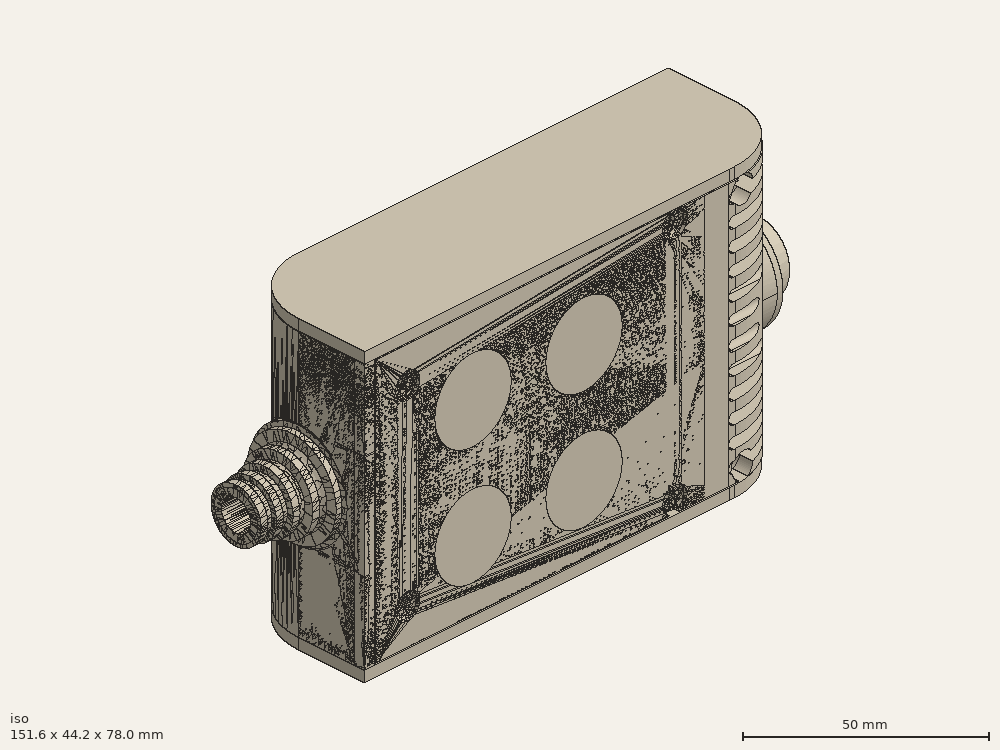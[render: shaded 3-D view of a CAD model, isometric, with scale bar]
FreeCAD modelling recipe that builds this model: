
FCSTD DOCUMENT  (FreeCAD 0.19R0.19.2)
Label: enclosure_194FCStd
License: All rights reserved
LicenseURL: http://en.wikipedia.org/wiki/All_rights_reserved
objects: Part::Revolution×152, Part::MultiFuse×146, Part::Feature×146, Sketcher::SketchObject×84, Part::Cut×70, Part::Cylinder×70, Part::Extrusion×67, Part::Fillet×58, Part::Box×36, App::MeasureDistance×4, PartDesign::Body×2, Image::ImagePlane×1
note: 831 computed .brp shape members not serialized (recipe doc carries the construction recipe); baked Part::Feature solids carry a one-line shape summary decoded from their .brp

FEATURE [Sketcher::SketchObject] Sketch  label="topSketch"
  FullyConstrained = true
  sketch-geometry (20):
    g0: LineSegment StartX=5.21097e-06 StartY=3 StartZ=0 EndX=5.21097e-06 EndY=19 EndZ=0
    g1: ArcOfCircle CenterX=19 CenterY=19 CenterZ=0 NormalX=0 NormalY=0 NormalZ=1 AngleXU=0 Radius=19 StartAngle=1.5708 EndAngle=3.14159
    g2: ArcOfCircle CenterX=19 CenterY=19 CenterZ=0 NormalX=0 NormalY=0 NormalZ=1 AngleXU=0 Radius=16 StartAngle=1.5708 EndAngle=3.14159
    g3: LineSegment StartX=114 StartY=35 StartZ=0 EndX=19 EndY=35 EndZ=0
    g4: LineSegment StartX=5.21097e-06 StartY=3 StartZ=0 EndX=5.21097e-06 EndY=0 EndZ=0
    g5: LineSegment StartX=3 StartY=0 StartZ=0 EndX=5.21097e-06 EndY=0 EndZ=0
    g6: LineSegment StartX=3 StartY=19 StartZ=0 EndX=3 EndY=0 EndZ=0
    g7: LineSegment StartX=19 StartY=38 StartZ=0 EndX=124 EndY=38 EndZ=0
    g8: Circle CenterX=119 CenterY=35 CenterZ=0 NormalX=0 NormalY=0 NormalZ=1 AngleXU=0 Radius=1
    g9: Circle CenterX=121 CenterY=35 CenterZ=0 NormalX=0 NormalY=0 NormalZ=1 AngleXU=0 Radius=1
    g10: Circle CenterX=121 CenterY=33 CenterZ=0 NormalX=0 NormalY=0 NormalZ=1 AngleXU=0 Radius=1
    g11: BSplineCurve PolesCount=3 KnotsCount=2 Degree=2 IsPeriodic=0
    g12: GeomPoint X=119 Y=35 Z=0
    g13: GeomPoint X=121 Y=33 Z=0
    g14: LineSegment StartX=119 StartY=35 StartZ=0 EndX=114 EndY=35 EndZ=0
    g15: ArcOfCircle CenterX=105 CenterY=19 CenterZ=0 NormalX=0 NormalY=0 NormalZ=1 AngleXU=0 Radius=19 StartAngle=5.7297 EndAngle=6.28319
    g16: ArcOfCircle CenterX=105 CenterY=19 CenterZ=0 NormalX=0 NormalY=0 NormalZ=1 AngleXU=0 Radius=16 StartAngle=5.60905 EndAngle=6.28319
    g17: LineSegment StartX=121 StartY=33 StartZ=0 EndX=121 EndY=19 EndZ=0
    g18: LineSegment StartX=124 StartY=38 StartZ=0 EndX=124 EndY=19 EndZ=0
    g19: LineSegment StartX=117.5 StartY=9.01251 StartZ=0 EndX=121.163 EndY=9.0125 EndZ=0
  constraints (46):
    c: Vertical(g0)
    c: Block(g0)
    c: Coincident(g1,g0)
    c: Block(g1)
    c: Coincident(g2,g1)
    c: Block(g2)
    c: Coincident(g3,g2)
    c: Horizontal(g3)
    c: Tangent(g3,g2)
    c: Coincident(g4,g0)
    c: Distance(g4) = 3
    c: Vertical(g4)
    c: Coincident(g5,g4)
    c: Horizontal(g5)
    c: Coincident(g6,g2)
    c: Coincident(g6,g5)
    c: Vertical(g6)
    c: Horizontal(g7)
    c: Distance(g7) = 105
    c: Coincident(g7,g1)
    c: Block(g3)
    c: Weight(g8) = 1
    c: Equal(g8,g9)
    c: Equal(g8,g10)
    c: InternalAlignment(g8,g11)
    c: InternalAlignment(g9,g11)
    c: InternalAlignment(g10,g11)
    c: InternalAlignment(g12,g11)
    c: InternalAlignment(g13,g11)
    c: Block(g11)
    c: Coincident(g14,g11)
    c: Coincident(g14,g3)
    c: Horizontal(g14)
    c: Block(g15)
    c: Coincident(g16,g15)
    c: Block(g16)
    c: Coincident(g17,g11)
    c: Coincident(g17,g16)
    c: Vertical(g17)
    c: Distance(g17) = 14
    c: Coincident(g18,g7)
    c: Coincident(g18,g15)
    c: Vertical(g18)
    c: Distance(g18) = 19
    c: Coincident(g19,g16)
    c: Coincident(g19,g15)
FEATURE [Sketcher::SketchObject] Sketch001  label="bottomSketch"
  FullyConstrained = true
  sketch-geometry (32):
    g0: LineSegment StartX=3.3 StartY=-6.03275e-07 StartZ=0 EndX=98 EndY=-6.03275e-07 EndZ=0
    g1: ArcOfCircle CenterX=98 CenterY=19 CenterZ=0 NormalX=0 NormalY=0 NormalZ=1 AngleXU=0 Radius=19 StartAngle=4.71239 EndAngle=5.71103
    g2: LineSegment StartX=6.3 StartY=8 StartZ=0 EndX=3.3 EndY=8 EndZ=0
    g3: LineSegment StartX=3.3 StartY=8 StartZ=0 EndX=3.3 EndY=-6.03275e-07 EndZ=0
    g4: ArcOfCircle CenterX=8.3 CenterY=5 CenterZ=0 NormalX=0 NormalY=0 NormalZ=1 AngleXU=0 Radius=2 StartAngle=3.14159 EndAngle=4.71239
    g5: LineSegment StartX=6.3 StartY=8 StartZ=0 EndX=6.3 EndY=5 EndZ=0
    g6: ArcOfCircle CenterX=98 CenterY=19 CenterZ=0 NormalX=0 NormalY=0 NormalZ=1 AngleXU=0 Radius=12.7 StartAngle=4.71239 EndAngle=6.28319
    g7: LineSegment StartX=94.7 StartY=3 StartZ=0 EndX=8.3 EndY=3 EndZ=0
    g8-g12: Circle x5 (B-spline internal-alignment scaffolding for g13; pole/knot coordinates omitted)
    g13: BSplineCurve PolesCount=5 KnotsCount=3 Degree=3 IsPeriodic=0
    g14: GeomPoint X=98 Y=6.3 Z=0
    g15: GeomPoint X=96.3938 Y=4.71946 Z=0
    g16: GeomPoint X=94.7 Y=3 Z=0
    g17-g23: Circle x7 (B-spline internal-alignment scaffolding for g24; pole/knot coordinates omitted)
    g24: BSplineCurve PolesCount=7 KnotsCount=5 Degree=3 IsPeriodic=0
    g25-g29: GeomPoint x5 (B-spline internal-alignment scaffolding for g24; pole/knot coordinates omitted)
    g30: ArcOfCircle CenterX=98 CenterY=19 CenterZ=0 NormalX=0 NormalY=0 NormalZ=1 AngleXU=0 Radius=15.7 StartAngle=5.81226 EndAngle=6.28319
    g31: LineSegment StartX=110.7 StartY=19 StartZ=0 EndX=113.7 EndY=19 EndZ=0
  constraints (41):
    c: Horizontal(g0)
    c: Coincident(g1,g0)
    c: Block(g1)
    c: Horizontal(g2)
    c: Distance(g2) = 3
    c: Coincident(g3,g2)
    c: Vertical(g3)
    c: Coincident(g3,g0)
    c: Block(g4)
    c: Block(g2)
    c: Coincident(g5,g2)
    c: Coincident(g5,g4)
    c: Vertical(g5)
    c: Coincident(g6,g1)
    c: Block(g6)
    c: Coincident(g7,g4)
    c: Horizontal(g7)
    c: Block(g0)
    c: Block(g7)
    c: Block(g3)
    c: Coincident(g13,g6)
    c: Weight(g8) = 1
    c: Equal(g8, g9-g12) x4
    c: Coincident(g13,g7)
    c: InternalAlignment(g8-g12 -> g13) x5
    c: InternalAlignment(g14,g13)
    c: InternalAlignment(g15,g13)
    c: InternalAlignment(g16,g13)
    c: Block(g13)
    c: Weight(g17) = 1
    c: Equal(g17, g18-g23) x6
    c: Coincident(g24,g1)
    c: InternalAlignment(g17-g23 -> g24) x7
    c: InternalAlignment(g25-g29 -> g24) x5
    c: Block(g24)
    c: Coincident(g30,g24)
    c: Coincident(g31,g6)
    c: Coincident(g31,g30)
    c: Horizontal(g31)
    c: Block(g31)
    c: Block(g30)
FEATURE [Part::Extrusion] Extrude  label="top"
  Base = -> Sketch
  Dir = (0,0,1)
  DirMode = 2
  FaceMakerClass = Part::FaceMakerBullseye
  LengthFwd = 72
  LengthRev = 0
  Solid = true
  Symmetric = false
FEATURE [Part::Extrusion] Extrude001  label="bottom"
  Base = -> Sketch001
  Dir = (0,0,1)
  DirMode = 2
  FaceMakerClass = Part::FaceMakerBullseye
  LengthFwd = 71.4
  LengthRev = 0
  Placement = pos=(0,0,0.3) rot=(0,0,1;0rad)
  Solid = true
  Symmetric = false
FEATURE [Sketcher::SketchObject] Sketch002  label="topSketch001"
  FullyConstrained = true
  sketch-geometry (8):
    g0: ArcOfCircle CenterX=19 CenterY=19.0975 CenterZ=0 NormalX=0 NormalY=0 NormalZ=1 AngleXU=0 Radius=18.9025 StartAngle=1.5708 EndAngle=3.14674
    g1: LineSegment StartX=0.0977805 StartY=19.0003 StartZ=0 EndX=0.0977805 EndY=0.000251602 EndZ=0
    g2: LineSegment StartX=19 StartY=38 StartZ=0 EndX=124 EndY=38 EndZ=0
    g3: LineSegment StartX=0.0977805 StartY=0.000251602 StartZ=0 EndX=105.098 EndY=0.000251602 EndZ=0
    g4: LineSegment StartX=124 StartY=38 StartZ=0 EndX=125.616 EndY=38 EndZ=0
    g5: LineSegment StartX=105.098 StartY=0.000251602 StartZ=0 EndX=106.713 EndY=0.000251602 EndZ=0
    g6: ArcOfCircle CenterX=106.616 CenterY=19 CenterZ=0 NormalX=0 NormalY=0 NormalZ=1 AngleXU=0 Radius=19 StartAngle=4.71754 EndAngle=6.28319
    g7: LineSegment StartX=125.616 StartY=38 StartZ=0 EndX=125.616 EndY=19 EndZ=0
  constraints (21):
    c: Block(g0)
    c: Coincident(g1,g0)
    c: Vertical(g1)
    c: Horizontal(g2)
    c: Distance(g2) = 105
    c: Coincident(g2,g0)
    c: Distance(g1) = 19
    c: Coincident(g3,g1)
    c: Horizontal(g3)
    c: Distance(g3) = 105
    c: Coincident(g4,g2)
    c: Horizontal(g4)
    c: Distance(g4) = 1.61553
    c: Horizontal(g5)
    c: Equal(g4,g5) = 1.61553
    c: Coincident(g5,g3)
    c: Block(g6)
    c: Coincident(g6,g5)
    c: Coincident(g7,g4)
    c: Coincident(g7,g6)
    c: Vertical(g7)
FEATURE [Part::Extrusion] Extrude002  label="sideA"
  Base = -> Sketch002
  Dir = (0,0,1)
  DirMode = 2
  FaceMakerClass = Part::FaceMakerBullseye
  LengthFwd = 3
  LengthRev = 0
  Placement = pos=(0,0,-3) rot=(0,0,1;0rad)
  Solid = true
  Symmetric = false
FEATURE [Sketcher::SketchObject] Sketch003  label="topSketch002"
  FullyConstrained = true
  sketch-geometry (6):
    g0: LineSegment StartX=19 StartY=38 StartZ=0 EndX=117 EndY=38 EndZ=0
    g1: ArcOfCircle CenterX=19 CenterY=19 CenterZ=0 NormalX=0 NormalY=0 NormalZ=1 AngleXU=0 Radius=19 StartAngle=1.5708 EndAngle=3.14159
    g2: LineSegment StartX=117 StartY=38 StartZ=0 EndX=117 EndY=19 EndZ=0
    g3: LineSegment StartX=98 StartY=1.0161e-12 StartZ=0 EndX=5.22862e-06 EndY=1.0161e-12 EndZ=0
    g4: LineSegment StartX=5.22862e-06 StartY=19 StartZ=0 EndX=5.22862e-06 EndY=1.0161e-12 EndZ=0
    g5: ArcOfCircle CenterX=98 CenterY=19 CenterZ=0 NormalX=0 NormalY=0 NormalZ=1 AngleXU=0 Radius=19 StartAngle=4.71239 EndAngle=6.28319
  constraints (16):
    c: Horizontal(g0)
    c: Distance(g0) = 98
    c: Coincident(g1,g0)
    c: Block(g1)
    c: Coincident(g2,g0)
    c: Vertical(g2)
    c: Distance(g2) = 19
    c: Horizontal(g3)
    c: Coincident(g4,g1)
    c: Vertical(g4)
    c: Coincident(g3,g4)
    c: Block(g3)
    c: Coincident(g5,g2)
    c: Coincident(g5,g3)
    c: Block(g0)
    c: Block(g5)
FEATURE [Sketcher::SketchObject] Sketch004
  FullyConstrained = true
  MapMode = 3
  Placement = pos=(0,0,0) rot=(1,0,0;1.5708rad)
  Support = -> [Extrude]
  sketch-geometry (8):
    g0: Circle CenterX=80.351 CenterY=-67.6202 CenterZ=0 NormalX=0 NormalY=0 NormalZ=1 AngleXU=0 Radius=2
    g1: Circle CenterX=80.351 CenterY=-67.6202 CenterZ=0 NormalX=0 NormalY=0 NormalZ=1 AngleXU=0 Radius=3
    g2: Circle CenterX=80.351 CenterY=-4.92017 CenterZ=0 NormalX=0 NormalY=0 NormalZ=1 AngleXU=0 Radius=2
    g3: Circle CenterX=80.351 CenterY=-4.92017 CenterZ=0 NormalX=0 NormalY=0 NormalZ=1 AngleXU=0 Radius=3
    g4: Circle CenterX=23.851 CenterY=-4.92017 CenterZ=0 NormalX=0 NormalY=0 NormalZ=1 AngleXU=0 Radius=2
    g5: Circle CenterX=23.851 CenterY=-4.92017 CenterZ=0 NormalX=0 NormalY=0 NormalZ=1 AngleXU=0 Radius=3
    g6: Circle CenterX=23.851 CenterY=-67.6202 CenterZ=0 NormalX=0 NormalY=0 NormalZ=1 AngleXU=0 Radius=2
    g7: Circle CenterX=23.851 CenterY=-67.6202 CenterZ=0 NormalX=0 NormalY=0 NormalZ=1 AngleXU=0 Radius=3
  constraints (8):
    c: Block(g3)
    c: Block(g2)
    c: Block(g1)
    c: Block(g0)
    c: Block(g6)
    c: Block(g7)
    c: Block(g4)
    c: Block(g5)
FEATURE [Part::Extrusion] Extrude004
  Base = -> Sketch004
  Dir = (0,-1,2e-16)
  DirMode = 2
  FaceMakerClass = Part::FaceMakerBullseye
  LengthFwd = 6
  LengthRev = 0
  Placement = pos=(0,9,0) rot=(0,0,1;0rad)
  Solid = true
  Symmetric = false
FEATURE [Sketcher::SketchObject] Sketch005
  FullyConstrained = true
  MapMode = 3
  Placement = pos=(0,0,0) rot=(1,0,0;1.5708rad)
  Support = -> [Extrude]
  sketch-geometry (8):
    g0: Circle CenterX=80.351 CenterY=-67.6202 CenterZ=0 NormalX=0 NormalY=0 NormalZ=1 AngleXU=0 Radius=3
    g1: Circle CenterX=80.351 CenterY=-4.92017 CenterZ=0 NormalX=0 NormalY=0 NormalZ=1 AngleXU=0 Radius=3
    g2: Circle CenterX=23.851 CenterY=-4.92017 CenterZ=0 NormalX=0 NormalY=0 NormalZ=1 AngleXU=0 Radius=3
    g3: Circle CenterX=23.851 CenterY=-67.6202 CenterZ=0 NormalX=0 NormalY=0 NormalZ=1 AngleXU=0 Radius=3
    g4: Circle CenterX=23.851 CenterY=-67.6202 CenterZ=0 NormalX=0 NormalY=0 NormalZ=1 AngleXU=0 Radius=5
    g5: Circle CenterX=80.351 CenterY=-67.6202 CenterZ=0 NormalX=0 NormalY=0 NormalZ=1 AngleXU=0 Radius=5
    g6: Circle CenterX=23.851 CenterY=-4.92017 CenterZ=0 NormalX=0 NormalY=0 NormalZ=1 AngleXU=0 Radius=5
    g7: Circle CenterX=80.351 CenterY=-4.92017 CenterZ=0 NormalX=0 NormalY=0 NormalZ=1 AngleXU=0 Radius=5
  constraints (8):
    c: Block(g1)
    c: Block(g0)
    c: Block(g3)
    c: Block(g2)
    c: Block(g5)
    c: Block(g4)
    c: Block(g6)
    c: Block(g7)
FEATURE [Part::Extrusion] Extrude005
  Base = -> Sketch005
  Dir = (0,-1,2e-16)
  DirMode = 2
  FaceMakerClass = Part::FaceMakerBullseye
  LengthFwd = 2
  LengthRev = 0
  Solid = true
  Symmetric = false
FEATURE [Sketcher::SketchObject] Sketch006
  FullyConstrained = true
  MapMode = 3
  Placement = pos=(0,0,0) rot=(1,0,0;1.5708rad)
  sketch-geometry (8):
    g0: Circle CenterX=80.351 CenterY=-67.6202 CenterZ=0 NormalX=0 NormalY=0 NormalZ=1 AngleXU=0 Radius=3
    g1: Circle CenterX=80.351 CenterY=-4.92017 CenterZ=0 NormalX=0 NormalY=0 NormalZ=1 AngleXU=0 Radius=3
    g2: Circle CenterX=23.851 CenterY=-4.92017 CenterZ=0 NormalX=0 NormalY=0 NormalZ=1 AngleXU=0 Radius=3
    g3: Circle CenterX=23.851 CenterY=-67.6202 CenterZ=0 NormalX=0 NormalY=0 NormalZ=1 AngleXU=0 Radius=3
    g4: Circle CenterX=23.851 CenterY=-67.6202 CenterZ=0 NormalX=0 NormalY=0 NormalZ=1 AngleXU=0 Radius=5
    g5: Circle CenterX=80.351 CenterY=-67.6202 CenterZ=0 NormalX=0 NormalY=0 NormalZ=1 AngleXU=0 Radius=5
    g6: Circle CenterX=23.851 CenterY=-4.92017 CenterZ=0 NormalX=0 NormalY=0 NormalZ=1 AngleXU=0 Radius=5
    g7: Circle CenterX=80.351 CenterY=-4.92017 CenterZ=0 NormalX=0 NormalY=0 NormalZ=1 AngleXU=0 Radius=5
  constraints (8):
    c: Block(g1)
    c: Block(g0)
    c: Block(g3)
    c: Block(g2)
    c: Block(g5)
    c: Block(g4)
    c: Block(g6)
    c: Block(g7)
FEATURE [Part::Extrusion] Extrude007
  Base = -> Sketch006
  Dir = (0,-1,2e-16)
  DirMode = 2
  FaceMakerClass = Part::FaceMakerBullseye
  LengthFwd = 2
  LengthRev = 0
  Solid = true
  Symmetric = false
FEATURE [Part::Fillet] Fillet
  Base = -> Extrude007
  Edges = 4 edges r=1.99: [Edge6,Edge12,Edge18,Edge24]
FEATURE [Part::Cut] Cut
  Base = -> Extrude005
  Placement = pos=(0,5,0) rot=(0,0,1;0rad)
  Tool = -> Fillet
FEATURE [Part::MultiFuse] Fusion  label="pCBScrews"
  Placement = pos=(-2.5,0,72.3) rot=(0,0,1;0rad)
  Shapes = -> [Extrude004,Cut]
FEATURE [App::MeasureDistance] Distance  label="Distance: 0.69 mm"
  Distance = 0.685967
  P1 = (24.0138,2.9647,0.3)
  P2 = (23.8901,3,-0.373787)
FEATURE [App::MeasureDistance] Distance001  label="Distance: 0.53 mm"
  Distance = 0.533607
  P1 = (80.2939,3,72.2334)
  P2 = (80.281,2.99661,71.7)
FEATURE [Part::Fillet] Fillet001
  Base = -> Extrude001
  Edges = 1 edges r=2.4: [Edge17]
FEATURE [Part::Fillet] Fillet002  label="bottom001"
  Base = -> Fillet001
  Edges = 1 edges r=2.4: [Edge36]
FEATURE [Part::Fillet] Fillet003  label="top001"
  Base = -> Extrude
  Edges = 1 edges r=2: [Edge1]
FEATURE [Sketcher::SketchObject] Sketch007
  FullyConstrained = true
  sketch-geometry (16):
    g0: LineSegment StartX=4 StartY=0 StartZ=0 EndX=4 EndY=2.4 EndZ=0
    g1: LineSegment StartX=4 StartY=2.4 StartZ=0 EndX=7 EndY=2.4 EndZ=0
    g2: LineSegment StartX=4 StartY=0 StartZ=0 EndX=5.7 EndY=0 EndZ=0
    g3: LineSegment StartX=5.7 StartY=0 StartZ=0 EndX=5.7 EndY=-5.6 EndZ=0
    g4-g8: Circle x5 (B-spline internal-alignment scaffolding for g9; pole/knot coordinates omitted)
    g9: BSplineCurve PolesCount=5 KnotsCount=3 Degree=3 IsPeriodic=0
    g10: GeomPoint X=7 Y=2.4 Z=0
    g11: GeomPoint X=10.4582 Y=-1.55472 Z=0
    g12: GeomPoint X=14 Y=-5.6 Z=0
    g13: LineSegment StartX=14 StartY=-5.6 StartZ=0 EndX=14 EndY=-14.1 EndZ=0
    g14: LineSegment StartX=14 StartY=-14.1 StartZ=0 EndX=6.5 EndY=-14.1 EndZ=0
    g15: LineSegment StartX=5.7 StartY=-5.6 StartZ=0 EndX=6.5 EndY=-14.1 EndZ=0
  constraints (28):
    c: Distance(g0) = 2.4
    c: Vertical(g0)
    c: Block(g0)
    c: Coincident(g1,g0)
    c: Horizontal(g1)
    c: Distance(g1) = 3
    c: Coincident(g2,g0)
    c: Horizontal(g2)
    c: Distance(g2) = 1.7
    c: Coincident(g3,g2)
    c: Vertical(g3)
    c: Distance(g3) = 5.6
    c: Coincident(g9,g1)
    c: Weight(g4) = 1
    c: Equal(g4, g5-g8) x4
    c: InternalAlignment(g4-g8 -> g9) x5
    c: InternalAlignment(g10,g9)
    c: InternalAlignment(g11,g9)
    c: InternalAlignment(g12,g9)
    c: Block(g9)
    c: Coincident(g13,g9)
    c: Vertical(g13)
    c: Distance(g13) = 8.5
    c: Coincident(g14,g13)
    c: Horizontal(g14)
    c: Distance(g14) = 7.5
    c: Coincident(g15,g3)
    c: Coincident(g15,g14)
FEATURE [Part::Feature] Face
  shape: bbox 10 x 16.5 x 2e-07 mm, 1 faces, 0 solids (baked)
FEATURE [Part::Revolution] Revolve  label="plugHousing"
  Angle = 360
  Axis = (0,1,0)
  Base = (0,0,0)
  FaceMakerClass = Part::FaceMakerBullseye
  Placement = pos=(0,0,36.15) rot=(0,0,1;0rad)
  Solid = false
  Source = -> Face
  Symmetric = false
FEATURE [Part::Feature] Face001
  shape: bbox 10 x 16.5 x 2e-07 mm, 1 faces, 0 solids (baked)
FEATURE [Part::Revolution] Revolve001  label="plugHousing001"
  Angle = 360
  Axis = (0,1,0)
  Base = (0,0,0)
  FaceMakerClass = Part::FaceMakerBullseye
  Placement = pos=(0,0,36.15) rot=(0,0,1;0rad)
  Solid = false
  Source = -> Face001
  Symmetric = false
FEATURE [Part::MultiFuse] Fusion001  label="plugHousing002"
  Placement = pos=(0,0,0) rot=(0,0,1;1.5708rad)
  Shapes = -> [Revolve001,Revolve]
FEATURE [Part::Feature] Face002
  shape: bbox 10 x 16.5 x 2e-07 mm, 1 faces, 0 solids (baked)
FEATURE [Part::Revolution] Revolve003  label="plugHousing005"
  Angle = 360
  Axis = (0,1,0)
  Base = (0,0,0)
  FaceMakerClass = Part::FaceMakerBullseye
  Placement = pos=(0,0,36.15) rot=(0,0,1;0rad)
  Solid = false
  Source = -> Face002
  Symmetric = false
FEATURE [Part::Feature] Face003
  shape: bbox 10 x 16.5 x 2e-07 mm, 1 faces, 0 solids (baked)
FEATURE [Part::Revolution] Revolve002  label="plugHousing003"
  Angle = 360
  Axis = (0,1,0)
  Base = (0,0,0)
  FaceMakerClass = Part::FaceMakerBullseye
  Placement = pos=(0,0,36.15) rot=(0,0,1;0rad)
  Solid = false
  Source = -> Face003
  Symmetric = false
FEATURE [Part::MultiFuse] Fusion002  label="plugHousing004"
  Placement = pos=(0,0,0) rot=(0,0,1;1.5708rad)
  Shapes = -> [Revolve002,Revolve003]
FEATURE [Part::MultiFuse] Fusion003  label="plugHousing006"
  Placement = pos=(0,19,0) rot=(0,0,1;3.14159rad)
  Shapes = -> [Fusion002,Fusion001]
FEATURE [Part::Feature] Face004
  shape: bbox 10 x 16.5 x 2e-07 mm, 1 faces, 0 solids (baked)
FEATURE [Part::Revolution] Revolve006  label="plugHousing010"
  Angle = 360
  Axis = (0,1,0)
  Base = (0,0,0)
  FaceMakerClass = Part::FaceMakerBullseye
  Placement = pos=(0,0,36.15) rot=(0,0,1;0rad)
  Solid = false
  Source = -> Face004
  Symmetric = false
FEATURE [Part::Feature] Face005
  shape: bbox 10 x 16.5 x 2e-07 mm, 1 faces, 0 solids (baked)
FEATURE [Part::Revolution] Revolve007  label="plugHousing011"
  Angle = 360
  Axis = (0,1,0)
  Base = (0,0,0)
  FaceMakerClass = Part::FaceMakerBullseye
  Placement = pos=(0,0,36.15) rot=(0,0,1;0rad)
  Solid = false
  Source = -> Face005
  Symmetric = false
FEATURE [Part::Feature] Face006
  shape: bbox 10 x 16.5 x 2e-07 mm, 1 faces, 0 solids (baked)
FEATURE [Part::Revolution] Revolve004  label="plugHousing007"
  Angle = 360
  Axis = (0,1,0)
  Base = (0,0,0)
  FaceMakerClass = Part::FaceMakerBullseye
  Placement = pos=(0,0,36.15) rot=(0,0,1;0rad)
  Solid = false
  Source = -> Face006
  Symmetric = false
FEATURE [Part::MultiFuse] Fusion004  label="plugHousing009"
  Placement = pos=(0,0,0) rot=(0,0,1;1.5708rad)
  Shapes = -> [Revolve004,Revolve007]
FEATURE [Part::Feature] Face007
  shape: bbox 10 x 16.5 x 2e-07 mm, 1 faces, 0 solids (baked)
FEATURE [Part::Revolution] Revolve005  label="plugHousing008"
  Angle = 360
  Axis = (0,1,0)
  Base = (0,0,0)
  FaceMakerClass = Part::FaceMakerBullseye
  Placement = pos=(0,0,36.15) rot=(0,0,1;0rad)
  Solid = false
  Source = -> Face007
  Symmetric = false
FEATURE [Part::MultiFuse] Fusion005  label="plugHousing012"
  Placement = pos=(0,0,0) rot=(0,0,1;1.5708rad)
  Shapes = -> [Revolve006,Revolve005]
FEATURE [Part::MultiFuse] Fusion006  label="plugHousing013"
  Placement = pos=(0,19,0) rot=(0,0,1;3.14159rad)
  Shapes = -> [Fusion005,Fusion004]
FEATURE [Part::MultiFuse] Fusion007  label="plugHousing014"
  Placement = pos=(122.621,0,-0.15) rot=(0,0,1;0rad)
  Shapes = -> [Fusion003,Fusion006]
FEATURE [Part::Cylinder] Cylinder002
  Angle = 360
  AttacherType = Attacher::AttachEngine3D
  Height = 20
  Placement = pos=(0,0,36.15) rot=(0,0,1;0rad)
  Radius = 4
FEATURE [Part::Cylinder] Cylinder003
  Angle = 360
  AttacherType = Attacher::AttachEngine3D
  Height = 10
  Placement = pos=(0,0,36.15) rot=(0,0,1;0rad)
  Radius = 4
FEATURE [Part::MultiFuse] Fusion009  label="removeToCreateHoleForPlugHousing"
  Placement = pos=(70,19,36.15) rot=(0,1,0;1.5708rad)
  Shapes = -> [Cylinder002,Cylinder003]
FEATURE [Part::Cylinder] Cylinder004
  Angle = 360
  AttacherType = Attacher::AttachEngine3D
  Height = 20
  Placement = pos=(0,0,36.15) rot=(0,0,1;0rad)
  Radius = 4
FEATURE [Part::Cylinder] Cylinder005
  Angle = 360
  AttacherType = Attacher::AttachEngine3D
  Height = 10
  Placement = pos=(0,0,36.15) rot=(0,0,1;0rad)
  Radius = 4
FEATURE [Part::MultiFuse] Fusion010  label="removeToCreateHoleForPlugHousing001"
  Placement = pos=(70,19,36.15) rot=(0,1,0;1.5708rad)
  Shapes = -> [Cylinder004,Cylinder005]
FEATURE [Part::Cut] Cut001
  Base = -> Fillet003
  Tool = -> Fusion010
FEATURE [Part::Cut] Cut002  label="Bottom"
  Base = -> Fillet002
  Tool = -> Fusion009
FEATURE [Part::Feature] Face008
  shape: bbox 10 x 16.5 x 2e-07 mm, 1 faces, 0 solids (baked)
FEATURE [Part::Revolution] Revolve011  label="plugHousing021"
  Angle = 360
  Axis = (0,1,0)
  Base = (0,0,0)
  FaceMakerClass = Part::FaceMakerBullseye
  Placement = pos=(0,0,36.15) rot=(0,0,1;0rad)
  Solid = false
  Source = -> Face008
  Symmetric = false
FEATURE [Part::Feature] Face009
  shape: bbox 10 x 16.5 x 2e-07 mm, 1 faces, 0 solids (baked)
FEATURE [Part::Revolution] Revolve012  label="plugHousing022"
  Angle = 360
  Axis = (0,1,0)
  Base = (0,0,0)
  FaceMakerClass = Part::FaceMakerBullseye
  Placement = pos=(0,0,36.15) rot=(0,0,1;0rad)
  Solid = false
  Source = -> Face009
  Symmetric = false
FEATURE [Part::Feature] Face010 .. Face013  x4 (patterned run collapsed; names and placements below)
  shape: bbox 10 x 16.5 x 2e-07 mm, 1 faces, 0 solids (baked)
FEATURE [Part::Revolution] Revolve015  label="plugHousing027"
  Angle = 360
  Axis = (0,1,0)
  Base = (0,0,0)
  FaceMakerClass = Part::FaceMakerBullseye
  Placement = pos=(0,0,36.15) rot=(0,0,1;0rad)
  Solid = false
  Source = -> Face013
  Symmetric = false
FEATURE [Part::Feature] Face014
  shape: bbox 10 x 16.5 x 2e-07 mm, 1 faces, 0 solids (baked)
FEATURE [Part::Feature] Face015
  shape: bbox 10 x 16.5 x 2e-07 mm, 1 faces, 0 solids (baked)
FEATURE [Part::Feature] Face016
  shape: bbox 10 x 16.5 x 2e-07 mm, 1 faces, 0 solids (baked)
FEATURE [Part::Revolution] Revolve019  label="plugHousing033"
  Angle = 360
  Axis = (0,1,0)
  Base = (0,0,0)
  FaceMakerClass = Part::FaceMakerBullseye
  Placement = pos=(0,0,36.15) rot=(0,0,1;0rad)
  Solid = false
  Source = -> Face016
  Symmetric = false
FEATURE [Part::Feature] Face017
  shape: bbox 10 x 16.5 x 2e-07 mm, 1 faces, 0 solids (baked)
FEATURE [Part::Revolution] Revolve020  label="plugHousing034"
  Angle = 360
  Axis = (0,1,0)
  Base = (0,0,0)
  FaceMakerClass = Part::FaceMakerBullseye
  Placement = pos=(0,0,36.15) rot=(0,0,1;0rad)
  Solid = false
  Source = -> Face017
  Symmetric = false
FEATURE [Part::Feature] Face018
  shape: bbox 10 x 16.5 x 2e-07 mm, 1 faces, 0 solids (baked)
FEATURE [Part::Revolution] Revolve016  label="plugHousing030"
  Angle = 360
  Axis = (0,1,0)
  Base = (0,0,0)
  FaceMakerClass = Part::FaceMakerBullseye
  Placement = pos=(0,0,36.15) rot=(0,0,1;0rad)
  Solid = false
  Source = -> Face018
  Symmetric = false
FEATURE [Part::MultiFuse] Fusion020  label="plugHousing038"
  Placement = pos=(0,0,0) rot=(0,0,1;1.5708rad)
  Shapes = -> [Revolve016,Revolve020]
FEATURE [Part::Feature] Face019
  shape: bbox 10 x 16.5 x 2e-07 mm, 1 faces, 0 solids (baked)
FEATURE [Part::Feature] Face020
  shape: bbox 10 x 16.5 x 2e-07 mm, 1 faces, 0 solids (baked)
FEATURE [Part::Revolution] Revolve017  label="plugHousing031"
  Angle = 360
  Axis = (0,1,0)
  Base = (0,0,0)
  FaceMakerClass = Part::FaceMakerBullseye
  Placement = pos=(0,0,36.15) rot=(0,0,1;0rad)
  Solid = false
  Source = -> Face020
  Symmetric = false
FEATURE [Part::MultiFuse] Fusion021  label="plugHousing039"
  Placement = pos=(0,0,0) rot=(0,0,1;1.5708rad)
  Shapes = -> [Revolve019,Revolve017]
FEATURE [Part::MultiFuse] Fusion023  label="plugHousing041"
  Placement = pos=(0,19,0) rot=(0,0,1;3.14159rad)
  Shapes = -> [Fusion021,Fusion020]
FEATURE [Part::Revolution] Revolve022  label="plugHousing043"
  Angle = 360
  Axis = (0,1,0)
  Base = (0,0,0)
  FaceMakerClass = Part::FaceMakerBullseye
  Placement = pos=(0,0,36.15) rot=(0,0,1;0rad)
  Solid = false
  Source = -> Face019
  Symmetric = false
FEATURE [Part::Feature] Face021
  shape: bbox 10 x 16.5 x 2e-07 mm, 1 faces, 0 solids (baked)
FEATURE [Part::Revolution] Revolve023  label="plugHousing044"
  Angle = 360
  Axis = (0,1,0)
  Base = (0,0,0)
  FaceMakerClass = Part::FaceMakerBullseye
  Placement = pos=(0,0,36.15) rot=(0,0,1;0rad)
  Solid = false
  Source = -> Face021
  Symmetric = false
FEATURE [Part::Feature] Face022
  shape: bbox 10 x 16.5 x 2e-07 mm, 1 faces, 0 solids (baked)
FEATURE [Part::Revolution] Revolve018  label="plugHousing032"
  Angle = 360
  Axis = (0,1,0)
  Base = (0,0,0)
  FaceMakerClass = Part::FaceMakerBullseye
  Placement = pos=(0,0,36.15) rot=(0,0,1;0rad)
  Solid = false
  Source = -> Face022
  Symmetric = false
FEATURE [Part::MultiFuse] Fusion022  label="plugHousing040"
  Placement = pos=(0,0,0) rot=(0,0,1;1.5708rad)
  Shapes = -> [Revolve018,Revolve023]
FEATURE [Part::Feature] Face023
  shape: bbox 10 x 16.5 x 2e-07 mm, 1 faces, 0 solids (baked)
FEATURE [Part::Revolution] Revolve021  label="plugHousing035"
  Angle = 360
  Axis = (0,1,0)
  Base = (0,0,0)
  FaceMakerClass = Part::FaceMakerBullseye
  Placement = pos=(0,0,36.15) rot=(0,0,1;0rad)
  Solid = false
  Source = -> Face023
  Symmetric = false
FEATURE [Part::MultiFuse] Fusion018  label="plugHousing036"
  Placement = pos=(0,0,0) rot=(0,0,1;1.5708rad)
  Shapes = -> [Revolve022,Revolve021]
FEATURE [Part::MultiFuse] Fusion019  label="plugHousing037"
  Placement = pos=(0,19,0) rot=(0,0,1;3.14159rad)
  Shapes = -> [Fusion018,Fusion022]
FEATURE [Part::MultiFuse] Fusion024  label="plugHousing042"
  Placement = pos=(122.621,0,-0.15) rot=(0,0,1;0rad)
  Shapes = -> [Fusion023,Fusion019]
FEATURE [Part::Cylinder] Cylinder006
  Angle = 360
  AttacherType = Attacher::AttachEngine3D
  Height = 20
  Placement = pos=(0,0,36.15) rot=(0,0,1;0rad)
  Radius = 14.3
FEATURE [Part::Cylinder] Cylinder007
  Angle = 360
  AttacherType = Attacher::AttachEngine3D
  Height = 10
  Placement = pos=(0,0,36.15) rot=(0,0,1;0rad)
  Radius = 4
FEATURE [Part::MultiFuse] Fusion026  label="removeToCreteHoleForPlugHousing"
  Placement = pos=(70,19,36) rot=(0,1,0;1.5708rad)
  Shapes = -> [Cylinder006,Cylinder007]
FEATURE [Part::Box] Box001  label="Cube001"
  AttacherType = Attacher::AttachEngine3D
  Height = 28
  Length = 3
  Placement = pos=(110.7,19,22) rot=(0,0,1;0rad)
  Width = 15.7
FEATURE [Part::Cut] Cut003  label="top002"
  Base = -> Cut001
  Tool = -> Fusion007
FEATURE [Part::Revolution] Revolve008  label="plugHousing015"
  Angle = 360
  Axis = (0,1,0)
  Base = (0,0,0)
  FaceMakerClass = Part::FaceMakerBullseye
  Placement = pos=(0,0,36.15) rot=(0,0,1;0rad)
  Solid = false
  Source = -> Face010
  Symmetric = false
FEATURE [Part::MultiFuse] Fusion013  label="plugHousing020"
  Placement = pos=(0,0,0) rot=(0,0,1;1.5708rad)
  Shapes = -> [Revolve008,Revolve012]
FEATURE [Part::Cut] Cut004  label="top003"
  Base = -> Cut003
  Placement = pos=(1,0,0) rot=(0,0,1;0rad)
  Tool = -> Fusion026
FEATURE [Part::Cylinder] Cylinder008
  Angle = 360
  AttacherType = Attacher::AttachEngine3D
  Height = 20
  Placement = pos=(0,0,36.15) rot=(0,0,1;0rad)
  Radius = 10.3
FEATURE [Part::Cylinder] Cylinder009
  Angle = 360
  AttacherType = Attacher::AttachEngine3D
  Height = 10
  Placement = pos=(0,0,36.15) rot=(0,0,1;0rad)
  Radius = 4
FEATURE [Part::MultiFuse] Fusion027  label="removeToCreteHoleForPlugHousing001"
  Placement = pos=(70,19,36) rot=(0,1,0;1.5708rad)
  Shapes = -> [Cylinder008,Cylinder009]
FEATURE [Part::Cut] Cut005  label="plugHousingTab"
  Base = -> Box001
  Tool = -> Fusion027
FEATURE [Part::MultiFuse] Fusion028  label="plugHousing045"
  Shapes = -> [Fusion024,Cut005]
FEATURE [Part::Box] Box002  label="Cube002"
  AttacherType = Attacher::AttachEngine3D
  Height = 28.8
  Length = 3
  Placement = pos=(107.3,28,21.6) rot=(0,0,1;0rad)
  Width = 7
FEATURE [Part::Box] Box003  label="Cube003"
  AttacherType = Attacher::AttachEngine3D
  Height = 3
  Length = 6.4
  Placement = pos=(107.3,28,18.6) rot=(0,0,1;0rad)
  Width = 7
FEATURE [Part::Box] Box004  label="Cube004"
  AttacherType = Attacher::AttachEngine3D
  Height = 3
  Length = 6.4
  Placement = pos=(107.3,28,50.4) rot=(0,0,1;0rad)
  Width = 7
FEATURE [Part::MultiFuse] Fusion029  label="plugHousingBracketHolder"
  Shapes = -> [Box004,Box002,Box003]
FEATURE [Part::Cylinder] Cylinder010
  Angle = 360
  AttacherType = Attacher::AttachEngine3D
  Height = 20
  Placement = pos=(0,0,36.15) rot=(0,0,1;0rad)
  Radius = 14.3
FEATURE [Part::Cylinder] Cylinder011
  Angle = 360
  AttacherType = Attacher::AttachEngine3D
  Height = 10
  Placement = pos=(0,0,36.15) rot=(0,0,1;0rad)
  Radius = 4
FEATURE [Part::MultiFuse] Fusion030  label="removeToCreteHoleForPlugHousing002"
  Placement = pos=(70,19,36) rot=(0,1,0;1.5708rad)
  Shapes = -> [Cylinder010,Cylinder011]
FEATURE [Part::Cut] Cut006  label="plugHousingBracketHolder001"
  Base = -> Fusion029
  Tool = -> Fusion030
FEATURE [Part::Cylinder] Cylinder012
  Angle = 360
  AttacherType = Attacher::AttachEngine3D
  Height = 20
  Placement = pos=(0,0,36.15) rot=(0,0,1;0rad)
  Radius = 7
FEATURE [Part::Cylinder] Cylinder013
  Angle = 360
  AttacherType = Attacher::AttachEngine3D
  Height = 10
  Placement = pos=(0,0,36.15) rot=(0,0,1;0rad)
  Radius = 4
FEATURE [Part::MultiFuse] Fusion032  label="removeToCreteHoleForPlugHousing003"
  Placement = pos=(70,19,36) rot=(0,1,0;1.5708rad)
  Shapes = -> [Cylinder012,Cylinder013]
FEATURE [Part::Cut] Cut007  label="bottom002"
  Base = -> Cut002
  Tool = -> Fusion032
FEATURE [Sketcher::SketchObject] Sketch008
  FullyConstrained = true
  sketch-geometry (54):
    g0: LineSegment StartX=-4.2 StartY=0 StartZ=0 EndX=-6.2 EndY=0 EndZ=0
    g1: LineSegment StartX=-14 StartY=-18 StartZ=0 EndX=-14 EndY=-26.5 EndZ=0
    g2: LineSegment StartX=-4.2 StartY=0 StartZ=0 EndX=-4.2 EndY=-13.4877 EndZ=0
    g3: Circle CenterX=-4.2 CenterY=-13.4877 CenterZ=0 NormalX=0 NormalY=0 NormalZ=1 AngleXU=0 Radius=1
    g4: Circle CenterX=-4.2 CenterY=-26.5 CenterZ=0 NormalX=0 NormalY=0 NormalZ=1 AngleXU=0 Radius=1
    g5: Circle CenterX=-8.2 CenterY=-26.5 CenterZ=0 NormalX=0 NormalY=0 NormalZ=1 AngleXU=0 Radius=1
    g6: BSplineCurve PolesCount=3 KnotsCount=2 Degree=2 IsPeriodic=0
    g7: GeomPoint X=-4.2 Y=-13.4877 Z=0
    g8: GeomPoint X=-8.2 Y=-26.5 Z=0
    g9: LineSegment StartX=-14 StartY=-26.5 StartZ=0 EndX=-8.2 EndY=-26.5 EndZ=0
    g10: LineSegment StartX=-10.15 StartY=-12 StartZ=0 EndX=-10.15 EndY=-14 EndZ=0
    g11: LineSegment StartX=-12.8401 StartY=-16 StartZ=0 EndX=-10.1571 EndY=-16 EndZ=0
    g12: LineSegment StartX=-10.15 StartY=-14 StartZ=0 EndX=-8.70761 EndY=-14 EndZ=0
    g13: LineSegment StartX=-12.8401 StartY=-16 StartZ=0 EndX=-12.8401 EndY=-17.6958 EndZ=0
    g14: LineSegment StartX=-10.15 StartY=-12 StartZ=0 EndX=-7.79258 EndY=-12 EndZ=0
    g15: Circle CenterX=-6.2215 CenterY=-2 CenterZ=0 NormalX=0 NormalY=0 NormalZ=1 AngleXU=0 Radius=1
    g16: Circle CenterX=-6.22762 CenterY=-2.58724 CenterZ=0 NormalX=0 NormalY=0 NormalZ=1 AngleXU=0 Radius=1
    g17: Circle CenterX=-6.32538 CenterY=-4 CenterZ=0 NormalX=0 NormalY=0 NormalZ=1 AngleXU=0 Radius=1
    g18: BSplineCurve PolesCount=3 KnotsCount=2 Degree=2 IsPeriodic=0
    g19: GeomPoint X=-6.2215 Y=-2 Z=0
    g20: GeomPoint X=-6.32538 Y=-4 Z=0
    g21: Circle CenterX=-6.48644 CenterY=-5.99526 CenterZ=0 NormalX=0 NormalY=0 NormalZ=1 AngleXU=0 Radius=1
    g22: Circle CenterX=-6.58486 CenterY=-6.99526 CenterZ=0 NormalX=0 NormalY=0 NormalZ=1 AngleXU=0 Radius=1
    g23: Circle CenterX=-6.77343 CenterY=-8 CenterZ=0 NormalX=0 NormalY=0 NormalZ=1 AngleXU=0 Radius=1
    g24: BSplineCurve PolesCount=3 KnotsCount=2 Degree=2 IsPeriodic=0
    g25: GeomPoint X=-6.48644 Y=-5.99526 Z=0
    g26: GeomPoint X=-6.77343 Y=-8 Z=0
    g27: Circle CenterX=-7.19003 CenterY=-10 CenterZ=0 NormalX=0 NormalY=0 NormalZ=1 AngleXU=0 Radius=1
    g28: Circle CenterX=-7.44407 CenterY=-11.0915 CenterZ=0 NormalX=0 NormalY=0 NormalZ=1 AngleXU=0 Radius=1
    g29: Circle CenterX=-7.79258 CenterY=-12 CenterZ=0 NormalX=0 NormalY=0 NormalZ=1 AngleXU=0 Radius=1
    g30: BSplineCurve PolesCount=3 KnotsCount=2 Degree=2 IsPeriodic=0
    g31: GeomPoint X=-7.19003 Y=-10 Z=0
    g32: GeomPoint X=-7.79258 Y=-12 Z=0
    g33: Circle CenterX=-8.70761 CenterY=-14 CenterZ=0 NormalX=0 NormalY=0 NormalZ=1 AngleXU=0 Radius=1
    g34: Circle CenterX=-9.33087 CenterY=-15.1837 CenterZ=0 NormalX=0 NormalY=0 NormalZ=1 AngleXU=0 Radius=1
    g35: Circle CenterX=-10.1571 CenterY=-16 CenterZ=0 NormalX=0 NormalY=0 NormalZ=1 AngleXU=0 Radius=1
    g36: BSplineCurve PolesCount=3 KnotsCount=2 Degree=2 IsPeriodic=0
    g37: GeomPoint X=-8.70761 Y=-14 Z=0
    g38: GeomPoint X=-10.1571 Y=-16 Z=0
    g39: Circle CenterX=-12.8401 CenterY=-17.6958 CenterZ=0 NormalX=0 NormalY=0 NormalZ=1 AngleXU=0 Radius=1
    g40: Circle CenterX=-13.3521 CenterY=-17.9027 CenterZ=0 NormalX=0 NormalY=0 NormalZ=1 AngleXU=0 Radius=1
    g41: Circle CenterX=-14 CenterY=-18 CenterZ=0 NormalX=0 NormalY=0 NormalZ=1 AngleXU=0 Radius=1
    g42: BSplineCurve PolesCount=3 KnotsCount=2 Degree=2 IsPeriodic=0
    g43: GeomPoint X=-12.8401 Y=-17.6958 Z=0
    g44: GeomPoint X=-14 Y=-18 Z=0
    g45: LineSegment StartX=-6.2 StartY=0 StartZ=0 EndX=-7.2 EndY=0 EndZ=0
    g46: LineSegment StartX=-7.2 StartY=0 StartZ=0 EndX=-7.2 EndY=-2 EndZ=0
    g47: LineSegment StartX=-7.2 StartY=-2 StartZ=0 EndX=-6.2215 EndY=-2 EndZ=0
    g48: LineSegment StartX=-6.32538 StartY=-4 StartZ=0 EndX=-7.65538 EndY=-4 EndZ=0
    g49: LineSegment StartX=-7.65538 StartY=-4 StartZ=0 EndX=-7.65538 EndY=-5.99526 EndZ=0
    g50: LineSegment StartX=-7.65538 StartY=-5.99526 StartZ=0 EndX=-6.48644 EndY=-5.99526 EndZ=0
    g51: LineSegment StartX=-6.77343 StartY=-8 StartZ=0 EndX=-8.43343 EndY=-8 EndZ=0
    g52: LineSegment StartX=-8.43343 StartY=-8 StartZ=0 EndX=-8.43343 EndY=-10 EndZ=0
    g53: LineSegment StartX=-8.43343 StartY=-10 StartZ=0 EndX=-7.19003 EndY=-10 EndZ=0
  constraints (112):
    c: Horizontal(g0)
    c: Distance(g0) = 2
    c: Block(g0)
    c: Vertical(g1)
    c: Coincident(g2,g0)
    c: Vertical(g2)
    c: Block(g2)
    c: Coincident(g6,g2)
    c: Weight(g3) = 1
    c: Equal(g3,g4)
    c: Equal(g3,g5)
    c: InternalAlignment(g3,g6)
    c: InternalAlignment(g4,g6)
    c: InternalAlignment(g5,g6)
    c: InternalAlignment(g7,g6)
    c: InternalAlignment(g8,g6)
    c: Block(g6)
    c: Coincident(g9,g1)
    c: Coincident(g9,g6)
    c: Horizontal(g9)
    c: Vertical(g10)
    c: Block(g10)
    c: Horizontal(g11)
    c: Block(g11)
    c: Coincident(g12,g10)
    c: Horizontal(g12)
    c: Block(g12)
    c: Coincident(g13,g11)
    c: Vertical(g13)
    c: Block(g13)
    c: Coincident(g14,g10)
    c: Horizontal(g14)
    c: Block(g14)
    c: Block(g9)
    c: Block(g1)
    c: Weight(g15) = 1
    c: Equal(g15,g16)
    c: Equal(g15,g17)
    c: InternalAlignment(g15,g18)
    c: InternalAlignment(g16,g18)
    c: InternalAlignment(g17,g18)
    c: InternalAlignment(g19,g18)
    c: InternalAlignment(g20,g18)
    c: Weight(g21) = 1
    c: Equal(g21,g22)
    c: Equal(g21,g23)
    c: InternalAlignment(g21,g24)
    c: InternalAlignment(g22,g24)
    c: InternalAlignment(g23,g24)
    c: InternalAlignment(g25,g24)
    c: InternalAlignment(g26,g24)
    c: Weight(g27) = 1
    c: Equal(g27,g28)
    c: Equal(g27,g29)
    c: Coincident(g30,g14)
    c: InternalAlignment(g27,g30)
    c: InternalAlignment(g28,g30)
    c: InternalAlignment(g29,g30)
    c: InternalAlignment(g31,g30)
    c: InternalAlignment(g32,g30)
    c: Coincident(g36,g12)
    c: Weight(g33) = 1
    c: Equal(g33,g34)
    c: Equal(g33,g35)
    c: Coincident(g36,g11)
    c: InternalAlignment(g33,g36)
    c: InternalAlignment(g34,g36)
    c: InternalAlignment(g35,g36)
    c: InternalAlignment(g37,g36)
    c: InternalAlignment(g38,g36)
    c: Coincident(g42,g13)
    c: Weight(g39) = 1
    c: Equal(g39,g40)
    c: Equal(g39,g41)
    c: Coincident(g42,g1)
    c: InternalAlignment(g39,g42)
    c: InternalAlignment(g40,g42)
    c: InternalAlignment(g41,g42)
    c: InternalAlignment(g43,g42)
    c: InternalAlignment(g44,g42)
    c: Block(g18)
    c: Block(g24)
    c: Block(g30)
    c: Block(g36)
    c: Block(g42)
    c: Horizontal(g45)
    c: Coincident(g45,g0)
    c: Vertical(g46)
    c: Coincident(g46,g45)
    c: Coincident(g47,g46)
    c: Coincident(g47,g18)
    c: Horizontal(g47)
    c: Block(g46)
    c: Coincident(g48,g18)
    c: Horizontal(g48)
    c: Distance(g48) = 1.33
    c: Vertical(g49)
    c: Coincident(g49,g48)
    c: Coincident(g50,g49)
    c: Coincident(g50,g24)
    c: Horizontal(g50)
    c: Tangent(g50,g22)
    c: Horizontal(g51)
    c: Coincident(g51,g24)
    c: Block(g51)
    c: Vertical(g52)
    c: Block(g52)
    c: Coincident(g52,g51)
    c: Coincident(g53,g52)
    c: Coincident(g53,g30)
    c: Horizontal(g53)
    c: Distance(g1) = 8.5
FEATURE [Part::Feature] Face024
  shape: bbox 9.8 x 26.5 x 2e-07 mm, 1 faces, 0 solids (baked)
FEATURE [Part::Revolution] Revolve024
  Angle = 360
  Axis = (0,1,0)
  Base = (0,0,0)
  FaceMakerClass = Part::FaceMakerBullseye
  Placement = pos=(0,0,0) rot=(0,0,1;1.5708rad)
  Solid = false
  Source = -> Face024
  Symmetric = false
FEATURE [Part::Feature] Face025
  shape: bbox 9.8 x 26.5 x 2e-07 mm, 1 faces, 0 solids (baked)
FEATURE [Part::Revolution] Revolve025
  Angle = 360
  Axis = (0,1,0)
  Base = (0,0,0)
  FaceMakerClass = Part::FaceMakerBullseye
  Placement = pos=(0,0,0) rot=(0,0,1;1.5708rad)
  Solid = false
  Source = -> Face025
  Symmetric = false
FEATURE [Part::MultiFuse] Fusion033
  Placement = pos=(-18,19,36) rot=(0,0,1;0rad)
  Shapes = -> [Revolve025,Revolve024]
FEATURE [Part::Cylinder] Cylinder014
  Angle = 360
  AttacherType = Attacher::AttachEngine3D
  Height = 20
  Placement = pos=(0,0,36.15) rot=(0,0,1;0rad)
  Radius = 14.3
FEATURE [Part::Cylinder] Cylinder015
  Angle = 360
  AttacherType = Attacher::AttachEngine3D
  Height = 10
  Placement = pos=(0,0,36.15) rot=(0,0,1;0rad)
  Radius = 4
FEATURE [Part::MultiFuse] Fusion034  label="removeToCreteHoleForPlugHousing004"
  Placement = pos=(-42,19,36) rot=(0,1,0;1.5708rad)
  Shapes = -> [Cylinder014,Cylinder015]
FEATURE [Part::Cut] Cut008  label="top004"
  Base = -> Cut004
  Placement = pos=(-1,0,0) rot=(0,0,1;0rad)
  Tool = -> Fusion034
FEATURE [Part::Box] Box005  label="Cube005"
  AttacherType = Attacher::AttachEngine3D
  Height = 28
  Length = 3
  Placement = pos=(110.7,19,22) rot=(0,0,1;0rad)
  Width = 15.7
FEATURE [Part::Cylinder] Cylinder016
  Angle = 360
  AttacherType = Attacher::AttachEngine3D
  Height = 10
  Placement = pos=(0,0,36.15) rot=(0,0,1;0rad)
  Radius = 4
FEATURE [Part::Cylinder] Cylinder017
  Angle = 360
  AttacherType = Attacher::AttachEngine3D
  Height = 20
  Placement = pos=(0,0,36.15) rot=(0,0,1;0rad)
  Radius = 10.3
FEATURE [Part::MultiFuse] Fusion035  label="removeToCreteHoleForPlugHousing005"
  Placement = pos=(70,19,36) rot=(0,1,0;1.5708rad)
  Shapes = -> [Cylinder017,Cylinder016]
FEATURE [Part::Cut] Cut009  label="plugHousingTab001"
  Base = -> Box005
  Placement = pos=(-107.4,-14,0) rot=(0,0,1;0rad)
  Tool = -> Fusion035
FEATURE [Part::Box] Box006  label="Cube006"
  AttacherType = Attacher::AttachEngine3D
  Height = 28
  Length = 3
  Placement = pos=(110.7,19,22) rot=(0,0,1;0rad)
  Width = 15.7
FEATURE [Part::Cylinder] Cylinder018
  Angle = 360
  AttacherType = Attacher::AttachEngine3D
  Height = 10
  Placement = pos=(0,0,36.15) rot=(0,0,1;0rad)
  Radius = 4
FEATURE [Part::Cylinder] Cylinder019
  Angle = 360
  AttacherType = Attacher::AttachEngine3D
  Height = 20
  Placement = pos=(0,0,36.15) rot=(0,0,1;0rad)
  Radius = 10.3
FEATURE [Part::MultiFuse] Fusion036  label="removeToCreteHoleForPlugHousing006"
  Placement = pos=(70,19,36) rot=(0,1,0;1.5708rad)
  Shapes = -> [Cylinder019,Cylinder018]
FEATURE [Part::Cut] Cut010  label="plugHousingTab002"
  Base = -> Box006
  Placement = pos=(-107.4,-14,0) rot=(0,0,1;0rad)
  Tool = -> Fusion036
FEATURE [Part::MultiFuse] Fusion037
  Placement = pos=(9.6,23,0) rot=(0,0,1;3.14159rad)
  Shapes = -> [Cut009,Cut010]
FEATURE [Part::Box] Box  label="Cube"
  AttacherType = Attacher::AttachEngine3D
  Height = 10
  Length = 3
  Placement = pos=(3.3,4,12) rot=(0,0,1;0rad)
  Width = 10
FEATURE [Part::Fillet] Fillet004
  Base = -> Fusion028
  Edges = 1 edges r=2: [Edge25]
FEATURE [Part::Fillet] Fillet005  label="plugHousing046"
  Base = -> Fillet004
  Edges = 1 edges r=2: [Edge8]
FEATURE [Part::Fillet] Fillet006
  Base = -> Box
  Edges = 1 edges r=2: [Edge11]
FEATURE [Part::Box] Box007  label="Cube007"
  AttacherType = Attacher::AttachEngine3D
  Height = 10
  Length = 3
  Placement = pos=(3.3,4,50) rot=(0,0,1;0rad)
  Width = 10
FEATURE [Part::Fillet] Fillet007
  Base = -> Box007
  Edges = 1 edges r=2: [Edge12]
FEATURE [Part::Box] Box008  label="Cube008"
  AttacherType = Attacher::AttachEngine3D
  Height = 28
  Length = 4
  Placement = pos=(5,0,22) rot=(0,0,1;0rad)
  Width = 10
FEATURE [Part::Fillet] Fillet008
  Base = -> Box008
  Edges = 1 edges r=1: [Edge7]
FEATURE [Part::Fillet] Fillet009
  Base = -> Fillet008
  Edges = 1 edges r=2: [Edge5]
FEATURE [Part::Fillet] Fillet010
  Base = -> Fillet009
  Edges = 1 edges r=2: [Edge2]
FEATURE [Sketcher::SketchObject] Sketch009  label="topSketch003"
  FullyConstrained = true
  sketch-geometry (4):
    g0: LineSegment StartX=16.8446 StartY=31.512 StartZ=0 EndX=16.3251 EndY=34.4666 EndZ=0
    g1: ArcOfCircle CenterX=19 CenterY=19.2524 CenterZ=0 NormalX=0 NormalY=0 NormalZ=1 AngleXU=0 Radius=15.4476 StartAngle=1.74483 EndAngle=2.72717
    g2: ArcOfCircle CenterX=19 CenterY=19.2524 CenterZ=0 NormalX=0 NormalY=0 NormalZ=1 AngleXU=0 Radius=12.4476 StartAngle=1.74483 EndAngle=2.73189
    g3: LineSegment StartX=4.86004 StartY=25.4725 StartZ=0 EndX=7.58253 EndY=24.2107 EndZ=0
  constraints (7):
    c: Block(g0)
    c: Coincident(g1,g0)
    c: Coincident(g2,g0)
    c: Coincident(g3,g1)
    c: Coincident(g3,g2)
    c: Block(g1)
    c: Block(g2)
FEATURE [Part::Extrusion] Extrude008
  Base = -> Sketch009
  Dir = (0,0,1)
  DirMode = 2
  FaceMakerClass = Part::FaceMakerBullseye
  LengthFwd = 10
  LengthRev = 0
  Placement = pos=(0,0,31) rot=(0,0,1;0rad)
  Solid = true
  Symmetric = false
FEATURE [Part::Cylinder] Cylinder020
  Angle = 360
  AttacherType = Attacher::AttachEngine3D
  Height = 20
  Placement = pos=(0,0,36.15) rot=(0,0,1;0rad)
  Radius = 8.2
FEATURE [Part::Cylinder] Cylinder021
  Angle = 360
  AttacherType = Attacher::AttachEngine3D
  Height = 10
  Placement = pos=(0,0,36.15) rot=(0,0,1;0rad)
  Radius = 4
FEATURE [Part::MultiFuse] Fusion038  label="removeToCreteHoleForPlugHousing007"
  Placement = pos=(-42,19,36) rot=(0,1,0;1.5708rad)
  Shapes = -> [Cylinder020,Cylinder021]
FEATURE [Part::Cut] Cut011
  Base = -> Extrude008
  Tool = -> Fusion038
FEATURE [Part::Fillet] Fillet011
  Base = -> Cut011
  Edges = 1 edges r=2: [Edge1]
FEATURE [Part::Fillet] Fillet012
  Base = -> Fillet011
  Edges = 1 edges r=2.5: [Edge1]
FEATURE [Part::Fillet] Fillet013
  Base = -> Fillet012
  Edges = 1 edges r=2.5: [Edge2]
FEATURE [Part::Box] Box010  label="Cube010"
  AttacherType = Attacher::AttachEngine3D
  Height = 16
  Length = 8
  Placement = pos=(12.7,31.52,28) rot=(0,0,1;0rad)
  Width = 4
FEATURE [Sketcher::SketchObject] Sketch010  label="topSketch004"
  FullyConstrained = true
  sketch-geometry (4):
    g0: LineSegment StartX=16.8446 StartY=31.512 StartZ=0 EndX=16.3251 EndY=34.4666 EndZ=0
    g1: ArcOfCircle CenterX=19 CenterY=19.2524 CenterZ=0 NormalX=0 NormalY=0 NormalZ=1 AngleXU=0 Radius=15.4476 StartAngle=1.74483 EndAngle=2.72717
    g2: ArcOfCircle CenterX=19 CenterY=19.2524 CenterZ=0 NormalX=0 NormalY=0 NormalZ=1 AngleXU=0 Radius=12.4476 StartAngle=1.74483 EndAngle=2.73189
    g3: LineSegment StartX=4.86004 StartY=25.4725 StartZ=0 EndX=7.58253 EndY=24.2107 EndZ=0
  constraints (7):
    c: Block(g0)
    c: Coincident(g1,g0)
    c: Coincident(g2,g0)
    c: Coincident(g3,g1)
    c: Coincident(g3,g2)
    c: Block(g1)
    c: Block(g2)
FEATURE [Part::Cylinder] Cylinder022
  Angle = 360
  AttacherType = Attacher::AttachEngine3D
  Height = 10
  Placement = pos=(0,0,36.15) rot=(0,0,1;0rad)
  Radius = 4
FEATURE [Sketcher::SketchObject] Sketch011  label="topSketch005"
  FullyConstrained = true
  sketch-geometry (4):
    g0: LineSegment StartX=16.8446 StartY=31.512 StartZ=0 EndX=16.3251 EndY=34.4666 EndZ=0
    g1: ArcOfCircle CenterX=19 CenterY=19.2524 CenterZ=0 NormalX=0 NormalY=0 NormalZ=1 AngleXU=0 Radius=15.4476 StartAngle=1.74483 EndAngle=2.72717
    g2: ArcOfCircle CenterX=19 CenterY=19.2524 CenterZ=0 NormalX=0 NormalY=0 NormalZ=1 AngleXU=0 Radius=12.4476 StartAngle=1.74483 EndAngle=2.73189
    g3: LineSegment StartX=4.86004 StartY=25.4725 StartZ=0 EndX=7.58253 EndY=24.2107 EndZ=0
  constraints (7):
    c: Block(g0)
    c: Coincident(g1,g0)
    c: Coincident(g2,g0)
    c: Coincident(g3,g1)
    c: Coincident(g3,g2)
    c: Block(g1)
    c: Block(g2)
FEATURE [Part::Extrusion] Extrude010
  Base = -> Sketch011
  Dir = (0,0,1)
  DirMode = 2
  FaceMakerClass = Part::FaceMakerBullseye
  LengthFwd = 10.6
  LengthRev = 0
  Placement = pos=(0,0,31) rot=(0,0,1;0rad)
  Solid = true
  Symmetric = false
FEATURE [Part::Cylinder] Cylinder023
  Angle = 360
  AttacherType = Attacher::AttachEngine3D
  Height = 20
  Placement = pos=(0,0,36.15) rot=(0,0,1;0rad)
  Radius = 8.2
FEATURE [Part::MultiFuse] Fusion039  label="removeToCreteHoleForPlugHousing008"
  Placement = pos=(-42,19,36) rot=(0,1,0;1.5708rad)
  Shapes = -> [Cylinder023,Cylinder022]
FEATURE [Part::Cut] Cut012
  Base = -> Extrude010
  Placement = pos=(0,0,-0.3) rot=(0,0,1;0rad)
  Tool = -> Fusion039
FEATURE [Part::Cut] Cut013
  Base = -> Box010
  Tool = -> Cut012
FEATURE [Part::Fillet] Fillet014
  Base = -> Cut013
  Edges = 1 edges r=0.7: [Edge13]
FEATURE [Part::Fillet] Fillet015
  Base = -> Fillet014
  Edges = 1 edges r=0.7: [Edge13]
FEATURE [Part::Fillet] Fillet016
  Base = -> Fillet015
  Edges = 1 edges r=0.7: [Edge16]
FEATURE [Part::Fillet] Fillet017
  Base = -> Fillet016
  Edges = 1 edges r=0.7: [Edge11]
FEATURE [Part::Fillet] Fillet018
  Base = -> Fillet017
  Edges = 1 edges r=0.7: [Edge10]
FEATURE [Part::Fillet] Fillet019
  Base = -> Fillet018
  Edges = 1 edges r=1.2: [Edge5]
FEATURE [Part::Fillet] Fillet020
  Base = -> Fillet019
  Edges = 1 edges r=1.2: [Edge12]
FEATURE [Part::Fillet] Fillet021
  Base = -> Fillet020
  Edges = 1 edges r=2: [Edge1]
  Placement = pos=(0.3,0,0) rot=(0,0,1;0rad)
FEATURE [Part::MultiFuse] Fusion040  label="top005"
  Shapes = -> [Cut008,Fillet021]
FEATURE [Part::MultiFuse] Fusion041  label="wireHolder"
  Shapes = -> [Fusion033,Fillet013]
FEATURE [Part::MultiFuse] Fusion042
  Shapes = -> [Fillet007,Fusion041]
FEATURE [Part::MultiFuse] Fusion043  label="wireHolder001"
  Shapes = -> [Fusion042,Fillet010]
FEATURE [Part::MultiFuse] Fusion044  label="wireHolder002"
  Shapes = -> [Fillet006,Fusion037,Fusion043]
FEATURE [Part::Feature] Face026
  shape: bbox 11 x 6 x 2e-07 mm, 1 faces, 0 solids (baked)
FEATURE [Part::Revolution] Revolve026
  Angle = 360
  Axis = (0,1,0)
  Base = (0,0,0)
  FaceMakerClass = Part::FaceMakerBullseye
  Placement = pos=(30.3,-1,19.7) rot=(0,0,1;0rad)
  Solid = false
  Source = -> Face026
  Symmetric = false
FEATURE [Sketcher::SketchObject] Sketch013  label="topSketch006"
  FullyConstrained = true
  sketch-geometry (13):
    g0: LineSegment StartX=117 StartY=19 StartZ=0 EndX=117 EndY=38 EndZ=0
    g1: ArcOfCircle CenterX=98 CenterY=19 CenterZ=0 NormalX=0 NormalY=0 NormalZ=1 AngleXU=0 Radius=19 StartAngle=5.7297 EndAngle=6.28319
    g2: LineSegment StartX=0 StartY=3 StartZ=0 EndX=0 EndY=19 EndZ=0
    g3: LineSegment StartX=19 StartY=38 StartZ=0 EndX=117 EndY=38 EndZ=0
    g4: ArcOfCircle CenterX=19 CenterY=19 CenterZ=0 NormalX=0 NormalY=0 NormalZ=1 AngleXU=0 Radius=19 StartAngle=1.5708 EndAngle=3.14159
    g5: ArcOfCircle CenterX=19 CenterY=19 CenterZ=0 NormalX=0 NormalY=0 NormalZ=1 AngleXU=0 Radius=16 StartAngle=1.5708 EndAngle=3.14159
    g6: ArcOfCircle CenterX=98 CenterY=19 CenterZ=0 NormalX=0 NormalY=0 NormalZ=1 AngleXU=0 Radius=16 StartAngle=5.60905 EndAngle=6.28319
    g7: LineSegment StartX=114 StartY=19 StartZ=0 EndX=114 EndY=35 EndZ=0
    g8: LineSegment StartX=110.5 StartY=9.01251 StartZ=0 EndX=114.163 EndY=9.01251 EndZ=0
    g9: LineSegment StartX=114 StartY=35 StartZ=0 EndX=19 EndY=35 EndZ=0
    g10: LineSegment StartX=0 StartY=3 StartZ=0 EndX=0 EndY=0 EndZ=0
    g11: LineSegment StartX=3 StartY=0 StartZ=0 EndX=0 EndY=0 EndZ=0
    g12: LineSegment StartX=3 StartY=19 StartZ=0 EndX=3 EndY=0 EndZ=0
  constraints (33):
    c: Vertical(g0)
    c: Distance(g0) = 19
    c: Block(g0)
    c: Coincident(g1,g0)
    c: Block(g1)
    c: Vertical(g2)
    c: Block(g2)
    c: Coincident(g3,g0)
    c: Horizontal(g3)
    c: Distance(g3) = 98
    c: Coincident(g4,g3)
    c: Coincident(g4,g2)
    c: Block(g4)
    c: Coincident(g5,g4)
    c: Coincident(g6,g1)
    c: Block(g6)
    c: Block(g5)
    c: Coincident(g7,g6)
    c: Vertical(g7)
    c: Coincident(g8,g6)
    c: Coincident(g8,g1)
    c: Coincident(g9,g7)
    c: Coincident(g9,g5)
    c: Horizontal(g9)
    c: Tangent(g9,g5)
    c: Coincident(g10,g2)
    c: Distance(g10) = 3
    c: Vertical(g10)
    c: Coincident(g11,g10)
    c: Horizontal(g11)
    c: Coincident(g12,g5)
    c: Coincident(g12,g11)
    c: Vertical(g12)
FEATURE [Part::Extrusion] Extrude011  label="top006"
  Base = -> Sketch013
  Dir = (0,0,1)
  DirMode = 2
  FaceMakerClass = Part::FaceMakerBullseye
  LengthFwd = 72
  LengthRev = 0
  Solid = true
  Symmetric = false
FEATURE [Sketcher::SketchObject] Sketch014
  FullyConstrained = true
  MapMode = 3
  Placement = pos=(0,0,0) rot=(1,0,0;1.5708rad)
  Support = -> [Extrude011]
  sketch-geometry (8):
    g0: Circle CenterX=80.351 CenterY=-67.6202 CenterZ=0 NormalX=0 NormalY=0 NormalZ=1 AngleXU=0 Radius=2
    g1: Circle CenterX=80.351 CenterY=-67.6202 CenterZ=0 NormalX=0 NormalY=0 NormalZ=1 AngleXU=0 Radius=3
    g2: Circle CenterX=80.351 CenterY=-4.92017 CenterZ=0 NormalX=0 NormalY=0 NormalZ=1 AngleXU=0 Radius=2
    g3: Circle CenterX=80.351 CenterY=-4.92017 CenterZ=0 NormalX=0 NormalY=0 NormalZ=1 AngleXU=0 Radius=3
    g4: Circle CenterX=23.851 CenterY=-4.92017 CenterZ=0 NormalX=0 NormalY=0 NormalZ=1 AngleXU=0 Radius=2
    g5: Circle CenterX=23.851 CenterY=-4.92017 CenterZ=0 NormalX=0 NormalY=0 NormalZ=1 AngleXU=0 Radius=3
    g6: Circle CenterX=23.851 CenterY=-67.6202 CenterZ=0 NormalX=0 NormalY=0 NormalZ=1 AngleXU=0 Radius=2
    g7: Circle CenterX=23.851 CenterY=-67.6202 CenterZ=0 NormalX=0 NormalY=0 NormalZ=1 AngleXU=0 Radius=3
  constraints (8):
    c: Block(g3)
    c: Block(g2)
    c: Block(g1)
    c: Block(g0)
    c: Block(g6)
    c: Block(g7)
    c: Block(g4)
    c: Block(g5)
FEATURE [Part::Feature] Face027
  shape: bbox 11 x 6 x 2e-07 mm, 1 faces, 0 solids (baked)
FEATURE [Part::Revolution] Revolve027
  Angle = 360
  Axis = (0,1,0)
  Base = (0,0,0)
  FaceMakerClass = Part::FaceMakerBullseye
  Placement = pos=(30.3,-1,51.7) rot=(0,0,1;0rad)
  Solid = false
  Source = -> Face027
  Symmetric = false
FEATURE [Part::Feature] Face028
  shape: bbox 11 x 6 x 2e-07 mm, 1 faces, 0 solids (baked)
FEATURE [Part::Revolution] Revolve028
  Angle = 360
  Axis = (0,1,0)
  Base = (0,0,0)
  FaceMakerClass = Part::FaceMakerBullseye
  Placement = pos=(62.3,-1,19.7) rot=(0,0,1;0rad)
  Solid = false
  Source = -> Face028
  Symmetric = false
FEATURE [Part::Feature] Face029
  shape: bbox 11 x 6 x 2e-07 mm, 1 faces, 0 solids (baked)
FEATURE [Part::Revolution] Revolve029
  Angle = 360
  Axis = (0,1,0)
  Base = (0,0,0)
  FaceMakerClass = Part::FaceMakerBullseye
  Placement = pos=(62.3,-1,51.7) rot=(0,0,1;0rad)
  Solid = false
  Source = -> Face029
  Symmetric = false
FEATURE [Part::Feature] Wire
  shape: bbox 11 x 5.2 x 2e-07 mm, 0 faces, 0 solids (baked)
FEATURE [Part::Revolution] Revolve030
  Angle = 360
  Axis = (0,1,0)
  Base = (0,0,0)
  FaceMakerClass = Part::FaceMakerBullseye
  Placement = pos=(30.3,38,19.7) rot=(0,0,1;0rad)
  Solid = true
  Source = -> Wire
  Symmetric = false
FEATURE [Part::Feature] Wire001
  shape: bbox 11 x 5.2 x 2e-07 mm, 0 faces, 0 solids (baked)
FEATURE [Part::Revolution] Revolve031
  Angle = 360
  Axis = (0,1,0)
  Base = (0,0,0)
  FaceMakerClass = Part::FaceMakerBullseye
  Placement = pos=(30.3,38,51.7) rot=(0,0,1;0rad)
  Solid = true
  Source = -> Wire001
  Symmetric = false
FEATURE [Part::Feature] Wire002
  shape: bbox 11 x 5.2 x 2e-07 mm, 0 faces, 0 solids (baked)
FEATURE [Part::Revolution] Revolve032
  Angle = 360
  Axis = (0,1,0)
  Base = (0,0,0)
  FaceMakerClass = Part::FaceMakerBullseye
  Placement = pos=(62.3,38,51.7) rot=(0,0,1;0rad)
  Solid = true
  Source = -> Wire002
  Symmetric = false
FEATURE [Part::Feature] Wire003
  shape: bbox 11 x 5.2 x 2e-07 mm, 0 faces, 0 solids (baked)
FEATURE [Part::Revolution] Revolve033
  Angle = 360
  Axis = (0,1,0)
  Base = (0,0,0)
  FaceMakerClass = Part::FaceMakerBullseye
  Placement = pos=(62.3,38,19.7) rot=(0,0,1;0rad)
  Solid = true
  Source = -> Wire003
  Symmetric = false
FEATURE [Part::MultiFuse] Fusion045  label="altRandScrewHousing"
  Shapes = -> [Revolve029,Revolve027,Revolve028,Revolve026]
FEATURE [Part::MultiFuse] Fusion046  label="fanScrewHousing"
  Shapes = -> [Revolve033,Revolve032,Revolve031,Revolve030]
FEATURE [Sketcher::SketchObject] Sketch015
  FullyConstrained = true
  sketch-geometry (17):
    g0: Circle CenterX=-3.5 CenterY=23.5 CenterZ=0 NormalX=0 NormalY=0 NormalZ=1 AngleXU=0 Radius=1
    g1: Circle CenterX=-1 CenterY=15.25 CenterZ=0 NormalX=0 NormalY=0 NormalZ=1 AngleXU=0 Radius=1
    g2: Circle CenterX=-3.5 CenterY=7 CenterZ=0 NormalX=0 NormalY=0 NormalZ=1 AngleXU=0 Radius=1
    g3: BSplineCurve PolesCount=3 KnotsCount=2 Degree=2 IsPeriodic=0
    g4: GeomPoint X=-3.5 Y=23.5 Z=0
    g5: GeomPoint X=-3.5 Y=7 Z=0
    g6: Circle CenterX=-4.8 CenterY=30.5 CenterZ=0 NormalX=0 NormalY=0 NormalZ=1 AngleXU=0 Radius=1
    g7: Circle CenterX=-3.5 CenterY=30.5 CenterZ=0 NormalX=0 NormalY=0 NormalZ=1 AngleXU=0 Radius=1
    g8: Circle CenterX=-3.5 CenterY=29.2 CenterZ=0 NormalX=0 NormalY=0 NormalZ=1 AngleXU=0 Radius=1
    g9: BSplineCurve PolesCount=3 KnotsCount=2 Degree=2 IsPeriodic=0
    g10: GeomPoint X=-4.8 Y=30.5 Z=0
    g11: GeomPoint X=-3.5 Y=29.2 Z=0
    g12: LineSegment StartX=-3.5 StartY=29.2 StartZ=0 EndX=-3.5 EndY=23.5 EndZ=0
    g13: LineSegment StartX=-4.8 StartY=30.5 StartZ=0 EndX=0 EndY=30.5 EndZ=0
    g14: LineSegment StartX=-3.5 StartY=0.3 StartZ=0 EndX=0 EndY=0.3 EndZ=0
    g15: LineSegment StartX=-3.5 StartY=0.3 StartZ=0 EndX=-3.5 EndY=7 EndZ=0
    g16: LineSegment StartX=0 StartY=0.3 StartZ=0 EndX=0 EndY=30.5 EndZ=0
  constraints (33):
    c: Weight(g0) = 1
    c: Equal(g0,g1)
    c: Equal(g0,g2)
    c: InternalAlignment(g0,g3)
    c: InternalAlignment(g1,g3)
    c: InternalAlignment(g2,g3)
    c: InternalAlignment(g4,g3)
    c: InternalAlignment(g5,g3)
    c: Block(g3)
    c: Weight(g6) = 1
    c: Equal(g6,g7)
    c: Equal(g6,g8)
    c: InternalAlignment(g6,g9)
    c: InternalAlignment(g7,g9)
    c: InternalAlignment(g8,g9)
    c: InternalAlignment(g10,g9)
    c: InternalAlignment(g11,g9)
    c: Block(g9)
    c: Coincident(g12,g9)
    c: Coincident(g12,g3)
    c: Vertical(g12)
    c: Coincident(g13,g9)
    c: Horizontal(g13)
    c: Distance(g13) = 4.8
    c: Horizontal(g14)
    c: Block(g14)
    c: Coincident(g15,g14)
    c: Coincident(g15,g3)
    c: Vertical(g15)
    c: Coincident(g16,g14)
    c: Coincident(g16,g13)
    c: Vertical(g16)
    c: Tangent(g16,g1)
FEATURE [Sketcher::SketchObject] Sketch016
  FullyConstrained = true
  sketch-geometry (16):
    g0: Circle CenterX=-3.5 CenterY=23.5 CenterZ=0 NormalX=0 NormalY=0 NormalZ=1 AngleXU=0 Radius=1
    g1: Circle CenterX=-1 CenterY=15.25 CenterZ=0 NormalX=0 NormalY=0 NormalZ=1 AngleXU=0 Radius=1
    g2: Circle CenterX=-3.5 CenterY=7 CenterZ=0 NormalX=0 NormalY=0 NormalZ=1 AngleXU=0 Radius=1
    g3: BSplineCurve PolesCount=3 KnotsCount=2 Degree=2 IsPeriodic=0
    g4: GeomPoint X=-3.5 Y=23.5 Z=0
    g5: GeomPoint X=-3.5 Y=7 Z=0
    g6: LineSegment StartX=-3.5 StartY=28.2 StartZ=0 EndX=-3.5 EndY=23.5 EndZ=0
    g7: LineSegment StartX=0 StartY=29.5 StartZ=0 EndX=0 EndY=30 EndZ=0
    g8: LineSegment StartX=-3.5 StartY=28.2 StartZ=0 EndX=-3.5 EndY=30 EndZ=0
    g9: LineSegment StartX=0 StartY=30 StartZ=0 EndX=0 EndY=30.5 EndZ=0
    g10: LineSegment StartX=0 StartY=30.5 StartZ=0 EndX=-3.5 EndY=30.5 EndZ=0
    g11: LineSegment StartX=-3.5 StartY=30.5 StartZ=0 EndX=-3.5 EndY=30 EndZ=0
    g12: LineSegment StartX=0 StartY=29.5 StartZ=0 EndX=0 EndY=5 EndZ=0
    g13: LineSegment StartX=-3.5 StartY=0.3 StartZ=0 EndX=-3.5 EndY=7 EndZ=0
    g14: LineSegment StartX=-3.5 StartY=0.3 StartZ=0 EndX=0 EndY=0.3 EndZ=0
    g15: LineSegment StartX=0 StartY=5 StartZ=0 EndX=0 EndY=0.3 EndZ=0
  constraints (39):
    c: Weight(g0) = 1
    c: Equal(g0,g1)
    c: Equal(g0,g2)
    c: InternalAlignment(g0,g3)
    c: InternalAlignment(g1,g3)
    c: InternalAlignment(g2,g3)
    c: InternalAlignment(g4,g3)
    c: InternalAlignment(g5,g3)
    c: Block(g3)
    c: Coincident(g6,g3)
    c: Vertical(g6)
    c: Vertical(g7)
    c: Distance(g7) = 0.5
    c: Coincident(g8,g6)
    c: Vertical(g8)
    c: Block(g6)
    c: Block(g7)
    c: Vertical(g9)
    c: Equal(g7,g9) = 0.5
    c: Block(g9)
    c: Coincident(g9,g7)
    c: Horizontal(g10)
    c: Coincident(g10,g9)
    c: Coincident(g11,g10)
    c: Coincident(g11,g8)
    c: Vertical(g11)
    c: Block(g11)
    c: Coincident(g12,g7)
    c: Vertical(g12)
    c: Coincident(g13,g3)
    c: Vertical(g13)
    c: Distance(g13) = 6.7
    c: Coincident(g14,g13)
    c: Horizontal(g14)
    c: Block(g14)
    c: Coincident(g15,g12)
    c: Coincident(g15,g14)
    c: Vertical(g15)
    c: Block(g15)
FEATURE [Sketcher::SketchObject] Sketch017
  FullyConstrained = true
  sketch-geometry (11):
    g0: LineSegment StartX=-3.5 StartY=1e-16 StartZ=0 EndX=-1.6 EndY=1e-16 EndZ=0
    g1: LineSegment StartX=-1.6 StartY=1e-16 StartZ=0 EndX=-1.6 EndY=1.5 EndZ=0
    g2: LineSegment StartX=-3.5 StartY=1.5 StartZ=0 EndX=-1.6 EndY=1.5 EndZ=0
    g3: LineSegment StartX=-3.5 StartY=1e-16 StartZ=0 EndX=-4.8 EndY=1e-16 EndZ=0
    g4: Circle CenterX=-3.5 CenterY=1.3 CenterZ=0 NormalX=0 NormalY=0 NormalZ=1 AngleXU=0 Radius=1
    g5: Circle CenterX=-3.5 CenterY=1e-16 CenterZ=0 NormalX=0 NormalY=0 NormalZ=1 AngleXU=0 Radius=1
    g6: Circle CenterX=-4.8 CenterY=1e-16 CenterZ=0 NormalX=0 NormalY=0 NormalZ=1 AngleXU=0 Radius=1
    g7: BSplineCurve PolesCount=3 KnotsCount=2 Degree=2 IsPeriodic=0
    g8: GeomPoint X=-3.5 Y=1.3 Z=0
    g9: GeomPoint X=-4.8 Y=1e-16 Z=0
    g10: LineSegment StartX=-3.5 StartY=1.3 StartZ=0 EndX=-3.5 EndY=1.5 EndZ=0
  constraints (24):
    c: Horizontal(g0)
    c: Distance(g0) = 1.9
    c: Block(g0)
    c: Coincident(g1,g0)
    c: Vertical(g1)
    c: Coincident(g2,g1)
    c: Horizontal(g2)
    c: Coincident(g3,g0)
    c: Horizontal(g3)
    c: Distance(g3) = 1.3
    c: Weight(g4) = 1
    c: Equal(g4,g5)
    c: Coincident(g5,g0)
    c: Equal(g4,g6)
    c: Coincident(g7,g3)
    c: InternalAlignment(g4,g7)
    c: InternalAlignment(g5,g7)
    c: InternalAlignment(g6,g7)
    c: InternalAlignment(g8,g7)
    c: InternalAlignment(g9,g7)
    c: Coincident(g10,g7)
    c: Coincident(g10,g2)
    c: Vertical(g10)
    c: Block(g10)
FEATURE [Part::Feature] Face035
  shape: bbox 3.2 x 1.5 x 2e-07 mm, 1 faces, 0 solids (baked)
FEATURE [Part::Revolution] Revolve039  label="backCaseScrewRetainer"
  Angle = 360
  Axis = (0,1,0)
  Base = (0,0,0)
  FaceMakerClass = Part::FaceMakerBullseye
  Placement = pos=(12.5,3,62) rot=(0,0,1;0rad)
  Solid = false
  Source = -> Face035
  Symmetric = false
FEATURE [Part::Feature] Face036
  shape: bbox 3.2 x 1.5 x 2e-07 mm, 1 faces, 0 solids (baked)
FEATURE [Part::Feature] Face039
  shape: bbox 4.8 x 30.2 x 2e-07 mm, 1 faces, 0 solids (baked)
FEATURE [Part::Revolution] Revolve043  label="frontCaseScrewPost002"
  Angle = 360
  Axis = (0,1,0)
  Base = (0,0,0)
  FaceMakerClass = Part::FaceMakerBullseye
  Placement = pos=(89.5,4.5,3.5) rot=(0,0,1;0rad)
  Solid = false
  Source = -> Face039
  Symmetric = false
FEATURE [Part::Feature] Face042
  shape: bbox 4.8 x 30.2 x 2e-07 mm, 1 faces, 0 solids (baked)
FEATURE [Part::Revolution] Revolve046  label="frontCaseScrewPost003"
  Angle = 360
  Axis = (0,1,0)
  Base = (0,0,0)
  FaceMakerClass = Part::FaceMakerBullseye
  Placement = pos=(89.5,4.5,68.5) rot=(0,0,1;0rad)
  Solid = false
  Source = -> Face042
  Symmetric = false
FEATURE [Part::Feature] Face043
  shape: bbox 3.2 x 1.5 x 2e-07 mm, 1 faces, 0 solids (baked)
FEATURE [Part::Revolution] Revolve047  label="frontCaseScrewRetainer002"
  Angle = 360
  Axis = (0,1,0)
  Base = (0,0,0)
  FaceMakerClass = Part::FaceMakerBullseye
  Placement = pos=(89.5,3,68.5) rot=(0,0,1;0rad)
  Solid = false
  Source = -> Face043
  Symmetric = false
FEATURE [Part::Feature] Face044
  shape: bbox 3.2 x 1.5 x 2e-07 mm, 1 faces, 0 solids (baked)
FEATURE [Part::Revolution] Revolve048  label="frontCaseScrewRetainer003"
  Angle = 360
  Axis = (0,1,0)
  Base = (0,0,0)
  FaceMakerClass = Part::FaceMakerBullseye
  Placement = pos=(89.5,3,3.5) rot=(0,0,1;0rad)
  Solid = false
  Source = -> Face044
  Symmetric = false
FEATURE [App::MeasureDistance] Distance002  label="Distance: 1.67 mm"
  Distance = 1.66921
  P1 = (99.2361,4.7524,71.7)
  P2 = (99.2347,6.42161,71.7)
FEATURE [Sketcher::SketchObject] Sketch018
  FullyConstrained = true
  sketch-geometry (7):
    g0: LineSegment StartX=0 StartY=0 StartZ=0 EndX=0 EndY=6 EndZ=0
    g1: Circle CenterX=0 CenterY=0 CenterZ=0 NormalX=0 NormalY=0 NormalZ=1 AngleXU=0 Radius=1
    g2: Circle CenterX=8 CenterY=6 CenterZ=0 NormalX=0 NormalY=0 NormalZ=1 AngleXU=0 Radius=1
    g3: BSplineCurve PolesCount=3 KnotsCount=2 Degree=2 IsPeriodic=0
    g4: GeomPoint X=0 Y=0 Z=0
    g5: GeomPoint X=8 Y=6 Z=0
    g6: LineSegment StartX=0 StartY=6 StartZ=0 EndX=8 EndY=6 EndZ=0
  constraints (14):
    c: Coincident(g0,g-1)
    c: Distance(g0) = 6
    c: Vertical(g0)
    c: Coincident(g3,g0)
    c: Weight(g1) = 1
    c: Equal(g1,g2)
    c: InternalAlignment(g1,g3)
    c: InternalAlignment(g2,g3)
    c: InternalAlignment(g4,g3)
    c: InternalAlignment(g5,g3)
    c: Block(g3)
    c: Coincident(g6,g0)
    c: Coincident(g6,g3)
    c: Horizontal(g6)
FEATURE [Part::Extrusion] Extrude012  label="caseScrewPillarBracket"
  Base = -> Sketch018
  Dir = (0,0,1)
  DirMode = 2
  FaceMakerClass = Part::FaceMakerBullseye
  LengthFwd = 2.4
  LengthRev = 0
  Placement = pos=(15.76,29,8.8) rot=(0,1,0;0rad)
  Solid = true
  Symmetric = false
FEATURE [Sketcher::SketchObject] Sketch019
  FullyConstrained = true
  sketch-geometry (7):
    g0: LineSegment StartX=0 StartY=0 StartZ=0 EndX=0 EndY=6 EndZ=0
    g1: Circle CenterX=0 CenterY=0 CenterZ=0 NormalX=0 NormalY=0 NormalZ=1 AngleXU=0 Radius=1
    g2: Circle CenterX=8 CenterY=6 CenterZ=0 NormalX=0 NormalY=0 NormalZ=1 AngleXU=0 Radius=1
    g3: BSplineCurve PolesCount=3 KnotsCount=2 Degree=2 IsPeriodic=0
    g4: GeomPoint X=0 Y=0 Z=0
    g5: GeomPoint X=8 Y=6 Z=0
    g6: LineSegment StartX=0 StartY=6 StartZ=0 EndX=8 EndY=6 EndZ=0
  constraints (14):
    c: Coincident(g0,g-1)
    c: Distance(g0) = 6
    c: Vertical(g0)
    c: Coincident(g3,g0)
    c: Weight(g1) = 1
    c: Equal(g1,g2)
    c: InternalAlignment(g1,g3)
    c: InternalAlignment(g2,g3)
    c: InternalAlignment(g4,g3)
    c: InternalAlignment(g5,g3)
    c: Block(g3)
    c: Coincident(g6,g0)
    c: Coincident(g6,g3)
    c: Horizontal(g6)
FEATURE [Part::Extrusion] Extrude013  label="caseScrewPillarBracket001"
  Base = -> Sketch019
  Dir = (0,0,1)
  DirMode = 2
  FaceMakerClass = Part::FaceMakerBullseye
  LengthFwd = 2.4
  LengthRev = 0
  Placement = pos=(15.76,29,60.8) rot=(0,0,1;0rad)
  Solid = true
  Symmetric = false
FEATURE [Sketcher::SketchObject] Sketch020
  FullyConstrained = true
  sketch-geometry (7):
    g0: LineSegment StartX=0 StartY=0 StartZ=0 EndX=0 EndY=6 EndZ=0
    g1: Circle CenterX=0 CenterY=0 CenterZ=0 NormalX=0 NormalY=0 NormalZ=1 AngleXU=0 Radius=1
    g2: Circle CenterX=8 CenterY=6 CenterZ=0 NormalX=0 NormalY=0 NormalZ=1 AngleXU=0 Radius=1
    g3: BSplineCurve PolesCount=3 KnotsCount=2 Degree=2 IsPeriodic=0
    g4: GeomPoint X=0 Y=0 Z=0
    g5: GeomPoint X=8 Y=6 Z=0
    g6: LineSegment StartX=0 StartY=6 StartZ=0 EndX=8 EndY=6 EndZ=0
  constraints (14):
    c: Coincident(g0,g-1)
    c: Distance(g0) = 6
    c: Vertical(g0)
    c: Coincident(g3,g0)
    c: Weight(g1) = 1
    c: Equal(g1,g2)
    c: InternalAlignment(g1,g3)
    c: InternalAlignment(g2,g3)
    c: InternalAlignment(g4,g3)
    c: InternalAlignment(g5,g3)
    c: Block(g3)
    c: Coincident(g6,g0)
    c: Coincident(g6,g3)
    c: Horizontal(g6)
FEATURE [Part::Extrusion] Extrude014  label="caseScrewPillarBracket002"
  Base = -> Sketch020
  Dir = (0,0,1)
  DirMode = 2
  FaceMakerClass = Part::FaceMakerBullseye
  LengthFwd = 2.4
  LengthRev = 0
  Placement = pos=(13.7,29,13.26) rot=(0,-1,0;1.5708rad)
  Solid = true
  Symmetric = false
FEATURE [Sketcher::SketchObject] Sketch021
  FullyConstrained = true
  sketch-geometry (7):
    g0: LineSegment StartX=0 StartY=0 StartZ=0 EndX=0 EndY=6 EndZ=0
    g1: Circle CenterX=0 CenterY=0 CenterZ=0 NormalX=0 NormalY=0 NormalZ=1 AngleXU=0 Radius=1
    g2: Circle CenterX=8 CenterY=6 CenterZ=0 NormalX=0 NormalY=0 NormalZ=1 AngleXU=0 Radius=1
    g3: BSplineCurve PolesCount=3 KnotsCount=2 Degree=2 IsPeriodic=0
    g4: GeomPoint X=0 Y=0 Z=0
    g5: GeomPoint X=8 Y=6 Z=0
    g6: LineSegment StartX=0 StartY=6 StartZ=0 EndX=8 EndY=6 EndZ=0
  constraints (14):
    c: Coincident(g0,g-1)
    c: Distance(g0) = 6
    c: Vertical(g0)
    c: Coincident(g3,g0)
    c: Weight(g1) = 1
    c: Equal(g1,g2)
    c: InternalAlignment(g1,g3)
    c: InternalAlignment(g2,g3)
    c: InternalAlignment(g4,g3)
    c: InternalAlignment(g5,g3)
    c: Block(g3)
    c: Coincident(g6,g0)
    c: Coincident(g6,g3)
    c: Horizontal(g6)
FEATURE [Part::Extrusion] Extrude015  label="caseScrewPillarBracket003"
  Base = -> Sketch021
  Dir = (0,0,1)
  DirMode = 2
  FaceMakerClass = Part::FaceMakerBullseye
  LengthFwd = 2.4
  LengthRev = 0
  Placement = pos=(11.3,29,58.74) rot=(0,1,0;1.5708rad)
  Solid = true
  Symmetric = false
FEATURE [Sketcher::SketchObject] Sketch022
  FullyConstrained = true
  sketch-geometry (7):
    g0: LineSegment StartX=0 StartY=0 StartZ=0 EndX=0 EndY=6 EndZ=0
    g1: Circle CenterX=0 CenterY=0 CenterZ=0 NormalX=0 NormalY=0 NormalZ=1 AngleXU=0 Radius=1
    g2: Circle CenterX=8 CenterY=6 CenterZ=0 NormalX=0 NormalY=0 NormalZ=1 AngleXU=0 Radius=1
    g3: BSplineCurve PolesCount=3 KnotsCount=2 Degree=2 IsPeriodic=0
    g4: GeomPoint X=0 Y=0 Z=0
    g5: GeomPoint X=8 Y=6 Z=0
    g6: LineSegment StartX=0 StartY=6 StartZ=0 EndX=8 EndY=6 EndZ=0
  constraints (14):
    c: Coincident(g0,g-1)
    c: Distance(g0) = 6
    c: Vertical(g0)
    c: Coincident(g3,g0)
    c: Weight(g1) = 1
    c: Equal(g1,g2)
    c: InternalAlignment(g1,g3)
    c: InternalAlignment(g2,g3)
    c: InternalAlignment(g4,g3)
    c: InternalAlignment(g5,g3)
    c: Block(g3)
    c: Coincident(g6,g0)
    c: Coincident(g6,g3)
    c: Horizontal(g6)
FEATURE [Part::Extrusion] Extrude016  label="caseScrewPillarBracket004"
  Base = -> Sketch022
  Dir = (0,0,1)
  DirMode = 2
  FaceMakerClass = Part::FaceMakerBullseye
  LengthFwd = 2.4
  LengthRev = 0
  Placement = pos=(88.3,29,65.23) rot=(0,1,0;1.5708rad)
  Solid = true
  Symmetric = false
FEATURE [Sketcher::SketchObject] Sketch023
  FullyConstrained = true
  sketch-geometry (7):
    g0: LineSegment StartX=0 StartY=0 StartZ=0 EndX=0 EndY=6 EndZ=0
    g1: Circle CenterX=0 CenterY=0 CenterZ=0 NormalX=0 NormalY=0 NormalZ=1 AngleXU=0 Radius=1
    g2: Circle CenterX=8 CenterY=6 CenterZ=0 NormalX=0 NormalY=0 NormalZ=1 AngleXU=0 Radius=1
    g3: BSplineCurve PolesCount=3 KnotsCount=2 Degree=2 IsPeriodic=0
    g4: GeomPoint X=0 Y=0 Z=0
    g5: GeomPoint X=8 Y=6 Z=0
    g6: LineSegment StartX=0 StartY=6 StartZ=0 EndX=8 EndY=6 EndZ=0
  constraints (14):
    c: Coincident(g0,g-1)
    c: Distance(g0) = 6
    c: Vertical(g0)
    c: Coincident(g3,g0)
    c: Weight(g1) = 1
    c: Equal(g1,g2)
    c: InternalAlignment(g1,g3)
    c: InternalAlignment(g2,g3)
    c: InternalAlignment(g4,g3)
    c: InternalAlignment(g5,g3)
    c: Block(g3)
    c: Coincident(g6,g0)
    c: Coincident(g6,g3)
    c: Horizontal(g6)
FEATURE [Part::Extrusion] Extrude017  label="caseScrewPillarBracket005"
  Base = -> Sketch023
  Dir = (0,0,1)
  DirMode = 2
  FaceMakerClass = Part::FaceMakerBullseye
  LengthFwd = 2.4
  LengthRev = 0
  Placement = pos=(90.7,29,6.77) rot=(0,-1,0;1.5708rad)
  Solid = true
  Symmetric = false
FEATURE [Sketcher::SketchObject] Sketch024
  FullyConstrained = true
  sketch-geometry (7):
    g0: LineSegment StartX=0 StartY=0 StartZ=0 EndX=0 EndY=6 EndZ=0
    g1: Circle CenterX=0 CenterY=0 CenterZ=0 NormalX=0 NormalY=0 NormalZ=1 AngleXU=0 Radius=1
    g2: Circle CenterX=8 CenterY=6 CenterZ=0 NormalX=0 NormalY=0 NormalZ=1 AngleXU=0 Radius=1
    g3: BSplineCurve PolesCount=3 KnotsCount=2 Degree=2 IsPeriodic=0
    g4: GeomPoint X=0 Y=0 Z=0
    g5: GeomPoint X=8 Y=6 Z=0
    g6: LineSegment StartX=0 StartY=6 StartZ=0 EndX=8 EndY=6 EndZ=0
  constraints (14):
    c: Coincident(g0,g-1)
    c: Distance(g0) = 6
    c: Vertical(g0)
    c: Coincident(g3,g0)
    c: Weight(g1) = 1
    c: Equal(g1,g2)
    c: InternalAlignment(g1,g3)
    c: InternalAlignment(g2,g3)
    c: InternalAlignment(g4,g3)
    c: InternalAlignment(g5,g3)
    c: Block(g3)
    c: Coincident(g6,g0)
    c: Coincident(g6,g3)
    c: Horizontal(g6)
FEATURE [Part::Extrusion] Extrude018  label="caseScrewPillarBracket006"
  Base = -> Sketch024
  Dir = (0,0,1)
  DirMode = 2
  FaceMakerClass = Part::FaceMakerBullseye
  LengthFwd = 2.4
  LengthRev = 0
  Placement = pos=(103.7,29,6.77) rot=(0,-1,0;1.5708rad)
  Solid = true
  Symmetric = false
FEATURE [Sketcher::SketchObject] Sketch025
  FullyConstrained = true
  sketch-geometry (7):
    g0: LineSegment StartX=0 StartY=0 StartZ=0 EndX=0 EndY=6 EndZ=0
    g1: Circle CenterX=0 CenterY=0 CenterZ=0 NormalX=0 NormalY=0 NormalZ=1 AngleXU=0 Radius=1
    g2: Circle CenterX=8 CenterY=6 CenterZ=0 NormalX=0 NormalY=0 NormalZ=1 AngleXU=0 Radius=1
    g3: BSplineCurve PolesCount=3 KnotsCount=2 Degree=2 IsPeriodic=0
    g4: GeomPoint X=0 Y=0 Z=0
    g5: GeomPoint X=8 Y=6 Z=0
    g6: LineSegment StartX=0 StartY=6 StartZ=0 EndX=8 EndY=6 EndZ=0
  constraints (14):
    c: Coincident(g0,g-1)
    c: Distance(g0) = 6
    c: Vertical(g0)
    c: Coincident(g3,g0)
    c: Weight(g1) = 1
    c: Equal(g1,g2)
    c: InternalAlignment(g1,g3)
    c: InternalAlignment(g2,g3)
    c: InternalAlignment(g4,g3)
    c: InternalAlignment(g5,g3)
    c: Block(g3)
    c: Coincident(g6,g0)
    c: Coincident(g6,g3)
    c: Horizontal(g6)
FEATURE [Part::Extrusion] Extrude019  label="caseScrewPillarBracket007"
  Base = -> Sketch025
  Dir = (0,0,1)
  DirMode = 2
  FaceMakerClass = Part::FaceMakerBullseye
  LengthFwd = 2.4
  LengthRev = 0
  Placement = pos=(101.3,29,65.23) rot=(0,1,0;1.5708rad)
  Solid = true
  Symmetric = false
FEATURE [Part::Box] Box011  label="frontCaseScrewPillarBracket"
  AttacherType = Attacher::AttachEngine3D
  Height = 2.4
  Length = 16
  Placement = pos=(87,28,2.3) rot=(0,0,1;0rad)
  Width = 7
FEATURE [Part::Box] Box012  label="frontCaseScrewPillarBracket001"
  AttacherType = Attacher::AttachEngine3D
  Height = 2.4
  Length = 16
  Placement = pos=(87,28,67.3) rot=(0,0,1;0rad)
  Width = 7
FEATURE [Sketcher::SketchObject] Sketch026
  FullyConstrained = true
  sketch-geometry (17):
    g0: Circle CenterX=-3.5 CenterY=23.5 CenterZ=0 NormalX=0 NormalY=0 NormalZ=1 AngleXU=0 Radius=1
    g1: Circle CenterX=-1 CenterY=15.25 CenterZ=0 NormalX=0 NormalY=0 NormalZ=1 AngleXU=0 Radius=1
    g2: Circle CenterX=-3.5 CenterY=7 CenterZ=0 NormalX=0 NormalY=0 NormalZ=1 AngleXU=0 Radius=1
    g3: BSplineCurve PolesCount=3 KnotsCount=2 Degree=2 IsPeriodic=0
    g4: GeomPoint X=-3.5 Y=23.5 Z=0
    g5: GeomPoint X=-3.5 Y=7 Z=0
    g6: Circle CenterX=-4.8 CenterY=30.5 CenterZ=0 NormalX=0 NormalY=0 NormalZ=1 AngleXU=0 Radius=1
    g7: Circle CenterX=-3.5 CenterY=30.5 CenterZ=0 NormalX=0 NormalY=0 NormalZ=1 AngleXU=0 Radius=1
    g8: Circle CenterX=-3.5 CenterY=29.2 CenterZ=0 NormalX=0 NormalY=0 NormalZ=1 AngleXU=0 Radius=1
    g9: BSplineCurve PolesCount=3 KnotsCount=2 Degree=2 IsPeriodic=0
    g10: GeomPoint X=-4.8 Y=30.5 Z=0
    g11: GeomPoint X=-3.5 Y=29.2 Z=0
    g12: LineSegment StartX=-3.5 StartY=29.2 StartZ=0 EndX=-3.5 EndY=23.5 EndZ=0
    g13: LineSegment StartX=-4.8 StartY=30.5 StartZ=0 EndX=0 EndY=30.5 EndZ=0
    g14: LineSegment StartX=-3.5 StartY=5 StartZ=0 EndX=-3.5 EndY=7 EndZ=0
    g15: LineSegment StartX=0 StartY=5 StartZ=0 EndX=0 EndY=30.5 EndZ=0
    g16: LineSegment StartX=-3.5 StartY=5 StartZ=0 EndX=0 EndY=5 EndZ=0
  constraints (33):
    c: Weight(g0) = 1
    c: Equal(g0,g1)
    c: Equal(g0,g2)
    c: InternalAlignment(g0,g3)
    c: InternalAlignment(g1,g3)
    c: InternalAlignment(g2,g3)
    c: InternalAlignment(g4,g3)
    c: InternalAlignment(g5,g3)
    c: Block(g3)
    c: Weight(g6) = 1
    c: Equal(g6,g7)
    c: Equal(g6,g8)
    c: InternalAlignment(g6,g9)
    c: InternalAlignment(g7,g9)
    c: InternalAlignment(g8,g9)
    c: InternalAlignment(g10,g9)
    c: InternalAlignment(g11,g9)
    c: Block(g9)
    c: Coincident(g12,g9)
    c: Coincident(g12,g3)
    c: Vertical(g12)
    c: Coincident(g13,g9)
    c: Horizontal(g13)
    c: Distance(g13) = 4.8
    c: Coincident(g14,g3)
    c: Vertical(g14)
    c: Coincident(g15,g13)
    c: Vertical(g15)
    c: Tangent(g15,g1)
    c: Distance(g14) = 2
    c: Coincident(g16,g14)
    c: Horizontal(g16)
    c: Coincident(g15,g16)
FEATURE [Part::Feature] Face050
  shape: bbox 4.8 x 25.5 x 2e-07 mm, 1 faces, 0 solids (baked)
FEATURE [Part::Revolution] Revolve054  label="moreFrontCaseScrewPost001"
  Angle = 360
  Axis = (0,1,0)
  Base = (0,0,0)
  FaceMakerClass = Part::FaceMakerBullseye
  Placement = pos=(102.5,4.5,3.5) rot=(0,0,1;0rad)
  Solid = false
  Source = -> Face050
  Symmetric = false
FEATURE [Part::Feature] Face051
  shape: bbox 4.8 x 25.5 x 2e-07 mm, 1 faces, 0 solids (baked)
FEATURE [Part::Revolution] Revolve055  label="moreFrontCaseScrewPost002"
  Angle = 360
  Axis = (0,1,0)
  Base = (0,0,0)
  FaceMakerClass = Part::FaceMakerBullseye
  Placement = pos=(102.5,4.5,68.5) rot=(0,0,1;0rad)
  Solid = false
  Source = -> Face051
  Symmetric = false
FEATURE [Sketcher::SketchObject] Sketch027
  FullyConstrained = true
  sketch-geometry (10):
    g0: LineSegment StartX=-1.6 StartY=4.7 StartZ=0 EndX=-1.6 EndY=1.7 EndZ=0
    g1: LineSegment StartX=-3.5 StartY=4.7 StartZ=0 EndX=-1.6 EndY=4.7 EndZ=0
    g2: LineSegment StartX=-1.6 StartY=1.7 StartZ=0 EndX=-1.6 EndY=1.5 EndZ=0
    g3: LineSegment StartX=-1.6 StartY=1.5 StartZ=0 EndX=-5.2 EndY=1.5 EndZ=0
    g4: Circle CenterX=-3.5 CenterY=4.7 CenterZ=0 NormalX=0 NormalY=0 NormalZ=1 AngleXU=0 Radius=1
    g5: Circle CenterX=-3.59627 CenterY=2.99743 CenterZ=0 NormalX=0 NormalY=0 NormalZ=1 AngleXU=0 Radius=1
    g6: Circle CenterX=-5.2 CenterY=1.5 CenterZ=0 NormalX=0 NormalY=0 NormalZ=1 AngleXU=0 Radius=1
    g7: BSplineCurve PolesCount=3 KnotsCount=2 Degree=2 IsPeriodic=0
    g8: GeomPoint X=-3.5 Y=4.7 Z=0
    g9: GeomPoint X=-5.2 Y=1.5 Z=0
  constraints (23):
    c: Vertical(g0)
    c: Distance(g0) = 3
    c: Coincident(g1,g0)
    c: Horizontal(g1)
    c: Block(g0)
    c: Block(g1)
    c: Coincident(g2,g0)
    c: Vertical(g2)
    c: Distance(g2) = 0.2
    c: Coincident(g3,g2)
    c: Horizontal(g3)
    c: Block(g3)
    c: Coincident(g7,g1)
    c: Weight(g4) = 1
    c: Equal(g4,g5)
    c: Equal(g4,g6)
    c: Coincident(g7,g3)
    c: InternalAlignment(g4,g7)
    c: InternalAlignment(g5,g7)
    c: InternalAlignment(g6,g7)
    c: InternalAlignment(g8,g7)
    c: InternalAlignment(g9,g7)
    c: Block(g7)
FEATURE [Sketcher::SketchObject] Sketch028
  FullyConstrained = true
  sketch-geometry (18):
    g0: LineSegment StartX=0 StartY=3e-16 StartZ=0 EndX=0 EndY=1.7 EndZ=0
    g1: LineSegment StartX=-3.5 StartY=0 StartZ=0 EndX=-3.5 EndY=0.9 EndZ=0
    g2: Circle CenterX=-2.7 CenterY=1.7 CenterZ=0 NormalX=0 NormalY=0 NormalZ=1 AngleXU=0 Radius=1
    g3: Circle CenterX=-3.5 CenterY=1.7 CenterZ=0 NormalX=0 NormalY=0 NormalZ=1 AngleXU=0 Radius=1
    g4: Circle CenterX=-3.5 CenterY=0.9 CenterZ=0 NormalX=0 NormalY=0 NormalZ=1 AngleXU=0 Radius=1
    g5: BSplineCurve PolesCount=3 KnotsCount=2 Degree=2 IsPeriodic=0
    g6: GeomPoint X=-2.7 Y=1.7 Z=0
    g7: GeomPoint X=-3.5 Y=0.9 Z=0
    g8: LineSegment StartX=-3.5 StartY=0 StartZ=0 EndX=-3.5 EndY=-7 EndZ=0
    g9: LineSegment StartX=0 StartY=3e-16 StartZ=0 EndX=0 EndY=-7 EndZ=0
    g10: LineSegment StartX=-3.5 StartY=-7 StartZ=0 EndX=0 EndY=-7 EndZ=0
    g11: LineSegment StartX=-2.7 StartY=1.7 StartZ=0 EndX=-1.6 EndY=1.7 EndZ=0
    g12: LineSegment StartX=0 StartY=1.7 StartZ=0 EndX=0 EndY=4.5 EndZ=0
    g13: LineSegment StartX=0 StartY=4.5 StartZ=0 EndX=0 EndY=10.8 EndZ=0
    g14: LineSegment StartX=0 StartY=10.8 StartZ=0 EndX=-2 EndY=10.8 EndZ=0
    g15: LineSegment StartX=-1.6 StartY=4.7 StartZ=0 EndX=-1.6 EndY=1.7 EndZ=0
    g16: LineSegment StartX=-1.6 StartY=4.7 StartZ=0 EndX=-2 EndY=4.7 EndZ=0
    g17: LineSegment StartX=-2 StartY=4.7 StartZ=0 EndX=-2 EndY=10.8 EndZ=0
  constraints (44):
    c: Vertical(g0)
    c: Vertical(g1)
    c: Distance(g1) = 0.9
    c: Block(g0)
    c: Distance(g0) = 1.7
    c: Weight(g2) = 1
    c: Equal(g2,g3)
    c: Equal(g2,g4)
    c: Coincident(g5,g1)
    c: InternalAlignment(g2,g5)
    c: InternalAlignment(g3,g5)
    c: InternalAlignment(g4,g5)
    c: InternalAlignment(g6,g5)
    c: InternalAlignment(g7,g5)
    c: Block(g5)
    c: Coincident(g8,g1)
    c: Vertical(g8)
    c: Distance(g8) = 7
    c: Vertical(g9)
    c: Equal(g8,g9) = 7
    c: Coincident(g9,g0)
    c: Coincident(g10,g8)
    c: Coincident(g10,g9)
    c: Horizontal(g10)
    c: Coincident(g11,g5)
    c: Horizontal(g11)
    c: Coincident(g12,g0)
    c: Vertical(g12)
    c: Distance(g12) = 2.8
    c: Coincident(g13,g12)
    c: Vertical(g13)
    c: Distance(g13) = 6.3
    c: Coincident(g14,g13)
    c: Horizontal(g14)
    c: Distance(g14) = 2
    c: Vertical(g15)
    c: Distance(g15) = 3
    c: Block(g11)
    c: Coincident(g15,g11)
    c: Coincident(g16,g15)
    c: Horizontal(g16)
    c: Coincident(g17,g16)
    c: Coincident(g17,g14)
    c: Vertical(g17)
FEATURE [Part::Revolution] Revolve040  label="backCaseScrewRetainer001"
  Angle = 360
  Axis = (0,1,0)
  Base = (0,0,0)
  FaceMakerClass = Part::FaceMakerBullseye
  Placement = pos=(12.5,3,10) rot=(0,0,1;0rad)
  Solid = false
  Source = -> Face036
  Symmetric = false
FEATURE [Part::Feature] Face055
  shape: bbox 3.5 x 30.2 x 2e-07 mm, 1 faces, 0 solids (baked)
FEATURE [Part::Revolution] Revolve059  label="backCaseScrewPost"
  Angle = 360
  Axis = (0,1,0)
  Base = (0,0,0)
  FaceMakerClass = Part::FaceMakerBullseye
  Placement = pos=(12.5,4.5,10) rot=(0,0,1;0rad)
  Solid = false
  Source = -> Face055
  Symmetric = false
FEATURE [Part::Feature] Face056
  shape: bbox 3.5 x 30.2 x 2e-07 mm, 1 faces, 0 solids (baked)
FEATURE [Part::Revolution] Revolve060  label="backCaseScrewPost001"
  Angle = 360
  Axis = (0,1,0)
  Base = (0,0,0)
  FaceMakerClass = Part::FaceMakerBullseye
  Placement = pos=(12.5,4.5,62) rot=(0,0,1;0rad)
  Solid = false
  Source = -> Face056
  Symmetric = false
FEATURE [Part::Feature] Face057
  shape: bbox 3.5 x 17.8 x 2e-07 mm, 1 faces, 0 solids (baked)
FEATURE [Part::Revolution] Revolve061  label="removeToCreateScrewAndThreadedInsertHole"
  Angle = 360
  Axis = (0,1,0)
  Base = (0,0,0)
  FaceMakerClass = Part::FaceMakerBullseye
  Placement = pos=(12.5,0,10) rot=(0,0,1;0rad)
  Solid = false
  Source = -> Face057
  Symmetric = false
FEATURE [Part::Feature] Face058
  shape: bbox 3.5 x 17.8 x 2e-07 mm, 1 faces, 0 solids (baked)
FEATURE [Part::Revolution] Revolve062  label="removeToCreateScrewAndThreadedInsertHole001"
  Angle = 360
  Axis = (0,1,0)
  Base = (0,0,0)
  FaceMakerClass = Part::FaceMakerBullseye
  Placement = pos=(12.5,0,62) rot=(0,0,1;0rad)
  Solid = false
  Source = -> Face058
  Symmetric = false
FEATURE [Part::Feature] Face059
  shape: bbox 3.5 x 17.8 x 2e-07 mm, 1 faces, 0 solids (baked)
FEATURE [Part::Revolution] Revolve063  label="removeToCreateScrewAndThreadedInsertHole002"
  Angle = 360
  Axis = (0,1,0)
  Base = (0,0,0)
  FaceMakerClass = Part::FaceMakerBullseye
  Placement = pos=(89.5,0,68.5) rot=(0,0,1;0rad)
  Solid = false
  Source = -> Face059
  Symmetric = false
FEATURE [Part::Feature] Face060
  shape: bbox 3.5 x 17.8 x 2e-07 mm, 1 faces, 0 solids (baked)
FEATURE [Part::Revolution] Revolve064  label="removeToCreateScrewAndThreadedInsertHole003"
  Angle = 360
  Axis = (0,1,0)
  Base = (0,0,0)
  FaceMakerClass = Part::FaceMakerBullseye
  Placement = pos=(89.5,0,3.5) rot=(0,0,1;0rad)
  Solid = false
  Source = -> Face060
  Symmetric = false
FEATURE [Part::Feature] Face061
  shape: bbox 3.5 x 17.8 x 2e-07 mm, 1 faces, 0 solids (baked)
FEATURE [Part::Revolution] Revolve065  label="removeToCreateScrewAndThreadedInsertHole004"
  Angle = 360
  Axis = (0,1,0)
  Base = (0,0,0)
  FaceMakerClass = Part::FaceMakerBullseye
  Placement = pos=(102.5,4.7,3.5) rot=(0,0,1;0rad)
  Solid = false
  Source = -> Face061
  Symmetric = false
FEATURE [Part::Feature] Face062
  shape: bbox 3.5 x 17.8 x 2e-07 mm, 1 faces, 0 solids (baked)
FEATURE [Part::Revolution] Revolve066  label="removeToCreateScrewAndThreadedInsertHole005"
  Angle = 360
  Axis = (0,1,0)
  Base = (0,0,0)
  FaceMakerClass = Part::FaceMakerBullseye
  Placement = pos=(102.5,4.7,68.5) rot=(0,0,1;0rad)
  Solid = false
  Source = -> Face062
  Symmetric = false
FEATURE [Part::MultiFuse] Fusion047  label="makeHoles"
  Shapes = -> [Revolve066,Revolve065,Revolve064,Revolve063,Revolve062,Revolve061]
FEATURE [Part::Feature] Face063
  shape: bbox 3.6 x 3.2 x 2e-07 mm, 1 faces, 0 solids (baked)
FEATURE [Part::Revolution] Revolve067  label="moreFrontCaseScrewRetainer002"
  Angle = 360
  Axis = (0,1,0)
  Base = (0,0,0)
  FaceMakerClass = Part::FaceMakerBullseye
  Placement = pos=(102.5,4.5,68.5) rot=(0,0,1;0rad)
  Solid = false
  Source = -> Face063
  Symmetric = false
FEATURE [Part::Feature] Face064
  shape: bbox 3.6 x 3.2 x 2e-07 mm, 1 faces, 0 solids (baked)
FEATURE [Part::Revolution] Revolve068  label="moreFrontCaseScrewRetainer003"
  Angle = 360
  Axis = (0,1,0)
  Base = (0,0,0)
  FaceMakerClass = Part::FaceMakerBullseye
  Placement = pos=(102.5,4.5,3.5) rot=(0,0,1;0rad)
  Solid = false
  Source = -> Face064
  Symmetric = false
FEATURE [Part::Feature] Face065
  shape: bbox 3.5 x 17.8 x 2e-07 mm, 1 faces, 0 solids (baked)
FEATURE [Part::Revolution] Revolve069  label="removeToCreateScrewAndThreadedInsertHole006"
  Angle = 360
  Axis = (0,1,0)
  Base = (0,0,0)
  FaceMakerClass = Part::FaceMakerBullseye
  Placement = pos=(12.5,0,10) rot=(0,0,1;0rad)
  Solid = false
  Source = -> Face065
  Symmetric = false
FEATURE [Part::Feature] Face066
  shape: bbox 3.5 x 17.8 x 2e-07 mm, 1 faces, 0 solids (baked)
FEATURE [Part::Revolution] Revolve070  label="removeToCreateScrewAndThreadedInsertHole007"
  Angle = 360
  Axis = (0,1,0)
  Base = (0,0,0)
  FaceMakerClass = Part::FaceMakerBullseye
  Placement = pos=(12.5,0,62) rot=(0,0,1;0rad)
  Solid = false
  Source = -> Face066
  Symmetric = false
FEATURE [Part::Feature] Face067
  shape: bbox 3.5 x 17.8 x 2e-07 mm, 1 faces, 0 solids (baked)
FEATURE [Part::Revolution] Revolve071  label="removeToCreateScrewAndThreadedInsertHole008"
  Angle = 360
  Axis = (0,1,0)
  Base = (0,0,0)
  FaceMakerClass = Part::FaceMakerBullseye
  Placement = pos=(89.5,0,68.5) rot=(0,0,1;0rad)
  Solid = false
  Source = -> Face067
  Symmetric = false
FEATURE [Part::Feature] Face068
  shape: bbox 3.5 x 17.8 x 2e-07 mm, 1 faces, 0 solids (baked)
FEATURE [Part::Revolution] Revolve072  label="removeToCreateScrewAndThreadedInsertHole009"
  Angle = 360
  Axis = (0,1,0)
  Base = (0,0,0)
  FaceMakerClass = Part::FaceMakerBullseye
  Placement = pos=(89.5,0,3.5) rot=(0,0,1;0rad)
  Solid = false
  Source = -> Face068
  Symmetric = false
FEATURE [Part::Feature] Face069
  shape: bbox 3.5 x 17.8 x 2e-07 mm, 1 faces, 0 solids (baked)
FEATURE [Part::Feature] Face070
  shape: bbox 3.5 x 17.8 x 2e-07 mm, 1 faces, 0 solids (baked)
FEATURE [Part::Revolution] Revolve073  label="removeToCreateScrewAndThreadedInsertHole010"
  Angle = 360
  Axis = (0,1,0)
  Base = (0,0,0)
  FaceMakerClass = Part::FaceMakerBullseye
  Placement = pos=(102.5,4.7,3.5) rot=(0,0,1;0rad)
  Solid = false
  Source = -> Face069
  Symmetric = false
FEATURE [Part::Revolution] Revolve074  label="removeToCreateScrewAndThreadedInsertHole011"
  Angle = 360
  Axis = (0,1,0)
  Base = (0,0,0)
  FaceMakerClass = Part::FaceMakerBullseye
  Placement = pos=(102.5,4.7,68.5) rot=(0,0,1;0rad)
  Solid = false
  Source = -> Face070
  Symmetric = false
FEATURE [Part::MultiFuse] Fusion048  label="makeHoles001"
  Shapes = -> [Revolve074,Revolve073,Revolve072,Revolve071,Revolve070,Revolve069]
FEATURE [Part::MultiFuse] Fusion049  label="caseScrewRetainers"
  Shapes = -> [Revolve067,Revolve068,Revolve048,Revolve047,Revolve039,Revolve040]
FEATURE [Part::Cut] Cut015  label="caseScrewRetainers001"
  Base = -> Fusion049
  Tool = -> Fusion048
FEATURE [Part::MultiFuse] Fusion050  label="casePillars"
  Shapes = -> [Revolve055,Revolve054,Revolve043,Revolve046,Revolve059,Revolve060]
FEATURE [Part::Feature] Face071 .. Face076  x6 (patterned run collapsed; names and placements below)
  shape: bbox 3.5 x 17.8 x 2e-07 mm, 1 faces, 0 solids (baked)
FEATURE [Part::Revolution] Revolve075  label="removeToCreateScrewAndThreadedInsertHole012"
  Angle = 360
  Axis = (0,1,0)
  Base = (0,0,0)
  FaceMakerClass = Part::FaceMakerBullseye
  Placement = pos=(12.5,0,10) rot=(0,0,1;0rad)
  Solid = false
  Source = -> Face071
  Symmetric = false
FEATURE [Part::Revolution] Revolve076  label="removeToCreateScrewAndThreadedInsertHole013"
  Angle = 360
  Axis = (0,1,0)
  Base = (0,0,0)
  FaceMakerClass = Part::FaceMakerBullseye
  Placement = pos=(12.5,0,62) rot=(0,0,1;0rad)
  Solid = false
  Source = -> Face072
  Symmetric = false
FEATURE [Part::Revolution] Revolve077  label="removeToCreateScrewAndThreadedInsertHole014"
  Angle = 360
  Axis = (0,1,0)
  Base = (0,0,0)
  FaceMakerClass = Part::FaceMakerBullseye
  Placement = pos=(89.5,0,68.5) rot=(0,0,1;0rad)
  Solid = false
  Source = -> Face073
  Symmetric = false
FEATURE [Part::Revolution] Revolve078  label="removeToCreateScrewAndThreadedInsertHole015"
  Angle = 360
  Axis = (0,1,0)
  Base = (0,0,0)
  FaceMakerClass = Part::FaceMakerBullseye
  Placement = pos=(89.5,0,3.5) rot=(0,0,1;0rad)
  Solid = false
  Source = -> Face074
  Symmetric = false
FEATURE [Part::Revolution] Revolve079  label="removeToCreateScrewAndThreadedInsertHole016"
  Angle = 360
  Axis = (0,1,0)
  Base = (0,0,0)
  FaceMakerClass = Part::FaceMakerBullseye
  Placement = pos=(102.5,4.7,3.5) rot=(0,0,1;0rad)
  Solid = false
  Source = -> Face075
  Symmetric = false
FEATURE [Part::Revolution] Revolve080  label="removeToCreateScrewAndThreadedInsertHole017"
  Angle = 360
  Axis = (0,1,0)
  Base = (0,0,0)
  FaceMakerClass = Part::FaceMakerBullseye
  Placement = pos=(102.5,4.7,68.5) rot=(0,0,1;0rad)
  Solid = false
  Source = -> Face076
  Symmetric = false
FEATURE [Part::MultiFuse] Fusion051  label="makeHoles002"
  Shapes = -> [Revolve080,Revolve079,Revolve078,Revolve077,Revolve076,Revolve075]
FEATURE [Part::Cut] Cut016  label="caesPillars"
  Base = -> Fusion050
  Tool = -> Fusion051
FEATURE [Part::Revolution] Revolve009  label="plugHousing016"
  Angle = 360
  Axis = (0,1,0)
  Base = (0,0,0)
  FaceMakerClass = Part::FaceMakerBullseye
  Placement = pos=(0,0,36.15) rot=(0,0,1;0rad)
  Solid = false
  Source = -> Face012
  Symmetric = false
FEATURE [Part::MultiFuse] Fusion014  label="plugHousing023"
  Placement = pos=(0,0,0) rot=(0,0,1;1.5708rad)
  Shapes = -> [Revolve011,Revolve009]
FEATURE [Part::Revolution] Revolve010  label="plugHousing017"
  Angle = 360
  Axis = (0,1,0)
  Base = (0,0,0)
  FaceMakerClass = Part::FaceMakerBullseye
  Placement = pos=(0,0,36.15) rot=(0,0,1;0rad)
  Solid = false
  Source = -> Face014
  Symmetric = false
FEATURE [Part::MultiFuse] Fusion015  label="plugHousing024"
  Placement = pos=(0,0,0) rot=(0,0,1;1.5708rad)
  Shapes = -> [Revolve010,Revolve015]
FEATURE [Part::Revolution] Revolve014  label="plugHousing026"
  Angle = 360
  Axis = (0,1,0)
  Base = (0,0,0)
  FaceMakerClass = Part::FaceMakerBullseye
  Placement = pos=(0,0,36.15) rot=(0,0,1;0rad)
  Solid = false
  Source = -> Face011
  Symmetric = false
FEATURE [Part::Revolution] Revolve013  label="plugHousing025"
  Angle = 360
  Axis = (0,1,0)
  Base = (0,0,0)
  FaceMakerClass = Part::FaceMakerBullseye
  Placement = pos=(0,0,36.15) rot=(0,0,1;0rad)
  Solid = false
  Source = -> Face015
  Symmetric = false
FEATURE [Part::MultiFuse] Fusion016  label="plugHousing028"
  Placement = pos=(0,19,0) rot=(0,0,1;3.14159rad)
  Shapes = -> [Fusion014,Fusion013]
FEATURE [Part::MultiFuse] Fusion011  label="plugHousing018"
  Placement = pos=(0,0,0) rot=(0,0,1;1.5708rad)
  Shapes = -> [Revolve014,Revolve013]
FEATURE [Part::MultiFuse] Fusion012  label="plugHousing019"
  Placement = pos=(0,19,0) rot=(0,0,1;3.14159rad)
  Shapes = -> [Fusion011,Fusion015]
FEATURE [Part::MultiFuse] Fusion017  label="plugHousing029"
  Placement = pos=(122.621,0,-0.15) rot=(0,0,1;0rad)
  Shapes = -> [Fusion016,Fusion012]
FEATURE [Part::MultiFuse] Fusion052  label="casePillarRetainers"
  Shapes = -> [Extrude012,Extrude013,Extrude014,Extrude015,Extrude016,Extrude017,Extrude018,Extrude019,Box011,Box012]
FEATURE [Part::Feature] Face077
  shape: bbox 3.5 x 17.8 x 2e-07 mm, 1 faces, 0 solids (baked)
FEATURE [Part::Revolution] Revolve081  label="removeToCreateScrewAndThreadedInsertHole018"
  Angle = 360
  Axis = (0,1,0)
  Base = (0,0,0)
  FaceMakerClass = Part::FaceMakerBullseye
  Placement = pos=(62.3,30.3,19.7) rot=(0,0,1;0rad)
  Solid = false
  Source = -> Face077
  Symmetric = false
FEATURE [Part::Feature] Face078
  shape: bbox 3.5 x 17.8 x 2e-07 mm, 1 faces, 0 solids (baked)
FEATURE [Part::Revolution] Revolve082  label="removeToCreateScrewAndThreadedInsertHole019"
  Angle = 360
  Axis = (0,1,0)
  Base = (0,0,0)
  FaceMakerClass = Part::FaceMakerBullseye
  Placement = pos=(62.3,30.3,51.7) rot=(0,0,1;0rad)
  Solid = false
  Source = -> Face078
  Symmetric = false
FEATURE [Part::Feature] Face079
  shape: bbox 3.5 x 17.8 x 2e-07 mm, 1 faces, 0 solids (baked)
FEATURE [Part::Revolution] Revolve083  label="removeToCreateScrewAndThreadedInsertHole020"
  Angle = 360
  Axis = (0,1,0)
  Base = (0,0,0)
  FaceMakerClass = Part::FaceMakerBullseye
  Placement = pos=(30.3,30.3,19.7) rot=(0,0,1;0rad)
  Solid = false
  Source = -> Face079
  Symmetric = false
FEATURE [Part::Feature] Face080
  shape: bbox 3.5 x 17.8 x 2e-07 mm, 1 faces, 0 solids (baked)
FEATURE [Part::Revolution] Revolve084  label="removeToCreateScrewAndThreadedInsertHole021"
  Angle = 360
  Axis = (0,1,0)
  Base = (0,0,0)
  FaceMakerClass = Part::FaceMakerBullseye
  Placement = pos=(30.3,30.3,51.7) rot=(0,0,1;0rad)
  Solid = false
  Source = -> Face080
  Symmetric = false
FEATURE [Part::MultiFuse] Fusion053  label="createThreadedInsertHolesForFan"
  Shapes = -> [Revolve081,Revolve082,Revolve083,Revolve084]
FEATURE [Part::Cut] Cut017  label="fanScrewHousing001"
  Base = -> Fusion046
  Tool = -> Fusion053
FEATURE [Part::Feature] Face081
  shape: bbox 3.5 x 17.8 x 2e-07 mm, 1 faces, 0 solids (baked)
FEATURE [Part::Revolution] Revolve085  label="removeToCreateScrewAndThreadedInsertHole022"
  Angle = 360
  Axis = (0,1,0)
  Base = (0,0,0)
  FaceMakerClass = Part::FaceMakerBullseye
  Placement = pos=(62.3,30.3,19.7) rot=(0,0,1;0rad)
  Solid = false
  Source = -> Face081
  Symmetric = false
FEATURE [Part::Feature] Face082
  shape: bbox 3.5 x 17.8 x 2e-07 mm, 1 faces, 0 solids (baked)
FEATURE [Part::Revolution] Revolve086  label="removeToCreateScrewAndThreadedInsertHole023"
  Angle = 360
  Axis = (0,1,0)
  Base = (0,0,0)
  FaceMakerClass = Part::FaceMakerBullseye
  Placement = pos=(62.3,30.3,51.7) rot=(0,0,1;0rad)
  Solid = false
  Source = -> Face082
  Symmetric = false
FEATURE [Part::Feature] Face083
  shape: bbox 3.5 x 17.8 x 2e-07 mm, 1 faces, 0 solids (baked)
FEATURE [Part::Revolution] Revolve087  label="removeToCreateScrewAndThreadedInsertHole024"
  Angle = 360
  Axis = (0,1,0)
  Base = (0,0,0)
  FaceMakerClass = Part::FaceMakerBullseye
  Placement = pos=(30.3,30.3,19.7) rot=(0,0,1;0rad)
  Solid = false
  Source = -> Face083
  Symmetric = false
FEATURE [Part::Feature] Face084
  shape: bbox 3.5 x 17.8 x 2e-07 mm, 1 faces, 0 solids (baked)
FEATURE [Part::Revolution] Revolve088  label="removeToCreateScrewAndThreadedInsertHole025"
  Angle = 360
  Axis = (0,1,0)
  Base = (0,0,0)
  FaceMakerClass = Part::FaceMakerBullseye
  Placement = pos=(30.3,30.3,51.7) rot=(0,0,1;0rad)
  Solid = false
  Source = -> Face084
  Symmetric = false
FEATURE [Part::MultiFuse] Fusion054  label="createThreadedInsertHolesForFan001"
  Shapes = -> [Revolve085,Revolve086,Revolve087,Revolve088]
FEATURE [Part::Cut] Cut018  label="top007"
  Base = -> Fusion040
  Tool = -> Fusion054
FEATURE [Sketcher::SketchObject] Sketch029
  FullyConstrained = false
  Placement = pos=(0,0,0) rot=(1,0,0;1.5708rad)
  sketch-geometry (24):
    g0: ArcOfCircle CenterX=-4 CenterY=-10.5 CenterZ=0 NormalX=0 NormalY=0 NormalZ=1 AngleXU=0 Radius=1.5 StartAngle=6e-16 EndAngle=3.14159
    g1: ArcOfCircle CenterX=-34.2 CenterY=-10.5 CenterZ=0 NormalX=0 NormalY=0 NormalZ=1 AngleXU=0 Radius=1.5 StartAngle=0 EndAngle=3.14159
    g2: ArcOfCircle CenterX=-34.2 CenterY=-27.7 CenterZ=0 NormalX=0 NormalY=0 NormalZ=1 AngleXU=0 Radius=1.5 StartAngle=3.14159 EndAngle=6.28319
    g3: ArcOfCircle CenterX=-4 CenterY=-27.7 CenterZ=0 NormalX=0 NormalY=0 NormalZ=1 AngleXU=0 Radius=1.5 StartAngle=3.1416 EndAngle=6.28319
    g4: ArcOfCircle CenterX=-10 CenterY=-4.3 CenterZ=0 NormalX=0 NormalY=0 NormalZ=1 AngleXU=0 Radius=1.5 StartAngle=2e-16 EndAngle=3.14159
    g5: ArcOfCircle CenterX=-16.1 CenterY=-1.8 CenterZ=0 NormalX=0 NormalY=0 NormalZ=1 AngleXU=0 Radius=1.5 StartAngle=5e-16 EndAngle=3.14159
    g6: ArcOfCircle CenterX=-22.1 CenterY=-1.8 CenterZ=0 NormalX=0 NormalY=0 NormalZ=1 AngleXU=0 Radius=1.5 StartAngle=5e-16 EndAngle=3.14159
    g7: ArcOfCircle CenterX=-28.2 CenterY=-4.3 CenterZ=0 NormalX=0 NormalY=0 NormalZ=1 AngleXU=0 Radius=1.5 StartAngle=2e-16 EndAngle=3.14159
    g8: ArcOfCircle CenterX=-10 CenterY=-33.9 CenterZ=0 NormalX=0 NormalY=0 NormalZ=1 AngleXU=0 Radius=1.5 StartAngle=3.14159 EndAngle=6.28319
    g9: ArcOfCircle CenterX=-16.1 CenterY=-36.4 CenterZ=0 NormalX=0 NormalY=0 NormalZ=1 AngleXU=0 Radius=1.5 StartAngle=3.14159 EndAngle=6.28319
    g10: ArcOfCircle CenterX=-22.1 CenterY=-36.4 CenterZ=0 NormalX=0 NormalY=0 NormalZ=1 AngleXU=0 Radius=1.5 StartAngle=3.14159 EndAngle=6.28319
    g11: ArcOfCircle CenterX=-28.2 CenterY=-33.9 CenterZ=0 NormalX=0 NormalY=0 NormalZ=1 AngleXU=0 Radius=1.5 StartAngle=3.14159 EndAngle=6.28319
    g12: LineSegment StartX=-35.7 StartY=-10.5 StartZ=0 EndX=-35.7 EndY=-27.7 EndZ=0
    g13: LineSegment StartX=-32.7 StartY=-10.5 StartZ=0 EndX=-32.7 EndY=-27.7 EndZ=0
    g14: LineSegment StartX=-29.7 StartY=-33.9 StartZ=0 EndX=-29.7 EndY=-4.3 EndZ=0
    g15: LineSegment StartX=-26.7 StartY=-33.9 StartZ=0 EndX=-26.7 EndY=-4.3 EndZ=0
    g16: LineSegment StartX=-2.5 StartY=-10.5 StartZ=0 EndX=-2.5 EndY=-27.7 EndZ=0
    g17: LineSegment StartX=-8.5 StartY=-4.3 StartZ=0 EndX=-8.5 EndY=-33.9 EndZ=0
    g18: LineSegment StartX=-5.5 StartY=-10.5 StartZ=0 EndX=-5.5 EndY=-27.7 EndZ=0
    g19: LineSegment StartX=-11.5 StartY=-4.3 StartZ=0 EndX=-11.5 EndY=-33.9 EndZ=0
    g20: LineSegment StartX=-14.6 StartY=-1.8 StartZ=0 EndX=-14.6 EndY=-36.4 EndZ=0
    g21: LineSegment StartX=-17.6 StartY=-1.8 StartZ=0 EndX=-17.6 EndY=-36.4 EndZ=0
    g22: LineSegment StartX=-20.6 StartY=-36.4 StartZ=0 EndX=-20.6 EndY=-1.8 EndZ=0
    g23: LineSegment StartX=-23.6 StartY=-1.8 StartZ=0 EndX=-23.6 EndY=-36.4 EndZ=0
  constraints (48):
    c: Block(g0)
    c: Block(g1)
    c: Block(g2)
    c: Block(g3)
    c: Block(g4)
    c: Block(g5)
    c: Block(g6)
    c: Block(g7)
    c: Block(g8)
    c: Block(g9)
    c: Block(g10)
    c: Block(g11)
    c: Coincident(g12,g1)
    c: Coincident(g12,g2)
    c: Vertical(g12)
    c: Coincident(g13,g1)
    c: Coincident(g13,g2)
    c: Vertical(g13)
    c: Coincident(g14,g11)
    c: Coincident(g14,g7)
    c: Vertical(g14)
    c: Coincident(g15,g11)
    c: Coincident(g15,g7)
    c: Vertical(g15)
    c: Coincident(g16,g0)
    c: Coincident(g16,g3)
    c: Vertical(g16)
    c: Coincident(g17,g4)
    c: Coincident(g17,g8)
    c: Vertical(g17)
    c: Coincident(g18,g0)
    c: Coincident(g18,g3)
    c: Vertical(g18)
    c: Coincident(g19,g4)
    c: Coincident(g19,g8)
    c: Vertical(g19)
    c: Coincident(g20,g5)
    c: Coincident(g20,g9)
    c: Vertical(g20)
    c: Coincident(g21,g5)
    c: Coincident(g21,g9)
    c: Vertical(g21)
    c: Coincident(g22,g10)
    c: Coincident(g22,g6)
    c: Vertical(g22)
    c: Coincident(g23,g6)
    c: Coincident(g23,g10)
    c: Vertical(g23)
FEATURE [Part::Extrusion] Extrude020  label="removeToCreateFanGrillHoles"
  Base = -> Sketch029
  Dir = (0,-1,6e-16)
  DirMode = 2
  FaceMakerClass = Part::FaceMakerBullseye
  LengthFwd = 10
  LengthRev = 0
  Placement = pos=(65.4,44,54.82) rot=(0,0,1;0rad)
  Solid = true
  Symmetric = false
FEATURE [Part::MultiFuse] Fusion055  label="top008"
  Shapes = -> [Cut017,Cut018]
FEATURE [Part::Cut] Cut019  label="top009"
  Base = -> Fusion055
  Tool = -> Extrude020
FEATURE [App::MeasureDistance] Distance003  label="Distance: 71.95 mm"
  Distance = 71.9513
  P1 = (117,38,72)
  P2 = (117,38,0.0487319)
FEATURE [Sketcher::SketchObject] Sketch030
  FullyConstrained = true
  Placement = pos=(117,19,0) rot=(0.57735,0.57735,0.57735;2.0944rad)
  sketch-geometry (48):
    g0: LineSegment StartX=-49.19 StartY=69.25 StartZ=0 EndX=-49.19 EndY=66.25 EndZ=0
    g1: LineSegment StartX=-49.19 StartY=63.5 StartZ=0 EndX=-49.19 EndY=60.5 EndZ=0
    g2: LineSegment StartX=-49.19 StartY=57.75 StartZ=0 EndX=-49.19 EndY=54.75 EndZ=0
    g3: LineSegment StartX=-49.19 StartY=52 StartZ=0 EndX=-49.19 EndY=49 EndZ=0
    g4: LineSegment StartX=-49.19 StartY=46.25 StartZ=0 EndX=-49.19 EndY=43.25 EndZ=0
    g5: LineSegment StartX=-49.19 StartY=40.5 StartZ=0 EndX=-49.19 EndY=37.5 EndZ=0
    g6: LineSegment StartX=-49.19 StartY=34.5 StartZ=0 EndX=-49.19 EndY=31.5 EndZ=0
    g7: LineSegment StartX=-49.19 StartY=28.75 StartZ=0 EndX=-49.19 EndY=25.75 EndZ=0
    g8: LineSegment StartX=-49.19 StartY=23 StartZ=0 EndX=-49.19 EndY=20 EndZ=0
    g9: LineSegment StartX=-49.19 StartY=17.25 StartZ=0 EndX=-49.19 EndY=14.25 EndZ=0
    g10: LineSegment StartX=-49.19 StartY=11.5 StartZ=0 EndX=-49.19 EndY=8.5 EndZ=0
    g11: LineSegment StartX=-49.19 StartY=5.75 StartZ=0 EndX=-49.19 EndY=2.75 EndZ=0
    g12: ArcOfCircle CenterX=-1.5 CenterY=67.75 CenterZ=0 NormalX=0 NormalY=0 NormalZ=1 AngleXU=0 Radius=1.5 StartAngle=4.71239 EndAngle=7.85398
    g13: ArcOfCircle CenterX=-1.5 CenterY=62 CenterZ=0 NormalX=0 NormalY=0 NormalZ=1 AngleXU=0 Radius=1.5 StartAngle=4.71239 EndAngle=7.85398
    g14: ArcOfCircle CenterX=-1.5 CenterY=56.25 CenterZ=0 NormalX=0 NormalY=0 NormalZ=1 AngleXU=0 Radius=1.5 StartAngle=4.71239 EndAngle=7.85398
    g15: ArcOfCircle CenterX=-11.49 CenterY=50.5 CenterZ=0 NormalX=0 NormalY=0 NormalZ=1 AngleXU=0 Radius=1.5 StartAngle=4.71239 EndAngle=7.85398
    g16: ArcOfCircle CenterX=-16.28 CenterY=44.75 CenterZ=0 NormalX=0 NormalY=0 NormalZ=1 AngleXU=0 Radius=1.5 StartAngle=4.71239 EndAngle=7.85398
    g17: ArcOfCircle CenterX=-18.2337 CenterY=39 CenterZ=0 NormalX=0 NormalY=0 NormalZ=1 AngleXU=0 Radius=1.5 StartAngle=4.71485 EndAngle=7.85398
    g18: ArcOfCircle CenterX=-16.2837 CenterY=27.25 CenterZ=0 NormalX=0 NormalY=0 NormalZ=1 AngleXU=0 Radius=1.5 StartAngle=4.71485 EndAngle=7.85398
    g19: ArcOfCircle CenterX=-18.2337 CenterY=33 CenterZ=0 NormalX=0 NormalY=0 NormalZ=1 AngleXU=0 Radius=1.5 StartAngle=4.71485 EndAngle=7.85398
    g20: ArcOfCircle CenterX=-11.49 CenterY=21.5 CenterZ=0 NormalX=0 NormalY=0 NormalZ=1 AngleXU=0 Radius=1.5 StartAngle=4.71239 EndAngle=7.85398
    g21: ArcOfCircle CenterX=-1.5 CenterY=4.25 CenterZ=0 NormalX=0 NormalY=0 NormalZ=1 AngleXU=0 Radius=1.5 StartAngle=4.71239 EndAngle=7.85398
    g22: ArcOfCircle CenterX=-1.5 CenterY=10 CenterZ=0 NormalX=0 NormalY=0 NormalZ=1 AngleXU=0 Radius=1.5 StartAngle=4.71239 EndAngle=7.85398
    g23: ArcOfCircle CenterX=-1.5 CenterY=15.75 CenterZ=0 NormalX=0 NormalY=0 NormalZ=1 AngleXU=0 Radius=1.5 StartAngle=4.71239 EndAngle=7.85398
    g24: LineSegment StartX=-49.19 StartY=69.25 StartZ=0 EndX=-1.5 EndY=69.25 EndZ=0
    g25: LineSegment StartX=-49.19 StartY=66.25 StartZ=0 EndX=-1.5 EndY=66.25 EndZ=0
    g26: LineSegment StartX=-49.19 StartY=63.5 StartZ=0 EndX=-1.5 EndY=63.5 EndZ=0
    g27: LineSegment StartX=-49.19 StartY=60.5 StartZ=0 EndX=-1.5 EndY=60.5 EndZ=0
    g28: LineSegment StartX=-49.19 StartY=57.75 StartZ=0 EndX=-1.5 EndY=57.75 EndZ=0
    g29: LineSegment StartX=-49.19 StartY=54.75 StartZ=0 EndX=-1.5 EndY=54.75 EndZ=0
    g30: LineSegment StartX=-49.19 StartY=52 StartZ=0 EndX=-11.49 EndY=52 EndZ=0
    g31: LineSegment StartX=-49.19 StartY=49 StartZ=0 EndX=-11.49 EndY=49 EndZ=0
    g32: LineSegment StartX=-49.19 StartY=46.25 StartZ=0 EndX=-16.28 EndY=46.25 EndZ=0
    g33: LineSegment StartX=-49.19 StartY=43.25 StartZ=0 EndX=-16.28 EndY=43.25 EndZ=0
    g34: LineSegment StartX=-49.19 StartY=40.5 StartZ=0 EndX=-18.2337 EndY=40.5 EndZ=0
    g35: LineSegment StartX=-49.19 StartY=37.5 StartZ=0 EndX=-18.23 EndY=37.5 EndZ=0
    g36: LineSegment StartX=-49.19 StartY=34.5 StartZ=0 EndX=-18.2337 EndY=34.5 EndZ=0
    g37: LineSegment StartX=-49.19 StartY=31.5 StartZ=0 EndX=-18.23 EndY=31.5 EndZ=0
    g38: LineSegment StartX=-49.19 StartY=28.75 StartZ=0 EndX=-16.2837 EndY=28.75 EndZ=0
    g39: LineSegment StartX=-49.19 StartY=25.75 StartZ=0 EndX=-16.28 EndY=25.75 EndZ=0
    g40: LineSegment StartX=-49.19 StartY=23 StartZ=0 EndX=-11.49 EndY=23 EndZ=0
    g41: LineSegment StartX=-49.19 StartY=20 StartZ=0 EndX=-11.49 EndY=20 EndZ=0
    g42: LineSegment StartX=-49.19 StartY=17.25 StartZ=0 EndX=-1.5 EndY=17.25 EndZ=0
    g43: LineSegment StartX=-49.19 StartY=14.25 StartZ=0 EndX=-1.5 EndY=14.25 EndZ=0
    g44: LineSegment StartX=-49.19 StartY=11.5 StartZ=0 EndX=-1.5 EndY=11.5 EndZ=0
    g45: LineSegment StartX=-49.19 StartY=8.5 StartZ=0 EndX=-1.5 EndY=8.5 EndZ=0
    g46: LineSegment StartX=-49.19 StartY=5.75 StartZ=0 EndX=-1.5 EndY=5.75 EndZ=0
    g47: LineSegment StartX=-49.19 StartY=2.75 StartZ=0 EndX=-1.5 EndY=2.75 EndZ=0
  constraints (120):
    c: Vertical(g0)
    c: Distance(g0) = 3
    c: Block(g0)
    c: Vertical(g1)
    c: Distance(g1) = 3
    c: Vertical(g2)
    c: Equal(g0,g2) = 3
    c: Block(g2)
    c: Vertical(g3)
    c: Equal(g1,g3) = 3
    c: Vertical(g4)
    c: Equal(g0,g4) = 3
    c: Block(g4)
    c: Vertical(g5)
    c: Equal(g1,g5) = 3
    c: Vertical(g6)
    c: Equal(g0,g6) = 3
    c: Block(g6)
    c: Vertical(g7)
    c: Equal(g1,g7) = 3
    c: Vertical(g8)
    c: Equal(g0,g8) = 3
    c: Block(g8)
    c: Vertical(g9)
    c: Equal(g1,g9) = 3
    c: Vertical(g10)
    c: Equal(g0,g10) = 3
    c: Block(g10)
    c: Vertical(g11)
    c: Equal(g1,g11) = 3
    c: Block(g12)
    c: Block(g13)
    c: Block(g14)
    c: Block(g15)
    c: Block(g16)
    c: Block(g17)
    c: Block(g18)
    c: Block(g19)
    c: Block(g20)
    c: Block(g21)
    c: Block(g22)
    c: Block(g23)
    c: Block(g11)
    c: Block(g9)
    c: Block(g7)
    c: Block(g5)
    c: Block(g3)
    c: Block(g1)
    c: Coincident(g24,g0)
    c: Coincident(g24,g12)
    c: Horizontal(g24)
    c: Coincident(g25,g0)
    c: Coincident(g25,g12)
    c: Horizontal(g25)
    c: Coincident(g26,g1)
    c: Coincident(g26,g13)
    c: Horizontal(g26)
    c: Coincident(g27,g1)
    c: Coincident(g27,g13)
    c: Horizontal(g27)
    c: Coincident(g28,g2)
    c: Coincident(g28,g14)
    c: Horizontal(g28)
    c: Coincident(g29,g2)
    c: Coincident(g29,g14)
    c: Horizontal(g29)
    c: Coincident(g30,g3)
    c: Coincident(g30,g15)
    c: Horizontal(g30)
    c: Coincident(g31,g3)
    c: Coincident(g31,g15)
    c: Horizontal(g31)
    c: Coincident(g32,g4)
    c: Coincident(g32,g16)
    c: Horizontal(g32)
    c: Coincident(g33,g4)
    c: Coincident(g33,g16)
    c: Horizontal(g33)
    c: Coincident(g34,g5)
    c: Coincident(g34,g17)
    c: Horizontal(g34)
    c: Coincident(g35,g5)
    c: Coincident(g35,g17)
    c: Horizontal(g35)
    c: Coincident(g36,g6)
    c: Coincident(g36,g19)
    c: Horizontal(g36)
    c: Coincident(g37,g6)
    c: Coincident(g37,g19)
    c: Horizontal(g37)
    c: Coincident(g38,g7)
    c: Coincident(g38,g18)
    c: Horizontal(g38)
    c: Coincident(g39,g7)
    c: Coincident(g39,g18)
    c: Horizontal(g39)
    c: Coincident(g40,g8)
    c: Coincident(g40,g20)
    c: Horizontal(g40)
    c: Coincident(g41,g8)
    c: Coincident(g41,g20)
    c: Horizontal(g41)
    c: Coincident(g42,g9)
    c: Coincident(g42,g23)
    c: Horizontal(g42)
    c: Coincident(g43,g9)
    c: Coincident(g43,g23)
    c: Horizontal(g43)
    c: Coincident(g44,g10)
    c: Coincident(g44,g22)
    c: Horizontal(g44)
    c: Coincident(g45,g10)
    c: Coincident(g45,g22)
    c: Horizontal(g45)
    c: Coincident(g46,g11)
    c: Coincident(g46,g21)
    c: Horizontal(g46)
    c: Coincident(g47,g11)
    c: Coincident(g47,g21)
    c: Horizontal(g47)
FEATURE [Sketcher::SketchObject] Sketch031
  FullyConstrained = true
  Placement = pos=(117,19,0) rot=(0.57735,0.57735,0.57735;2.0944rad)
  sketch-geometry (24):
    g0: ArcOfCircle CenterX=-49.19 CenterY=67.75 CenterZ=0 NormalX=0 NormalY=0 NormalZ=1 AngleXU=0 Radius=1.5 StartAngle=1.5708 EndAngle=4.71239
    g1: ArcOfCircle CenterX=-49.19 CenterY=62 CenterZ=0 NormalX=0 NormalY=0 NormalZ=1 AngleXU=0 Radius=1.5 StartAngle=1.5708 EndAngle=4.71239
    g2: ArcOfCircle CenterX=-49.19 CenterY=56.25 CenterZ=0 NormalX=0 NormalY=0 NormalZ=1 AngleXU=0 Radius=1.5 StartAngle=1.5708 EndAngle=4.71239
    g3: ArcOfCircle CenterX=-49.19 CenterY=50.5 CenterZ=0 NormalX=0 NormalY=0 NormalZ=1 AngleXU=0 Radius=1.5 StartAngle=1.5708 EndAngle=4.71239
    g4: ArcOfCircle CenterX=-49.19 CenterY=44.75 CenterZ=0 NormalX=0 NormalY=0 NormalZ=1 AngleXU=0 Radius=1.5 StartAngle=1.5708 EndAngle=4.71239
    g5: ArcOfCircle CenterX=-49.19 CenterY=39 CenterZ=0 NormalX=0 NormalY=0 NormalZ=1 AngleXU=0 Radius=1.5 StartAngle=1.5708 EndAngle=4.71239
    g6: ArcOfCircle CenterX=-49.19 CenterY=33 CenterZ=0 NormalX=0 NormalY=0 NormalZ=1 AngleXU=0 Radius=1.5 StartAngle=1.5708 EndAngle=4.71239
    g7: ArcOfCircle CenterX=-49.19 CenterY=27.25 CenterZ=0 NormalX=0 NormalY=0 NormalZ=1 AngleXU=0 Radius=1.5 StartAngle=1.5708 EndAngle=4.71239
    g8: ArcOfCircle CenterX=-49.19 CenterY=21.5 CenterZ=0 NormalX=0 NormalY=0 NormalZ=1 AngleXU=0 Radius=1.5 StartAngle=1.5708 EndAngle=4.71239
    g9: ArcOfCircle CenterX=-49.19 CenterY=15.75 CenterZ=0 NormalX=0 NormalY=0 NormalZ=1 AngleXU=0 Radius=1.5 StartAngle=1.5708 EndAngle=4.71239
    g10: ArcOfCircle CenterX=-49.19 CenterY=10 CenterZ=0 NormalX=0 NormalY=0 NormalZ=1 AngleXU=0 Radius=1.5 StartAngle=1.5708 EndAngle=4.71239
    g11: ArcOfCircle CenterX=-49.19 CenterY=4.25 CenterZ=0 NormalX=0 NormalY=0 NormalZ=1 AngleXU=0 Radius=1.5 StartAngle=1.5708 EndAngle=4.71239
    g12: LineSegment StartX=-49.19 StartY=69.25 StartZ=0 EndX=-49.19 EndY=66.25 EndZ=0
    g13: LineSegment StartX=-49.19 StartY=63.5 StartZ=0 EndX=-49.19 EndY=60.5 EndZ=0
    g14: LineSegment StartX=-49.19 StartY=57.75 StartZ=0 EndX=-49.19 EndY=54.75 EndZ=0
    g15: LineSegment StartX=-49.19 StartY=52 StartZ=0 EndX=-49.19 EndY=49 EndZ=0
    g16: LineSegment StartX=-49.19 StartY=46.25 StartZ=0 EndX=-49.19 EndY=43.25 EndZ=0
    g17: LineSegment StartX=-49.19 StartY=40.5 StartZ=0 EndX=-49.19 EndY=37.5 EndZ=0
    g18: LineSegment StartX=-49.19 StartY=34.5 StartZ=0 EndX=-49.19 EndY=31.5 EndZ=0
    g19: LineSegment StartX=-49.19 StartY=28.75 StartZ=0 EndX=-49.19 EndY=25.75 EndZ=0
    g20: LineSegment StartX=-49.19 StartY=23 StartZ=0 EndX=-49.19 EndY=20 EndZ=0
    g21: LineSegment StartX=-49.19 StartY=17.25 StartZ=0 EndX=-49.19 EndY=14.25 EndZ=0
    g22: LineSegment StartX=-49.19 StartY=11.5 StartZ=0 EndX=-49.19 EndY=8.5 EndZ=0
    g23: LineSegment StartX=-49.19 StartY=5.75 StartZ=0 EndX=-49.19 EndY=2.75 EndZ=0
  constraints (48):
    c: Block(g0)
    c: Block(g1)
    c: Block(g2)
    c: Block(g3)
    c: Block(g4)
    c: Block(g5)
    c: Block(g6)
    c: Block(g7)
    c: Block(g8)
    c: Block(g9)
    c: Block(g10)
    c: Block(g11)
    c: Coincident(g12,g0)
    c: Coincident(g12,g0)
    c: Vertical(g12)
    c: Vertical(g13)
    c: Coincident(g13,g1)
    c: Vertical(g14)
    c: Coincident(g14,g2)
    c: Vertical(g15)
    c: Coincident(g15,g3)
    c: Vertical(g16)
    c: Coincident(g16,g4)
    c: Vertical(g17)
    c: Coincident(g17,g5)
    c: Vertical(g18)
    c: Coincident(g18,g6)
    c: Vertical(g19)
    c: Coincident(g19,g7)
    c: Vertical(g20)
    c: Coincident(g20,g8)
    c: Vertical(g21)
    c: Coincident(g21,g9)
    c: Vertical(g22)
    c: Coincident(g22,g10)
    c: Vertical(g23)
    c: Coincident(g23,g11)
    c: Block(g23)
    c: Block(g22)
    c: Block(g21)
    c: Block(g20)
    c: Block(g13)
    c: Block(g14)
    c: Block(g15)
    c: Block(g16)
    c: Block(g17)
    c: Block(g18)
    c: Block(g19)
FEATURE [Part::Extrusion] Extrude022
  Base = -> Sketch030
  Dir = (1,-2e-16,2e-16)
  DirMode = 2
  FaceMakerClass = Part::FaceMakerBullseye
  LengthFwd = 19
  LengthRev = 0
  Placement = pos=(-19,0,0) rot=(0,0,1;0rad)
  Solid = true
  Symmetric = false
FEATURE [Part::Fillet] Fillet022
  Base = -> Extrude022
  Edges = 24 edges r=1.49: [Edge6,Edge11,Edge18,Edge23,Edge30,Edge35,Edge42,Edge47,Edge54,Edge59,Edge66,Edge71,Edge78,Edge83,Edge90,Edge95,Edge102,Edge107,Edge114,Edge119,Edge126,Edge131,Edge138,Edge143]
FEATURE [Part::Cut] Cut020  label="top010"
  Base = -> Cut019
  Tool = -> Fillet022
FEATURE [Sketcher::SketchObject] Sketch032
  FullyConstrained = true
  Placement = pos=(117,19,0) rot=(0.57735,0.57735,0.57735;2.0944rad)
  sketch-geometry (48):
    g0: LineSegment StartX=-49.19 StartY=69.25 StartZ=0 EndX=-49.19 EndY=66.25 EndZ=0
    g1: LineSegment StartX=-49.19 StartY=63.5 StartZ=0 EndX=-49.19 EndY=60.5 EndZ=0
    g2: LineSegment StartX=-49.19 StartY=57.75 StartZ=0 EndX=-49.19 EndY=54.75 EndZ=0
    g3: LineSegment StartX=-49.19 StartY=52 StartZ=0 EndX=-49.19 EndY=49 EndZ=0
    g4: LineSegment StartX=-49.19 StartY=46.25 StartZ=0 EndX=-49.19 EndY=43.25 EndZ=0
    g5: LineSegment StartX=-49.19 StartY=40.5 StartZ=0 EndX=-49.19 EndY=37.5 EndZ=0
    g6: LineSegment StartX=-49.19 StartY=34.5 StartZ=0 EndX=-49.19 EndY=31.5 EndZ=0
    g7: LineSegment StartX=-49.19 StartY=28.75 StartZ=0 EndX=-49.19 EndY=25.75 EndZ=0
    g8: LineSegment StartX=-49.19 StartY=23 StartZ=0 EndX=-49.19 EndY=20 EndZ=0
    g9: LineSegment StartX=-49.19 StartY=17.25 StartZ=0 EndX=-49.19 EndY=14.25 EndZ=0
    g10: LineSegment StartX=-49.19 StartY=11.5 StartZ=0 EndX=-49.19 EndY=8.5 EndZ=0
    g11: LineSegment StartX=-49.19 StartY=5.75 StartZ=0 EndX=-49.19 EndY=2.75 EndZ=0
    g12: ArcOfCircle CenterX=-1.5 CenterY=67.75 CenterZ=0 NormalX=0 NormalY=0 NormalZ=1 AngleXU=0 Radius=1.5 StartAngle=4.71239 EndAngle=7.85398
    g13: ArcOfCircle CenterX=-1.5 CenterY=62 CenterZ=0 NormalX=0 NormalY=0 NormalZ=1 AngleXU=0 Radius=1.5 StartAngle=4.71239 EndAngle=7.85398
    g14: ArcOfCircle CenterX=-1.5 CenterY=56.25 CenterZ=0 NormalX=0 NormalY=0 NormalZ=1 AngleXU=0 Radius=1.5 StartAngle=4.71239 EndAngle=7.85398
    g15: ArcOfCircle CenterX=-11.49 CenterY=50.5 CenterZ=0 NormalX=0 NormalY=0 NormalZ=1 AngleXU=0 Radius=1.5 StartAngle=4.71239 EndAngle=7.85398
    g16: ArcOfCircle CenterX=-16.28 CenterY=44.75 CenterZ=0 NormalX=0 NormalY=0 NormalZ=1 AngleXU=0 Radius=1.5 StartAngle=4.71239 EndAngle=7.85398
    g17: ArcOfCircle CenterX=-18.2337 CenterY=39 CenterZ=0 NormalX=0 NormalY=0 NormalZ=1 AngleXU=0 Radius=1.5 StartAngle=4.71485 EndAngle=7.85398
    g18: ArcOfCircle CenterX=-16.2837 CenterY=27.25 CenterZ=0 NormalX=0 NormalY=0 NormalZ=1 AngleXU=0 Radius=1.5 StartAngle=4.71485 EndAngle=7.85398
    g19: ArcOfCircle CenterX=-18.2337 CenterY=33 CenterZ=0 NormalX=0 NormalY=0 NormalZ=1 AngleXU=0 Radius=1.5 StartAngle=4.71485 EndAngle=7.85398
    g20: ArcOfCircle CenterX=-11.49 CenterY=21.5 CenterZ=0 NormalX=0 NormalY=0 NormalZ=1 AngleXU=0 Radius=1.5 StartAngle=4.71239 EndAngle=7.85398
    g21: ArcOfCircle CenterX=-1.5 CenterY=4.25 CenterZ=0 NormalX=0 NormalY=0 NormalZ=1 AngleXU=0 Radius=1.5 StartAngle=4.71239 EndAngle=7.85398
    g22: ArcOfCircle CenterX=-1.5 CenterY=10 CenterZ=0 NormalX=0 NormalY=0 NormalZ=1 AngleXU=0 Radius=1.5 StartAngle=4.71239 EndAngle=7.85398
    g23: ArcOfCircle CenterX=-1.5 CenterY=15.75 CenterZ=0 NormalX=0 NormalY=0 NormalZ=1 AngleXU=0 Radius=1.5 StartAngle=4.71239 EndAngle=7.85398
    g24: LineSegment StartX=-49.19 StartY=69.25 StartZ=0 EndX=-1.5 EndY=69.25 EndZ=0
    g25: LineSegment StartX=-49.19 StartY=66.25 StartZ=0 EndX=-1.5 EndY=66.25 EndZ=0
    g26: LineSegment StartX=-49.19 StartY=63.5 StartZ=0 EndX=-1.5 EndY=63.5 EndZ=0
    g27: LineSegment StartX=-49.19 StartY=60.5 StartZ=0 EndX=-1.5 EndY=60.5 EndZ=0
    g28: LineSegment StartX=-49.19 StartY=57.75 StartZ=0 EndX=-1.5 EndY=57.75 EndZ=0
    g29: LineSegment StartX=-49.19 StartY=54.75 StartZ=0 EndX=-1.5 EndY=54.75 EndZ=0
    g30: LineSegment StartX=-49.19 StartY=52 StartZ=0 EndX=-11.49 EndY=52 EndZ=0
    g31: LineSegment StartX=-49.19 StartY=49 StartZ=0 EndX=-11.49 EndY=49 EndZ=0
    g32: LineSegment StartX=-49.19 StartY=46.25 StartZ=0 EndX=-16.28 EndY=46.25 EndZ=0
    g33: LineSegment StartX=-49.19 StartY=43.25 StartZ=0 EndX=-16.28 EndY=43.25 EndZ=0
    g34: LineSegment StartX=-49.19 StartY=40.5 StartZ=0 EndX=-18.2337 EndY=40.5 EndZ=0
    g35: LineSegment StartX=-49.19 StartY=37.5 StartZ=0 EndX=-18.23 EndY=37.5 EndZ=0
    g36: LineSegment StartX=-49.19 StartY=34.5 StartZ=0 EndX=-18.2337 EndY=34.5 EndZ=0
    g37: LineSegment StartX=-49.19 StartY=31.5 StartZ=0 EndX=-18.23 EndY=31.5 EndZ=0
    g38: LineSegment StartX=-49.19 StartY=28.75 StartZ=0 EndX=-16.2837 EndY=28.75 EndZ=0
    g39: LineSegment StartX=-49.19 StartY=25.75 StartZ=0 EndX=-16.28 EndY=25.75 EndZ=0
    g40: LineSegment StartX=-49.19 StartY=23 StartZ=0 EndX=-11.49 EndY=23 EndZ=0
    g41: LineSegment StartX=-49.19 StartY=20 StartZ=0 EndX=-11.49 EndY=20 EndZ=0
    g42: LineSegment StartX=-49.19 StartY=17.25 StartZ=0 EndX=-1.5 EndY=17.25 EndZ=0
    g43: LineSegment StartX=-49.19 StartY=14.25 StartZ=0 EndX=-1.5 EndY=14.25 EndZ=0
    g44: LineSegment StartX=-49.19 StartY=11.5 StartZ=0 EndX=-1.5 EndY=11.5 EndZ=0
    g45: LineSegment StartX=-49.19 StartY=8.5 StartZ=0 EndX=-1.5 EndY=8.5 EndZ=0
    g46: LineSegment StartX=-49.19 StartY=5.75 StartZ=0 EndX=-1.5 EndY=5.75 EndZ=0
    g47: LineSegment StartX=-49.19 StartY=2.75 StartZ=0 EndX=-1.5 EndY=2.75 EndZ=0
  constraints (120):
    c: Vertical(g0)
    c: Distance(g0) = 3
    c: Block(g0)
    c: Vertical(g1)
    c: Distance(g1) = 3
    c: Vertical(g2)
    c: Equal(g0,g2) = 3
    c: Block(g2)
    c: Vertical(g3)
    c: Equal(g1,g3) = 3
    c: Vertical(g4)
    c: Equal(g0,g4) = 3
    c: Block(g4)
    c: Vertical(g5)
    c: Equal(g1,g5) = 3
    c: Vertical(g6)
    c: Equal(g0,g6) = 3
    c: Block(g6)
    c: Vertical(g7)
    c: Equal(g1,g7) = 3
    c: Vertical(g8)
    c: Equal(g0,g8) = 3
    c: Block(g8)
    c: Vertical(g9)
    c: Equal(g1,g9) = 3
    c: Vertical(g10)
    c: Equal(g0,g10) = 3
    c: Block(g10)
    c: Vertical(g11)
    c: Equal(g1,g11) = 3
    c: Block(g12)
    c: Block(g13)
    c: Block(g14)
    c: Block(g15)
    c: Block(g16)
    c: Block(g17)
    c: Block(g18)
    c: Block(g19)
    c: Block(g20)
    c: Block(g21)
    c: Block(g22)
    c: Block(g23)
    c: Block(g11)
    c: Block(g9)
    c: Block(g7)
    c: Block(g5)
    c: Block(g3)
    c: Block(g1)
    c: Coincident(g24,g0)
    c: Coincident(g24,g12)
    c: Horizontal(g24)
    c: Coincident(g25,g0)
    c: Coincident(g25,g12)
    c: Horizontal(g25)
    c: Coincident(g26,g1)
    c: Coincident(g26,g13)
    c: Horizontal(g26)
    c: Coincident(g27,g1)
    c: Coincident(g27,g13)
    c: Horizontal(g27)
    c: Coincident(g28,g2)
    c: Coincident(g28,g14)
    c: Horizontal(g28)
    c: Coincident(g29,g2)
    c: Coincident(g29,g14)
    c: Horizontal(g29)
    c: Coincident(g30,g3)
    c: Coincident(g30,g15)
    c: Horizontal(g30)
    c: Coincident(g31,g3)
    c: Coincident(g31,g15)
    c: Horizontal(g31)
    c: Coincident(g32,g4)
    c: Coincident(g32,g16)
    c: Horizontal(g32)
    c: Coincident(g33,g4)
    c: Coincident(g33,g16)
    c: Horizontal(g33)
    c: Coincident(g34,g5)
    c: Coincident(g34,g17)
    c: Horizontal(g34)
    c: Coincident(g35,g5)
    c: Coincident(g35,g17)
    c: Horizontal(g35)
    c: Coincident(g36,g6)
    c: Coincident(g36,g19)
    c: Horizontal(g36)
    c: Coincident(g37,g6)
    c: Coincident(g37,g19)
    c: Horizontal(g37)
    c: Coincident(g38,g7)
    c: Coincident(g38,g18)
    c: Horizontal(g38)
    c: Coincident(g39,g7)
    c: Coincident(g39,g18)
    c: Horizontal(g39)
    c: Coincident(g40,g8)
    c: Coincident(g40,g20)
    c: Horizontal(g40)
    c: Coincident(g41,g8)
    c: Coincident(g41,g20)
    c: Horizontal(g41)
    c: Coincident(g42,g9)
    c: Coincident(g42,g23)
    c: Horizontal(g42)
    c: Coincident(g43,g9)
    c: Coincident(g43,g23)
    c: Horizontal(g43)
    c: Coincident(g44,g10)
    c: Coincident(g44,g22)
    c: Horizontal(g44)
    c: Coincident(g45,g10)
    c: Coincident(g45,g22)
    c: Horizontal(g45)
    c: Coincident(g46,g11)
    c: Coincident(g46,g21)
    c: Horizontal(g46)
    c: Coincident(g47,g11)
    c: Coincident(g47,g21)
    c: Horizontal(g47)
FEATURE [Part::Extrusion] Extrude023
  Base = -> Sketch032
  Dir = (1,-2e-16,2e-16)
  DirMode = 2
  FaceMakerClass = Part::FaceMakerBullseye
  LengthFwd = 19
  LengthRev = 0
  Placement = pos=(-19,0,0) rot=(0,0,1;0rad)
  Solid = true
  Symmetric = false
FEATURE [Part::Fillet] Fillet023
  Base = -> Extrude023
  Edges = <same value as first occurrence — deduplicated (x6 in doc)>
  Placement = pos=(0,0.05,0) rot=(0,0,1;0rad)
FEATURE [Part::Cut] Cut014  label="bottom003"
  Base = -> Cut007
  Tool = -> Fusion047
FEATURE [Part::Cut] Cut021  label="bottom004"
  Base = -> Cut014
  Tool = -> Fillet023
FEATURE [Sketcher::SketchObject] Sketch033
  FullyConstrained = true
  Placement = pos=(117,19,0) rot=(0.57735,0.57735,0.57735;2.0944rad)
  sketch-geometry (8):
    g0: LineSegment StartX=-49.19 StartY=69.25 StartZ=0 EndX=-49.19 EndY=66.25 EndZ=0
    g1: LineSegment StartX=-49.19 StartY=5.75 StartZ=0 EndX=-49.19 EndY=2.75 EndZ=0
    g2: ArcOfCircle CenterX=-1.5 CenterY=67.75 CenterZ=0 NormalX=0 NormalY=0 NormalZ=1 AngleXU=0 Radius=1.5 StartAngle=4.71239 EndAngle=7.85398
    g3: ArcOfCircle CenterX=-1.5 CenterY=4.25 CenterZ=0 NormalX=0 NormalY=0 NormalZ=1 AngleXU=0 Radius=1.5 StartAngle=4.71239 EndAngle=7.85398
    g4: LineSegment StartX=-49.19 StartY=69.25 StartZ=0 EndX=-1.5 EndY=69.25 EndZ=0
    g5: LineSegment StartX=-49.19 StartY=66.25 StartZ=0 EndX=-1.5 EndY=66.25 EndZ=0
    g6: LineSegment StartX=-49.19 StartY=5.75 StartZ=0 EndX=-1.5 EndY=5.75 EndZ=0
    g7: LineSegment StartX=-49.19 StartY=2.75 StartZ=0 EndX=-1.5 EndY=2.75 EndZ=0
  constraints (19):
    c: Vertical(g0)
    c: Distance(g0) = 3
    c: Block(g0)
    c: Vertical(g1)
    c: Block(g2)
    c: Block(g3)
    c: Block(g1)
    c: Coincident(g4,g0)
    c: Coincident(g4,g2)
    c: Horizontal(g4)
    c: Coincident(g5,g0)
    c: Coincident(g5,g2)
    c: Horizontal(g5)
    c: Coincident(g6,g1)
    c: Coincident(g6,g3)
    c: Horizontal(g6)
    c: Coincident(g7,g1)
    c: Coincident(g7,g3)
    c: Horizontal(g7)
FEATURE [Sketcher::SketchObject] Sketch034
  FullyConstrained = true
  Placement = pos=(117,19,0) rot=(0.57735,0.57735,0.57735;2.0944rad)
  sketch-geometry (8):
    g0: LineSegment StartX=-49.19 StartY=63.5 StartZ=0 EndX=-49.19 EndY=60.5 EndZ=0
    g1: LineSegment StartX=-49.19 StartY=11.5 StartZ=0 EndX=-49.19 EndY=8.5 EndZ=0
    g2: ArcOfCircle CenterX=-1.5 CenterY=62 CenterZ=0 NormalX=0 NormalY=0 NormalZ=1 AngleXU=0 Radius=1.5 StartAngle=4.71239 EndAngle=7.85398
    g3: ArcOfCircle CenterX=-1.5 CenterY=10 CenterZ=0 NormalX=0 NormalY=0 NormalZ=1 AngleXU=0 Radius=1.5 StartAngle=4.71239 EndAngle=7.85398
    g4: LineSegment StartX=-49.19 StartY=63.5 StartZ=0 EndX=-1.5 EndY=63.5 EndZ=0
    g5: LineSegment StartX=-49.19 StartY=60.5 StartZ=0 EndX=-1.5 EndY=60.5 EndZ=0
    g6: LineSegment StartX=-49.19 StartY=11.5 StartZ=0 EndX=-1.5 EndY=11.5 EndZ=0
    g7: LineSegment StartX=-49.19 StartY=8.5 StartZ=0 EndX=-1.5 EndY=8.5 EndZ=0
  constraints (19):
    c: Vertical(g0)
    c: Distance(g0) = 3
    c: Vertical(g1)
    c: Block(g1)
    c: Block(g2)
    c: Block(g3)
    c: Block(g0)
    c: Coincident(g4,g0)
    c: Coincident(g4,g2)
    c: Horizontal(g4)
    c: Coincident(g5,g0)
    c: Coincident(g5,g2)
    c: Horizontal(g5)
    c: Coincident(g6,g1)
    c: Coincident(g6,g3)
    c: Horizontal(g6)
    c: Coincident(g7,g1)
    c: Coincident(g7,g3)
    c: Horizontal(g7)
FEATURE [Part::Extrusion] Extrude024
  Base = -> Sketch033
  Dir = (1,0,0)
  DirMode = 2
  FaceMakerClass = Part::FaceMakerBullseye
  LengthFwd = 10
  LengthRev = 0
  Solid = true
  Symmetric = false
FEATURE [Part::Extrusion] Extrude025
  Base = -> Sketch034
  Dir = (1,0,0)
  DirMode = 2
  FaceMakerClass = Part::FaceMakerBullseye
  LengthFwd = 10
  LengthRev = 0
  Solid = true
  Symmetric = false
FEATURE [Part::Fillet] Fillet024  label="removeFromtMoreFrontCaseScrewRetainers"
  Base = -> Extrude024
  Edges = 4 edges r=1.49: [Edge6,Edge11,Edge18,Edge23]
  Placement = pos=(-11,0,0) rot=(0,0,1;0rad)
FEATURE [Part::Fillet] Fillet025  label="removeFromtMoreFrontCaseScrewRetainers001"
  Base = -> Extrude025
  Edges = 4 edges r=1.49: [Edge6,Edge11,Edge18,Edge23]
  Placement = pos=(-19,0,0) rot=(0,0,1;0rad)
FEATURE [Part::Cut] Cut022
  Base = -> Cut015
  Tool = -> Fillet025
FEATURE [Part::Cut] Cut023  label="screwRetainers"
  Base = -> Cut022
  Tool = -> Fillet024
FEATURE [Part::MultiFuse] Fusion056  label="bottom005"
  Shapes = -> [Fusion044,Cut021]
FEATURE [Part::MultiFuse] Fusion057  label="casePillars001"
  Shapes = -> [Cut016,Fusion052]
FEATURE [Part::MultiFuse] Fusion058  label="bottom006"
  Shapes = -> [Fusion056,Cut023]
FEATURE [Part::MultiFuse] Fusion059  label="bottom007"
  Shapes = -> [Fusion058,Fillet005]
FEATURE [Part::MultiFuse] Fusion060  label="bottom008"
  Shapes = -> [Fusion059,Fusion]
FEATURE [Part::MultiFuse] Fusion061  label="top011"
  Shapes = -> [Cut006,Cut020]
FEATURE [Part::MultiFuse] Fusion062  label="top012"
  Shapes = -> [Fusion057,Fusion061]
FEATURE [Sketcher::SketchObject] Sketch035  label="topSketch007"
  FullyConstrained = true
  sketch-geometry (6):
    g0: LineSegment StartX=19 StartY=38 StartZ=0 EndX=117 EndY=38 EndZ=0
    g1: ArcOfCircle CenterX=19 CenterY=19 CenterZ=0 NormalX=0 NormalY=0 NormalZ=1 AngleXU=0 Radius=19 StartAngle=1.5708 EndAngle=3.14159
    g2: LineSegment StartX=117 StartY=38 StartZ=0 EndX=117 EndY=19 EndZ=0
    g3: LineSegment StartX=98 StartY=1.0161e-12 StartZ=0 EndX=5.22862e-06 EndY=1.0161e-12 EndZ=0
    g4: LineSegment StartX=5.22862e-06 StartY=19 StartZ=0 EndX=5.22862e-06 EndY=1.0161e-12 EndZ=0
    g5: ArcOfCircle CenterX=98 CenterY=19 CenterZ=0 NormalX=0 NormalY=0 NormalZ=1 AngleXU=0 Radius=19 StartAngle=4.71239 EndAngle=6.28319
  constraints (16):
    c: Horizontal(g0)
    c: Distance(g0) = 98
    c: Coincident(g1,g0)
    c: Block(g1)
    c: Coincident(g2,g0)
    c: Vertical(g2)
    c: Distance(g2) = 19
    c: Horizontal(g3)
    c: Coincident(g4,g1)
    c: Vertical(g4)
    c: Coincident(g3,g4)
    c: Block(g3)
    c: Coincident(g5,g2)
    c: Coincident(g5,g3)
    c: Block(g0)
    c: Block(g5)
FEATURE [Part::Extrusion] Extrude026  label="sideA001"
  Base = -> Sketch035
  Dir = (0,0,1)
  DirMode = 2
  FaceMakerClass = Part::FaceMakerBullseye
  LengthFwd = 3
  LengthRev = 0
  Placement = pos=(0,0,-2.7) rot=(0,0,1;0rad)
  Solid = true
  Symmetric = false
FEATURE [Sketcher::SketchObject] Sketch036  label="topSketch008"
  FullyConstrained = true
  sketch-geometry (6):
    g0: LineSegment StartX=19 StartY=38 StartZ=0 EndX=117 EndY=38 EndZ=0
    g1: ArcOfCircle CenterX=19 CenterY=19 CenterZ=0 NormalX=0 NormalY=0 NormalZ=1 AngleXU=0 Radius=19 StartAngle=1.5708 EndAngle=3.14159
    g2: LineSegment StartX=117 StartY=38 StartZ=0 EndX=117 EndY=19 EndZ=0
    g3: LineSegment StartX=98 StartY=1.0161e-12 StartZ=0 EndX=5.22862e-06 EndY=1.0161e-12 EndZ=0
    g4: LineSegment StartX=5.22862e-06 StartY=19 StartZ=0 EndX=5.22862e-06 EndY=1.0161e-12 EndZ=0
    g5: ArcOfCircle CenterX=98 CenterY=19 CenterZ=0 NormalX=0 NormalY=0 NormalZ=1 AngleXU=0 Radius=19 StartAngle=4.71239 EndAngle=6.28319
  constraints (16):
    c: Horizontal(g0)
    c: Distance(g0) = 98
    c: Coincident(g1,g0)
    c: Block(g1)
    c: Coincident(g2,g0)
    c: Vertical(g2)
    c: Distance(g2) = 19
    c: Horizontal(g3)
    c: Coincident(g4,g1)
    c: Vertical(g4)
    c: Coincident(g3,g4)
    c: Block(g3)
    c: Coincident(g5,g2)
    c: Coincident(g5,g3)
    c: Block(g0)
    c: Block(g5)
FEATURE [Part::Extrusion] Extrude027  label="sideB001"
  Base = -> Sketch036
  Dir = (0,0,1)
  DirMode = 2
  FaceMakerClass = Part::FaceMakerBullseye
  LengthFwd = 3
  LengthRev = 0
  Placement = pos=(0,0,71.7) rot=(0,0,1;0rad)
  Solid = true
  Symmetric = false
FEATURE [Part::MultiFuse] Fusion064  label="removeFromBottom"
  Shapes = -> [Extrude026,Extrude027]
FEATURE [Part::Cut] Cut024  label="bottom009"
  Base = -> Fusion060
  Tool = -> Fusion064
FEATURE [Sketcher::SketchObject] Sketch037  label="topSketch009"
  FullyConstrained = true
  sketch-geometry (8):
    g0: ArcOfCircle CenterX=19 CenterY=19.1201 CenterZ=0 NormalX=0 NormalY=0 NormalZ=1 AngleXU=0 Radius=18.8799 StartAngle=1.5708 EndAngle=3.14793
    g1: LineSegment StartX=0.120501 StartY=19.0004 StartZ=0 EndX=0.120501 EndY=0.000382114 EndZ=0
    g2: LineSegment StartX=19 StartY=38 StartZ=0 EndX=124 EndY=38 EndZ=0
    g3: LineSegment StartX=0.120501 StartY=0.000382114 StartZ=0 EndX=105.121 EndY=0.000382114 EndZ=0
    g4: LineSegment StartX=124 StartY=38 StartZ=0 EndX=125.616 EndY=38 EndZ=0
    g5: LineSegment StartX=105.121 StartY=0.000382114 StartZ=0 EndX=106.736 EndY=0.000382114 EndZ=0
    g6: ArcOfCircle CenterX=106.616 CenterY=19 CenterZ=0 NormalX=0 NormalY=0 NormalZ=1 AngleXU=0 Radius=19 StartAngle=4.71873 EndAngle=6.28319
    g7: LineSegment StartX=125.616 StartY=38 StartZ=0 EndX=125.616 EndY=19 EndZ=0
  constraints (21):
    c: Block(g0)
    c: Coincident(g1,g0)
    c: Vertical(g1)
    c: Horizontal(g2)
    c: Distance(g2) = 105
    c: Coincident(g2,g0)
    c: Distance(g1) = 19
    c: Coincident(g3,g1)
    c: Horizontal(g3)
    c: Distance(g3) = 105
    c: Coincident(g4,g2)
    c: Horizontal(g4)
    c: Distance(g4) = 1.61553
    c: Horizontal(g5)
    c: Equal(g4,g5) = 1.61553
    c: Coincident(g5,g3)
    c: Block(g6)
    c: Coincident(g6,g5)
    c: Coincident(g7,g4)
    c: Coincident(g7,g6)
    c: Vertical(g7)
FEATURE [Part::Extrusion] Extrude028  label="sideB"
  Base = -> Sketch037
  Dir = (0,0,1)
  DirMode = 2
  FaceMakerClass = Part::FaceMakerBullseye
  LengthFwd = 3
  LengthRev = 0
  Placement = pos=(0,0,72) rot=(0,0,1;0rad)
  Solid = true
  Symmetric = false
FEATURE [Sketcher::SketchObject] Sketch038  label="topSketch010"
  FullyConstrained = true
  sketch-geometry (22):
    g0: LineSegment StartX=5.21097e-06 StartY=3 StartZ=0 EndX=5.21097e-06 EndY=19 EndZ=0
    g1: ArcOfCircle CenterX=19 CenterY=19 CenterZ=0 NormalX=0 NormalY=0 NormalZ=1 AngleXU=0 Radius=19 StartAngle=1.5708 EndAngle=3.14159
    g2: ArcOfCircle CenterX=19 CenterY=19 CenterZ=0 NormalX=0 NormalY=0 NormalZ=1 AngleXU=0 Radius=16 StartAngle=1.5708 EndAngle=3.14159
    g3: LineSegment StartX=114 StartY=35 StartZ=0 EndX=19 EndY=35 EndZ=0
    g4: LineSegment StartX=5.21097e-06 StartY=3 StartZ=0 EndX=5.21097e-06 EndY=0 EndZ=0
    g5: LineSegment StartX=3 StartY=0 StartZ=0 EndX=5.21097e-06 EndY=0 EndZ=0
    g6: LineSegment StartX=3 StartY=19 StartZ=0 EndX=3 EndY=0 EndZ=0
    g7: LineSegment StartX=19 StartY=38 StartZ=0 EndX=124 EndY=38 EndZ=0
    g8: Circle CenterX=119 CenterY=35 CenterZ=0 NormalX=0 NormalY=0 NormalZ=1 AngleXU=0 Radius=1
    g9: Circle CenterX=121 CenterY=35 CenterZ=0 NormalX=0 NormalY=0 NormalZ=1 AngleXU=0 Radius=1
    g10: Circle CenterX=121 CenterY=33 CenterZ=0 NormalX=0 NormalY=0 NormalZ=1 AngleXU=0 Radius=1
    g11: BSplineCurve PolesCount=3 KnotsCount=2 Degree=2 IsPeriodic=0
    g12: GeomPoint X=119 Y=35 Z=0
    g13: GeomPoint X=121 Y=33 Z=0
    g14: LineSegment StartX=119 StartY=35 StartZ=0 EndX=114 EndY=35 EndZ=0
    g15: ArcOfCircle CenterX=105 CenterY=19 CenterZ=0 NormalX=0 NormalY=0 NormalZ=1 AngleXU=0 Radius=16 StartAngle=5.60905 EndAngle=6.28319
    g16: LineSegment StartX=121 StartY=33 StartZ=0 EndX=121 EndY=19 EndZ=0
    g17: LineSegment StartX=117.5 StartY=9.01251 StartZ=0 EndX=121.163 EndY=9.0125 EndZ=0
    g18: ArcOfCircle CenterX=105 CenterY=19 CenterZ=0 NormalX=0 NormalY=0 NormalZ=1 AngleXU=0 Radius=20.6155 StartAngle=5.7297 EndAngle=6.28319
    g19: LineSegment StartX=121.163 StartY=9.0125 StartZ=0 EndX=122.538 EndY=8.16329 EndZ=0
    g20: LineSegment StartX=124 StartY=38 StartZ=0 EndX=125.616 EndY=38 EndZ=0
    g21: LineSegment StartX=125.616 StartY=19 StartZ=0 EndX=125.616 EndY=38 EndZ=0
  constraints (49):
    c: Vertical(g0)
    c: Block(g0)
    c: Coincident(g1,g0)
    c: Block(g1)
    c: Coincident(g2,g1)
    c: Block(g2)
    c: Coincident(g3,g2)
    c: Horizontal(g3)
    c: Tangent(g3,g2)
    c: Coincident(g4,g0)
    c: Distance(g4) = 3
    c: Vertical(g4)
    c: Coincident(g5,g4)
    c: Horizontal(g5)
    c: Coincident(g6,g2)
    c: Coincident(g6,g5)
    c: Vertical(g6)
    c: Horizontal(g7)
    c: Distance(g7) = 105
    c: Coincident(g7,g1)
    c: Block(g3)
    c: Weight(g8) = 1
    c: Equal(g8,g9)
    c: Equal(g8,g10)
    c: InternalAlignment(g8,g11)
    c: InternalAlignment(g9,g11)
    c: InternalAlignment(g10,g11)
    c: InternalAlignment(g12,g11)
    c: InternalAlignment(g13,g11)
    c: Block(g11)
    c: Coincident(g14,g11)
    c: Coincident(g14,g3)
    c: Horizontal(g14)
    c: Block(g15)
    c: Coincident(g16,g11)
    c: Coincident(g16,g15)
    c: Vertical(g16)
    c: Distance(g16) = 14
    c: Coincident(g17,g15)
    c: Block(g18)
    c: Coincident(g19,g18)
    c: Coincident(g20,g7)
    c: Horizontal(g20)
    c: Vertical(g21)
    c: Coincident(g20,g21)
    c: Block(g20)
    c: Block(g21)
    c: Block(g19)
    c: Block(g17)
FEATURE [Part::Extrusion] Extrude029
  Base = -> Sketch038
  Dir = (0,0,1)
  DirMode = 2
  FaceMakerClass = Part::FaceMakerBullseye
  LengthFwd = 72
  LengthRev = 0
  Solid = true
  Symmetric = false
FEATURE [Part::Feature] Face085
  shape: bbox 4.8 x 25.5 x 2e-07 mm, 1 faces, 0 solids (baked)
FEATURE [Part::Revolution] Revolve089  label="moreFrontCaseScrewPost003"
  Angle = 360
  Axis = (0,1,0)
  Base = (0,0,0)
  FaceMakerClass = Part::FaceMakerBullseye
  Placement = pos=(109.5,4.5,3.5) rot=(0,0,1;0rad)
  Solid = false
  Source = -> Face085
  Symmetric = false
FEATURE [Part::Feature] Face086
  shape: bbox 4.8 x 25.5 x 2e-07 mm, 1 faces, 0 solids (baked)
FEATURE [Part::Revolution] Revolve090  label="moreFrontCaseScrewPost004"
  Angle = 360
  Axis = (0,1,0)
  Base = (0,0,0)
  FaceMakerClass = Part::FaceMakerBullseye
  Placement = pos=(109.5,4.5,68.5) rot=(0,0,1;0rad)
  Solid = false
  Source = -> Face086
  Symmetric = false
FEATURE [Part::Fillet] Fillet026  label="top013"
  Base = -> Extrude029
  Edges = 1 edges r=2: [Edge35]
FEATURE [Sketcher::SketchObject] Sketch039
  FullyConstrained = true
  sketch-geometry (7):
    g0: LineSegment StartX=0 StartY=0 StartZ=0 EndX=0 EndY=6 EndZ=0
    g1: Circle CenterX=0 CenterY=0 CenterZ=0 NormalX=0 NormalY=0 NormalZ=1 AngleXU=0 Radius=1
    g2: Circle CenterX=8 CenterY=6 CenterZ=0 NormalX=0 NormalY=0 NormalZ=1 AngleXU=0 Radius=1
    g3: BSplineCurve PolesCount=3 KnotsCount=2 Degree=2 IsPeriodic=0
    g4: GeomPoint X=0 Y=0 Z=0
    g5: GeomPoint X=8 Y=6 Z=0
    g6: LineSegment StartX=0 StartY=6 StartZ=0 EndX=8 EndY=6 EndZ=0
  constraints (14):
    c: Coincident(g0,g-1)
    c: Distance(g0) = 6
    c: Vertical(g0)
    c: Coincident(g3,g0)
    c: Weight(g1) = 1
    c: Equal(g1,g2)
    c: InternalAlignment(g1,g3)
    c: InternalAlignment(g2,g3)
    c: InternalAlignment(g4,g3)
    c: InternalAlignment(g5,g3)
    c: Block(g3)
    c: Coincident(g6,g0)
    c: Coincident(g6,g3)
    c: Horizontal(g6)
FEATURE [Sketcher::SketchObject] Sketch040
  FullyConstrained = true
  sketch-geometry (7):
    g0: LineSegment StartX=0 StartY=0 StartZ=0 EndX=0 EndY=6 EndZ=0
    g1: Circle CenterX=0 CenterY=0 CenterZ=0 NormalX=0 NormalY=0 NormalZ=1 AngleXU=0 Radius=1
    g2: Circle CenterX=8 CenterY=6 CenterZ=0 NormalX=0 NormalY=0 NormalZ=1 AngleXU=0 Radius=1
    g3: BSplineCurve PolesCount=3 KnotsCount=2 Degree=2 IsPeriodic=0
    g4: GeomPoint X=0 Y=0 Z=0
    g5: GeomPoint X=8 Y=6 Z=0
    g6: LineSegment StartX=0 StartY=6 StartZ=0 EndX=8 EndY=6 EndZ=0
  constraints (14):
    c: Coincident(g0,g-1)
    c: Distance(g0) = 6
    c: Vertical(g0)
    c: Coincident(g3,g0)
    c: Weight(g1) = 1
    c: Equal(g1,g2)
    c: InternalAlignment(g1,g3)
    c: InternalAlignment(g2,g3)
    c: InternalAlignment(g4,g3)
    c: InternalAlignment(g5,g3)
    c: Block(g3)
    c: Coincident(g6,g0)
    c: Coincident(g6,g3)
    c: Horizontal(g6)
FEATURE [Sketcher::SketchObject] Sketch041
  FullyConstrained = true
  sketch-geometry (7):
    g0: LineSegment StartX=0 StartY=0 StartZ=0 EndX=0 EndY=6 EndZ=0
    g1: Circle CenterX=0 CenterY=0 CenterZ=0 NormalX=0 NormalY=0 NormalZ=1 AngleXU=0 Radius=1
    g2: Circle CenterX=8 CenterY=6 CenterZ=0 NormalX=0 NormalY=0 NormalZ=1 AngleXU=0 Radius=1
    g3: BSplineCurve PolesCount=3 KnotsCount=2 Degree=2 IsPeriodic=0
    g4: GeomPoint X=0 Y=0 Z=0
    g5: GeomPoint X=8 Y=6 Z=0
    g6: LineSegment StartX=0 StartY=6 StartZ=0 EndX=8 EndY=6 EndZ=0
  constraints (14):
    c: Coincident(g0,g-1)
    c: Distance(g0) = 6
    c: Vertical(g0)
    c: Coincident(g3,g0)
    c: Weight(g1) = 1
    c: Equal(g1,g2)
    c: InternalAlignment(g1,g3)
    c: InternalAlignment(g2,g3)
    c: InternalAlignment(g4,g3)
    c: InternalAlignment(g5,g3)
    c: Block(g3)
    c: Coincident(g6,g0)
    c: Coincident(g6,g3)
    c: Horizontal(g6)
FEATURE [Sketcher::SketchObject] Sketch042
  FullyConstrained = true
  sketch-geometry (7):
    g0: LineSegment StartX=0 StartY=0 StartZ=0 EndX=0 EndY=6 EndZ=0
    g1: Circle CenterX=0 CenterY=0 CenterZ=0 NormalX=0 NormalY=0 NormalZ=1 AngleXU=0 Radius=1
    g2: Circle CenterX=8 CenterY=6 CenterZ=0 NormalX=0 NormalY=0 NormalZ=1 AngleXU=0 Radius=1
    g3: BSplineCurve PolesCount=3 KnotsCount=2 Degree=2 IsPeriodic=0
    g4: GeomPoint X=0 Y=0 Z=0
    g5: GeomPoint X=8 Y=6 Z=0
    g6: LineSegment StartX=0 StartY=6 StartZ=0 EndX=8 EndY=6 EndZ=0
  constraints (14):
    c: Coincident(g0,g-1)
    c: Distance(g0) = 6
    c: Vertical(g0)
    c: Coincident(g3,g0)
    c: Weight(g1) = 1
    c: Equal(g1,g2)
    c: InternalAlignment(g1,g3)
    c: InternalAlignment(g2,g3)
    c: InternalAlignment(g4,g3)
    c: InternalAlignment(g5,g3)
    c: Block(g3)
    c: Coincident(g6,g0)
    c: Coincident(g6,g3)
    c: Horizontal(g6)
FEATURE [Part::Extrusion] Extrude030  label="caseScrewPillarBracket008"
  Base = -> Sketch039
  Dir = (0,0,1)
  DirMode = 2
  FaceMakerClass = Part::FaceMakerBullseye
  LengthFwd = 2.4
  LengthRev = 0
  Placement = pos=(15.76,29,8.8) rot=(0,1,0;0rad)
  Solid = true
  Symmetric = false
FEATURE [Part::Extrusion] Extrude031  label="caseScrewPillarBracket009"
  Base = -> Sketch040
  Dir = (0,0,1)
  DirMode = 2
  FaceMakerClass = Part::FaceMakerBullseye
  LengthFwd = 2.4
  LengthRev = 0
  Placement = pos=(15.76,29,60.8) rot=(0,0,1;0rad)
  Solid = true
  Symmetric = false
FEATURE [Part::Extrusion] Extrude032  label="caseScrewPillarBracket010"
  Base = -> Sketch041
  Dir = (0,0,1)
  DirMode = 2
  FaceMakerClass = Part::FaceMakerBullseye
  LengthFwd = 2.4
  LengthRev = 0
  Placement = pos=(13.7,29,13.26) rot=(0,-1,0;1.5708rad)
  Solid = true
  Symmetric = false
FEATURE [Part::Extrusion] Extrude033  label="caseScrewPillarBracket011"
  Base = -> Sketch042
  Dir = (0,0,1)
  DirMode = 2
  FaceMakerClass = Part::FaceMakerBullseye
  LengthFwd = 2.4
  LengthRev = 0
  Placement = pos=(11.3,29,58.74) rot=(0,1,0;1.5708rad)
  Solid = true
  Symmetric = false
FEATURE [Sketcher::SketchObject] Sketch043
  FullyConstrained = true
  sketch-geometry (7):
    g0: LineSegment StartX=0 StartY=0 StartZ=0 EndX=0 EndY=6 EndZ=0
    g1: Circle CenterX=0 CenterY=0 CenterZ=0 NormalX=0 NormalY=0 NormalZ=1 AngleXU=0 Radius=1
    g2: Circle CenterX=8 CenterY=6 CenterZ=0 NormalX=0 NormalY=0 NormalZ=1 AngleXU=0 Radius=1
    g3: BSplineCurve PolesCount=3 KnotsCount=2 Degree=2 IsPeriodic=0
    g4: GeomPoint X=0 Y=0 Z=0
    g5: GeomPoint X=8 Y=6 Z=0
    g6: LineSegment StartX=0 StartY=6 StartZ=0 EndX=8 EndY=6 EndZ=0
  constraints (14):
    c: Coincident(g0,g-1)
    c: Distance(g0) = 6
    c: Vertical(g0)
    c: Coincident(g3,g0)
    c: Weight(g1) = 1
    c: Equal(g1,g2)
    c: InternalAlignment(g1,g3)
    c: InternalAlignment(g2,g3)
    c: InternalAlignment(g4,g3)
    c: InternalAlignment(g5,g3)
    c: Block(g3)
    c: Coincident(g6,g0)
    c: Coincident(g6,g3)
    c: Horizontal(g6)
FEATURE [Part::Extrusion] Extrude034  label="caseScrewPillarBracket012"
  Base = -> Sketch043
  Dir = (0,0,1)
  DirMode = 2
  FaceMakerClass = Part::FaceMakerBullseye
  LengthFwd = 2.4
  LengthRev = 0
  Placement = pos=(88.3,29,65.23) rot=(0,1,0;1.5708rad)
  Solid = true
  Symmetric = false
FEATURE [Sketcher::SketchObject] Sketch044
  FullyConstrained = true
  sketch-geometry (7):
    g0: LineSegment StartX=0 StartY=0 StartZ=0 EndX=0 EndY=6 EndZ=0
    g1: Circle CenterX=0 CenterY=0 CenterZ=0 NormalX=0 NormalY=0 NormalZ=1 AngleXU=0 Radius=1
    g2: Circle CenterX=8 CenterY=6 CenterZ=0 NormalX=0 NormalY=0 NormalZ=1 AngleXU=0 Radius=1
    g3: BSplineCurve PolesCount=3 KnotsCount=2 Degree=2 IsPeriodic=0
    g4: GeomPoint X=0 Y=0 Z=0
    g5: GeomPoint X=8 Y=6 Z=0
    g6: LineSegment StartX=0 StartY=6 StartZ=0 EndX=8 EndY=6 EndZ=0
  constraints (14):
    c: Coincident(g0,g-1)
    c: Distance(g0) = 6
    c: Vertical(g0)
    c: Coincident(g3,g0)
    c: Weight(g1) = 1
    c: Equal(g1,g2)
    c: InternalAlignment(g1,g3)
    c: InternalAlignment(g2,g3)
    c: InternalAlignment(g4,g3)
    c: InternalAlignment(g5,g3)
    c: Block(g3)
    c: Coincident(g6,g0)
    c: Coincident(g6,g3)
    c: Horizontal(g6)
FEATURE [Part::Extrusion] Extrude035  label="caseScrewPillarBracket013"
  Base = -> Sketch044
  Dir = (0,0,1)
  DirMode = 2
  FaceMakerClass = Part::FaceMakerBullseye
  LengthFwd = 2.4
  LengthRev = 0
  Placement = pos=(90.7,29,6.77) rot=(0,-1,0;1.5708rad)
  Solid = true
  Symmetric = false
FEATURE [Sketcher::SketchObject] Sketch045
  FullyConstrained = true
  sketch-geometry (7):
    g0: LineSegment StartX=0 StartY=0 StartZ=0 EndX=0 EndY=6 EndZ=0
    g1: Circle CenterX=0 CenterY=0 CenterZ=0 NormalX=0 NormalY=0 NormalZ=1 AngleXU=0 Radius=1
    g2: Circle CenterX=8 CenterY=6 CenterZ=0 NormalX=0 NormalY=0 NormalZ=1 AngleXU=0 Radius=1
    g3: BSplineCurve PolesCount=3 KnotsCount=2 Degree=2 IsPeriodic=0
    g4: GeomPoint X=0 Y=0 Z=0
    g5: GeomPoint X=8 Y=6 Z=0
    g6: LineSegment StartX=0 StartY=6 StartZ=0 EndX=8 EndY=6 EndZ=0
  constraints (14):
    c: Coincident(g0,g-1)
    c: Distance(g0) = 6
    c: Vertical(g0)
    c: Coincident(g3,g0)
    c: Weight(g1) = 1
    c: Equal(g1,g2)
    c: InternalAlignment(g1,g3)
    c: InternalAlignment(g2,g3)
    c: InternalAlignment(g4,g3)
    c: InternalAlignment(g5,g3)
    c: Block(g3)
    c: Coincident(g6,g0)
    c: Coincident(g6,g3)
    c: Horizontal(g6)
FEATURE [Sketcher::SketchObject] Sketch046
  FullyConstrained = true
  sketch-geometry (7):
    g0: LineSegment StartX=0 StartY=0 StartZ=0 EndX=0 EndY=6 EndZ=0
    g1: Circle CenterX=0 CenterY=0 CenterZ=0 NormalX=0 NormalY=0 NormalZ=1 AngleXU=0 Radius=1
    g2: Circle CenterX=8 CenterY=6 CenterZ=0 NormalX=0 NormalY=0 NormalZ=1 AngleXU=0 Radius=1
    g3: BSplineCurve PolesCount=3 KnotsCount=2 Degree=2 IsPeriodic=0
    g4: GeomPoint X=0 Y=0 Z=0
    g5: GeomPoint X=8 Y=6 Z=0
    g6: LineSegment StartX=0 StartY=6 StartZ=0 EndX=8 EndY=6 EndZ=0
  constraints (14):
    c: Coincident(g0,g-1)
    c: Distance(g0) = 6
    c: Vertical(g0)
    c: Coincident(g3,g0)
    c: Weight(g1) = 1
    c: Equal(g1,g2)
    c: InternalAlignment(g1,g3)
    c: InternalAlignment(g2,g3)
    c: InternalAlignment(g4,g3)
    c: InternalAlignment(g5,g3)
    c: Block(g3)
    c: Coincident(g6,g0)
    c: Coincident(g6,g3)
    c: Horizontal(g6)
FEATURE [Part::Extrusion] Extrude036  label="caseScrewPillarBracket014"
  Base = -> Sketch045
  Dir = (0,0,1)
  DirMode = 2
  FaceMakerClass = Part::FaceMakerBullseye
  LengthFwd = 2.4
  LengthRev = 0
  Placement = pos=(110.7,29,6.77) rot=(0,-1,0;1.5708rad)
  Solid = true
  Symmetric = false
FEATURE [Part::Extrusion] Extrude037  label="caseScrewPillarBracket015"
  Base = -> Sketch046
  Dir = (0,0,1)
  DirMode = 2
  FaceMakerClass = Part::FaceMakerBullseye
  LengthFwd = 2.4
  LengthRev = 0
  Placement = pos=(108.3,29,65.23) rot=(0,1,0;1.5708rad)
  Solid = true
  Symmetric = false
FEATURE [Part::Box] Box013  label="frontCaseScrewPillarBracket002"
  AttacherType = Attacher::AttachEngine3D
  Height = 2.4
  Length = 22
  Placement = pos=(87,28,2.3) rot=(0,0,1;0rad)
  Width = 7
FEATURE [Part::Box] Box014  label="frontCaseScrewPillarBracket003"
  AttacherType = Attacher::AttachEngine3D
  Height = 2.4
  Length = 22
  Placement = pos=(87,28,67.3) rot=(0,0,1;0rad)
  Width = 7
FEATURE [Part::Feature] Face087
  shape: bbox 4.8 x 30.2 x 2e-07 mm, 1 faces, 0 solids (baked)
FEATURE [Part::Revolution] Revolve091  label="frontCaseScrewPost004"
  Angle = 360
  Axis = (0,1,0)
  Base = (0,0,0)
  FaceMakerClass = Part::FaceMakerBullseye
  Placement = pos=(89.5,4.5,3.5) rot=(0,0,1;0rad)
  Solid = false
  Source = -> Face087
  Symmetric = false
FEATURE [Part::Feature] Face088
  shape: bbox 4.8 x 30.2 x 2e-07 mm, 1 faces, 0 solids (baked)
FEATURE [Part::Revolution] Revolve092  label="frontCaseScrewPost005"
  Angle = 360
  Axis = (0,1,0)
  Base = (0,0,0)
  FaceMakerClass = Part::FaceMakerBullseye
  Placement = pos=(89.5,4.5,68.5) rot=(0,0,1;0rad)
  Solid = false
  Source = -> Face088
  Symmetric = false
FEATURE [Part::Feature] Face089
  shape: bbox 3.5 x 30.2 x 2e-07 mm, 1 faces, 0 solids (baked)
FEATURE [Part::Revolution] Revolve093  label="backCaseScrewPost002"
  Angle = 360
  Axis = (0,1,0)
  Base = (0,0,0)
  FaceMakerClass = Part::FaceMakerBullseye
  Placement = pos=(12.5,4.5,10) rot=(0,0,1;0rad)
  Solid = false
  Source = -> Face089
  Symmetric = false
FEATURE [Part::Feature] Face090
  shape: bbox 3.5 x 30.2 x 2e-07 mm, 1 faces, 0 solids (baked)
FEATURE [Part::Revolution] Revolve094  label="backCaseScrewPost003"
  Angle = 360
  Axis = (0,1,0)
  Base = (0,0,0)
  FaceMakerClass = Part::FaceMakerBullseye
  Placement = pos=(12.5,4.5,62) rot=(0,0,1;0rad)
  Solid = false
  Source = -> Face090
  Symmetric = false
FEATURE [Part::Box] Box015  label="Cube011"
  AttacherType = Attacher::AttachEngine3D
  Height = 28.8
  Length = 3
  Placement = pos=(107.3,28,21.6) rot=(0,0,1;0rad)
  Width = 7
FEATURE [Part::Box] Box016  label="Cube012"
  AttacherType = Attacher::AttachEngine3D
  Height = 3
  Length = 7.4
  Placement = pos=(107.3,28,18.6) rot=(0,0,1;0rad)
  Width = 7
FEATURE [Part::Box] Box017  label="Cube013"
  AttacherType = Attacher::AttachEngine3D
  Height = 3
  Length = 7.4
  Placement = pos=(107.3,28,50.4) rot=(0,0,1;0rad)
  Width = 7
FEATURE [Part::Cylinder] Cylinder024
  Angle = 360
  AttacherType = Attacher::AttachEngine3D
  Height = 20
  Placement = pos=(0,0,36.15) rot=(0,0,1;0rad)
  Radius = 14.3
FEATURE [Part::Cylinder] Cylinder025
  Angle = 360
  AttacherType = Attacher::AttachEngine3D
  Height = 10
  Placement = pos=(0,0,36.15) rot=(0,0,1;0rad)
  Radius = 4
FEATURE [Part::MultiFuse] Fusion066  label="removeToCreteHoleForPlugHousing009"
  Placement = pos=(70,19,36) rot=(0,1,0;1.5708rad)
  Shapes = -> [Cylinder024,Cylinder025]
FEATURE [Part::MultiFuse] Fusion065  label="plugHousingBracketHolder002"
  Shapes = -> [Box017,Box015,Box016]
FEATURE [Part::Cut] Cut025  label="plugHousingBracketHolder003"
  Base = -> Fusion065
  Placement = pos=(7,0,0) rot=(0,0,1;0rad)
  Tool = -> Fusion066
FEATURE [Sketcher::SketchObject] Sketch047
  FullyConstrained = false
  Placement = pos=(0,0,0) rot=(1,0,0;1.5708rad)
  sketch-geometry (24):
    g0: ArcOfCircle CenterX=-4 CenterY=-10.5 CenterZ=0 NormalX=0 NormalY=0 NormalZ=1 AngleXU=0 Radius=1.5 StartAngle=6e-16 EndAngle=3.14159
    g1: ArcOfCircle CenterX=-34.2 CenterY=-10.5 CenterZ=0 NormalX=0 NormalY=0 NormalZ=1 AngleXU=0 Radius=1.5 StartAngle=0 EndAngle=3.14159
    g2: ArcOfCircle CenterX=-34.2 CenterY=-27.7 CenterZ=0 NormalX=0 NormalY=0 NormalZ=1 AngleXU=0 Radius=1.5 StartAngle=3.14159 EndAngle=6.28319
    g3: ArcOfCircle CenterX=-4 CenterY=-27.7 CenterZ=0 NormalX=0 NormalY=0 NormalZ=1 AngleXU=0 Radius=1.5 StartAngle=3.1416 EndAngle=6.28319
    g4: ArcOfCircle CenterX=-10 CenterY=-4.3 CenterZ=0 NormalX=0 NormalY=0 NormalZ=1 AngleXU=0 Radius=1.5 StartAngle=2e-16 EndAngle=3.14159
    g5: ArcOfCircle CenterX=-16.1 CenterY=-1.8 CenterZ=0 NormalX=0 NormalY=0 NormalZ=1 AngleXU=0 Radius=1.5 StartAngle=5e-16 EndAngle=3.14159
    g6: ArcOfCircle CenterX=-22.1 CenterY=-1.8 CenterZ=0 NormalX=0 NormalY=0 NormalZ=1 AngleXU=0 Radius=1.5 StartAngle=5e-16 EndAngle=3.14159
    g7: ArcOfCircle CenterX=-28.2 CenterY=-4.3 CenterZ=0 NormalX=0 NormalY=0 NormalZ=1 AngleXU=0 Radius=1.5 StartAngle=2e-16 EndAngle=3.14159
    g8: ArcOfCircle CenterX=-10 CenterY=-33.9 CenterZ=0 NormalX=0 NormalY=0 NormalZ=1 AngleXU=0 Radius=1.5 StartAngle=3.14159 EndAngle=6.28319
    g9: ArcOfCircle CenterX=-16.1 CenterY=-36.4 CenterZ=0 NormalX=0 NormalY=0 NormalZ=1 AngleXU=0 Radius=1.5 StartAngle=3.14159 EndAngle=6.28319
    g10: ArcOfCircle CenterX=-22.1 CenterY=-36.4 CenterZ=0 NormalX=0 NormalY=0 NormalZ=1 AngleXU=0 Radius=1.5 StartAngle=3.14159 EndAngle=6.28319
    g11: ArcOfCircle CenterX=-28.2 CenterY=-33.9 CenterZ=0 NormalX=0 NormalY=0 NormalZ=1 AngleXU=0 Radius=1.5 StartAngle=3.14159 EndAngle=6.28319
    g12: LineSegment StartX=-35.7 StartY=-10.5 StartZ=0 EndX=-35.7 EndY=-27.7 EndZ=0
    g13: LineSegment StartX=-32.7 StartY=-10.5 StartZ=0 EndX=-32.7 EndY=-27.7 EndZ=0
    g14: LineSegment StartX=-29.7 StartY=-33.9 StartZ=0 EndX=-29.7 EndY=-4.3 EndZ=0
    g15: LineSegment StartX=-26.7 StartY=-33.9 StartZ=0 EndX=-26.7 EndY=-4.3 EndZ=0
    g16: LineSegment StartX=-2.5 StartY=-10.5 StartZ=0 EndX=-2.5 EndY=-27.7 EndZ=0
    g17: LineSegment StartX=-8.5 StartY=-4.3 StartZ=0 EndX=-8.5 EndY=-33.9 EndZ=0
    g18: LineSegment StartX=-5.5 StartY=-10.5 StartZ=0 EndX=-5.5 EndY=-27.7 EndZ=0
    g19: LineSegment StartX=-11.5 StartY=-4.3 StartZ=0 EndX=-11.5 EndY=-33.9 EndZ=0
    g20: LineSegment StartX=-14.6 StartY=-1.8 StartZ=0 EndX=-14.6 EndY=-36.4 EndZ=0
    g21: LineSegment StartX=-17.6 StartY=-1.8 StartZ=0 EndX=-17.6 EndY=-36.4 EndZ=0
    g22: LineSegment StartX=-20.6 StartY=-36.4 StartZ=0 EndX=-20.6 EndY=-1.8 EndZ=0
    g23: LineSegment StartX=-23.6 StartY=-1.8 StartZ=0 EndX=-23.6 EndY=-36.4 EndZ=0
  constraints (48):
    c: Block(g0)
    c: Block(g1)
    c: Block(g2)
    c: Block(g3)
    c: Block(g4)
    c: Block(g5)
    c: Block(g6)
    c: Block(g7)
    c: Block(g8)
    c: Block(g9)
    c: Block(g10)
    c: Block(g11)
    c: Coincident(g12,g1)
    c: Coincident(g12,g2)
    c: Vertical(g12)
    c: Coincident(g13,g1)
    c: Coincident(g13,g2)
    c: Vertical(g13)
    c: Coincident(g14,g11)
    c: Coincident(g14,g7)
    c: Vertical(g14)
    c: Coincident(g15,g11)
    c: Coincident(g15,g7)
    c: Vertical(g15)
    c: Coincident(g16,g0)
    c: Coincident(g16,g3)
    c: Vertical(g16)
    c: Coincident(g17,g4)
    c: Coincident(g17,g8)
    c: Vertical(g17)
    c: Coincident(g18,g0)
    c: Coincident(g18,g3)
    c: Vertical(g18)
    c: Coincident(g19,g4)
    c: Coincident(g19,g8)
    c: Vertical(g19)
    c: Coincident(g20,g5)
    c: Coincident(g20,g9)
    c: Vertical(g20)
    c: Coincident(g21,g5)
    c: Coincident(g21,g9)
    c: Vertical(g21)
    c: Coincident(g22,g10)
    c: Coincident(g22,g6)
    c: Vertical(g22)
    c: Coincident(g23,g6)
    c: Coincident(g23,g10)
    c: Vertical(g23)
FEATURE [Part::Extrusion] Extrude038  label="removeToCreateFanGrillHoles001"
  Base = -> Sketch047
  Dir = (0,-1,6e-16)
  DirMode = 2
  FaceMakerClass = Part::FaceMakerBullseye
  LengthFwd = 10
  LengthRev = 0
  Placement = pos=(65.4,44,54.82) rot=(0,0,1;0rad)
  Solid = true
  Symmetric = false
FEATURE [Part::Feature] Wire004
  shape: bbox 11 x 5.2 x 2e-07 mm, 0 faces, 0 solids (baked)
FEATURE [Part::Revolution] Revolve095
  Angle = 360
  Axis = (0,1,0)
  Base = (0,0,0)
  FaceMakerClass = Part::FaceMakerBullseye
  Placement = pos=(30.3,38,19.7) rot=(0,0,1;0rad)
  Solid = true
  Source = -> Wire004
  Symmetric = false
FEATURE [Part::Feature] Wire005
  shape: bbox 11 x 5.2 x 2e-07 mm, 0 faces, 0 solids (baked)
FEATURE [Part::Revolution] Revolve096
  Angle = 360
  Axis = (0,1,0)
  Base = (0,0,0)
  FaceMakerClass = Part::FaceMakerBullseye
  Placement = pos=(30.3,38,51.7) rot=(0,0,1;0rad)
  Solid = true
  Source = -> Wire005
  Symmetric = false
FEATURE [Part::Feature] Wire006
  shape: bbox 11 x 5.2 x 2e-07 mm, 0 faces, 0 solids (baked)
FEATURE [Part::Revolution] Revolve097
  Angle = 360
  Axis = (0,1,0)
  Base = (0,0,0)
  FaceMakerClass = Part::FaceMakerBullseye
  Placement = pos=(62.3,38,51.7) rot=(0,0,1;0rad)
  Solid = true
  Source = -> Wire006
  Symmetric = false
FEATURE [Part::Feature] Wire007
  shape: bbox 11 x 5.2 x 2e-07 mm, 0 faces, 0 solids (baked)
FEATURE [Part::Revolution] Revolve098
  Angle = 360
  Axis = (0,1,0)
  Base = (0,0,0)
  FaceMakerClass = Part::FaceMakerBullseye
  Placement = pos=(62.3,38,19.7) rot=(0,0,1;0rad)
  Solid = true
  Source = -> Wire007
  Symmetric = false
FEATURE [Part::MultiFuse] Fusion067  label="fanScrewHousing002"
  Shapes = -> [Revolve098,Revolve097,Revolve096,Revolve095]
FEATURE [Part::Feature] Face091 .. Face094  x4 (patterned run collapsed; names and placements below)
  shape: bbox 3.5 x 17.8 x 2e-07 mm, 1 faces, 0 solids (baked)
FEATURE [Part::Revolution] Revolve099  label="removeToCreateScrewAndThreadedInsertHole026"
  Angle = 360
  Axis = (0,1,0)
  Base = (0,0,0)
  FaceMakerClass = Part::FaceMakerBullseye
  Placement = pos=(62.3,30.3,19.7) rot=(0,0,1;0rad)
  Solid = false
  Source = -> Face091
  Symmetric = false
FEATURE [Part::Revolution] Revolve100  label="removeToCreateScrewAndThreadedInsertHole027"
  Angle = 360
  Axis = (0,1,0)
  Base = (0,0,0)
  FaceMakerClass = Part::FaceMakerBullseye
  Placement = pos=(62.3,30.3,51.7) rot=(0,0,1;0rad)
  Solid = false
  Source = -> Face092
  Symmetric = false
FEATURE [Part::Revolution] Revolve101  label="removeToCreateScrewAndThreadedInsertHole028"
  Angle = 360
  Axis = (0,1,0)
  Base = (0,0,0)
  FaceMakerClass = Part::FaceMakerBullseye
  Placement = pos=(30.3,30.3,19.7) rot=(0,0,1;0rad)
  Solid = false
  Source = -> Face093
  Symmetric = false
FEATURE [Part::Revolution] Revolve102  label="removeToCreateScrewAndThreadedInsertHole029"
  Angle = 360
  Axis = (0,1,0)
  Base = (0,0,0)
  FaceMakerClass = Part::FaceMakerBullseye
  Placement = pos=(30.3,30.3,51.7) rot=(0,0,1;0rad)
  Solid = false
  Source = -> Face094
  Symmetric = false
FEATURE [Part::MultiFuse] Fusion068  label="createThreadedInsertHolesForFan002"
  Shapes = -> [Revolve099,Revolve100,Revolve101,Revolve102]
FEATURE [Part::Cut] Cut026  label="fanScrewHousing003"
  Base = -> Fusion067
  Tool = -> Fusion068
FEATURE [Sketcher::SketchObject] Sketch048
  FullyConstrained = false
  Placement = pos=(0,0,0) rot=(1,0,0;1.5708rad)
  sketch-geometry (24):
    g0: ArcOfCircle CenterX=-4 CenterY=-10.5 CenterZ=0 NormalX=0 NormalY=0 NormalZ=1 AngleXU=0 Radius=1.5 StartAngle=6e-16 EndAngle=3.14159
    g1: ArcOfCircle CenterX=-34.2 CenterY=-10.5 CenterZ=0 NormalX=0 NormalY=0 NormalZ=1 AngleXU=0 Radius=1.5 StartAngle=0 EndAngle=3.14159
    g2: ArcOfCircle CenterX=-34.2 CenterY=-27.7 CenterZ=0 NormalX=0 NormalY=0 NormalZ=1 AngleXU=0 Radius=1.5 StartAngle=3.14159 EndAngle=6.28319
    g3: ArcOfCircle CenterX=-4 CenterY=-27.7 CenterZ=0 NormalX=0 NormalY=0 NormalZ=1 AngleXU=0 Radius=1.5 StartAngle=3.1416 EndAngle=6.28319
    g4: ArcOfCircle CenterX=-10 CenterY=-4.3 CenterZ=0 NormalX=0 NormalY=0 NormalZ=1 AngleXU=0 Radius=1.5 StartAngle=2e-16 EndAngle=3.14159
    g5: ArcOfCircle CenterX=-16.1 CenterY=-1.8 CenterZ=0 NormalX=0 NormalY=0 NormalZ=1 AngleXU=0 Radius=1.5 StartAngle=5e-16 EndAngle=3.14159
    g6: ArcOfCircle CenterX=-22.1 CenterY=-1.8 CenterZ=0 NormalX=0 NormalY=0 NormalZ=1 AngleXU=0 Radius=1.5 StartAngle=5e-16 EndAngle=3.14159
    g7: ArcOfCircle CenterX=-28.2 CenterY=-4.3 CenterZ=0 NormalX=0 NormalY=0 NormalZ=1 AngleXU=0 Radius=1.5 StartAngle=2e-16 EndAngle=3.14159
    g8: ArcOfCircle CenterX=-10 CenterY=-33.9 CenterZ=0 NormalX=0 NormalY=0 NormalZ=1 AngleXU=0 Radius=1.5 StartAngle=3.14159 EndAngle=6.28319
    g9: ArcOfCircle CenterX=-16.1 CenterY=-36.4 CenterZ=0 NormalX=0 NormalY=0 NormalZ=1 AngleXU=0 Radius=1.5 StartAngle=3.14159 EndAngle=6.28319
    g10: ArcOfCircle CenterX=-22.1 CenterY=-36.4 CenterZ=0 NormalX=0 NormalY=0 NormalZ=1 AngleXU=0 Radius=1.5 StartAngle=3.14159 EndAngle=6.28319
    g11: ArcOfCircle CenterX=-28.2 CenterY=-33.9 CenterZ=0 NormalX=0 NormalY=0 NormalZ=1 AngleXU=0 Radius=1.5 StartAngle=3.14159 EndAngle=6.28319
    g12: LineSegment StartX=-35.7 StartY=-10.5 StartZ=0 EndX=-35.7 EndY=-27.7 EndZ=0
    g13: LineSegment StartX=-32.7 StartY=-10.5 StartZ=0 EndX=-32.7 EndY=-27.7 EndZ=0
    g14: LineSegment StartX=-29.7 StartY=-33.9 StartZ=0 EndX=-29.7 EndY=-4.3 EndZ=0
    g15: LineSegment StartX=-26.7 StartY=-33.9 StartZ=0 EndX=-26.7 EndY=-4.3 EndZ=0
    g16: LineSegment StartX=-2.5 StartY=-10.5 StartZ=0 EndX=-2.5 EndY=-27.7 EndZ=0
    g17: LineSegment StartX=-8.5 StartY=-4.3 StartZ=0 EndX=-8.5 EndY=-33.9 EndZ=0
    g18: LineSegment StartX=-5.5 StartY=-10.5 StartZ=0 EndX=-5.5 EndY=-27.7 EndZ=0
    g19: LineSegment StartX=-11.5 StartY=-4.3 StartZ=0 EndX=-11.5 EndY=-33.9 EndZ=0
    g20: LineSegment StartX=-14.6 StartY=-1.8 StartZ=0 EndX=-14.6 EndY=-36.4 EndZ=0
    g21: LineSegment StartX=-17.6 StartY=-1.8 StartZ=0 EndX=-17.6 EndY=-36.4 EndZ=0
    g22: LineSegment StartX=-20.6 StartY=-36.4 StartZ=0 EndX=-20.6 EndY=-1.8 EndZ=0
    g23: LineSegment StartX=-23.6 StartY=-1.8 StartZ=0 EndX=-23.6 EndY=-36.4 EndZ=0
  constraints (48):
    c: Block(g0)
    c: Block(g1)
    c: Block(g2)
    c: Block(g3)
    c: Block(g4)
    c: Block(g5)
    c: Block(g6)
    c: Block(g7)
    c: Block(g8)
    c: Block(g9)
    c: Block(g10)
    c: Block(g11)
    c: Coincident(g12,g1)
    c: Coincident(g12,g2)
    c: Vertical(g12)
    c: Coincident(g13,g1)
    c: Coincident(g13,g2)
    c: Vertical(g13)
    c: Coincident(g14,g11)
    c: Coincident(g14,g7)
    c: Vertical(g14)
    c: Coincident(g15,g11)
    c: Coincident(g15,g7)
    c: Vertical(g15)
    c: Coincident(g16,g0)
    c: Coincident(g16,g3)
    c: Vertical(g16)
    c: Coincident(g17,g4)
    c: Coincident(g17,g8)
    c: Vertical(g17)
    c: Coincident(g18,g0)
    c: Coincident(g18,g3)
    c: Vertical(g18)
    c: Coincident(g19,g4)
    c: Coincident(g19,g8)
    c: Vertical(g19)
    c: Coincident(g20,g5)
    c: Coincident(g20,g9)
    c: Vertical(g20)
    c: Coincident(g21,g5)
    c: Coincident(g21,g9)
    c: Vertical(g21)
    c: Coincident(g22,g10)
    c: Coincident(g22,g6)
    c: Vertical(g22)
    c: Coincident(g23,g6)
    c: Coincident(g23,g10)
    c: Vertical(g23)
FEATURE [Part::Extrusion] Extrude039  label="removeToCreateFanGrillHoles002"
  Base = -> Sketch048
  Dir = (0,-1,6e-16)
  DirMode = 2
  FaceMakerClass = Part::FaceMakerBullseye
  LengthFwd = 10
  LengthRev = 0
  Placement = pos=(65.4,44,54.82) rot=(0,0,1;0rad)
  Solid = true
  Symmetric = false
FEATURE [Part::Cut] Cut027  label="fanScrewHousing004"
  Base = -> Cut026
  Tool = -> Extrude038
FEATURE [Part::Cut] Cut028  label="top014"
  Base = -> Fillet026
  Tool = -> Extrude039
FEATURE [Part::Feature] Face095 .. Face098  x4 (patterned run collapsed; names and placements below)
  shape: bbox 3.5 x 17.8 x 2e-07 mm, 1 faces, 0 solids (baked)
FEATURE [Part::Revolution] Revolve103  label="removeToCreateScrewAndThreadedInsertHole030"
  Angle = 360
  Axis = (0,1,0)
  Base = (0,0,0)
  FaceMakerClass = Part::FaceMakerBullseye
  Placement = pos=(62.3,30.3,19.7) rot=(0,0,1;0rad)
  Solid = false
  Source = -> Face095
  Symmetric = false
FEATURE [Part::Revolution] Revolve104  label="removeToCreateScrewAndThreadedInsertHole031"
  Angle = 360
  Axis = (0,1,0)
  Base = (0,0,0)
  FaceMakerClass = Part::FaceMakerBullseye
  Placement = pos=(62.3,30.3,51.7) rot=(0,0,1;0rad)
  Solid = false
  Source = -> Face096
  Symmetric = false
FEATURE [Part::Revolution] Revolve105  label="removeToCreateScrewAndThreadedInsertHole032"
  Angle = 360
  Axis = (0,1,0)
  Base = (0,0,0)
  FaceMakerClass = Part::FaceMakerBullseye
  Placement = pos=(30.3,30.3,19.7) rot=(0,0,1;0rad)
  Solid = false
  Source = -> Face097
  Symmetric = false
FEATURE [Part::Revolution] Revolve106  label="removeToCreateScrewAndThreadedInsertHole033"
  Angle = 360
  Axis = (0,1,0)
  Base = (0,0,0)
  FaceMakerClass = Part::FaceMakerBullseye
  Placement = pos=(30.3,30.3,51.7) rot=(0,0,1;0rad)
  Solid = false
  Source = -> Face098
  Symmetric = false
FEATURE [Part::MultiFuse] Fusion069  label="createThreadedInsertHolesForFan003"
  Shapes = -> [Revolve103,Revolve104,Revolve105,Revolve106]
FEATURE [Part::Cut] Cut029  label="top015"
  Base = -> Cut028
  Tool = -> Fusion054
FEATURE [Part::Cut] Cut030  label="fanScrewHousing005"
  Base = -> Cut027
  Tool = -> Fusion069
FEATURE [Part::Cylinder] Cylinder026  label="removeToCreteHoleForPlugHousing010"
  Angle = 360
  AttacherType = Attacher::AttachEngine3D
  Height = 20
  Placement = pos=(-2,19,36) rot=(0,1,0;1.5708rad)
  Radius = 14.3
FEATURE [Part::Box] Box018  label="removeToCreteHoleForPlugHousing011"
  AttacherType = Attacher::AttachEngine3D
  Height = 28.6
  Length = 10
  Placement = pos=(-2,0,21.7) rot=(0,0,1;0rad)
  Width = 19
FEATURE [Part::Box] Box019  label="wireHolderBottomCaseBit"
  AttacherType = Attacher::AttachEngine3D
  Height = 28
  Length = 3
  Placement = pos=(0,0,22) rot=(0,0,1;0rad)
  Width = 21
FEATURE [Part::Cylinder] Cylinder027  label="removeToCreteHoleForPlugHousing012"
  Angle = 360
  AttacherType = Attacher::AttachEngine3D
  Height = 20
  Placement = pos=(-2,19,36) rot=(0,1,0;1.5708rad)
  Radius = 14.3
FEATURE [Part::Cut] Cut031  label="wireHolderBottomCaseBit001"
  Base = -> Box019
  Tool = -> Cylinder027
FEATURE [Part::MultiFuse] Fusion070  label="removeToCreteHoleForPlugHousing013"
  Shapes = -> [Box018,Cylinder026]
FEATURE [Part::Cut] Cut032  label="top016"
  Base = -> Cut029
  Tool = -> Fusion070
FEATURE [Part::Cylinder] Cylinder028
  Angle = 360
  AttacherType = Attacher::AttachEngine3D
  Height = 20
  Placement = pos=(0,0,36.15) rot=(0,0,1;0rad)
  Radius = 14.3
FEATURE [Part::Cylinder] Cylinder029
  Angle = 360
  AttacherType = Attacher::AttachEngine3D
  Height = 10
  Placement = pos=(0,0,36.15) rot=(0,0,1;0rad)
  Radius = 4
FEATURE [Part::MultiFuse] Fusion071  label="removeToCreteHoleForPlugHousing014"
  Placement = pos=(70,19,36) rot=(0,1,0;1.5708rad)
  Shapes = -> [Cylinder028,Cylinder029]
FEATURE [Sketcher::SketchObject] Sketch049  label="topSketch011"
  FullyConstrained = true
  sketch-geometry (4):
    g0: ArcOfCircle CenterX=105 CenterY=19 CenterZ=0 NormalX=0 NormalY=0 NormalZ=1 AngleXU=0 Radius=20.6155 StartAngle=5.54125 EndAngle=6.28319
    g1: ArcOfCircle CenterX=105 CenterY=19 CenterZ=0 NormalX=0 NormalY=0 NormalZ=1 AngleXU=0 Radius=13 StartAngle=5.54125 EndAngle=6.28319
    g2: LineSegment StartX=118 StartY=19 StartZ=0 EndX=125.616 EndY=19 EndZ=0
    g3: LineSegment StartX=114.583 StartY=10.2157 StartZ=0 EndX=120.197 EndY=5.06982 EndZ=0
  constraints (7):
    c: Block(g0)
    c: Block(g1)
    c: Coincident(g2,g1)
    c: Coincident(g2,g0)
    c: Horizontal(g2)
    c: Coincident(g3,g1)
    c: Coincident(g3,g0)
FEATURE [Part::Box] Box020  label="removeToCreteHoleForPlugHousing015"
  AttacherType = Attacher::AttachEngine3D
  Height = 28.6
  Length = 20
  Placement = pos=(106.15,0,21.7) rot=(0,0,1;0rad)
  Width = 19
FEATURE [Part::MultiFuse] Fusion072  label="removeToCreteHoleForPlugHousing016"
  Shapes = -> [Box020,Fusion071]
FEATURE [Part::Cut] Cut033  label="removeToCreteHoleForPlugHousing017"
  Base = -> Cut032
  Tool = -> Fusion072
FEATURE [Part::Cylinder] Cylinder030
  Angle = 360
  AttacherType = Attacher::AttachEngine3D
  Height = 20
  Placement = pos=(0,0,36.15) rot=(0,0,1;0rad)
  Radius = 14.3
FEATURE [Part::Cylinder] Cylinder031
  Angle = 360
  AttacherType = Attacher::AttachEngine3D
  Height = 10
  Placement = pos=(0,0,36.15) rot=(0,0,1;0rad)
  Radius = 4
FEATURE [Part::Box] Box021  label="removeToCreteHoleForPlugHousing019"
  AttacherType = Attacher::AttachEngine3D
  Height = 28.6
  Length = 20
  Placement = pos=(106.15,0,21.7) rot=(0,0,1;0rad)
  Width = 19
FEATURE [Part::MultiFuse] Fusion074  label="removeToCreteHoleForPlugHousing020"
  Placement = pos=(70,19,36) rot=(0,1,0;1.5708rad)
  Shapes = -> [Cylinder030,Cylinder031]
FEATURE [Part::MultiFuse] Fusion073  label="removeToCreteHoleForPlugHousing018"
  Placement = pos=(0,0,28.3) rot=(0,0,1;0rad)
  Shapes = -> [Box021,Fusion074]
FEATURE [Part::Cylinder] Cylinder032
  Angle = 360
  AttacherType = Attacher::AttachEngine3D
  Height = 20
  Placement = pos=(0,0,36.15) rot=(0,0,1;0rad)
  Radius = 14.3
FEATURE [Part::Cylinder] Cylinder033
  Angle = 360
  AttacherType = Attacher::AttachEngine3D
  Height = 10
  Placement = pos=(0,0,36.15) rot=(0,0,1;0rad)
  Radius = 4
FEATURE [Part::Box] Box022  label="removeToCreteHoleForPlugHousing021"
  AttacherType = Attacher::AttachEngine3D
  Height = 28.6
  Length = 20
  Placement = pos=(106.15,0,21.7) rot=(0,0,1;0rad)
  Width = 19
FEATURE [Part::MultiFuse] Fusion076  label="removeToCreteHoleForPlugHousing023"
  Placement = pos=(70,19,36) rot=(0,1,0;1.5708rad)
  Shapes = -> [Cylinder032,Cylinder033]
FEATURE [Part::MultiFuse] Fusion075  label="removeToCreteHoleForPlugHousing022"
  Placement = pos=(0,0,-28.3) rot=(0,0,1;0rad)
  Shapes = -> [Box022,Fusion076]
FEATURE [Part::MultiFuse] Fusion077  label="removeToCreatePlugHousingBottomBit"
  Shapes = -> [Fusion075,Fusion073]
FEATURE [Part::Cylinder] Cylinder034
  Angle = 360
  AttacherType = Attacher::AttachEngine3D
  Height = 20
  Placement = pos=(0,0,36.15) rot=(0,0,1;0rad)
  Radius = 14
FEATURE [Part::Cylinder] Cylinder035
  Angle = 360
  AttacherType = Attacher::AttachEngine3D
  Height = 10
  Placement = pos=(0,0,36.15) rot=(0,0,1;0rad)
  Radius = 4
FEATURE [Part::MultiFuse] Fusion078  label="removeToCreteHoleForPlugHousing024"
  Placement = pos=(70,19,36) rot=(0,1,0;1.5708rad)
  Shapes = -> [Cylinder034,Cylinder035]
FEATURE [Part::MultiFuse] Fusion079  label="removeToCreatePlugHousingBottomBit001"
  Shapes = -> [Fusion078,Fusion077]
FEATURE [Part::Extrusion] Extrude040  label="bottomPlugHousingBit"
  Base = -> Sketch049
  Dir = (0,0,1)
  DirMode = 2
  FaceMakerClass = Part::FaceMakerBullseye
  LengthFwd = 72
  LengthRev = 0
  Solid = true
  Symmetric = false
FEATURE [Part::Cut] Cut034  label="bottomPlugHousingBit001"
  Base = -> Extrude040
  Placement = pos=(-0.09,0,0) rot=(0,0,1;0rad)
  Tool = -> Fusion079
FEATURE [Part::Box] Box023  label="Cube014"
  AttacherType = Attacher::AttachEngine3D
  Height = 16
  Length = 8
  Placement = pos=(12.7,31.52,28) rot=(0,0,1;0rad)
  Width = 4
FEATURE [Part::Cylinder] Cylinder036
  Angle = 360
  AttacherType = Attacher::AttachEngine3D
  Height = 10
  Placement = pos=(0,0,36.15) rot=(0,0,1;0rad)
  Radius = 4
FEATURE [Part::Cylinder] Cylinder037
  Angle = 360
  AttacherType = Attacher::AttachEngine3D
  Height = 20
  Placement = pos=(0,0,36.15) rot=(0,0,1;0rad)
  Radius = 8.2
FEATURE [Part::MultiFuse] Fusion080  label="removeToCreteHoleForPlugHousing025"
  Placement = pos=(-42,19,36) rot=(0,1,0;1.5708rad)
  Shapes = -> [Cylinder037,Cylinder036]
FEATURE [Sketcher::SketchObject] Sketch050  label="topSketch012"
  FullyConstrained = true
  sketch-geometry (4):
    g0: LineSegment StartX=16.8446 StartY=31.512 StartZ=0 EndX=16.3251 EndY=34.4666 EndZ=0
    g1: ArcOfCircle CenterX=19 CenterY=19.2524 CenterZ=0 NormalX=0 NormalY=0 NormalZ=1 AngleXU=0 Radius=15.4476 StartAngle=1.74483 EndAngle=2.72717
    g2: ArcOfCircle CenterX=19 CenterY=19.2524 CenterZ=0 NormalX=0 NormalY=0 NormalZ=1 AngleXU=0 Radius=12.4476 StartAngle=1.74483 EndAngle=2.73189
    g3: LineSegment StartX=4.86004 StartY=25.4725 StartZ=0 EndX=7.58253 EndY=24.2107 EndZ=0
  constraints (7):
    c: Block(g0)
    c: Coincident(g1,g0)
    c: Coincident(g2,g0)
    c: Coincident(g3,g1)
    c: Coincident(g3,g2)
    c: Block(g1)
    c: Block(g2)
FEATURE [Part::Extrusion] Extrude041
  Base = -> Sketch050
  Dir = (0,0,1)
  DirMode = 2
  FaceMakerClass = Part::FaceMakerBullseye
  LengthFwd = 10.6
  LengthRev = 0
  Placement = pos=(0,0,31) rot=(0,0,1;0rad)
  Solid = true
  Symmetric = false
FEATURE [Part::Cut] Cut035
  Base = -> Extrude041
  Placement = pos=(0,0,-0.3) rot=(0,0,1;0rad)
  Tool = -> Fusion080
FEATURE [Part::Cut] Cut036
  Base = -> Box023
  Tool = -> Cut035
FEATURE [Part::Fillet] Fillet027
  Base = -> Cut036
  Edges = 1 edges r=0.7: [Edge13]
FEATURE [Part::Fillet] Fillet028
  Base = -> Fillet027
  Edges = 1 edges r=0.7: [Edge13]
FEATURE [Part::Fillet] Fillet029
  Base = -> Fillet028
  Edges = 1 edges r=0.7: [Edge16]
FEATURE [Part::Fillet] Fillet030
  Base = -> Fillet029
  Edges = 1 edges r=0.7: [Edge11]
FEATURE [Part::Fillet] Fillet031
  Base = -> Fillet030
  Edges = 1 edges r=0.7: [Edge10]
FEATURE [Part::Fillet] Fillet032
  Base = -> Fillet031
  Edges = 1 edges r=1.2: [Edge5]
FEATURE [Part::Fillet] Fillet033
  Base = -> Fillet032
  Edges = 1 edges r=1.2: [Edge12]
FEATURE [Part::Fillet] Fillet034  label="wireHousingRetainer"
  Base = -> Fillet033
  Edges = 1 edges r=2: [Edge1]
  Placement = pos=(0.3,0,0) rot=(0,0,1;0rad)
FEATURE [Part::Feature] Face099
  shape: bbox 3.5 x 17.8 x 2e-07 mm, 1 faces, 0 solids (baked)
FEATURE [Part::Revolution] Revolve107  label="removeToCreateScrewAndThreadedInsertHole034"
  Angle = 360
  Axis = (0,1,0)
  Base = (0,0,0)
  FaceMakerClass = Part::FaceMakerBullseye
  Placement = pos=(12.5,0,10) rot=(0,0,1;0rad)
  Solid = false
  Source = -> Face099
  Symmetric = false
FEATURE [Part::Feature] Face100
  shape: bbox 3.5 x 17.8 x 2e-07 mm, 1 faces, 0 solids (baked)
FEATURE [Part::Revolution] Revolve108  label="removeToCreateScrewAndThreadedInsertHole035"
  Angle = 360
  Axis = (0,1,0)
  Base = (0,0,0)
  FaceMakerClass = Part::FaceMakerBullseye
  Placement = pos=(12.5,0,62) rot=(0,0,1;0rad)
  Solid = false
  Source = -> Face100
  Symmetric = false
FEATURE [Part::Feature] Face101
  shape: bbox 3.5 x 17.8 x 2e-07 mm, 1 faces, 0 solids (baked)
FEATURE [Part::Revolution] Revolve109  label="removeToCreateScrewAndThreadedInsertHole036"
  Angle = 360
  Axis = (0,1,0)
  Base = (0,0,0)
  FaceMakerClass = Part::FaceMakerBullseye
  Placement = pos=(89.5,0,68.5) rot=(0,0,1;0rad)
  Solid = false
  Source = -> Face101
  Symmetric = false
FEATURE [Part::Feature] Face102
  shape: bbox 3.5 x 17.8 x 2e-07 mm, 1 faces, 0 solids (baked)
FEATURE [Part::Revolution] Revolve110  label="removeToCreateScrewAndThreadedInsertHole037"
  Angle = 360
  Axis = (0,1,0)
  Base = (0,0,0)
  FaceMakerClass = Part::FaceMakerBullseye
  Placement = pos=(89.5,0,3.5) rot=(0,0,1;0rad)
  Solid = false
  Source = -> Face102
  Symmetric = false
FEATURE [Part::Feature] Face103
  shape: bbox 3.5 x 17.8 x 2e-07 mm, 1 faces, 0 solids (baked)
FEATURE [Part::Revolution] Revolve111  label="removeToCreateScrewAndThreadedInsertHole038"
  Angle = 360
  Axis = (0,1,0)
  Base = (0,0,0)
  FaceMakerClass = Part::FaceMakerBullseye
  Placement = pos=(109.5,4.7,3.5) rot=(0,0,1;0rad)
  Solid = false
  Source = -> Face103
  Symmetric = false
FEATURE [Part::Feature] Face104
  shape: bbox 3.5 x 17.8 x 2e-07 mm, 1 faces, 0 solids (baked)
FEATURE [Part::Revolution] Revolve112  label="removeToCreateScrewAndThreadedInsertHole039"
  Angle = 360
  Axis = (0,1,0)
  Base = (0,0,0)
  FaceMakerClass = Part::FaceMakerBullseye
  Placement = pos=(109.5,4.7,68.5) rot=(0,0,1;0rad)
  Solid = false
  Source = -> Face104
  Symmetric = false
FEATURE [Part::MultiFuse] Fusion081  label="removeToCreateScrewAndThreadedInsertHole040"
  Shapes = -> [Revolve107,Revolve108,Revolve109,Revolve110,Revolve111,Revolve112]
FEATURE [Part::MultiFuse] Fusion082  label="casePillars002"
  Shapes = -> [Revolve094,Revolve092,Revolve090,Revolve089,Revolve091,Revolve093]
FEATURE [Part::Cut] Cut037  label="casePillars003"
  Base = -> Fusion082
  Tool = -> Fusion081
FEATURE [Sketcher::SketchObject] Sketch051
  FullyConstrained = true
  Placement = pos=(117,19,0) rot=(0.57735,0.57735,0.57735;2.0944rad)
  sketch-geometry (48):
    g0: LineSegment StartX=-49.19 StartY=69.25 StartZ=0 EndX=-49.19 EndY=66.25 EndZ=0
    g1: LineSegment StartX=-49.19 StartY=63.5 StartZ=0 EndX=-49.19 EndY=60.5 EndZ=0
    g2: LineSegment StartX=-49.19 StartY=57.75 StartZ=0 EndX=-49.19 EndY=54.75 EndZ=0
    g3: LineSegment StartX=-49.19 StartY=52 StartZ=0 EndX=-49.19 EndY=49 EndZ=0
    g4: LineSegment StartX=-49.19 StartY=46.25 StartZ=0 EndX=-49.19 EndY=43.25 EndZ=0
    g5: LineSegment StartX=-49.19 StartY=40.5 StartZ=0 EndX=-49.19 EndY=37.5 EndZ=0
    g6: LineSegment StartX=-49.19 StartY=34.5 StartZ=0 EndX=-49.19 EndY=31.5 EndZ=0
    g7: LineSegment StartX=-49.19 StartY=28.75 StartZ=0 EndX=-49.19 EndY=25.75 EndZ=0
    g8: LineSegment StartX=-49.19 StartY=23 StartZ=0 EndX=-49.19 EndY=20 EndZ=0
    g9: LineSegment StartX=-49.19 StartY=17.25 StartZ=0 EndX=-49.19 EndY=14.25 EndZ=0
    g10: LineSegment StartX=-49.19 StartY=11.5 StartZ=0 EndX=-49.19 EndY=8.5 EndZ=0
    g11: LineSegment StartX=-49.19 StartY=5.75 StartZ=0 EndX=-49.19 EndY=2.75 EndZ=0
    g12: ArcOfCircle CenterX=-1.5 CenterY=67.75 CenterZ=0 NormalX=0 NormalY=0 NormalZ=1 AngleXU=0 Radius=1.5 StartAngle=4.71239 EndAngle=7.85398
    g13: ArcOfCircle CenterX=-1.5 CenterY=62 CenterZ=0 NormalX=0 NormalY=0 NormalZ=1 AngleXU=0 Radius=1.5 StartAngle=4.71239 EndAngle=7.85398
    g14: ArcOfCircle CenterX=-1.5 CenterY=56.25 CenterZ=0 NormalX=0 NormalY=0 NormalZ=1 AngleXU=0 Radius=1.5 StartAngle=4.71239 EndAngle=7.85398
    g15: ArcOfCircle CenterX=-11.49 CenterY=50.5 CenterZ=0 NormalX=0 NormalY=0 NormalZ=1 AngleXU=0 Radius=1.5 StartAngle=4.71239 EndAngle=7.85398
    g16: ArcOfCircle CenterX=-16.28 CenterY=44.75 CenterZ=0 NormalX=0 NormalY=0 NormalZ=1 AngleXU=0 Radius=1.5 StartAngle=4.71239 EndAngle=7.85398
    g17: ArcOfCircle CenterX=-18.2337 CenterY=39 CenterZ=0 NormalX=0 NormalY=0 NormalZ=1 AngleXU=0 Radius=1.5 StartAngle=4.71485 EndAngle=7.85398
    g18: ArcOfCircle CenterX=-16.2837 CenterY=27.25 CenterZ=0 NormalX=0 NormalY=0 NormalZ=1 AngleXU=0 Radius=1.5 StartAngle=4.71485 EndAngle=7.85398
    g19: ArcOfCircle CenterX=-18.2337 CenterY=33 CenterZ=0 NormalX=0 NormalY=0 NormalZ=1 AngleXU=0 Radius=1.5 StartAngle=4.71485 EndAngle=7.85398
    g20: ArcOfCircle CenterX=-11.49 CenterY=21.5 CenterZ=0 NormalX=0 NormalY=0 NormalZ=1 AngleXU=0 Radius=1.5 StartAngle=4.71239 EndAngle=7.85398
    g21: ArcOfCircle CenterX=-1.5 CenterY=4.25 CenterZ=0 NormalX=0 NormalY=0 NormalZ=1 AngleXU=0 Radius=1.5 StartAngle=4.71239 EndAngle=7.85398
    g22: ArcOfCircle CenterX=-1.5 CenterY=10 CenterZ=0 NormalX=0 NormalY=0 NormalZ=1 AngleXU=0 Radius=1.5 StartAngle=4.71239 EndAngle=7.85398
    g23: ArcOfCircle CenterX=-1.5 CenterY=15.75 CenterZ=0 NormalX=0 NormalY=0 NormalZ=1 AngleXU=0 Radius=1.5 StartAngle=4.71239 EndAngle=7.85398
    g24: LineSegment StartX=-49.19 StartY=69.25 StartZ=0 EndX=-1.5 EndY=69.25 EndZ=0
    g25: LineSegment StartX=-49.19 StartY=66.25 StartZ=0 EndX=-1.5 EndY=66.25 EndZ=0
    g26: LineSegment StartX=-49.19 StartY=63.5 StartZ=0 EndX=-1.5 EndY=63.5 EndZ=0
    g27: LineSegment StartX=-49.19 StartY=60.5 StartZ=0 EndX=-1.5 EndY=60.5 EndZ=0
    g28: LineSegment StartX=-49.19 StartY=57.75 StartZ=0 EndX=-1.5 EndY=57.75 EndZ=0
    g29: LineSegment StartX=-49.19 StartY=54.75 StartZ=0 EndX=-1.5 EndY=54.75 EndZ=0
    g30: LineSegment StartX=-49.19 StartY=52 StartZ=0 EndX=-11.49 EndY=52 EndZ=0
    g31: LineSegment StartX=-49.19 StartY=49 StartZ=0 EndX=-11.49 EndY=49 EndZ=0
    g32: LineSegment StartX=-49.19 StartY=46.25 StartZ=0 EndX=-16.28 EndY=46.25 EndZ=0
    g33: LineSegment StartX=-49.19 StartY=43.25 StartZ=0 EndX=-16.28 EndY=43.25 EndZ=0
    g34: LineSegment StartX=-49.19 StartY=40.5 StartZ=0 EndX=-18.2337 EndY=40.5 EndZ=0
    g35: LineSegment StartX=-49.19 StartY=37.5 StartZ=0 EndX=-18.23 EndY=37.5 EndZ=0
    g36: LineSegment StartX=-49.19 StartY=34.5 StartZ=0 EndX=-18.2337 EndY=34.5 EndZ=0
    g37: LineSegment StartX=-49.19 StartY=31.5 StartZ=0 EndX=-18.23 EndY=31.5 EndZ=0
    g38: LineSegment StartX=-49.19 StartY=28.75 StartZ=0 EndX=-16.2837 EndY=28.75 EndZ=0
    g39: LineSegment StartX=-49.19 StartY=25.75 StartZ=0 EndX=-16.28 EndY=25.75 EndZ=0
    g40: LineSegment StartX=-49.19 StartY=23 StartZ=0 EndX=-11.49 EndY=23 EndZ=0
    g41: LineSegment StartX=-49.19 StartY=20 StartZ=0 EndX=-11.49 EndY=20 EndZ=0
    g42: LineSegment StartX=-49.19 StartY=17.25 StartZ=0 EndX=-1.5 EndY=17.25 EndZ=0
    g43: LineSegment StartX=-49.19 StartY=14.25 StartZ=0 EndX=-1.5 EndY=14.25 EndZ=0
    g44: LineSegment StartX=-49.19 StartY=11.5 StartZ=0 EndX=-1.5 EndY=11.5 EndZ=0
    g45: LineSegment StartX=-49.19 StartY=8.5 StartZ=0 EndX=-1.5 EndY=8.5 EndZ=0
    g46: LineSegment StartX=-49.19 StartY=5.75 StartZ=0 EndX=-1.5 EndY=5.75 EndZ=0
    g47: LineSegment StartX=-49.19 StartY=2.75 StartZ=0 EndX=-1.5 EndY=2.75 EndZ=0
  constraints (120):
    c: Vertical(g0)
    c: Distance(g0) = 3
    c: Block(g0)
    c: Vertical(g1)
    c: Distance(g1) = 3
    c: Vertical(g2)
    c: Equal(g0,g2) = 3
    c: Block(g2)
    c: Vertical(g3)
    c: Equal(g1,g3) = 3
    c: Vertical(g4)
    c: Equal(g0,g4) = 3
    c: Block(g4)
    c: Vertical(g5)
    c: Equal(g1,g5) = 3
    c: Vertical(g6)
    c: Equal(g0,g6) = 3
    c: Block(g6)
    c: Vertical(g7)
    c: Equal(g1,g7) = 3
    c: Vertical(g8)
    c: Equal(g0,g8) = 3
    c: Block(g8)
    c: Vertical(g9)
    c: Equal(g1,g9) = 3
    c: Vertical(g10)
    c: Equal(g0,g10) = 3
    c: Block(g10)
    c: Vertical(g11)
    c: Equal(g1,g11) = 3
    c: Block(g12)
    c: Block(g13)
    c: Block(g14)
    c: Block(g15)
    c: Block(g16)
    c: Block(g17)
    c: Block(g18)
    c: Block(g19)
    c: Block(g20)
    c: Block(g21)
    c: Block(g22)
    c: Block(g23)
    c: Block(g11)
    c: Block(g9)
    c: Block(g7)
    c: Block(g5)
    c: Block(g3)
    c: Block(g1)
    c: Coincident(g24,g0)
    c: Coincident(g24,g12)
    c: Horizontal(g24)
    c: Coincident(g25,g0)
    c: Coincident(g25,g12)
    c: Horizontal(g25)
    c: Coincident(g26,g1)
    c: Coincident(g26,g13)
    c: Horizontal(g26)
    c: Coincident(g27,g1)
    c: Coincident(g27,g13)
    c: Horizontal(g27)
    c: Coincident(g28,g2)
    c: Coincident(g28,g14)
    c: Horizontal(g28)
    c: Coincident(g29,g2)
    c: Coincident(g29,g14)
    c: Horizontal(g29)
    c: Coincident(g30,g3)
    c: Coincident(g30,g15)
    c: Horizontal(g30)
    c: Coincident(g31,g3)
    c: Coincident(g31,g15)
    c: Horizontal(g31)
    c: Coincident(g32,g4)
    c: Coincident(g32,g16)
    c: Horizontal(g32)
    c: Coincident(g33,g4)
    c: Coincident(g33,g16)
    c: Horizontal(g33)
    c: Coincident(g34,g5)
    c: Coincident(g34,g17)
    c: Horizontal(g34)
    c: Coincident(g35,g5)
    c: Coincident(g35,g17)
    c: Horizontal(g35)
    c: Coincident(g36,g6)
    c: Coincident(g36,g19)
    c: Horizontal(g36)
    c: Coincident(g37,g6)
    c: Coincident(g37,g19)
    c: Horizontal(g37)
    c: Coincident(g38,g7)
    c: Coincident(g38,g18)
    c: Horizontal(g38)
    c: Coincident(g39,g7)
    c: Coincident(g39,g18)
    c: Horizontal(g39)
    c: Coincident(g40,g8)
    c: Coincident(g40,g20)
    c: Horizontal(g40)
    c: Coincident(g41,g8)
    c: Coincident(g41,g20)
    c: Horizontal(g41)
    c: Coincident(g42,g9)
    c: Coincident(g42,g23)
    c: Horizontal(g42)
    c: Coincident(g43,g9)
    c: Coincident(g43,g23)
    c: Horizontal(g43)
    c: Coincident(g44,g10)
    c: Coincident(g44,g22)
    c: Horizontal(g44)
    c: Coincident(g45,g10)
    c: Coincident(g45,g22)
    c: Horizontal(g45)
    c: Coincident(g46,g11)
    c: Coincident(g46,g21)
    c: Horizontal(g46)
    c: Coincident(g47,g11)
    c: Coincident(g47,g21)
    c: Horizontal(g47)
FEATURE [Part::Extrusion] Extrude042
  Base = -> Sketch051
  Dir = (1,-2e-16,2e-16)
  DirMode = 2
  FaceMakerClass = Part::FaceMakerBullseye
  LengthFwd = 19
  LengthRev = 0
  Placement = pos=(-19,0,0) rot=(0,0,1;0rad)
  Solid = true
  Symmetric = false
FEATURE [Part::Fillet] Fillet035  label="removeToCreateVentalationHoles"
  Base = -> Extrude042
  Edges = <same value as first occurrence — deduplicated (x6 in doc)>
  Placement = pos=(7,0,0) rot=(0,0,1;0rad)
FEATURE [Part::Cut] Cut038  label="top017"
  Base = -> Cut033
  Tool = -> Fillet035
FEATURE [Sketcher::SketchObject] Sketch052  label="bottomSketch001"
  FullyConstrained = true
  sketch-geometry (45):
    g0: LineSegment StartX=6.29999 StartY=8 StartZ=0 EndX=3.29999 EndY=8 EndZ=0
    g1: LineSegment StartX=3.29999 StartY=8 StartZ=0 EndX=3.29999 EndY=-6.03275e-07 EndZ=0
    g2: ArcOfCircle CenterX=8.29999 CenterY=5 CenterZ=0 NormalX=0 NormalY=0 NormalZ=1 AngleXU=0 Radius=2 StartAngle=3.14159 EndAngle=4.71239
    g3: LineSegment StartX=6.29999 StartY=8 StartZ=0 EndX=6.29999 EndY=5 EndZ=0
    g4: ArcOfCircle CenterX=105 CenterY=19 CenterZ=0 NormalX=0 NormalY=0 NormalZ=1 AngleXU=0 Radius=12.7 StartAngle=4.71239 EndAngle=5.94289
    g5-g11: Circle x7 (B-spline internal-alignment scaffolding for g12; pole/knot coordinates omitted)
    g12: BSplineCurve PolesCount=7 KnotsCount=5 Degree=3 IsPeriodic=0
    g13-g17: GeomPoint x5 (B-spline internal-alignment scaffolding for g12; pole/knot coordinates omitted)
    g18: ArcOfCircle CenterX=105 CenterY=19 CenterZ=0 NormalX=0 NormalY=0 NormalZ=1 AngleXU=0 Radius=15.7 StartAngle=5.81226 EndAngle=6.28319
    g19: BSplineCurve PolesCount=5 KnotsCount=3 Degree=3 IsPeriodic=0
    g20: LineSegment StartX=8.29999 StartY=3 StartZ=0 EndX=101.7 EndY=3 EndZ=0
    g21: LineSegment StartX=3.29999 StartY=-6.03275e-07 StartZ=0 EndX=105 EndY=-6.03275e-07 EndZ=0
    g22: LineSegment StartX=120.974 StartY=8.71251 StartZ=0 EndX=122.332 EndY=7.83778 EndZ=0
    g23: LineSegment StartX=105 StartY=-6.03274e-07 StartZ=0 EndX=113 EndY=-6.03274e-07 EndZ=0
    g24: ArcOfCircle CenterX=105 CenterY=19 CenterZ=0 NormalX=0 NormalY=0 NormalZ=1 AngleXU=0 Radius=20.6155 StartAngle=5.11091 EndAngle=5.71103
    g25: ArcOfCircle CenterX=117.7 CenterY=19 CenterZ=0 NormalX=0 NormalY=0 NormalZ=1 AngleXU=0 Radius=3 StartAngle=1.2e-15 EndAngle=2.10468
    g26: Circle CenterX=116.345 CenterY=16.3232 CenterZ=0 NormalX=0 NormalY=0 NormalZ=1 AngleXU=0 Radius=1
    g27: Circle CenterX=117.24 CenterY=15.7584 CenterZ=0 NormalX=0 NormalY=0 NormalZ=1 AngleXU=0 Radius=1
    g28: Circle CenterX=116.972 CenterY=14.7612 CenterZ=0 NormalX=0 NormalY=0 NormalZ=1 AngleXU=0 Radius=1
    g29: BSplineCurve PolesCount=3 KnotsCount=2 Degree=2 IsPeriodic=0
    g30: GeomPoint X=116.345 Y=16.3232 Z=0
    g31: GeomPoint X=116.972 Y=14.7612 Z=0
    g32: Circle CenterX=115.828 CenterY=17.157 CenterZ=0 NormalX=0 NormalY=0 NormalZ=1 AngleXU=0 Radius=1
    g33: Circle CenterX=115.841 CenterY=16.639 CenterZ=0 NormalX=0 NormalY=0 NormalZ=1 AngleXU=0 Radius=1
    g34: Circle CenterX=116.345 CenterY=16.3232 CenterZ=0 NormalX=0 NormalY=0 NormalZ=1 AngleXU=0 Radius=1
    g35: BSplineCurve PolesCount=3 KnotsCount=2 Degree=2 IsPeriodic=0
    g36: GeomPoint X=115.828 Y=17.157 Z=0
    g37: GeomPoint X=116.345 Y=16.3232 Z=0
    g38: LineSegment StartX=115.828 StartY=17.157 StartZ=0 EndX=115.828 EndY=20.8307 EndZ=0
    g39: Circle CenterX=115.828 CenterY=20.8307 CenterZ=0 NormalX=0 NormalY=0 NormalZ=1 AngleXU=0 Radius=1
    g40: Circle CenterX=115.831 CenterY=21.3396 CenterZ=0 NormalX=0 NormalY=0 NormalZ=1 AngleXU=0 Radius=1
    g41: Circle CenterX=116.173 CenterY=21.5825 CenterZ=0 NormalX=0 NormalY=0 NormalZ=1 AngleXU=0 Radius=1
    g42: BSplineCurve PolesCount=3 KnotsCount=2 Degree=2 IsPeriodic=0
    g43: GeomPoint X=115.828 Y=20.8307 Z=0
    g44: GeomPoint X=116.173 Y=21.5825 Z=0
  constraints (70):
    c: Horizontal(g0)
    c: Distance(g0) = 3
    c: Coincident(g1,g0)
    c: Vertical(g1)
    c: Block(g2)
    c: Block(g0)
    c: Coincident(g3,g0)
    c: Coincident(g3,g2)
    c: Vertical(g3)
    c: Block(g1)
    c: Block(g4)
    c: Coincident(g19,g4)
    c: Block(g19)
    c: Equal(g5, g6-g11) x6
    c: InternalAlignment(g5-g11 -> g12) x7
    c: InternalAlignment(g13-g17 -> g12) x5
    c: Block(g12)
    c: Coincident(g18,g12)
    c: Block(g18)
    c: Coincident(g20,g2)
    c: Coincident(g20,g19)
    c: Horizontal(g20)
    c: Distance(g20) = 93.4
    c: Coincident(g21,g1)
    c: Horizontal(g21)
    c: Distance(g21) = 101.7
    c: Horizontal(g23)
    c: Distance(g23) = 8
    c: Coincident(g24,g23)
    c: Block(g23)
    c: Coincident(g22,g24)
    c: Block(g24)
    c: Block(g22)
    c: Distance(g22) = 1.61553
    c: Coincident(g25,g18)
    c: Block(g25)
    c: Weight(g26) = 1
    c: Equal(g26,g27)
    c: Equal(g26,g28)
    c: Coincident(g29,g4)
    c: InternalAlignment(g26,g29)
    c: InternalAlignment(g27,g29)
    c: InternalAlignment(g28,g29)
    c: InternalAlignment(g30,g29)
    c: InternalAlignment(g31,g29)
    c: Block(g29)
    c: Weight(g32) = 1
    c: Equal(g32,g33)
    c: Equal(g32,g34)
    c: Coincident(g35,g29)
    c: InternalAlignment(g32,g35)
    c: InternalAlignment(g33,g35)
    c: InternalAlignment(g34,g35)
    c: InternalAlignment(g36,g35)
    c: InternalAlignment(g37,g35)
    c: Block(g35)
    c: Coincident(g38,g35)
    c: Vertical(g38)
    c: Block(g38)
    c: Coincident(g42,g38)
    c: Weight(g39) = 1
    c: Equal(g39,g40)
    c: Equal(g39,g41)
    c: Coincident(g42,g25)
    c: InternalAlignment(g39,g42)
    c: InternalAlignment(g40,g42)
    c: InternalAlignment(g41,g42)
    c: InternalAlignment(g43,g42)
    c: InternalAlignment(g44,g42)
    c: Block(g42)
FEATURE [Part::Extrusion] Extrude043  label="bottom010"
  Base = -> Sketch052
  Dir = (0,0,1)
  DirMode = 2
  FaceMakerClass = Part::FaceMakerBullseye
  LengthFwd = 71.4
  LengthRev = 0
  Placement = pos=(0,0,0.3) rot=(0,0,1;0rad)
  Solid = true
  Symmetric = false
FEATURE [Sketcher::SketchObject] Sketch053  label="topSketch013"
  FullyConstrained = true
  sketch-geometry (22):
    g0: LineSegment StartX=5.21097e-06 StartY=3 StartZ=0 EndX=5.21097e-06 EndY=19 EndZ=0
    g1: ArcOfCircle CenterX=19 CenterY=19 CenterZ=0 NormalX=0 NormalY=0 NormalZ=1 AngleXU=0 Radius=19 StartAngle=1.5708 EndAngle=3.14159
    g2: ArcOfCircle CenterX=19 CenterY=19 CenterZ=0 NormalX=0 NormalY=0 NormalZ=1 AngleXU=0 Radius=16 StartAngle=1.5708 EndAngle=3.14159
    g3: LineSegment StartX=114 StartY=35 StartZ=0 EndX=19 EndY=35 EndZ=0
    g4: LineSegment StartX=5.21097e-06 StartY=3 StartZ=0 EndX=5.21097e-06 EndY=0 EndZ=0
    g5: LineSegment StartX=3 StartY=0 StartZ=0 EndX=5.21097e-06 EndY=0 EndZ=0
    g6: LineSegment StartX=3 StartY=19 StartZ=0 EndX=3 EndY=0 EndZ=0
    g7: LineSegment StartX=19 StartY=38 StartZ=0 EndX=124 EndY=38 EndZ=0
    g8: Circle CenterX=119 CenterY=35 CenterZ=0 NormalX=0 NormalY=0 NormalZ=1 AngleXU=0 Radius=1
    g9: Circle CenterX=121 CenterY=35 CenterZ=0 NormalX=0 NormalY=0 NormalZ=1 AngleXU=0 Radius=1
    g10: Circle CenterX=121 CenterY=33 CenterZ=0 NormalX=0 NormalY=0 NormalZ=1 AngleXU=0 Radius=1
    g11: BSplineCurve PolesCount=3 KnotsCount=2 Degree=2 IsPeriodic=0
    g12: GeomPoint X=119 Y=35 Z=0
    g13: GeomPoint X=121 Y=33 Z=0
    g14: LineSegment StartX=119 StartY=35 StartZ=0 EndX=114 EndY=35 EndZ=0
    g15: ArcOfCircle CenterX=105 CenterY=19 CenterZ=0 NormalX=0 NormalY=0 NormalZ=1 AngleXU=0 Radius=16 StartAngle=5.60905 EndAngle=6.28319
    g16: LineSegment StartX=121 StartY=33 StartZ=0 EndX=121 EndY=19 EndZ=0
    g17: LineSegment StartX=117.5 StartY=9.01251 StartZ=0 EndX=121.163 EndY=9.0125 EndZ=0
    g18: ArcOfCircle CenterX=105 CenterY=19 CenterZ=0 NormalX=0 NormalY=0 NormalZ=1 AngleXU=0 Radius=20.6155 StartAngle=5.7297 EndAngle=6.28319
    g19: LineSegment StartX=121.163 StartY=9.0125 StartZ=0 EndX=122.538 EndY=8.16329 EndZ=0
    g20: LineSegment StartX=124 StartY=38 StartZ=0 EndX=125.616 EndY=38 EndZ=0
    g21: LineSegment StartX=125.616 StartY=19 StartZ=0 EndX=125.616 EndY=38 EndZ=0
  constraints (50):
    c: Vertical(g0)
    c: Block(g0)
    c: Coincident(g1,g0)
    c: Block(g1)
    c: Coincident(g2,g1)
    c: Block(g2)
    c: Coincident(g3,g2)
    c: Horizontal(g3)
    c: Tangent(g3,g2)
    c: Coincident(g4,g0)
    c: Distance(g4) = 3
    c: Vertical(g4)
    c: Coincident(g5,g4)
    c: Horizontal(g5)
    c: Coincident(g6,g2)
    c: Coincident(g6,g5)
    c: Vertical(g6)
    c: Horizontal(g7)
    c: Distance(g7) = 105
    c: Coincident(g7,g1)
    c: Block(g3)
    c: Weight(g8) = 1
    c: Equal(g8,g9)
    c: Equal(g8,g10)
    c: InternalAlignment(g8,g11)
    c: InternalAlignment(g9,g11)
    c: InternalAlignment(g10,g11)
    c: InternalAlignment(g12,g11)
    c: InternalAlignment(g13,g11)
    c: Block(g11)
    c: Coincident(g14,g11)
    c: Coincident(g14,g3)
    c: Horizontal(g14)
    c: Block(g15)
    c: Coincident(g16,g11)
    c: Coincident(g16,g15)
    c: Vertical(g16)
    c: Distance(g16) = 14
    c: Coincident(g17,g15)
    c: Block(g18)
    c: Coincident(g19,g18)
    c: Coincident(g20,g7)
    c: Horizontal(g20)
    c: Vertical(g21)
    c: Coincident(g20,g21)
    c: Block(g20)
    c: Block(g21)
    c: Block(g19)
    c: Block(g17)
    c: Distance(g20) = 1.61553
FEATURE [Part::Extrusion] Extrude044
  Base = -> Sketch053
  Dir = (0,0,1)
  DirMode = 2
  FaceMakerClass = Part::FaceMakerBullseye
  LengthFwd = 72
  LengthRev = 0
  Solid = true
  Symmetric = false
FEATURE [Part::Fillet] Fillet036  label="top018"
  Base = -> Extrude044
  Edges = 1 edges r=2: [Edge41]
FEATURE [Sketcher::SketchObject] Sketch054
  FullyConstrained = false
  Placement = pos=(0,0,0) rot=(1,0,0;1.5708rad)
  sketch-geometry (24):
    g0: ArcOfCircle CenterX=-4 CenterY=-10.5 CenterZ=0 NormalX=0 NormalY=0 NormalZ=1 AngleXU=0 Radius=1.5 StartAngle=6e-16 EndAngle=3.14159
    g1: ArcOfCircle CenterX=-34.2 CenterY=-10.5 CenterZ=0 NormalX=0 NormalY=0 NormalZ=1 AngleXU=0 Radius=1.5 StartAngle=0 EndAngle=3.14159
    g2: ArcOfCircle CenterX=-34.2 CenterY=-27.7 CenterZ=0 NormalX=0 NormalY=0 NormalZ=1 AngleXU=0 Radius=1.5 StartAngle=3.14159 EndAngle=6.28319
    g3: ArcOfCircle CenterX=-4 CenterY=-27.7 CenterZ=0 NormalX=0 NormalY=0 NormalZ=1 AngleXU=0 Radius=1.5 StartAngle=3.1416 EndAngle=6.28319
    g4: ArcOfCircle CenterX=-10 CenterY=-4.3 CenterZ=0 NormalX=0 NormalY=0 NormalZ=1 AngleXU=0 Radius=1.5 StartAngle=2e-16 EndAngle=3.14159
    g5: ArcOfCircle CenterX=-16.1 CenterY=-1.8 CenterZ=0 NormalX=0 NormalY=0 NormalZ=1 AngleXU=0 Radius=1.5 StartAngle=5e-16 EndAngle=3.14159
    g6: ArcOfCircle CenterX=-22.1 CenterY=-1.8 CenterZ=0 NormalX=0 NormalY=0 NormalZ=1 AngleXU=0 Radius=1.5 StartAngle=5e-16 EndAngle=3.14159
    g7: ArcOfCircle CenterX=-28.2 CenterY=-4.3 CenterZ=0 NormalX=0 NormalY=0 NormalZ=1 AngleXU=0 Radius=1.5 StartAngle=2e-16 EndAngle=3.14159
    g8: ArcOfCircle CenterX=-10 CenterY=-33.9 CenterZ=0 NormalX=0 NormalY=0 NormalZ=1 AngleXU=0 Radius=1.5 StartAngle=3.14159 EndAngle=6.28319
    g9: ArcOfCircle CenterX=-16.1 CenterY=-36.4 CenterZ=0 NormalX=0 NormalY=0 NormalZ=1 AngleXU=0 Radius=1.5 StartAngle=3.14159 EndAngle=6.28319
    g10: ArcOfCircle CenterX=-22.1 CenterY=-36.4 CenterZ=0 NormalX=0 NormalY=0 NormalZ=1 AngleXU=0 Radius=1.5 StartAngle=3.14159 EndAngle=6.28319
    g11: ArcOfCircle CenterX=-28.2 CenterY=-33.9 CenterZ=0 NormalX=0 NormalY=0 NormalZ=1 AngleXU=0 Radius=1.5 StartAngle=3.14159 EndAngle=6.28319
    g12: LineSegment StartX=-35.7 StartY=-10.5 StartZ=0 EndX=-35.7 EndY=-27.7 EndZ=0
    g13: LineSegment StartX=-32.7 StartY=-10.5 StartZ=0 EndX=-32.7 EndY=-27.7 EndZ=0
    g14: LineSegment StartX=-29.7 StartY=-33.9 StartZ=0 EndX=-29.7 EndY=-4.3 EndZ=0
    g15: LineSegment StartX=-26.7 StartY=-33.9 StartZ=0 EndX=-26.7 EndY=-4.3 EndZ=0
    g16: LineSegment StartX=-2.5 StartY=-10.5 StartZ=0 EndX=-2.5 EndY=-27.7 EndZ=0
    g17: LineSegment StartX=-8.5 StartY=-4.3 StartZ=0 EndX=-8.5 EndY=-33.9 EndZ=0
    g18: LineSegment StartX=-5.5 StartY=-10.5 StartZ=0 EndX=-5.5 EndY=-27.7 EndZ=0
    g19: LineSegment StartX=-11.5 StartY=-4.3 StartZ=0 EndX=-11.5 EndY=-33.9 EndZ=0
    g20: LineSegment StartX=-14.6 StartY=-1.8 StartZ=0 EndX=-14.6 EndY=-36.4 EndZ=0
    g21: LineSegment StartX=-17.6 StartY=-1.8 StartZ=0 EndX=-17.6 EndY=-36.4 EndZ=0
    g22: LineSegment StartX=-20.6 StartY=-36.4 StartZ=0 EndX=-20.6 EndY=-1.8 EndZ=0
    g23: LineSegment StartX=-23.6 StartY=-1.8 StartZ=0 EndX=-23.6 EndY=-36.4 EndZ=0
  constraints (48):
    c: Block(g0)
    c: Block(g1)
    c: Block(g2)
    c: Block(g3)
    c: Block(g4)
    c: Block(g5)
    c: Block(g6)
    c: Block(g7)
    c: Block(g8)
    c: Block(g9)
    c: Block(g10)
    c: Block(g11)
    c: Coincident(g12,g1)
    c: Coincident(g12,g2)
    c: Vertical(g12)
    c: Coincident(g13,g1)
    c: Coincident(g13,g2)
    c: Vertical(g13)
    c: Coincident(g14,g11)
    c: Coincident(g14,g7)
    c: Vertical(g14)
    c: Coincident(g15,g11)
    c: Coincident(g15,g7)
    c: Vertical(g15)
    c: Coincident(g16,g0)
    c: Coincident(g16,g3)
    c: Vertical(g16)
    c: Coincident(g17,g4)
    c: Coincident(g17,g8)
    c: Vertical(g17)
    c: Coincident(g18,g0)
    c: Coincident(g18,g3)
    c: Vertical(g18)
    c: Coincident(g19,g4)
    c: Coincident(g19,g8)
    c: Vertical(g19)
    c: Coincident(g20,g5)
    c: Coincident(g20,g9)
    c: Vertical(g20)
    c: Coincident(g21,g5)
    c: Coincident(g21,g9)
    c: Vertical(g21)
    c: Coincident(g22,g10)
    c: Coincident(g22,g6)
    c: Vertical(g22)
    c: Coincident(g23,g6)
    c: Coincident(g23,g10)
    c: Vertical(g23)
FEATURE [Part::Extrusion] Extrude045  label="removeToCreateFanGrillHoles003"
  Base = -> Sketch054
  Dir = (0,-1,6e-16)
  DirMode = 2
  FaceMakerClass = Part::FaceMakerBullseye
  LengthFwd = 10
  LengthRev = 0
  Placement = pos=(65.4,44,54.82) rot=(0,0,1;0rad)
  Solid = true
  Symmetric = false
FEATURE [Part::Feature] Face105 .. Face108  x4 (patterned run collapsed; names and placements below)
  shape: bbox 3.5 x 17.8 x 2e-07 mm, 1 faces, 0 solids (baked)
FEATURE [Part::Revolution] Revolve113  label="removeToCreateScrewAndThreadedInsertHole041"
  Angle = 360
  Axis = (0,1,0)
  Base = (0,0,0)
  FaceMakerClass = Part::FaceMakerBullseye
  Placement = pos=(62.3,30.3,19.7) rot=(0,0,1;0rad)
  Solid = false
  Source = -> Face105
  Symmetric = false
FEATURE [Part::Revolution] Revolve114  label="removeToCreateScrewAndThreadedInsertHole042"
  Angle = 360
  Axis = (0,1,0)
  Base = (0,0,0)
  FaceMakerClass = Part::FaceMakerBullseye
  Placement = pos=(62.3,30.3,51.7) rot=(0,0,1;0rad)
  Solid = false
  Source = -> Face106
  Symmetric = false
FEATURE [Part::Revolution] Revolve115  label="removeToCreateScrewAndThreadedInsertHole043"
  Angle = 360
  Axis = (0,1,0)
  Base = (0,0,0)
  FaceMakerClass = Part::FaceMakerBullseye
  Placement = pos=(30.3,30.3,19.7) rot=(0,0,1;0rad)
  Solid = false
  Source = -> Face107
  Symmetric = false
FEATURE [Part::Revolution] Revolve116  label="removeToCreateScrewAndThreadedInsertHole044"
  Angle = 360
  Axis = (0,1,0)
  Base = (0,0,0)
  FaceMakerClass = Part::FaceMakerBullseye
  Placement = pos=(30.3,30.3,51.7) rot=(0,0,1;0rad)
  Solid = false
  Source = -> Face108
  Symmetric = false
FEATURE [Part::MultiFuse] Fusion083  label="createThreadedInsertHolesForFan004"
  Shapes = -> [Revolve113,Revolve114,Revolve115,Revolve116]
FEATURE [Part::Box] Box024  label="removeToCreteHoleForPlugHousing026"
  AttacherType = Attacher::AttachEngine3D
  Height = 28.6
  Length = 10
  Placement = pos=(-2,0,21.7) rot=(0,0,1;0rad)
  Width = 19
FEATURE [Part::Cylinder] Cylinder038  label="removeToCreteHoleForPlugHousing027"
  Angle = 360
  AttacherType = Attacher::AttachEngine3D
  Height = 20
  Placement = pos=(-2,19,36) rot=(0,1,0;1.5708rad)
  Radius = 14.3
FEATURE [Part::MultiFuse] Fusion084  label="removeToCreteHoleForPlugHousing028"
  Shapes = -> [Box024,Cylinder038]
FEATURE [Part::Cylinder] Cylinder039
  Angle = 360
  AttacherType = Attacher::AttachEngine3D
  Height = 20
  Placement = pos=(0,0,36.15) rot=(0,0,1;0rad)
  Radius = 14.3
FEATURE [Part::Cylinder] Cylinder040
  Angle = 360
  AttacherType = Attacher::AttachEngine3D
  Height = 10
  Placement = pos=(0,0,36.15) rot=(0,0,1;0rad)
  Radius = 4
FEATURE [Part::Box] Box025  label="removeToCreteHoleForPlugHousing030"
  AttacherType = Attacher::AttachEngine3D
  Height = 28.6
  Length = 20
  Placement = pos=(106.15,0,21.7) rot=(0,0,1;0rad)
  Width = 19
FEATURE [Part::MultiFuse] Fusion086  label="removeToCreteHoleForPlugHousing031"
  Placement = pos=(70,19,36) rot=(0,1,0;1.5708rad)
  Shapes = -> [Cylinder039,Cylinder040]
FEATURE [Part::MultiFuse] Fusion085  label="removeToCreteHoleForPlugHousing029"
  Shapes = -> [Box025,Fusion086]
FEATURE [Sketcher::SketchObject] Sketch055
  FullyConstrained = true
  Placement = pos=(117,19,0) rot=(0.57735,0.57735,0.57735;2.0944rad)
  sketch-geometry (48):
    g0: LineSegment StartX=-49.19 StartY=69.25 StartZ=0 EndX=-49.19 EndY=66.25 EndZ=0
    g1: LineSegment StartX=-49.19 StartY=63.5 StartZ=0 EndX=-49.19 EndY=60.5 EndZ=0
    g2: LineSegment StartX=-49.19 StartY=57.75 StartZ=0 EndX=-49.19 EndY=54.75 EndZ=0
    g3: LineSegment StartX=-49.19 StartY=52 StartZ=0 EndX=-49.19 EndY=49 EndZ=0
    g4: LineSegment StartX=-49.19 StartY=46.25 StartZ=0 EndX=-49.19 EndY=43.25 EndZ=0
    g5: LineSegment StartX=-49.19 StartY=40.5 StartZ=0 EndX=-49.19 EndY=37.5 EndZ=0
    g6: LineSegment StartX=-49.19 StartY=34.5 StartZ=0 EndX=-49.19 EndY=31.5 EndZ=0
    g7: LineSegment StartX=-49.19 StartY=28.75 StartZ=0 EndX=-49.19 EndY=25.75 EndZ=0
    g8: LineSegment StartX=-49.19 StartY=23 StartZ=0 EndX=-49.19 EndY=20 EndZ=0
    g9: LineSegment StartX=-49.19 StartY=17.25 StartZ=0 EndX=-49.19 EndY=14.25 EndZ=0
    g10: LineSegment StartX=-49.19 StartY=11.5 StartZ=0 EndX=-49.19 EndY=8.5 EndZ=0
    g11: LineSegment StartX=-49.19 StartY=5.75 StartZ=0 EndX=-49.19 EndY=2.75 EndZ=0
    g12: ArcOfCircle CenterX=-1.5 CenterY=67.75 CenterZ=0 NormalX=0 NormalY=0 NormalZ=1 AngleXU=0 Radius=1.5 StartAngle=4.71239 EndAngle=7.85398
    g13: ArcOfCircle CenterX=-1.5 CenterY=62 CenterZ=0 NormalX=0 NormalY=0 NormalZ=1 AngleXU=0 Radius=1.5 StartAngle=4.71239 EndAngle=7.85398
    g14: ArcOfCircle CenterX=-1.5 CenterY=56.25 CenterZ=0 NormalX=0 NormalY=0 NormalZ=1 AngleXU=0 Radius=1.5 StartAngle=4.71239 EndAngle=7.85398
    g15: ArcOfCircle CenterX=-11.49 CenterY=50.5 CenterZ=0 NormalX=0 NormalY=0 NormalZ=1 AngleXU=0 Radius=1.5 StartAngle=4.71239 EndAngle=7.85398
    g16: ArcOfCircle CenterX=-16.28 CenterY=44.75 CenterZ=0 NormalX=0 NormalY=0 NormalZ=1 AngleXU=0 Radius=1.5 StartAngle=4.71239 EndAngle=7.85398
    g17: ArcOfCircle CenterX=-18.2337 CenterY=39 CenterZ=0 NormalX=0 NormalY=0 NormalZ=1 AngleXU=0 Radius=1.5 StartAngle=4.71485 EndAngle=7.85398
    g18: ArcOfCircle CenterX=-16.2837 CenterY=27.25 CenterZ=0 NormalX=0 NormalY=0 NormalZ=1 AngleXU=0 Radius=1.5 StartAngle=4.71485 EndAngle=7.85398
    g19: ArcOfCircle CenterX=-18.2337 CenterY=33 CenterZ=0 NormalX=0 NormalY=0 NormalZ=1 AngleXU=0 Radius=1.5 StartAngle=4.71485 EndAngle=7.85398
    g20: ArcOfCircle CenterX=-11.49 CenterY=21.5 CenterZ=0 NormalX=0 NormalY=0 NormalZ=1 AngleXU=0 Radius=1.5 StartAngle=4.71239 EndAngle=7.85398
    g21: ArcOfCircle CenterX=-1.5 CenterY=4.25 CenterZ=0 NormalX=0 NormalY=0 NormalZ=1 AngleXU=0 Radius=1.5 StartAngle=4.71239 EndAngle=7.85398
    g22: ArcOfCircle CenterX=-1.5 CenterY=10 CenterZ=0 NormalX=0 NormalY=0 NormalZ=1 AngleXU=0 Radius=1.5 StartAngle=4.71239 EndAngle=7.85398
    g23: ArcOfCircle CenterX=-1.5 CenterY=15.75 CenterZ=0 NormalX=0 NormalY=0 NormalZ=1 AngleXU=0 Radius=1.5 StartAngle=4.71239 EndAngle=7.85398
    g24: LineSegment StartX=-49.19 StartY=69.25 StartZ=0 EndX=-1.5 EndY=69.25 EndZ=0
    g25: LineSegment StartX=-49.19 StartY=66.25 StartZ=0 EndX=-1.5 EndY=66.25 EndZ=0
    g26: LineSegment StartX=-49.19 StartY=63.5 StartZ=0 EndX=-1.5 EndY=63.5 EndZ=0
    g27: LineSegment StartX=-49.19 StartY=60.5 StartZ=0 EndX=-1.5 EndY=60.5 EndZ=0
    g28: LineSegment StartX=-49.19 StartY=57.75 StartZ=0 EndX=-1.5 EndY=57.75 EndZ=0
    g29: LineSegment StartX=-49.19 StartY=54.75 StartZ=0 EndX=-1.5 EndY=54.75 EndZ=0
    g30: LineSegment StartX=-49.19 StartY=52 StartZ=0 EndX=-11.49 EndY=52 EndZ=0
    g31: LineSegment StartX=-49.19 StartY=49 StartZ=0 EndX=-11.49 EndY=49 EndZ=0
    g32: LineSegment StartX=-49.19 StartY=46.25 StartZ=0 EndX=-16.28 EndY=46.25 EndZ=0
    g33: LineSegment StartX=-49.19 StartY=43.25 StartZ=0 EndX=-16.28 EndY=43.25 EndZ=0
    g34: LineSegment StartX=-49.19 StartY=40.5 StartZ=0 EndX=-18.2337 EndY=40.5 EndZ=0
    g35: LineSegment StartX=-49.19 StartY=37.5 StartZ=0 EndX=-18.23 EndY=37.5 EndZ=0
    g36: LineSegment StartX=-49.19 StartY=34.5 StartZ=0 EndX=-18.2337 EndY=34.5 EndZ=0
    g37: LineSegment StartX=-49.19 StartY=31.5 StartZ=0 EndX=-18.23 EndY=31.5 EndZ=0
    g38: LineSegment StartX=-49.19 StartY=28.75 StartZ=0 EndX=-16.2837 EndY=28.75 EndZ=0
    g39: LineSegment StartX=-49.19 StartY=25.75 StartZ=0 EndX=-16.28 EndY=25.75 EndZ=0
    g40: LineSegment StartX=-49.19 StartY=23 StartZ=0 EndX=-11.49 EndY=23 EndZ=0
    g41: LineSegment StartX=-49.19 StartY=20 StartZ=0 EndX=-11.49 EndY=20 EndZ=0
    g42: LineSegment StartX=-49.19 StartY=17.25 StartZ=0 EndX=-1.5 EndY=17.25 EndZ=0
    g43: LineSegment StartX=-49.19 StartY=14.25 StartZ=0 EndX=-1.5 EndY=14.25 EndZ=0
    g44: LineSegment StartX=-49.19 StartY=11.5 StartZ=0 EndX=-1.5 EndY=11.5 EndZ=0
    g45: LineSegment StartX=-49.19 StartY=8.5 StartZ=0 EndX=-1.5 EndY=8.5 EndZ=0
    g46: LineSegment StartX=-49.19 StartY=5.75 StartZ=0 EndX=-1.5 EndY=5.75 EndZ=0
    g47: LineSegment StartX=-49.19 StartY=2.75 StartZ=0 EndX=-1.5 EndY=2.75 EndZ=0
  constraints (120):
    c: Vertical(g0)
    c: Distance(g0) = 3
    c: Block(g0)
    c: Vertical(g1)
    c: Distance(g1) = 3
    c: Vertical(g2)
    c: Equal(g0,g2) = 3
    c: Block(g2)
    c: Vertical(g3)
    c: Equal(g1,g3) = 3
    c: Vertical(g4)
    c: Equal(g0,g4) = 3
    c: Block(g4)
    c: Vertical(g5)
    c: Equal(g1,g5) = 3
    c: Vertical(g6)
    c: Equal(g0,g6) = 3
    c: Block(g6)
    c: Vertical(g7)
    c: Equal(g1,g7) = 3
    c: Vertical(g8)
    c: Equal(g0,g8) = 3
    c: Block(g8)
    c: Vertical(g9)
    c: Equal(g1,g9) = 3
    c: Vertical(g10)
    c: Equal(g0,g10) = 3
    c: Block(g10)
    c: Vertical(g11)
    c: Equal(g1,g11) = 3
    c: Block(g12)
    c: Block(g13)
    c: Block(g14)
    c: Block(g15)
    c: Block(g16)
    c: Block(g17)
    c: Block(g18)
    c: Block(g19)
    c: Block(g20)
    c: Block(g21)
    c: Block(g22)
    c: Block(g23)
    c: Block(g11)
    c: Block(g9)
    c: Block(g7)
    c: Block(g5)
    c: Block(g3)
    c: Block(g1)
    c: Coincident(g24,g0)
    c: Coincident(g24,g12)
    c: Horizontal(g24)
    c: Coincident(g25,g0)
    c: Coincident(g25,g12)
    c: Horizontal(g25)
    c: Coincident(g26,g1)
    c: Coincident(g26,g13)
    c: Horizontal(g26)
    c: Coincident(g27,g1)
    c: Coincident(g27,g13)
    c: Horizontal(g27)
    c: Coincident(g28,g2)
    c: Coincident(g28,g14)
    c: Horizontal(g28)
    c: Coincident(g29,g2)
    c: Coincident(g29,g14)
    c: Horizontal(g29)
    c: Coincident(g30,g3)
    c: Coincident(g30,g15)
    c: Horizontal(g30)
    c: Coincident(g31,g3)
    c: Coincident(g31,g15)
    c: Horizontal(g31)
    c: Coincident(g32,g4)
    c: Coincident(g32,g16)
    c: Horizontal(g32)
    c: Coincident(g33,g4)
    c: Coincident(g33,g16)
    c: Horizontal(g33)
    c: Coincident(g34,g5)
    c: Coincident(g34,g17)
    c: Horizontal(g34)
    c: Coincident(g35,g5)
    c: Coincident(g35,g17)
    c: Horizontal(g35)
    c: Coincident(g36,g6)
    c: Coincident(g36,g19)
    c: Horizontal(g36)
    c: Coincident(g37,g6)
    c: Coincident(g37,g19)
    c: Horizontal(g37)
    c: Coincident(g38,g7)
    c: Coincident(g38,g18)
    c: Horizontal(g38)
    c: Coincident(g39,g7)
    c: Coincident(g39,g18)
    c: Horizontal(g39)
    c: Coincident(g40,g8)
    c: Coincident(g40,g20)
    c: Horizontal(g40)
    c: Coincident(g41,g8)
    c: Coincident(g41,g20)
    c: Horizontal(g41)
    c: Coincident(g42,g9)
    c: Coincident(g42,g23)
    c: Horizontal(g42)
    c: Coincident(g43,g9)
    c: Coincident(g43,g23)
    c: Horizontal(g43)
    c: Coincident(g44,g10)
    c: Coincident(g44,g22)
    c: Horizontal(g44)
    c: Coincident(g45,g10)
    c: Coincident(g45,g22)
    c: Horizontal(g45)
    c: Coincident(g46,g11)
    c: Coincident(g46,g21)
    c: Horizontal(g46)
    c: Coincident(g47,g11)
    c: Coincident(g47,g21)
    c: Horizontal(g47)
FEATURE [Part::Extrusion] Extrude046
  Base = -> Sketch055
  Dir = (1,0,0)
  DirMode = 2
  FaceMakerClass = Part::FaceMakerBullseye
  LengthFwd = 23
  LengthRev = 0
  Placement = pos=(-19,0,0) rot=(0,0,1;0rad)
  Solid = true
  Symmetric = false
FEATURE [Part::Fillet] Fillet038  label="removeToCreateVentalationHoles001"
  Base = -> Extrude046
  Edges = <same value as first occurrence — deduplicated (x6 in doc)>
  Placement = pos=(7,0,0) rot=(0,0,1;0rad)
FEATURE [Sketcher::SketchObject] Sketch056  label="topSketch014"
  FullyConstrained = true
  sketch-geometry (22):
    g0: LineSegment StartX=5.21097e-06 StartY=3 StartZ=0 EndX=5.21097e-06 EndY=19 EndZ=0
    g1: ArcOfCircle CenterX=19 CenterY=19 CenterZ=0 NormalX=0 NormalY=0 NormalZ=1 AngleXU=0 Radius=19 StartAngle=1.5708 EndAngle=3.14159
    g2: ArcOfCircle CenterX=19 CenterY=19 CenterZ=0 NormalX=0 NormalY=0 NormalZ=1 AngleXU=0 Radius=16 StartAngle=1.5708 EndAngle=3.14159
    g3: LineSegment StartX=114 StartY=35 StartZ=0 EndX=19 EndY=35 EndZ=0
    g4: LineSegment StartX=5.21097e-06 StartY=3 StartZ=0 EndX=5.21097e-06 EndY=0 EndZ=0
    g5: LineSegment StartX=3 StartY=0 StartZ=0 EndX=5.21097e-06 EndY=0 EndZ=0
    g6: LineSegment StartX=3 StartY=19 StartZ=0 EndX=3 EndY=0 EndZ=0
    g7: LineSegment StartX=19 StartY=38 StartZ=0 EndX=124 EndY=38 EndZ=0
    g8: Circle CenterX=119 CenterY=35 CenterZ=0 NormalX=0 NormalY=0 NormalZ=1 AngleXU=0 Radius=1
    g9: Circle CenterX=121 CenterY=35 CenterZ=0 NormalX=0 NormalY=0 NormalZ=1 AngleXU=0 Radius=1
    g10: Circle CenterX=121 CenterY=33 CenterZ=0 NormalX=0 NormalY=0 NormalZ=1 AngleXU=0 Radius=1
    g11: BSplineCurve PolesCount=3 KnotsCount=2 Degree=2 IsPeriodic=0
    g12: GeomPoint X=119 Y=35 Z=0
    g13: GeomPoint X=121 Y=33 Z=0
    g14: LineSegment StartX=119 StartY=35 StartZ=0 EndX=114 EndY=35 EndZ=0
    g15: ArcOfCircle CenterX=105 CenterY=19 CenterZ=0 NormalX=0 NormalY=0 NormalZ=1 AngleXU=0 Radius=16 StartAngle=5.60905 EndAngle=6.28319
    g16: LineSegment StartX=121 StartY=33 StartZ=0 EndX=121 EndY=19 EndZ=0
    g17: LineSegment StartX=117.5 StartY=9.01251 StartZ=0 EndX=121.163 EndY=9.0125 EndZ=0
    g18: ArcOfCircle CenterX=105 CenterY=19 CenterZ=0 NormalX=0 NormalY=0 NormalZ=1 AngleXU=0 Radius=20.6155 StartAngle=5.7297 EndAngle=6.28319
    g19: LineSegment StartX=121.163 StartY=9.0125 StartZ=0 EndX=122.538 EndY=8.16329 EndZ=0
    g20: LineSegment StartX=124 StartY=38 StartZ=0 EndX=125.616 EndY=38 EndZ=0
    g21: LineSegment StartX=125.616 StartY=19 StartZ=0 EndX=125.616 EndY=38 EndZ=0
  constraints (49):
    c: Vertical(g0)
    c: Block(g0)
    c: Coincident(g1,g0)
    c: Block(g1)
    c: Coincident(g2,g1)
    c: Block(g2)
    c: Coincident(g3,g2)
    c: Horizontal(g3)
    c: Tangent(g3,g2)
    c: Coincident(g4,g0)
    c: Distance(g4) = 3
    c: Vertical(g4)
    c: Coincident(g5,g4)
    c: Horizontal(g5)
    c: Coincident(g6,g2)
    c: Coincident(g6,g5)
    c: Vertical(g6)
    c: Horizontal(g7)
    c: Distance(g7) = 105
    c: Coincident(g7,g1)
    c: Block(g3)
    c: Weight(g8) = 1
    c: Equal(g8,g9)
    c: Equal(g8,g10)
    c: InternalAlignment(g8,g11)
    c: InternalAlignment(g9,g11)
    c: InternalAlignment(g10,g11)
    c: InternalAlignment(g12,g11)
    c: InternalAlignment(g13,g11)
    c: Block(g11)
    c: Coincident(g14,g11)
    c: Coincident(g14,g3)
    c: Horizontal(g14)
    c: Block(g15)
    c: Coincident(g16,g11)
    c: Coincident(g16,g15)
    c: Vertical(g16)
    c: Distance(g16) = 14
    c: Coincident(g17,g15)
    c: Block(g18)
    c: Coincident(g19,g18)
    c: Coincident(g20,g7)
    c: Horizontal(g20)
    c: Vertical(g21)
    c: Coincident(g20,g21)
    c: Block(g20)
    c: Block(g21)
    c: Block(g19)
    c: Block(g17)
FEATURE [Part::Box] Box026  label="removeToCreteHoleForPlugHousing032"
  AttacherType = Attacher::AttachEngine3D
  Height = 28.6
  Length = 10
  Placement = pos=(-2,0,21.7) rot=(0,0,1;0rad)
  Width = 19
FEATURE [Part::Feature] Face109 .. Face112  x4 (patterned run collapsed; names and placements below)
  shape: bbox 3.5 x 17.8 x 2e-07 mm, 1 faces, 0 solids (baked)
FEATURE [Part::Revolution] Revolve117  label="removeToCreateScrewAndThreadedInsertHole045"
  Angle = 360
  Axis = (0,1,0)
  Base = (0,0,0)
  FaceMakerClass = Part::FaceMakerBullseye
  Placement = pos=(62.3,30.3,19.7) rot=(0,0,1;0rad)
  Solid = false
  Source = -> Face109
  Symmetric = false
FEATURE [Part::Revolution] Revolve118  label="removeToCreateScrewAndThreadedInsertHole046"
  Angle = 360
  Axis = (0,1,0)
  Base = (0,0,0)
  FaceMakerClass = Part::FaceMakerBullseye
  Placement = pos=(62.3,30.3,51.7) rot=(0,0,1;0rad)
  Solid = false
  Source = -> Face110
  Symmetric = false
FEATURE [Part::Revolution] Revolve119  label="removeToCreateScrewAndThreadedInsertHole047"
  Angle = 360
  Axis = (0,1,0)
  Base = (0,0,0)
  FaceMakerClass = Part::FaceMakerBullseye
  Placement = pos=(30.3,30.3,19.7) rot=(0,0,1;0rad)
  Solid = false
  Source = -> Face111
  Symmetric = false
FEATURE [Part::Revolution] Revolve120  label="removeToCreateScrewAndThreadedInsertHole048"
  Angle = 360
  Axis = (0,1,0)
  Base = (0,0,0)
  FaceMakerClass = Part::FaceMakerBullseye
  Placement = pos=(30.3,30.3,51.7) rot=(0,0,1;0rad)
  Solid = false
  Source = -> Face112
  Symmetric = false
FEATURE [Part::MultiFuse] Fusion087  label="createThreadedInsertHolesForFan005"
  Shapes = -> [Revolve117,Revolve118,Revolve119,Revolve120]
FEATURE [Part::Extrusion] Extrude047
  Base = -> Sketch056
  Dir = (0,0,1)
  DirMode = 2
  FaceMakerClass = Part::FaceMakerBullseye
  LengthFwd = 72
  LengthRev = 0
  Solid = true
  Symmetric = false
FEATURE [Part::Fillet] Fillet039  label="top019"
  Base = -> Extrude047
  Edges = 1 edges r=2: [Edge35]
FEATURE [Sketcher::SketchObject] Sketch057
  FullyConstrained = false
  Placement = pos=(0,0,0) rot=(1,0,0;1.5708rad)
  sketch-geometry (24):
    g0: ArcOfCircle CenterX=-4 CenterY=-10.5 CenterZ=0 NormalX=0 NormalY=0 NormalZ=1 AngleXU=0 Radius=1.5 StartAngle=6e-16 EndAngle=3.14159
    g1: ArcOfCircle CenterX=-34.2 CenterY=-10.5 CenterZ=0 NormalX=0 NormalY=0 NormalZ=1 AngleXU=0 Radius=1.5 StartAngle=0 EndAngle=3.14159
    g2: ArcOfCircle CenterX=-34.2 CenterY=-27.7 CenterZ=0 NormalX=0 NormalY=0 NormalZ=1 AngleXU=0 Radius=1.5 StartAngle=3.14159 EndAngle=6.28319
    g3: ArcOfCircle CenterX=-4 CenterY=-27.7 CenterZ=0 NormalX=0 NormalY=0 NormalZ=1 AngleXU=0 Radius=1.5 StartAngle=3.1416 EndAngle=6.28319
    g4: ArcOfCircle CenterX=-10 CenterY=-4.3 CenterZ=0 NormalX=0 NormalY=0 NormalZ=1 AngleXU=0 Radius=1.5 StartAngle=2e-16 EndAngle=3.14159
    g5: ArcOfCircle CenterX=-16.1 CenterY=-1.8 CenterZ=0 NormalX=0 NormalY=0 NormalZ=1 AngleXU=0 Radius=1.5 StartAngle=5e-16 EndAngle=3.14159
    g6: ArcOfCircle CenterX=-22.1 CenterY=-1.8 CenterZ=0 NormalX=0 NormalY=0 NormalZ=1 AngleXU=0 Radius=1.5 StartAngle=5e-16 EndAngle=3.14159
    g7: ArcOfCircle CenterX=-28.2 CenterY=-4.3 CenterZ=0 NormalX=0 NormalY=0 NormalZ=1 AngleXU=0 Radius=1.5 StartAngle=2e-16 EndAngle=3.14159
    g8: ArcOfCircle CenterX=-10 CenterY=-33.9 CenterZ=0 NormalX=0 NormalY=0 NormalZ=1 AngleXU=0 Radius=1.5 StartAngle=3.14159 EndAngle=6.28319
    g9: ArcOfCircle CenterX=-16.1 CenterY=-36.4 CenterZ=0 NormalX=0 NormalY=0 NormalZ=1 AngleXU=0 Radius=1.5 StartAngle=3.14159 EndAngle=6.28319
    g10: ArcOfCircle CenterX=-22.1 CenterY=-36.4 CenterZ=0 NormalX=0 NormalY=0 NormalZ=1 AngleXU=0 Radius=1.5 StartAngle=3.14159 EndAngle=6.28319
    g11: ArcOfCircle CenterX=-28.2 CenterY=-33.9 CenterZ=0 NormalX=0 NormalY=0 NormalZ=1 AngleXU=0 Radius=1.5 StartAngle=3.14159 EndAngle=6.28319
    g12: LineSegment StartX=-35.7 StartY=-10.5 StartZ=0 EndX=-35.7 EndY=-27.7 EndZ=0
    g13: LineSegment StartX=-32.7 StartY=-10.5 StartZ=0 EndX=-32.7 EndY=-27.7 EndZ=0
    g14: LineSegment StartX=-29.7 StartY=-33.9 StartZ=0 EndX=-29.7 EndY=-4.3 EndZ=0
    g15: LineSegment StartX=-26.7 StartY=-33.9 StartZ=0 EndX=-26.7 EndY=-4.3 EndZ=0
    g16: LineSegment StartX=-2.5 StartY=-10.5 StartZ=0 EndX=-2.5 EndY=-27.7 EndZ=0
    g17: LineSegment StartX=-8.5 StartY=-4.3 StartZ=0 EndX=-8.5 EndY=-33.9 EndZ=0
    g18: LineSegment StartX=-5.5 StartY=-10.5 StartZ=0 EndX=-5.5 EndY=-27.7 EndZ=0
    g19: LineSegment StartX=-11.5 StartY=-4.3 StartZ=0 EndX=-11.5 EndY=-33.9 EndZ=0
    g20: LineSegment StartX=-14.6 StartY=-1.8 StartZ=0 EndX=-14.6 EndY=-36.4 EndZ=0
    g21: LineSegment StartX=-17.6 StartY=-1.8 StartZ=0 EndX=-17.6 EndY=-36.4 EndZ=0
    g22: LineSegment StartX=-20.6 StartY=-36.4 StartZ=0 EndX=-20.6 EndY=-1.8 EndZ=0
    g23: LineSegment StartX=-23.6 StartY=-1.8 StartZ=0 EndX=-23.6 EndY=-36.4 EndZ=0
  constraints (48):
    c: Block(g0)
    c: Block(g1)
    c: Block(g2)
    c: Block(g3)
    c: Block(g4)
    c: Block(g5)
    c: Block(g6)
    c: Block(g7)
    c: Block(g8)
    c: Block(g9)
    c: Block(g10)
    c: Block(g11)
    c: Coincident(g12,g1)
    c: Coincident(g12,g2)
    c: Vertical(g12)
    c: Coincident(g13,g1)
    c: Coincident(g13,g2)
    c: Vertical(g13)
    c: Coincident(g14,g11)
    c: Coincident(g14,g7)
    c: Vertical(g14)
    c: Coincident(g15,g11)
    c: Coincident(g15,g7)
    c: Vertical(g15)
    c: Coincident(g16,g0)
    c: Coincident(g16,g3)
    c: Vertical(g16)
    c: Coincident(g17,g4)
    c: Coincident(g17,g8)
    c: Vertical(g17)
    c: Coincident(g18,g0)
    c: Coincident(g18,g3)
    c: Vertical(g18)
    c: Coincident(g19,g4)
    c: Coincident(g19,g8)
    c: Vertical(g19)
    c: Coincident(g20,g5)
    c: Coincident(g20,g9)
    c: Vertical(g20)
    c: Coincident(g21,g5)
    c: Coincident(g21,g9)
    c: Vertical(g21)
    c: Coincident(g22,g10)
    c: Coincident(g22,g6)
    c: Vertical(g22)
    c: Coincident(g23,g6)
    c: Coincident(g23,g10)
    c: Vertical(g23)
FEATURE [Part::Extrusion] Extrude048  label="removeToCreateFanGrillHoles004"
  Base = -> Sketch057
  Dir = (0,-1,6e-16)
  DirMode = 2
  FaceMakerClass = Part::FaceMakerBullseye
  LengthFwd = 10
  LengthRev = 0
  Placement = pos=(65.4,44,54.82) rot=(0,0,1;0rad)
  Solid = true
  Symmetric = false
FEATURE [Part::Cut] Cut040  label="top021"
  Base = -> Fillet039
  Tool = -> Extrude048
FEATURE [Part::Cylinder] Cylinder041  label="removeToCreteHoleForPlugHousing034"
  Angle = 360
  AttacherType = Attacher::AttachEngine3D
  Height = 20
  Placement = pos=(-2,19,36) rot=(0,1,0;1.5708rad)
  Radius = 14.3
FEATURE [Part::MultiFuse] Fusion089  label="removeToCreteHoleForPlugHousing035"
  Shapes = -> [Box026,Cylinder041]
FEATURE [Part::Cylinder] Cylinder042
  Angle = 360
  AttacherType = Attacher::AttachEngine3D
  Height = 20
  Placement = pos=(0,0,36.15) rot=(0,0,1;0rad)
  Radius = 14.3
FEATURE [Part::Cylinder] Cylinder043
  Angle = 360
  AttacherType = Attacher::AttachEngine3D
  Height = 10
  Placement = pos=(0,0,36.15) rot=(0,0,1;0rad)
  Radius = 4
FEATURE [Part::Box] Box027  label="removeToCreteHoleForPlugHousing036"
  AttacherType = Attacher::AttachEngine3D
  Height = 28.6
  Length = 20
  Placement = pos=(106.15,0,21.7) rot=(0,0,1;0rad)
  Width = 19
FEATURE [Part::Cut] Cut041  label="top022"
  Base = -> Cut040
  Tool = -> Fusion087
FEATURE [Part::Cut] Cut039  label="top020"
  Base = -> Cut041
  Tool = -> Fusion089
FEATURE [Part::MultiFuse] Fusion090  label="removeToCreteHoleForPlugHousing037"
  Placement = pos=(70,19,36) rot=(0,1,0;1.5708rad)
  Shapes = -> [Cylinder042,Cylinder043]
FEATURE [Part::MultiFuse] Fusion088  label="removeToCreteHoleForPlugHousing033"
  Shapes = -> [Box027,Fusion090]
FEATURE [Part::Cut] Cut042  label="removeToCreteHoleForPlugHousing038"
  Base = -> Cut039
  Tool = -> Fusion088
FEATURE [Part::MultiFuse] Fusion091  label="removeFromTop"
  Shapes = -> [Fillet038,Fusion085,Fusion084,Fusion083,Extrude045]
FEATURE [Part::Cut] Cut043  label="REAL TOP ====="
  Base = -> Fillet036
  Tool = -> Fusion091
FEATURE [Part::MultiFuse] Fusion092  label="caseScrewPillarBracket016"
  Shapes = -> [Extrude030,Extrude031,Extrude032,Extrude033,Extrude034,Extrude035,Extrude036,Extrude037,Box013,Box014]
FEATURE [Sketcher::SketchObject] Sketch058  label="topSketch015"
  FullyConstrained = true
  sketch-geometry (20):
    g0: LineSegment StartX=5.21097e-06 StartY=3 StartZ=0 EndX=5.21097e-06 EndY=19 EndZ=0
    g1: ArcOfCircle CenterX=19 CenterY=19 CenterZ=0 NormalX=0 NormalY=0 NormalZ=1 AngleXU=0 Radius=19 StartAngle=1.5708 EndAngle=3.14159
    g2: ArcOfCircle CenterX=19 CenterY=19 CenterZ=0 NormalX=0 NormalY=0 NormalZ=1 AngleXU=0 Radius=16 StartAngle=1.5708 EndAngle=3.14159
    g3: LineSegment StartX=114 StartY=35 StartZ=0 EndX=19 EndY=35 EndZ=0
    g4: LineSegment StartX=5.21097e-06 StartY=3 StartZ=0 EndX=5.21097e-06 EndY=0 EndZ=0
    g5: LineSegment StartX=3 StartY=0 StartZ=0 EndX=5.21097e-06 EndY=0 EndZ=0
    g6: LineSegment StartX=3 StartY=19 StartZ=0 EndX=3 EndY=0 EndZ=0
    g7: LineSegment StartX=19 StartY=38 StartZ=0 EndX=124 EndY=38 EndZ=0
    g8: Circle CenterX=119 CenterY=35 CenterZ=0 NormalX=0 NormalY=0 NormalZ=1 AngleXU=0 Radius=1
    g9: Circle CenterX=121 CenterY=35 CenterZ=0 NormalX=0 NormalY=0 NormalZ=1 AngleXU=0 Radius=1
    g10: Circle CenterX=121 CenterY=33 CenterZ=0 NormalX=0 NormalY=0 NormalZ=1 AngleXU=0 Radius=1
    g11: BSplineCurve PolesCount=3 KnotsCount=2 Degree=2 IsPeriodic=0
    g12: GeomPoint X=119 Y=35 Z=0
    g13: GeomPoint X=121 Y=33 Z=0
    g14: LineSegment StartX=119 StartY=35 StartZ=0 EndX=114 EndY=35 EndZ=0
    g15: ArcOfCircle CenterX=105 CenterY=19 CenterZ=0 NormalX=0 NormalY=0 NormalZ=1 AngleXU=0 Radius=19 StartAngle=5.7297 EndAngle=6.28319
    g16: ArcOfCircle CenterX=105 CenterY=19 CenterZ=0 NormalX=0 NormalY=0 NormalZ=1 AngleXU=0 Radius=16 StartAngle=5.60905 EndAngle=6.28319
    g17: LineSegment StartX=121 StartY=33 StartZ=0 EndX=121 EndY=19 EndZ=0
    g18: LineSegment StartX=124 StartY=38 StartZ=0 EndX=124 EndY=19 EndZ=0
    g19: LineSegment StartX=117.5 StartY=9.01251 StartZ=0 EndX=121.163 EndY=9.0125 EndZ=0
  constraints (46):
    c: Vertical(g0)
    c: Block(g0)
    c: Coincident(g1,g0)
    c: Block(g1)
    c: Coincident(g2,g1)
    c: Block(g2)
    c: Coincident(g3,g2)
    c: Horizontal(g3)
    c: Tangent(g3,g2)
    c: Coincident(g4,g0)
    c: Distance(g4) = 3
    c: Vertical(g4)
    c: Coincident(g5,g4)
    c: Horizontal(g5)
    c: Coincident(g6,g2)
    c: Coincident(g6,g5)
    c: Vertical(g6)
    c: Horizontal(g7)
    c: Distance(g7) = 105
    c: Coincident(g7,g1)
    c: Block(g3)
    c: Weight(g8) = 1
    c: Equal(g8,g9)
    c: Equal(g8,g10)
    c: InternalAlignment(g8,g11)
    c: InternalAlignment(g9,g11)
    c: InternalAlignment(g10,g11)
    c: InternalAlignment(g12,g11)
    c: InternalAlignment(g13,g11)
    c: Block(g11)
    c: Coincident(g14,g11)
    c: Coincident(g14,g3)
    c: Horizontal(g14)
    c: Block(g15)
    c: Coincident(g16,g15)
    c: Block(g16)
    c: Coincident(g17,g11)
    c: Coincident(g17,g16)
    c: Vertical(g17)
    c: Distance(g17) = 14
    c: Coincident(g18,g7)
    c: Coincident(g18,g15)
    c: Vertical(g18)
    c: Distance(g18) = 19
    c: Coincident(g19,g16)
    c: Coincident(g19,g15)
FEATURE [Part::Extrusion] Extrude049  label="top023"
  Base = -> Sketch058
  Dir = (0,0,1)
  DirMode = 2
  FaceMakerClass = Part::FaceMakerBullseye
  LengthFwd = 72
  LengthRev = 0
  Solid = true
  Symmetric = false
FEATURE [Sketcher::SketchObject] Sketch059
  FullyConstrained = true
  MapMode = 3
  Placement = pos=(0,0,0) rot=(1,0,0;1.5708rad)
  Support = -> [Extrude049]
  sketch-geometry (8):
    g0: Circle CenterX=80.351 CenterY=-67.6202 CenterZ=0 NormalX=0 NormalY=0 NormalZ=1 AngleXU=0 Radius=2
    g1: Circle CenterX=80.351 CenterY=-67.6202 CenterZ=0 NormalX=0 NormalY=0 NormalZ=1 AngleXU=0 Radius=3
    g2: Circle CenterX=80.351 CenterY=-4.92017 CenterZ=0 NormalX=0 NormalY=0 NormalZ=1 AngleXU=0 Radius=2
    g3: Circle CenterX=80.351 CenterY=-4.92017 CenterZ=0 NormalX=0 NormalY=0 NormalZ=1 AngleXU=0 Radius=3
    g4: Circle CenterX=23.851 CenterY=-4.92017 CenterZ=0 NormalX=0 NormalY=0 NormalZ=1 AngleXU=0 Radius=2
    g5: Circle CenterX=23.851 CenterY=-4.92017 CenterZ=0 NormalX=0 NormalY=0 NormalZ=1 AngleXU=0 Radius=3
    g6: Circle CenterX=23.851 CenterY=-67.6202 CenterZ=0 NormalX=0 NormalY=0 NormalZ=1 AngleXU=0 Radius=2
    g7: Circle CenterX=23.851 CenterY=-67.6202 CenterZ=0 NormalX=0 NormalY=0 NormalZ=1 AngleXU=0 Radius=3
  constraints (8):
    c: Block(g3)
    c: Block(g2)
    c: Block(g1)
    c: Block(g0)
    c: Block(g6)
    c: Block(g7)
    c: Block(g4)
    c: Block(g5)
FEATURE [Sketcher::SketchObject] Sketch060
  FullyConstrained = true
  MapMode = 3
  Placement = pos=(0,0,0) rot=(1,0,0;1.5708rad)
  Support = -> [Extrude049]
  sketch-geometry (8):
    g0: Circle CenterX=80.351 CenterY=-67.6202 CenterZ=0 NormalX=0 NormalY=0 NormalZ=1 AngleXU=0 Radius=3
    g1: Circle CenterX=80.351 CenterY=-4.92017 CenterZ=0 NormalX=0 NormalY=0 NormalZ=1 AngleXU=0 Radius=3
    g2: Circle CenterX=23.851 CenterY=-4.92017 CenterZ=0 NormalX=0 NormalY=0 NormalZ=1 AngleXU=0 Radius=3
    g3: Circle CenterX=23.851 CenterY=-67.6202 CenterZ=0 NormalX=0 NormalY=0 NormalZ=1 AngleXU=0 Radius=3
    g4: Circle CenterX=23.851 CenterY=-67.6202 CenterZ=0 NormalX=0 NormalY=0 NormalZ=1 AngleXU=0 Radius=5
    g5: Circle CenterX=80.351 CenterY=-67.6202 CenterZ=0 NormalX=0 NormalY=0 NormalZ=1 AngleXU=0 Radius=5
    g6: Circle CenterX=23.851 CenterY=-4.92017 CenterZ=0 NormalX=0 NormalY=0 NormalZ=1 AngleXU=0 Radius=5
    g7: Circle CenterX=80.351 CenterY=-4.92017 CenterZ=0 NormalX=0 NormalY=0 NormalZ=1 AngleXU=0 Radius=5
  constraints (8):
    c: Block(g1)
    c: Block(g0)
    c: Block(g3)
    c: Block(g2)
    c: Block(g5)
    c: Block(g4)
    c: Block(g6)
    c: Block(g7)
FEATURE [Sketcher::SketchObject] Sketch061
  FullyConstrained = true
  MapMode = 3
  Placement = pos=(0,0,0) rot=(1,0,0;1.5708rad)
  sketch-geometry (8):
    g0: Circle CenterX=80.351 CenterY=-67.6202 CenterZ=0 NormalX=0 NormalY=0 NormalZ=1 AngleXU=0 Radius=3
    g1: Circle CenterX=80.351 CenterY=-4.92017 CenterZ=0 NormalX=0 NormalY=0 NormalZ=1 AngleXU=0 Radius=3
    g2: Circle CenterX=23.851 CenterY=-4.92017 CenterZ=0 NormalX=0 NormalY=0 NormalZ=1 AngleXU=0 Radius=3
    g3: Circle CenterX=23.851 CenterY=-67.6202 CenterZ=0 NormalX=0 NormalY=0 NormalZ=1 AngleXU=0 Radius=3
    g4: Circle CenterX=23.851 CenterY=-67.6202 CenterZ=0 NormalX=0 NormalY=0 NormalZ=1 AngleXU=0 Radius=5
    g5: Circle CenterX=80.351 CenterY=-67.6202 CenterZ=0 NormalX=0 NormalY=0 NormalZ=1 AngleXU=0 Radius=5
    g6: Circle CenterX=23.851 CenterY=-4.92017 CenterZ=0 NormalX=0 NormalY=0 NormalZ=1 AngleXU=0 Radius=5
    g7: Circle CenterX=80.351 CenterY=-4.92017 CenterZ=0 NormalX=0 NormalY=0 NormalZ=1 AngleXU=0 Radius=5
  constraints (8):
    c: Block(g1)
    c: Block(g0)
    c: Block(g3)
    c: Block(g2)
    c: Block(g5)
    c: Block(g4)
    c: Block(g6)
    c: Block(g7)
FEATURE [Sketcher::SketchObject] Sketch062  label="topSketch016"
  FullyConstrained = true
  sketch-geometry (20):
    g0: LineSegment StartX=5.21097e-06 StartY=3 StartZ=0 EndX=5.21097e-06 EndY=19 EndZ=0
    g1: ArcOfCircle CenterX=19 CenterY=19 CenterZ=0 NormalX=0 NormalY=0 NormalZ=1 AngleXU=0 Radius=19 StartAngle=1.5708 EndAngle=3.14159
    g2: ArcOfCircle CenterX=19 CenterY=19 CenterZ=0 NormalX=0 NormalY=0 NormalZ=1 AngleXU=0 Radius=16 StartAngle=1.5708 EndAngle=3.14159
    g3: LineSegment StartX=114 StartY=35 StartZ=0 EndX=19 EndY=35 EndZ=0
    g4: LineSegment StartX=5.21097e-06 StartY=3 StartZ=0 EndX=5.21097e-06 EndY=0 EndZ=0
    g5: LineSegment StartX=3 StartY=0 StartZ=0 EndX=5.21097e-06 EndY=0 EndZ=0
    g6: LineSegment StartX=3 StartY=19 StartZ=0 EndX=3 EndY=0 EndZ=0
    g7: LineSegment StartX=19 StartY=38 StartZ=0 EndX=124 EndY=38 EndZ=0
    g8: Circle CenterX=119 CenterY=35 CenterZ=0 NormalX=0 NormalY=0 NormalZ=1 AngleXU=0 Radius=1
    g9: Circle CenterX=121 CenterY=35 CenterZ=0 NormalX=0 NormalY=0 NormalZ=1 AngleXU=0 Radius=1
    g10: Circle CenterX=121 CenterY=33 CenterZ=0 NormalX=0 NormalY=0 NormalZ=1 AngleXU=0 Radius=1
    g11: BSplineCurve PolesCount=3 KnotsCount=2 Degree=2 IsPeriodic=0
    g12: GeomPoint X=119 Y=35 Z=0
    g13: GeomPoint X=121 Y=33 Z=0
    g14: LineSegment StartX=119 StartY=35 StartZ=0 EndX=114 EndY=35 EndZ=0
    g15: ArcOfCircle CenterX=105 CenterY=19 CenterZ=0 NormalX=0 NormalY=0 NormalZ=1 AngleXU=0 Radius=19 StartAngle=5.7297 EndAngle=6.28319
    g16: ArcOfCircle CenterX=105 CenterY=19 CenterZ=0 NormalX=0 NormalY=0 NormalZ=1 AngleXU=0 Radius=16 StartAngle=5.60905 EndAngle=6.28319
    g17: LineSegment StartX=121 StartY=33 StartZ=0 EndX=121 EndY=19 EndZ=0
    g18: LineSegment StartX=124 StartY=38 StartZ=0 EndX=124 EndY=19 EndZ=0
    g19: LineSegment StartX=117.5 StartY=9.01251 StartZ=0 EndX=121.163 EndY=9.0125 EndZ=0
  constraints (46):
    c: Vertical(g0)
    c: Block(g0)
    c: Coincident(g1,g0)
    c: Block(g1)
    c: Coincident(g2,g1)
    c: Block(g2)
    c: Coincident(g3,g2)
    c: Horizontal(g3)
    c: Tangent(g3,g2)
    c: Coincident(g4,g0)
    c: Distance(g4) = 3
    c: Vertical(g4)
    c: Coincident(g5,g4)
    c: Horizontal(g5)
    c: Coincident(g6,g2)
    c: Coincident(g6,g5)
    c: Vertical(g6)
    c: Horizontal(g7)
    c: Distance(g7) = 105
    c: Coincident(g7,g1)
    c: Block(g3)
    c: Weight(g8) = 1
    c: Equal(g8,g9)
    c: Equal(g8,g10)
    c: InternalAlignment(g8,g11)
    c: InternalAlignment(g9,g11)
    c: InternalAlignment(g10,g11)
    c: InternalAlignment(g12,g11)
    c: InternalAlignment(g13,g11)
    c: Block(g11)
    c: Coincident(g14,g11)
    c: Coincident(g14,g3)
    c: Horizontal(g14)
    c: Block(g15)
    c: Coincident(g16,g15)
    c: Block(g16)
    c: Coincident(g17,g11)
    c: Coincident(g17,g16)
    c: Vertical(g17)
    c: Distance(g17) = 14
    c: Coincident(g18,g7)
    c: Coincident(g18,g15)
    c: Vertical(g18)
    c: Distance(g18) = 19
    c: Coincident(g19,g16)
    c: Coincident(g19,g15)
FEATURE [Part::Extrusion] Extrude053  label="top024"
  Base = -> Sketch062
  Dir = (0,0,1)
  DirMode = 2
  FaceMakerClass = Part::FaceMakerBullseye
  LengthFwd = 72
  LengthRev = 0
  Solid = true
  Symmetric = false
FEATURE [Sketcher::SketchObject] Sketch063
  FullyConstrained = true
  MapMode = 3
  Placement = pos=(0,0,0) rot=(1,0,0;1.5708rad)
  Support = -> [Extrude053]
  sketch-geometry (8):
    g0: Circle CenterX=80.351 CenterY=-67.6202 CenterZ=0 NormalX=0 NormalY=0 NormalZ=1 AngleXU=0 Radius=2
    g1: Circle CenterX=80.351 CenterY=-67.6202 CenterZ=0 NormalX=0 NormalY=0 NormalZ=1 AngleXU=0 Radius=3
    g2: Circle CenterX=80.351 CenterY=-4.92017 CenterZ=0 NormalX=0 NormalY=0 NormalZ=1 AngleXU=0 Radius=2
    g3: Circle CenterX=80.351 CenterY=-4.92017 CenterZ=0 NormalX=0 NormalY=0 NormalZ=1 AngleXU=0 Radius=3
    g4: Circle CenterX=23.851 CenterY=-4.92017 CenterZ=0 NormalX=0 NormalY=0 NormalZ=1 AngleXU=0 Radius=2
    g5: Circle CenterX=23.851 CenterY=-4.92017 CenterZ=0 NormalX=0 NormalY=0 NormalZ=1 AngleXU=0 Radius=3
    g6: Circle CenterX=23.851 CenterY=-67.6202 CenterZ=0 NormalX=0 NormalY=0 NormalZ=1 AngleXU=0 Radius=2
    g7: Circle CenterX=23.851 CenterY=-67.6202 CenterZ=0 NormalX=0 NormalY=0 NormalZ=1 AngleXU=0 Radius=3
  constraints (8):
    c: Block(g3)
    c: Block(g2)
    c: Block(g1)
    c: Block(g0)
    c: Block(g6)
    c: Block(g7)
    c: Block(g4)
    c: Block(g5)
FEATURE [Part::Extrusion] Extrude054
  Base = -> Sketch063
  Dir = (0,-1,2e-16)
  DirMode = 2
  FaceMakerClass = Part::FaceMakerBullseye
  LengthFwd = 6
  LengthRev = 0
  Placement = pos=(0,9,0) rot=(0,0,1;0rad)
  Solid = true
  Symmetric = false
FEATURE [Sketcher::SketchObject] Sketch064  label="topSketch017"
  FullyConstrained = true
  sketch-geometry (20):
    g0: LineSegment StartX=5.21097e-06 StartY=3 StartZ=0 EndX=5.21097e-06 EndY=19 EndZ=0
    g1: ArcOfCircle CenterX=19 CenterY=19 CenterZ=0 NormalX=0 NormalY=0 NormalZ=1 AngleXU=0 Radius=19 StartAngle=1.5708 EndAngle=3.14159
    g2: ArcOfCircle CenterX=19 CenterY=19 CenterZ=0 NormalX=0 NormalY=0 NormalZ=1 AngleXU=0 Radius=16 StartAngle=1.5708 EndAngle=3.14159
    g3: LineSegment StartX=114 StartY=35 StartZ=0 EndX=19 EndY=35 EndZ=0
    g4: LineSegment StartX=5.21097e-06 StartY=3 StartZ=0 EndX=5.21097e-06 EndY=0 EndZ=0
    g5: LineSegment StartX=3 StartY=0 StartZ=0 EndX=5.21097e-06 EndY=0 EndZ=0
    g6: LineSegment StartX=3 StartY=19 StartZ=0 EndX=3 EndY=0 EndZ=0
    g7: LineSegment StartX=19 StartY=38 StartZ=0 EndX=124 EndY=38 EndZ=0
    g8: Circle CenterX=119 CenterY=35 CenterZ=0 NormalX=0 NormalY=0 NormalZ=1 AngleXU=0 Radius=1
    g9: Circle CenterX=121 CenterY=35 CenterZ=0 NormalX=0 NormalY=0 NormalZ=1 AngleXU=0 Radius=1
    g10: Circle CenterX=121 CenterY=33 CenterZ=0 NormalX=0 NormalY=0 NormalZ=1 AngleXU=0 Radius=1
    g11: BSplineCurve PolesCount=3 KnotsCount=2 Degree=2 IsPeriodic=0
    g12: GeomPoint X=119 Y=35 Z=0
    g13: GeomPoint X=121 Y=33 Z=0
    g14: LineSegment StartX=119 StartY=35 StartZ=0 EndX=114 EndY=35 EndZ=0
    g15: ArcOfCircle CenterX=105 CenterY=19 CenterZ=0 NormalX=0 NormalY=0 NormalZ=1 AngleXU=0 Radius=19 StartAngle=5.7297 EndAngle=6.28319
    g16: ArcOfCircle CenterX=105 CenterY=19 CenterZ=0 NormalX=0 NormalY=0 NormalZ=1 AngleXU=0 Radius=16 StartAngle=5.60905 EndAngle=6.28319
    g17: LineSegment StartX=121 StartY=33 StartZ=0 EndX=121 EndY=19 EndZ=0
    g18: LineSegment StartX=124 StartY=38 StartZ=0 EndX=124 EndY=19 EndZ=0
    g19: LineSegment StartX=117.5 StartY=9.01251 StartZ=0 EndX=121.163 EndY=9.0125 EndZ=0
  constraints (46):
    c: Vertical(g0)
    c: Block(g0)
    c: Coincident(g1,g0)
    c: Block(g1)
    c: Coincident(g2,g1)
    c: Block(g2)
    c: Coincident(g3,g2)
    c: Horizontal(g3)
    c: Tangent(g3,g2)
    c: Coincident(g4,g0)
    c: Distance(g4) = 3
    c: Vertical(g4)
    c: Coincident(g5,g4)
    c: Horizontal(g5)
    c: Coincident(g6,g2)
    c: Coincident(g6,g5)
    c: Vertical(g6)
    c: Horizontal(g7)
    c: Distance(g7) = 105
    c: Coincident(g7,g1)
    c: Block(g3)
    c: Weight(g8) = 1
    c: Equal(g8,g9)
    c: Equal(g8,g10)
    c: InternalAlignment(g8,g11)
    c: InternalAlignment(g9,g11)
    c: InternalAlignment(g10,g11)
    c: InternalAlignment(g12,g11)
    c: InternalAlignment(g13,g11)
    c: Block(g11)
    c: Coincident(g14,g11)
    c: Coincident(g14,g3)
    c: Horizontal(g14)
    c: Block(g15)
    c: Coincident(g16,g15)
    c: Block(g16)
    c: Coincident(g17,g11)
    c: Coincident(g17,g16)
    c: Vertical(g17)
    c: Distance(g17) = 14
    c: Coincident(g18,g7)
    c: Coincident(g18,g15)
    c: Vertical(g18)
    c: Distance(g18) = 19
    c: Coincident(g19,g16)
    c: Coincident(g19,g15)
FEATURE [Sketcher::SketchObject] Sketch065
  FullyConstrained = true
  MapMode = 3
  Placement = pos=(0,0,0) rot=(1,0,0;1.5708rad)
  sketch-geometry (8):
    g0: Circle CenterX=80.351 CenterY=-67.6202 CenterZ=0 NormalX=0 NormalY=0 NormalZ=1 AngleXU=0 Radius=3
    g1: Circle CenterX=80.351 CenterY=-4.92017 CenterZ=0 NormalX=0 NormalY=0 NormalZ=1 AngleXU=0 Radius=3
    g2: Circle CenterX=23.851 CenterY=-4.92017 CenterZ=0 NormalX=0 NormalY=0 NormalZ=1 AngleXU=0 Radius=3
    g3: Circle CenterX=23.851 CenterY=-67.6202 CenterZ=0 NormalX=0 NormalY=0 NormalZ=1 AngleXU=0 Radius=3
    g4: Circle CenterX=23.851 CenterY=-67.6202 CenterZ=0 NormalX=0 NormalY=0 NormalZ=1 AngleXU=0 Radius=5
    g5: Circle CenterX=80.351 CenterY=-67.6202 CenterZ=0 NormalX=0 NormalY=0 NormalZ=1 AngleXU=0 Radius=5
    g6: Circle CenterX=23.851 CenterY=-4.92017 CenterZ=0 NormalX=0 NormalY=0 NormalZ=1 AngleXU=0 Radius=5
    g7: Circle CenterX=80.351 CenterY=-4.92017 CenterZ=0 NormalX=0 NormalY=0 NormalZ=1 AngleXU=0 Radius=5
  constraints (8):
    c: Block(g1)
    c: Block(g0)
    c: Block(g3)
    c: Block(g2)
    c: Block(g5)
    c: Block(g4)
    c: Block(g6)
    c: Block(g7)
FEATURE [Part::Extrusion] Extrude056
  Base = -> Sketch065
  Dir = (0,-1,2e-16)
  DirMode = 2
  FaceMakerClass = Part::FaceMakerBullseye
  LengthFwd = 2
  LengthRev = 0
  Solid = true
  Symmetric = false
FEATURE [Part::Extrusion] Extrude057  label="top025"
  Base = -> Sketch064
  Dir = (0,0,1)
  DirMode = 2
  FaceMakerClass = Part::FaceMakerBullseye
  LengthFwd = 72
  LengthRev = 0
  Solid = true
  Symmetric = false
FEATURE [Sketcher::SketchObject] Sketch066
  FullyConstrained = true
  MapMode = 3
  Placement = pos=(0,0,0) rot=(1,0,0;1.5708rad)
  Support = -> [Extrude057]
  sketch-geometry (8):
    g0: Circle CenterX=80.351 CenterY=-67.6202 CenterZ=0 NormalX=0 NormalY=0 NormalZ=1 AngleXU=0 Radius=3
    g1: Circle CenterX=80.351 CenterY=-4.92017 CenterZ=0 NormalX=0 NormalY=0 NormalZ=1 AngleXU=0 Radius=3
    g2: Circle CenterX=23.851 CenterY=-4.92017 CenterZ=0 NormalX=0 NormalY=0 NormalZ=1 AngleXU=0 Radius=3
    g3: Circle CenterX=23.851 CenterY=-67.6202 CenterZ=0 NormalX=0 NormalY=0 NormalZ=1 AngleXU=0 Radius=3
    g4: Circle CenterX=23.851 CenterY=-67.6202 CenterZ=0 NormalX=0 NormalY=0 NormalZ=1 AngleXU=0 Radius=5
    g5: Circle CenterX=80.351 CenterY=-67.6202 CenterZ=0 NormalX=0 NormalY=0 NormalZ=1 AngleXU=0 Radius=5
    g6: Circle CenterX=23.851 CenterY=-4.92017 CenterZ=0 NormalX=0 NormalY=0 NormalZ=1 AngleXU=0 Radius=5
    g7: Circle CenterX=80.351 CenterY=-4.92017 CenterZ=0 NormalX=0 NormalY=0 NormalZ=1 AngleXU=0 Radius=5
  constraints (8):
    c: Block(g1)
    c: Block(g0)
    c: Block(g3)
    c: Block(g2)
    c: Block(g5)
    c: Block(g4)
    c: Block(g6)
    c: Block(g7)
FEATURE [Part::Extrusion] Extrude055
  Base = -> Sketch066
  Dir = (0,-1,2e-16)
  DirMode = 2
  FaceMakerClass = Part::FaceMakerBullseye
  LengthFwd = 2
  LengthRev = 0
  Solid = true
  Symmetric = false
FEATURE [Part::Fillet] Fillet041
  Base = -> Extrude056
  Edges = 4 edges r=1.99: [Edge6,Edge12,Edge18,Edge24]
FEATURE [Part::Cut] Cut045
  Base = -> Extrude055
  Placement = pos=(0,6,0) rot=(0,0,1;0rad)
  Tool = -> Fillet041
FEATURE [Part::MultiFuse] Fusion095  label="pcbScrewPillars"
  Placement = pos=(-3.2,-1,72.3) rot=(0,0,1;0rad)
  Shapes = -> [Cut045,Extrude054]
FEATURE [Part::Feature] Face113
  shape: bbox 3.2 x 1.5 x 2e-07 mm, 1 faces, 0 solids (baked)
FEATURE [Part::Revolution] Revolve121  label="backCaseScrewRetainer002"
  Angle = 360
  Axis = (0,1,0)
  Base = (0,0,0)
  FaceMakerClass = Part::FaceMakerBullseye
  Placement = pos=(12.5,3,62) rot=(0,0,1;0rad)
  Solid = false
  Source = -> Face113
  Symmetric = false
FEATURE [Part::Feature] Face114
  shape: bbox 3.2 x 1.5 x 2e-07 mm, 1 faces, 0 solids (baked)
FEATURE [Part::Feature] Face115
  shape: bbox 3.2 x 1.5 x 2e-07 mm, 1 faces, 0 solids (baked)
FEATURE [Part::Feature] Face116
  shape: bbox 3.2 x 1.5 x 2e-07 mm, 1 faces, 0 solids (baked)
FEATURE [Part::Revolution] Revolve122  label="frontCaseScrewRetainer004"
  Angle = 360
  Axis = (0,1,0)
  Base = (0,0,0)
  FaceMakerClass = Part::FaceMakerBullseye
  Placement = pos=(89.5,3,68.5) rot=(0,0,1;0rad)
  Solid = false
  Source = -> Face115
  Symmetric = false
FEATURE [Part::Revolution] Revolve123  label="frontCaseScrewRetainer005"
  Angle = 360
  Axis = (0,1,0)
  Base = (0,0,0)
  FaceMakerClass = Part::FaceMakerBullseye
  Placement = pos=(89.5,3,3.5) rot=(0,0,1;0rad)
  Solid = false
  Source = -> Face116
  Symmetric = false
FEATURE [Part::Revolution] Revolve124  label="backCaseScrewRetainer003"
  Angle = 360
  Axis = (0,1,0)
  Base = (0,0,0)
  FaceMakerClass = Part::FaceMakerBullseye
  Placement = pos=(12.5,3,10) rot=(0,0,1;0rad)
  Solid = false
  Source = -> Face114
  Symmetric = false
FEATURE [Part::Feature] Face117
  shape: bbox 3.6 x 3.2 x 2e-07 mm, 1 faces, 0 solids (baked)
FEATURE [Part::Revolution] Revolve125  label="moreFrontCaseScrewRetainer004"
  Angle = 360
  Axis = (0,1,0)
  Base = (0,0,0)
  FaceMakerClass = Part::FaceMakerBullseye
  Placement = pos=(109.5,4.5,68.5) rot=(0,0,1;0rad)
  Solid = false
  Source = -> Face117
  Symmetric = false
FEATURE [Part::Feature] Face118
  shape: bbox 3.6 x 3.2 x 2e-07 mm, 1 faces, 0 solids (baked)
FEATURE [Part::Revolution] Revolve126  label="moreFrontCaseScrewRetainer005"
  Angle = 360
  Axis = (0,1,0)
  Base = (0,0,0)
  FaceMakerClass = Part::FaceMakerBullseye
  Placement = pos=(109.5,4.5,3.5) rot=(0,0,1;0rad)
  Solid = false
  Source = -> Face118
  Symmetric = false
FEATURE [Part::MultiFuse] Fusion096  label="screwRetainers001"
  Shapes = -> [Revolve126,Revolve125,Revolve124,Revolve123,Revolve122,Revolve121]
FEATURE [Part::Feature] Face119
  shape: bbox 10 x 16.5 x 2e-07 mm, 1 faces, 0 solids (baked)
FEATURE [Part::Revolution] Revolve130  label="plugHousing050"
  Angle = 360
  Axis = (0,1,0)
  Base = (0,0,0)
  FaceMakerClass = Part::FaceMakerBullseye
  Placement = pos=(0,0,36.15) rot=(0,0,1;0rad)
  Solid = false
  Source = -> Face119
  Symmetric = false
FEATURE [Part::Feature] Face120
  shape: bbox 10 x 16.5 x 2e-07 mm, 1 faces, 0 solids (baked)
FEATURE [Part::Feature] Face121
  shape: bbox 10 x 16.5 x 2e-07 mm, 1 faces, 0 solids (baked)
FEATURE [Part::Revolution] Revolve127  label="plugHousing047"
  Angle = 360
  Axis = (0,1,0)
  Base = (0,0,0)
  FaceMakerClass = Part::FaceMakerBullseye
  Placement = pos=(0,0,36.15) rot=(0,0,1;0rad)
  Solid = false
  Source = -> Face121
  Symmetric = false
FEATURE [Part::Feature] Face122
  shape: bbox 10 x 16.5 x 2e-07 mm, 1 faces, 0 solids (baked)
FEATURE [Part::Feature] Face123
  shape: bbox 10 x 16.5 x 2e-07 mm, 1 faces, 0 solids (baked)
FEATURE [Part::Revolution] Revolve128  label="plugHousing048"
  Angle = 360
  Axis = (0,1,0)
  Base = (0,0,0)
  FaceMakerClass = Part::FaceMakerBullseye
  Placement = pos=(0,0,36.15) rot=(0,0,1;0rad)
  Solid = false
  Source = -> Face123
  Symmetric = false
FEATURE [Part::MultiFuse] Fusion100  label="plugHousing054"
  Placement = pos=(0,0,0) rot=(0,0,1;1.5708rad)
  Shapes = -> [Revolve130,Revolve128]
FEATURE [Part::Feature] Face124
  shape: bbox 10 x 16.5 x 2e-07 mm, 1 faces, 0 solids (baked)
FEATURE [Part::Feature] Face125
  shape: bbox 10 x 16.5 x 2e-07 mm, 1 faces, 0 solids (baked)
FEATURE [Part::Revolution] Revolve129  label="plugHousing049"
  Angle = 360
  Axis = (0,1,0)
  Base = (0,0,0)
  FaceMakerClass = Part::FaceMakerBullseye
  Placement = pos=(0,0,36.15) rot=(0,0,1;0rad)
  Solid = false
  Source = -> Face125
  Symmetric = false
FEATURE [Part::Feature] Face126
  shape: bbox 10 x 16.5 x 2e-07 mm, 1 faces, 0 solids (baked)
FEATURE [Part::Revolution] Revolve131  label="plugHousing058"
  Angle = 360
  Axis = (0,1,0)
  Base = (0,0,0)
  FaceMakerClass = Part::FaceMakerBullseye
  Placement = pos=(0,0,36.15) rot=(0,0,1;0rad)
  Solid = false
  Source = -> Face120
  Symmetric = false
FEATURE [Part::MultiFuse] Fusion099  label="plugHousing053"
  Placement = pos=(0,0,0) rot=(0,0,1;1.5708rad)
  Shapes = -> [Revolve127,Revolve131]
FEATURE [Part::MultiFuse] Fusion102  label="plugHousing056"
  Placement = pos=(0,19,0) rot=(0,0,1;3.14159rad)
  Shapes = -> [Fusion100,Fusion099]
FEATURE [Part::Revolution] Revolve132  label="plugHousing059"
  Angle = 360
  Axis = (0,1,0)
  Base = (0,0,0)
  FaceMakerClass = Part::FaceMakerBullseye
  Placement = pos=(0,0,36.15) rot=(0,0,1;0rad)
  Solid = false
  Source = -> Face126
  Symmetric = false
FEATURE [Part::Revolution] Revolve133  label="plugHousing060"
  Angle = 360
  Axis = (0,1,0)
  Base = (0,0,0)
  FaceMakerClass = Part::FaceMakerBullseye
  Placement = pos=(0,0,36.15) rot=(0,0,1;0rad)
  Solid = false
  Source = -> Face122
  Symmetric = false
FEATURE [Part::MultiFuse] Fusion097  label="plugHousing051"
  Placement = pos=(0,0,0) rot=(0,0,1;1.5708rad)
  Shapes = -> [Revolve133,Revolve132]
FEATURE [Part::Revolution] Revolve134  label="plugHousing061"
  Angle = 360
  Axis = (0,1,0)
  Base = (0,0,0)
  FaceMakerClass = Part::FaceMakerBullseye
  Placement = pos=(0,0,36.15) rot=(0,0,1;0rad)
  Solid = false
  Source = -> Face124
  Symmetric = false
FEATURE [Part::MultiFuse] Fusion101  label="plugHousing055"
  Placement = pos=(0,0,0) rot=(0,0,1;1.5708rad)
  Shapes = -> [Revolve129,Revolve134]
FEATURE [Part::MultiFuse] Fusion098  label="plugHousing052"
  Placement = pos=(0,19,0) rot=(0,0,1;3.14159rad)
  Shapes = -> [Fusion097,Fusion101]
FEATURE [Part::MultiFuse] Fusion103  label="plugHousing057"
  Placement = pos=(122.621,0,-0.15) rot=(0,0,1;0rad)
  Shapes = -> [Fusion102,Fusion098]
FEATURE [Part::Box] Box028  label="Cube015"
  AttacherType = Attacher::AttachEngine3D
  Height = 28
  Length = 3
  Placement = pos=(110.7,19,22) rot=(0,0,1;0rad)
  Width = 15.7
FEATURE [Part::Cylinder] Cylinder044
  Angle = 360
  AttacherType = Attacher::AttachEngine3D
  Height = 20
  Placement = pos=(0,0,36.15) rot=(0,0,1;0rad)
  Radius = 10.3
FEATURE [Part::Cylinder] Cylinder045
  Angle = 360
  AttacherType = Attacher::AttachEngine3D
  Height = 10
  Placement = pos=(0,0,36.15) rot=(0,0,1;0rad)
  Radius = 4
FEATURE [Part::MultiFuse] Fusion104  label="removeToCreteHoleForPlugHousing040"
  Placement = pos=(70,19,36) rot=(0,1,0;1.5708rad)
  Shapes = -> [Cylinder044,Cylinder045]
FEATURE [Part::Cut] Cut046  label="plugHousingTab003"
  Base = -> Box028
  Tool = -> Fusion104
FEATURE [Part::MultiFuse] Fusion105  label="plugHousing062"
  Shapes = -> [Fusion103,Cut046]
FEATURE [Part::Fillet] Fillet042
  Base = -> Fusion105
  Edges = 1 edges r=2: [Edge25]
FEATURE [Part::Fillet] Fillet043  label="plugHousing063"
  Base = -> Fillet042
  Edges = 1 edges r=2: [Edge8]
  Placement = pos=(7,0,0) rot=(0,0,1;0rad)
FEATURE [Part::Feature] Face127
  shape: bbox 10 x 16.5 x 2e-07 mm, 1 faces, 0 solids (baked)
FEATURE [Part::Feature] Face128
  shape: bbox 10 x 16.5 x 2e-07 mm, 1 faces, 0 solids (baked)
FEATURE [Part::Revolution] Revolve137  label="plugHousing070"
  Angle = 360
  Axis = (0,1,0)
  Base = (0,0,0)
  FaceMakerClass = Part::FaceMakerBullseye
  Placement = pos=(0,0,36.15) rot=(0,0,1;0rad)
  Solid = false
  Source = -> Face127
  Symmetric = false
FEATURE [Part::Revolution] Revolve140  label="plugHousing073"
  Angle = 360
  Axis = (0,1,0)
  Base = (0,0,0)
  FaceMakerClass = Part::FaceMakerBullseye
  Placement = pos=(0,0,36.15) rot=(0,0,1;0rad)
  Solid = false
  Source = -> Face128
  Symmetric = false
FEATURE [Part::Feature] Face129
  shape: bbox 10 x 16.5 x 2e-07 mm, 1 faces, 0 solids (baked)
FEATURE [Part::Revolution] Revolve138  label="plugHousing071"
  Angle = 360
  Axis = (0,1,0)
  Base = (0,0,0)
  FaceMakerClass = Part::FaceMakerBullseye
  Placement = pos=(0,0,36.15) rot=(0,0,1;0rad)
  Solid = false
  Source = -> Face129
  Symmetric = false
FEATURE [Part::Feature] Face130
  shape: bbox 10 x 16.5 x 2e-07 mm, 1 faces, 0 solids (baked)
FEATURE [Part::Revolution] Revolve139  label="plugHousing072"
  Angle = 360
  Axis = (0,1,0)
  Base = (0,0,0)
  FaceMakerClass = Part::FaceMakerBullseye
  Placement = pos=(0,0,36.15) rot=(0,0,1;0rad)
  Solid = false
  Source = -> Face130
  Symmetric = false
FEATURE [Part::Feature] Face131
  shape: bbox 10 x 16.5 x 2e-07 mm, 1 faces, 0 solids (baked)
FEATURE [Part::Revolution] Revolve135  label="plugHousing068"
  Angle = 360
  Axis = (0,1,0)
  Base = (0,0,0)
  FaceMakerClass = Part::FaceMakerBullseye
  Placement = pos=(0,0,36.15) rot=(0,0,1;0rad)
  Solid = false
  Source = -> Face131
  Symmetric = false
FEATURE [Part::MultiFuse] Fusion112  label="plugHousing078"
  Placement = pos=(0,0,0) rot=(0,0,1;1.5708rad)
  Shapes = -> [Revolve135,Revolve139]
FEATURE [Part::Feature] Face132
  shape: bbox 10 x 16.5 x 2e-07 mm, 1 faces, 0 solids (baked)
FEATURE [Part::Revolution] Revolve141  label="plugHousing074"
  Angle = 360
  Axis = (0,1,0)
  Base = (0,0,0)
  FaceMakerClass = Part::FaceMakerBullseye
  Placement = pos=(0,0,36.15) rot=(0,0,1;0rad)
  Solid = false
  Source = -> Face132
  Symmetric = false
FEATURE [Part::MultiFuse] Fusion110  label="plugHousing076"
  Placement = pos=(0,0,0) rot=(0,0,1;1.5708rad)
  Shapes = -> [Revolve141,Revolve140]
FEATURE [Part::Feature] Face133
  shape: bbox 10 x 16.5 x 2e-07 mm, 1 faces, 0 solids (baked)
FEATURE [Part::Revolution] Revolve136  label="plugHousing069"
  Angle = 360
  Axis = (0,1,0)
  Base = (0,0,0)
  FaceMakerClass = Part::FaceMakerBullseye
  Placement = pos=(0,0,36.15) rot=(0,0,1;0rad)
  Solid = false
  Source = -> Face133
  Symmetric = false
FEATURE [Part::MultiFuse] Fusion106  label="plugHousing064"
  Placement = pos=(0,0,0) rot=(0,0,1;1.5708rad)
  Shapes = -> [Revolve138,Revolve136]
FEATURE [Part::MultiFuse] Fusion108  label="plugHousing066"
  Placement = pos=(0,19,0) rot=(0,0,1;3.14159rad)
  Shapes = -> [Fusion106,Fusion112]
FEATURE [Part::Feature] Face134
  shape: bbox 10 x 16.5 x 2e-07 mm, 1 faces, 0 solids (baked)
FEATURE [Part::Revolution] Revolve142  label="plugHousing075"
  Angle = 360
  Axis = (0,1,0)
  Base = (0,0,0)
  FaceMakerClass = Part::FaceMakerBullseye
  Placement = pos=(0,0,36.15) rot=(0,0,1;0rad)
  Solid = false
  Source = -> Face134
  Symmetric = false
FEATURE [Part::MultiFuse] Fusion107  label="plugHousing065"
  Placement = pos=(0,0,0) rot=(0,0,1;1.5708rad)
  Shapes = -> [Revolve137,Revolve142]
FEATURE [Part::MultiFuse] Fusion111  label="plugHousing077"
  Placement = pos=(0,19,0) rot=(0,0,1;3.14159rad)
  Shapes = -> [Fusion110,Fusion107]
FEATURE [Part::MultiFuse] Fusion109  label="plugHousing067"
  Placement = pos=(131.236,0,-0.15) rot=(0,0,1;0rad)
  Shapes = -> [Fusion108,Fusion111]
FEATURE [Part::MultiFuse] Fusion113  label="plugHousing079"
  Shapes = -> [Fillet043,Fusion109]
FEATURE [Part::Feature] Face135
  shape: bbox 3.5 x 17.8 x 2e-07 mm, 1 faces, 0 solids (baked)
FEATURE [Part::Revolution] Revolve143  label="removeToCreateScrewAndThreadedInsertHole049"
  Angle = 360
  Axis = (0,1,0)
  Base = (0,0,0)
  FaceMakerClass = Part::FaceMakerBullseye
  Placement = pos=(12.5,0,10) rot=(0,0,1;0rad)
  Solid = false
  Source = -> Face135
  Symmetric = false
FEATURE [Part::Feature] Face136
  shape: bbox 3.5 x 17.8 x 2e-07 mm, 1 faces, 0 solids (baked)
FEATURE [Part::Revolution] Revolve144  label="removeToCreateScrewAndThreadedInsertHole050"
  Angle = 360
  Axis = (0,1,0)
  Base = (0,0,0)
  FaceMakerClass = Part::FaceMakerBullseye
  Placement = pos=(12.5,0,62) rot=(0,0,1;0rad)
  Solid = false
  Source = -> Face136
  Symmetric = false
FEATURE [Part::Feature] Face137
  shape: bbox 3.5 x 17.8 x 2e-07 mm, 1 faces, 0 solids (baked)
FEATURE [Part::Revolution] Revolve145  label="removeToCreateScrewAndThreadedInsertHole051"
  Angle = 360
  Axis = (0,1,0)
  Base = (0,0,0)
  FaceMakerClass = Part::FaceMakerBullseye
  Placement = pos=(89.5,0,68.5) rot=(0,0,1;0rad)
  Solid = false
  Source = -> Face137
  Symmetric = false
FEATURE [Part::Feature] Face138
  shape: bbox 3.5 x 17.8 x 2e-07 mm, 1 faces, 0 solids (baked)
FEATURE [Part::Revolution] Revolve146  label="removeToCreateScrewAndThreadedInsertHole052"
  Angle = 360
  Axis = (0,1,0)
  Base = (0,0,0)
  FaceMakerClass = Part::FaceMakerBullseye
  Placement = pos=(89.5,0,3.5) rot=(0,0,1;0rad)
  Solid = false
  Source = -> Face138
  Symmetric = false
FEATURE [Part::Feature] Face139
  shape: bbox 3.5 x 17.8 x 2e-07 mm, 1 faces, 0 solids (baked)
FEATURE [Part::Revolution] Revolve147  label="removeToCreateScrewAndThreadedInsertHole053"
  Angle = 360
  Axis = (0,1,0)
  Base = (0,0,0)
  FaceMakerClass = Part::FaceMakerBullseye
  Placement = pos=(109.5,4.7,3.5) rot=(0,0,1;0rad)
  Solid = false
  Source = -> Face139
  Symmetric = false
FEATURE [Part::Feature] Face140
  shape: bbox 3.5 x 17.8 x 2e-07 mm, 1 faces, 0 solids (baked)
FEATURE [Part::Revolution] Revolve148  label="removeToCreateScrewAndThreadedInsertHole054"
  Angle = 360
  Axis = (0,1,0)
  Base = (0,0,0)
  FaceMakerClass = Part::FaceMakerBullseye
  Placement = pos=(109.5,4.7,68.5) rot=(0,0,1;0rad)
  Solid = false
  Source = -> Face140
  Symmetric = false
FEATURE [Part::MultiFuse] Fusion114  label="removeToCreateScrewAndThreadedInsertHole055"
  Shapes = -> [Revolve148,Revolve147,Revolve146,Revolve145,Revolve144,Revolve143]
FEATURE [Part::Cut] Cut047  label="casePillars004"
  Base = -> Cut037
  Tool = -> Fusion114
FEATURE [Part::Feature] Face141
  shape: bbox 3.5 x 17.8 x 2e-07 mm, 1 faces, 0 solids (baked)
FEATURE [Part::Feature] Face142
  shape: bbox 3.5 x 17.8 x 2e-07 mm, 1 faces, 0 solids (baked)
FEATURE [Part::Feature] Face143
  shape: bbox 3.5 x 17.8 x 2e-07 mm, 1 faces, 0 solids (baked)
FEATURE [Part::Revolution] Revolve149  label="removeToCreateScrewAndThreadedInsertHole057"
  Angle = 360
  Axis = (0,1,0)
  Base = (0,0,0)
  FaceMakerClass = Part::FaceMakerBullseye
  Placement = pos=(12.5,0,10) rot=(0,0,1;0rad)
  Solid = false
  Source = -> Face141
  Symmetric = false
FEATURE [Part::Feature] Face144
  shape: bbox 3.5 x 17.8 x 2e-07 mm, 1 faces, 0 solids (baked)
FEATURE [Part::Feature] Face145
  shape: bbox 3.5 x 17.8 x 2e-07 mm, 1 faces, 0 solids (baked)
FEATURE [Part::Feature] Face146
  shape: bbox 3.5 x 17.8 x 2e-07 mm, 1 faces, 0 solids (baked)
FEATURE [Part::Revolution] Revolve150  label="removeToCreateScrewAndThreadedInsertHole058"
  Angle = 360
  Axis = (0,1,0)
  Base = (0,0,0)
  FaceMakerClass = Part::FaceMakerBullseye
  Placement = pos=(12.5,0,62) rot=(0,0,1;0rad)
  Solid = false
  Source = -> Face146
  Symmetric = false
FEATURE [Part::Revolution] Revolve151  label="removeToCreateScrewAndThreadedInsertHole059"
  Angle = 360
  Axis = (0,1,0)
  Base = (0,0,0)
  FaceMakerClass = Part::FaceMakerBullseye
  Placement = pos=(89.5,0,68.5) rot=(0,0,1;0rad)
  Solid = false
  Source = -> Face143
  Symmetric = false
FEATURE [Part::Revolution] Revolve152  label="removeToCreateScrewAndThreadedInsertHole060"
  Angle = 360
  Axis = (0,1,0)
  Base = (0,0,0)
  FaceMakerClass = Part::FaceMakerBullseye
  Placement = pos=(89.5,0,3.5) rot=(0,0,1;0rad)
  Solid = false
  Source = -> Face142
  Symmetric = false
FEATURE [Part::Revolution] Revolve153  label="removeToCreateScrewAndThreadedInsertHole061"
  Angle = 360
  Axis = (0,1,0)
  Base = (0,0,0)
  FaceMakerClass = Part::FaceMakerBullseye
  Placement = pos=(109.5,4.7,3.5) rot=(0,0,1;0rad)
  Solid = false
  Source = -> Face145
  Symmetric = false
FEATURE [Part::Revolution] Revolve154  label="removeToCreateScrewAndThreadedInsertHole062"
  Angle = 360
  Axis = (0,1,0)
  Base = (0,0,0)
  FaceMakerClass = Part::FaceMakerBullseye
  Placement = pos=(109.5,4.7,68.5) rot=(0,0,1;0rad)
  Solid = false
  Source = -> Face144
  Symmetric = false
FEATURE [Part::MultiFuse] Fusion115  label="removeToCreateScrewAndThreadedInsertHole056"
  Shapes = -> [Revolve154,Revolve153,Revolve152,Revolve151,Revolve150,Revolve149]
FEATURE [Part::Feature] Face147
  shape: bbox 9.8 x 26.5 x 2e-07 mm, 1 faces, 0 solids (baked)
FEATURE [Part::Revolution] Revolve155
  Angle = 360
  Axis = (0,1,0)
  Base = (0,0,0)
  FaceMakerClass = Part::FaceMakerBullseye
  Placement = pos=(0,0,0) rot=(0,0,1;1.5708rad)
  Solid = false
  Source = -> Face147
  Symmetric = false
FEATURE [Part::Feature] Face148
  shape: bbox 9.8 x 26.5 x 2e-07 mm, 1 faces, 0 solids (baked)
FEATURE [Part::Revolution] Revolve156
  Angle = 360
  Axis = (0,1,0)
  Base = (0,0,0)
  FaceMakerClass = Part::FaceMakerBullseye
  Placement = pos=(0,0,0) rot=(0,0,1;1.5708rad)
  Solid = false
  Source = -> Face148
  Symmetric = false
FEATURE [Part::MultiFuse] Fusion116
  Placement = pos=(-18,19,36) rot=(0,0,1;0rad)
  Shapes = -> [Revolve156,Revolve155]
FEATURE [Part::Box] Box029  label="Cube016"
  AttacherType = Attacher::AttachEngine3D
  Height = 28
  Length = 3
  Placement = pos=(110.7,19,22) rot=(0,0,1;0rad)
  Width = 15.7
FEATURE [Part::Cylinder] Cylinder046
  Angle = 360
  AttacherType = Attacher::AttachEngine3D
  Height = 10
  Placement = pos=(0,0,36.15) rot=(0,0,1;0rad)
  Radius = 4
FEATURE [Part::Cylinder] Cylinder047
  Angle = 360
  AttacherType = Attacher::AttachEngine3D
  Height = 20
  Placement = pos=(0,0,36.15) rot=(0,0,1;0rad)
  Radius = 10.3
FEATURE [Part::MultiFuse] Fusion117  label="removeToCreteHoleForPlugHousing041"
  Placement = pos=(70,19,36) rot=(0,1,0;1.5708rad)
  Shapes = -> [Cylinder047,Cylinder046]
FEATURE [Part::Cut] Cut049  label="plugHousingTab004"
  Base = -> Box029
  Placement = pos=(-107.4,-14,0) rot=(0,0,1;0rad)
  Tool = -> Fusion117
FEATURE [Part::Box] Box030  label="Cube017"
  AttacherType = Attacher::AttachEngine3D
  Height = 28
  Length = 3
  Placement = pos=(110.7,19,22) rot=(0,0,1;0rad)
  Width = 15.7
FEATURE [Part::Cylinder] Cylinder048
  Angle = 360
  AttacherType = Attacher::AttachEngine3D
  Height = 10
  Placement = pos=(0,0,36.15) rot=(0,0,1;0rad)
  Radius = 4
FEATURE [Part::Cylinder] Cylinder049
  Angle = 360
  AttacherType = Attacher::AttachEngine3D
  Height = 20
  Placement = pos=(0,0,36.15) rot=(0,0,1;0rad)
  Radius = 10.3
FEATURE [Part::MultiFuse] Fusion118  label="removeToCreteHoleForPlugHousing042"
  Placement = pos=(70,19,36) rot=(0,1,0;1.5708rad)
  Shapes = -> [Cylinder049,Cylinder048]
FEATURE [Part::Cut] Cut050  label="plugHousingTab005"
  Base = -> Box030
  Placement = pos=(-107.4,-14,0) rot=(0,0,1;0rad)
  Tool = -> Fusion118
FEATURE [Part::MultiFuse] Fusion119
  Placement = pos=(9.6,23,0) rot=(0,0,1;3.14159rad)
  Shapes = -> [Cut049,Cut050]
FEATURE [Part::Box] Box031  label="Cube018"
  AttacherType = Attacher::AttachEngine3D
  Height = 10
  Length = 3
  Placement = pos=(3.3,4,12) rot=(0,0,1;0rad)
  Width = 10
FEATURE [Part::Fillet] Fillet044
  Base = -> Box031
  Edges = 1 edges r=2: [Edge11]
FEATURE [Part::Box] Box032  label="Cube019"
  AttacherType = Attacher::AttachEngine3D
  Height = 10
  Length = 3
  Placement = pos=(3.3,4,50) rot=(0,0,1;0rad)
  Width = 10
FEATURE [Part::Fillet] Fillet045
  Base = -> Box032
  Edges = 1 edges r=2: [Edge12]
FEATURE [Part::Box] Box033  label="Cube020"
  AttacherType = Attacher::AttachEngine3D
  Height = 28
  Length = 4
  Placement = pos=(5,0,22) rot=(0,0,1;0rad)
  Width = 10
FEATURE [Part::Fillet] Fillet046
  Base = -> Box033
  Edges = 1 edges r=1: [Edge7]
FEATURE [Part::Fillet] Fillet047
  Base = -> Fillet046
  Edges = 1 edges r=2: [Edge5]
FEATURE [Part::Fillet] Fillet048
  Base = -> Fillet047
  Edges = 1 edges r=2: [Edge2]
FEATURE [Part::Cylinder] Cylinder050
  Angle = 360
  AttacherType = Attacher::AttachEngine3D
  Height = 20
  Placement = pos=(0,0,36.15) rot=(0,0,1;0rad)
  Radius = 8.2
FEATURE [Part::Cylinder] Cylinder051
  Angle = 360
  AttacherType = Attacher::AttachEngine3D
  Height = 10
  Placement = pos=(0,0,36.15) rot=(0,0,1;0rad)
  Radius = 4
FEATURE [Part::MultiFuse] Fusion120  label="removeToCreteHoleForPlugHousing043"
  Placement = pos=(-42,19,36) rot=(0,1,0;1.5708rad)
  Shapes = -> [Cylinder050,Cylinder051]
FEATURE [Sketcher::SketchObject] Sketch067  label="topSketch018"
  FullyConstrained = true
  sketch-geometry (4):
    g0: LineSegment StartX=16.8446 StartY=31.512 StartZ=0 EndX=16.3251 EndY=34.4666 EndZ=0
    g1: ArcOfCircle CenterX=19 CenterY=19.2524 CenterZ=0 NormalX=0 NormalY=0 NormalZ=1 AngleXU=0 Radius=15.4476 StartAngle=1.74483 EndAngle=2.72717
    g2: ArcOfCircle CenterX=19 CenterY=19.2524 CenterZ=0 NormalX=0 NormalY=0 NormalZ=1 AngleXU=0 Radius=12.4476 StartAngle=1.74483 EndAngle=2.73189
    g3: LineSegment StartX=4.86004 StartY=25.4725 StartZ=0 EndX=7.58253 EndY=24.2107 EndZ=0
  constraints (7):
    c: Block(g0)
    c: Coincident(g1,g0)
    c: Coincident(g2,g0)
    c: Coincident(g3,g1)
    c: Coincident(g3,g2)
    c: Block(g1)
    c: Block(g2)
FEATURE [Part::Extrusion] Extrude058
  Base = -> Sketch067
  Dir = (0,0,1)
  DirMode = 2
  FaceMakerClass = Part::FaceMakerBullseye
  LengthFwd = 10
  LengthRev = 0
  Placement = pos=(0,0,31) rot=(0,0,1;0rad)
  Solid = true
  Symmetric = false
FEATURE [Part::Cut] Cut051
  Base = -> Extrude058
  Tool = -> Fusion120
FEATURE [Part::Fillet] Fillet049
  Base = -> Cut051
  Edges = 1 edges r=2: [Edge1]
FEATURE [Part::Fillet] Fillet050
  Base = -> Fillet049
  Edges = 1 edges r=2.5: [Edge1]
FEATURE [Part::Fillet] Fillet051
  Base = -> Fillet050
  Edges = 1 edges r=2.5: [Edge2]
FEATURE [Part::MultiFuse] Fusion121  label="wireHolder003"
  Shapes = -> [Fusion116,Fillet051]
FEATURE [Part::MultiFuse] Fusion122
  Shapes = -> [Fillet045,Fusion121]
FEATURE [Part::MultiFuse] Fusion123  label="wireHolder004"
  Shapes = -> [Fusion122,Fillet048]
FEATURE [Part::MultiFuse] Fusion124  label="wireHolder005"
  Shapes = -> [Fillet044,Fusion119,Fusion123]
FEATURE [Sketcher::SketchObject] Sketch068  label="topSketch019"
  FullyConstrained = true
  sketch-geometry (6):
    g0: LineSegment StartX=19 StartY=38 StartZ=0 EndX=117 EndY=38 EndZ=0
    g1: ArcOfCircle CenterX=19 CenterY=19 CenterZ=0 NormalX=0 NormalY=0 NormalZ=1 AngleXU=0 Radius=19 StartAngle=1.5708 EndAngle=3.14159
    g2: LineSegment StartX=117 StartY=38 StartZ=0 EndX=117 EndY=19 EndZ=0
    g3: LineSegment StartX=98 StartY=1.0161e-12 StartZ=0 EndX=5.22862e-06 EndY=1.0161e-12 EndZ=0
    g4: LineSegment StartX=5.22862e-06 StartY=19 StartZ=0 EndX=5.22862e-06 EndY=1.0161e-12 EndZ=0
    g5: ArcOfCircle CenterX=98 CenterY=19 CenterZ=0 NormalX=0 NormalY=0 NormalZ=1 AngleXU=0 Radius=19 StartAngle=4.71239 EndAngle=6.28319
  constraints (16):
    c: Horizontal(g0)
    c: Distance(g0) = 98
    c: Coincident(g1,g0)
    c: Block(g1)
    c: Coincident(g2,g0)
    c: Vertical(g2)
    c: Distance(g2) = 19
    c: Horizontal(g3)
    c: Coincident(g4,g1)
    c: Vertical(g4)
    c: Coincident(g3,g4)
    c: Block(g3)
    c: Coincident(g5,g2)
    c: Coincident(g5,g3)
    c: Block(g0)
    c: Block(g5)
FEATURE [Part::Extrusion] Extrude059  label="sideA002"
  Base = -> Sketch068
  Dir = (0,0,1)
  DirMode = 2
  FaceMakerClass = Part::FaceMakerBullseye
  LengthFwd = 3
  LengthRev = 0
  Placement = pos=(0,0,-2.7) rot=(0,0,1;0rad)
  Solid = true
  Symmetric = false
FEATURE [Sketcher::SketchObject] Sketch069  label="topSketch020"
  FullyConstrained = true
  sketch-geometry (6):
    g0: LineSegment StartX=19 StartY=38 StartZ=0 EndX=117 EndY=38 EndZ=0
    g1: ArcOfCircle CenterX=19 CenterY=19 CenterZ=0 NormalX=0 NormalY=0 NormalZ=1 AngleXU=0 Radius=19 StartAngle=1.5708 EndAngle=3.14159
    g2: LineSegment StartX=117 StartY=38 StartZ=0 EndX=117 EndY=19 EndZ=0
    g3: LineSegment StartX=98 StartY=1.0161e-12 StartZ=0 EndX=5.22862e-06 EndY=1.0161e-12 EndZ=0
    g4: LineSegment StartX=5.22862e-06 StartY=19 StartZ=0 EndX=5.22862e-06 EndY=1.0161e-12 EndZ=0
    g5: ArcOfCircle CenterX=98 CenterY=19 CenterZ=0 NormalX=0 NormalY=0 NormalZ=1 AngleXU=0 Radius=19 StartAngle=4.71239 EndAngle=6.28319
  constraints (16):
    c: Horizontal(g0)
    c: Distance(g0) = 98
    c: Coincident(g1,g0)
    c: Block(g1)
    c: Coincident(g2,g0)
    c: Vertical(g2)
    c: Distance(g2) = 19
    c: Horizontal(g3)
    c: Coincident(g4,g1)
    c: Vertical(g4)
    c: Coincident(g3,g4)
    c: Block(g3)
    c: Coincident(g5,g2)
    c: Coincident(g5,g3)
    c: Block(g0)
    c: Block(g5)
FEATURE [Part::Extrusion] Extrude060  label="sideB002"
  Base = -> Sketch069
  Dir = (0,0,1)
  DirMode = 2
  FaceMakerClass = Part::FaceMakerBullseye
  LengthFwd = 3
  LengthRev = 0
  Placement = pos=(0,0,71.7) rot=(0,0,1;0rad)
  Solid = true
  Symmetric = false
FEATURE [Part::MultiFuse] Fusion127  label="removeFromBottom001"
  Placement = pos=(2,0,0) rot=(0,0,1;0rad)
  Shapes = -> [Extrude059,Extrude060]
FEATURE [Part::Cylinder] Cylinder052
  Angle = 360
  AttacherType = Attacher::AttachEngine3D
  Height = 20
  Placement = pos=(0,0,36.15) rot=(0,0,1;0rad)
  Radius = 14
FEATURE [Part::Cylinder] Cylinder053
  Angle = 360
  AttacherType = Attacher::AttachEngine3D
  Height = 10
  Placement = pos=(0,0,36.15) rot=(0,0,1;0rad)
  Radius = 4
FEATURE [Part::MultiFuse] Fusion128  label="removeToCreteHoleForPlugHousing044"
  Placement = pos=(70,19,36) rot=(0,1,0;1.5708rad)
  Shapes = -> [Cylinder052,Cylinder053]
FEATURE [Part::Cut] Cut052  label="bottom011"
  Base = -> Extrude043
  Tool = -> Fusion128
FEATURE [Part::Cut] Cut054  label="bottom012"
  Base = -> Cut052
  Tool = -> Fusion115
FEATURE [Sketcher::SketchObject] Sketch070
  FullyConstrained = true
  Placement = pos=(117,19,0) rot=(0.57735,0.57735,0.57735;2.0944rad)
  sketch-geometry (48):
    g0: LineSegment StartX=-49.19 StartY=69.25 StartZ=0 EndX=-49.19 EndY=66.25 EndZ=0
    g1: LineSegment StartX=-49.19 StartY=63.5 StartZ=0 EndX=-49.19 EndY=60.5 EndZ=0
    g2: LineSegment StartX=-49.19 StartY=57.75 StartZ=0 EndX=-49.19 EndY=54.75 EndZ=0
    g3: LineSegment StartX=-49.19 StartY=52 StartZ=0 EndX=-49.19 EndY=49 EndZ=0
    g4: LineSegment StartX=-49.19 StartY=46.25 StartZ=0 EndX=-49.19 EndY=43.25 EndZ=0
    g5: LineSegment StartX=-49.19 StartY=40.5 StartZ=0 EndX=-49.19 EndY=37.5 EndZ=0
    g6: LineSegment StartX=-49.19 StartY=34.5 StartZ=0 EndX=-49.19 EndY=31.5 EndZ=0
    g7: LineSegment StartX=-49.19 StartY=28.75 StartZ=0 EndX=-49.19 EndY=25.75 EndZ=0
    g8: LineSegment StartX=-49.19 StartY=23 StartZ=0 EndX=-49.19 EndY=20 EndZ=0
    g9: LineSegment StartX=-49.19 StartY=17.25 StartZ=0 EndX=-49.19 EndY=14.25 EndZ=0
    g10: LineSegment StartX=-49.19 StartY=11.5 StartZ=0 EndX=-49.19 EndY=8.5 EndZ=0
    g11: LineSegment StartX=-49.19 StartY=5.75 StartZ=0 EndX=-49.19 EndY=2.75 EndZ=0
    g12: ArcOfCircle CenterX=-1.5 CenterY=67.75 CenterZ=0 NormalX=0 NormalY=0 NormalZ=1 AngleXU=0 Radius=1.5 StartAngle=4.71239 EndAngle=7.85398
    g13: ArcOfCircle CenterX=-1.5 CenterY=62 CenterZ=0 NormalX=0 NormalY=0 NormalZ=1 AngleXU=0 Radius=1.5 StartAngle=4.71239 EndAngle=7.85398
    g14: ArcOfCircle CenterX=-1.5 CenterY=56.25 CenterZ=0 NormalX=0 NormalY=0 NormalZ=1 AngleXU=0 Radius=1.5 StartAngle=4.71239 EndAngle=7.85398
    g15: ArcOfCircle CenterX=-11.49 CenterY=50.5 CenterZ=0 NormalX=0 NormalY=0 NormalZ=1 AngleXU=0 Radius=1.5 StartAngle=4.71239 EndAngle=7.85398
    g16: ArcOfCircle CenterX=-16.28 CenterY=44.75 CenterZ=0 NormalX=0 NormalY=0 NormalZ=1 AngleXU=0 Radius=1.5 StartAngle=4.71239 EndAngle=7.85398
    g17: ArcOfCircle CenterX=-18.2337 CenterY=39 CenterZ=0 NormalX=0 NormalY=0 NormalZ=1 AngleXU=0 Radius=1.5 StartAngle=4.71485 EndAngle=7.85398
    g18: ArcOfCircle CenterX=-16.2837 CenterY=27.25 CenterZ=0 NormalX=0 NormalY=0 NormalZ=1 AngleXU=0 Radius=1.5 StartAngle=4.71485 EndAngle=7.85398
    g19: ArcOfCircle CenterX=-18.2337 CenterY=33 CenterZ=0 NormalX=0 NormalY=0 NormalZ=1 AngleXU=0 Radius=1.5 StartAngle=4.71485 EndAngle=7.85398
    g20: ArcOfCircle CenterX=-11.49 CenterY=21.5 CenterZ=0 NormalX=0 NormalY=0 NormalZ=1 AngleXU=0 Radius=1.5 StartAngle=4.71239 EndAngle=7.85398
    g21: ArcOfCircle CenterX=-1.5 CenterY=4.25 CenterZ=0 NormalX=0 NormalY=0 NormalZ=1 AngleXU=0 Radius=1.5 StartAngle=4.71239 EndAngle=7.85398
    g22: ArcOfCircle CenterX=-1.5 CenterY=10 CenterZ=0 NormalX=0 NormalY=0 NormalZ=1 AngleXU=0 Radius=1.5 StartAngle=4.71239 EndAngle=7.85398
    g23: ArcOfCircle CenterX=-1.5 CenterY=15.75 CenterZ=0 NormalX=0 NormalY=0 NormalZ=1 AngleXU=0 Radius=1.5 StartAngle=4.71239 EndAngle=7.85398
    g24: LineSegment StartX=-49.19 StartY=69.25 StartZ=0 EndX=-1.5 EndY=69.25 EndZ=0
    g25: LineSegment StartX=-49.19 StartY=66.25 StartZ=0 EndX=-1.5 EndY=66.25 EndZ=0
    g26: LineSegment StartX=-49.19 StartY=63.5 StartZ=0 EndX=-1.5 EndY=63.5 EndZ=0
    g27: LineSegment StartX=-49.19 StartY=60.5 StartZ=0 EndX=-1.5 EndY=60.5 EndZ=0
    g28: LineSegment StartX=-49.19 StartY=57.75 StartZ=0 EndX=-1.5 EndY=57.75 EndZ=0
    g29: LineSegment StartX=-49.19 StartY=54.75 StartZ=0 EndX=-1.5 EndY=54.75 EndZ=0
    g30: LineSegment StartX=-49.19 StartY=52 StartZ=0 EndX=-11.49 EndY=52 EndZ=0
    g31: LineSegment StartX=-49.19 StartY=49 StartZ=0 EndX=-11.49 EndY=49 EndZ=0
    g32: LineSegment StartX=-49.19 StartY=46.25 StartZ=0 EndX=-16.28 EndY=46.25 EndZ=0
    g33: LineSegment StartX=-49.19 StartY=43.25 StartZ=0 EndX=-16.28 EndY=43.25 EndZ=0
    g34: LineSegment StartX=-49.19 StartY=40.5 StartZ=0 EndX=-18.2337 EndY=40.5 EndZ=0
    g35: LineSegment StartX=-49.19 StartY=37.5 StartZ=0 EndX=-18.23 EndY=37.5 EndZ=0
    g36: LineSegment StartX=-49.19 StartY=34.5 StartZ=0 EndX=-18.2337 EndY=34.5 EndZ=0
    g37: LineSegment StartX=-49.19 StartY=31.5 StartZ=0 EndX=-18.23 EndY=31.5 EndZ=0
    g38: LineSegment StartX=-49.19 StartY=28.75 StartZ=0 EndX=-16.2837 EndY=28.75 EndZ=0
    g39: LineSegment StartX=-49.19 StartY=25.75 StartZ=0 EndX=-16.28 EndY=25.75 EndZ=0
    g40: LineSegment StartX=-49.19 StartY=23 StartZ=0 EndX=-11.49 EndY=23 EndZ=0
    g41: LineSegment StartX=-49.19 StartY=20 StartZ=0 EndX=-11.49 EndY=20 EndZ=0
    g42: LineSegment StartX=-49.19 StartY=17.25 StartZ=0 EndX=-1.5 EndY=17.25 EndZ=0
    g43: LineSegment StartX=-49.19 StartY=14.25 StartZ=0 EndX=-1.5 EndY=14.25 EndZ=0
    g44: LineSegment StartX=-49.19 StartY=11.5 StartZ=0 EndX=-1.5 EndY=11.5 EndZ=0
    g45: LineSegment StartX=-49.19 StartY=8.5 StartZ=0 EndX=-1.5 EndY=8.5 EndZ=0
    g46: LineSegment StartX=-49.19 StartY=5.75 StartZ=0 EndX=-1.5 EndY=5.75 EndZ=0
    g47: LineSegment StartX=-49.19 StartY=2.75 StartZ=0 EndX=-1.5 EndY=2.75 EndZ=0
  constraints (120):
    c: Vertical(g0)
    c: Distance(g0) = 3
    c: Block(g0)
    c: Vertical(g1)
    c: Distance(g1) = 3
    c: Vertical(g2)
    c: Equal(g0,g2) = 3
    c: Block(g2)
    c: Vertical(g3)
    c: Equal(g1,g3) = 3
    c: Vertical(g4)
    c: Equal(g0,g4) = 3
    c: Block(g4)
    c: Vertical(g5)
    c: Equal(g1,g5) = 3
    c: Vertical(g6)
    c: Equal(g0,g6) = 3
    c: Block(g6)
    c: Vertical(g7)
    c: Equal(g1,g7) = 3
    c: Vertical(g8)
    c: Equal(g0,g8) = 3
    c: Block(g8)
    c: Vertical(g9)
    c: Equal(g1,g9) = 3
    c: Vertical(g10)
    c: Equal(g0,g10) = 3
    c: Block(g10)
    c: Vertical(g11)
    c: Equal(g1,g11) = 3
    c: Block(g12)
    c: Block(g13)
    c: Block(g14)
    c: Block(g15)
    c: Block(g16)
    c: Block(g17)
    c: Block(g18)
    c: Block(g19)
    c: Block(g20)
    c: Block(g21)
    c: Block(g22)
    c: Block(g23)
    c: Block(g11)
    c: Block(g9)
    c: Block(g7)
    c: Block(g5)
    c: Block(g3)
    c: Block(g1)
    c: Coincident(g24,g0)
    c: Coincident(g24,g12)
    c: Horizontal(g24)
    c: Coincident(g25,g0)
    c: Coincident(g25,g12)
    c: Horizontal(g25)
    c: Coincident(g26,g1)
    c: Coincident(g26,g13)
    c: Horizontal(g26)
    c: Coincident(g27,g1)
    c: Coincident(g27,g13)
    c: Horizontal(g27)
    c: Coincident(g28,g2)
    c: Coincident(g28,g14)
    c: Horizontal(g28)
    c: Coincident(g29,g2)
    c: Coincident(g29,g14)
    c: Horizontal(g29)
    c: Coincident(g30,g3)
    c: Coincident(g30,g15)
    c: Horizontal(g30)
    c: Coincident(g31,g3)
    c: Coincident(g31,g15)
    c: Horizontal(g31)
    c: Coincident(g32,g4)
    c: Coincident(g32,g16)
    c: Horizontal(g32)
    c: Coincident(g33,g4)
    c: Coincident(g33,g16)
    c: Horizontal(g33)
    c: Coincident(g34,g5)
    c: Coincident(g34,g17)
    c: Horizontal(g34)
    c: Coincident(g35,g5)
    c: Coincident(g35,g17)
    c: Horizontal(g35)
    c: Coincident(g36,g6)
    c: Coincident(g36,g19)
    c: Horizontal(g36)
    c: Coincident(g37,g6)
    c: Coincident(g37,g19)
    c: Horizontal(g37)
    c: Coincident(g38,g7)
    c: Coincident(g38,g18)
    c: Horizontal(g38)
    c: Coincident(g39,g7)
    c: Coincident(g39,g18)
    c: Horizontal(g39)
    c: Coincident(g40,g8)
    c: Coincident(g40,g20)
    c: Horizontal(g40)
    c: Coincident(g41,g8)
    c: Coincident(g41,g20)
    c: Horizontal(g41)
    c: Coincident(g42,g9)
    c: Coincident(g42,g23)
    c: Horizontal(g42)
    c: Coincident(g43,g9)
    c: Coincident(g43,g23)
    c: Horizontal(g43)
    c: Coincident(g44,g10)
    c: Coincident(g44,g22)
    c: Horizontal(g44)
    c: Coincident(g45,g10)
    c: Coincident(g45,g22)
    c: Horizontal(g45)
    c: Coincident(g46,g11)
    c: Coincident(g46,g21)
    c: Horizontal(g46)
    c: Coincident(g47,g11)
    c: Coincident(g47,g21)
    c: Horizontal(g47)
FEATURE [Part::Extrusion] Extrude061
  Base = -> Sketch070
  Dir = (1,0,0)
  DirMode = 2
  FaceMakerClass = Part::FaceMakerBullseye
  LengthFwd = 23
  LengthRev = 0
  Placement = pos=(-19,0,0) rot=(0,0,1;0rad)
  Solid = true
  Symmetric = false
FEATURE [Part::Fillet] Fillet052  label="removeToCreateVentalationHoles002"
  Base = -> Extrude061
  Edges = <same value as first occurrence — deduplicated (x6 in doc)>
  Placement = pos=(7,0.02,0) rot=(0,0,1;0rad)
FEATURE [Part::MultiFuse] Fusion130  label="bottom013"
  Shapes = -> [Cut054,Cut034]
FEATURE [Part::Cut] Cut055
  Base = -> Fusion130
  Tool = -> Fillet052
FEATURE [Part::Cylinder] Cylinder054
  Angle = 360
  AttacherType = Attacher::AttachEngine3D
  Height = 20
  Placement = pos=(0,0,36.15) rot=(0,0,1;0rad)
  Radius = 4
FEATURE [Sketcher::SketchObject] Sketch071  label="bottomSketch002"
  FullyConstrained = true
  sketch-geometry (32):
    g0: LineSegment StartX=3.3 StartY=-6.03275e-07 StartZ=0 EndX=98 EndY=-6.03275e-07 EndZ=0
    g1: ArcOfCircle CenterX=98 CenterY=19 CenterZ=0 NormalX=0 NormalY=0 NormalZ=1 AngleXU=0 Radius=19 StartAngle=4.71239 EndAngle=5.71103
    g2: LineSegment StartX=6.3 StartY=8 StartZ=0 EndX=3.3 EndY=8 EndZ=0
    g3: LineSegment StartX=3.3 StartY=8 StartZ=0 EndX=3.3 EndY=-6.03275e-07 EndZ=0
    g4: ArcOfCircle CenterX=8.3 CenterY=5 CenterZ=0 NormalX=0 NormalY=0 NormalZ=1 AngleXU=0 Radius=2 StartAngle=3.14159 EndAngle=4.71239
    g5: LineSegment StartX=6.3 StartY=8 StartZ=0 EndX=6.3 EndY=5 EndZ=0
    g6: ArcOfCircle CenterX=98 CenterY=19 CenterZ=0 NormalX=0 NormalY=0 NormalZ=1 AngleXU=0 Radius=12.7 StartAngle=4.71239 EndAngle=6.28319
    g7: LineSegment StartX=94.7 StartY=3 StartZ=0 EndX=8.3 EndY=3 EndZ=0
    g8-g12: Circle x5 (B-spline internal-alignment scaffolding for g13; pole/knot coordinates omitted)
    g13: BSplineCurve PolesCount=5 KnotsCount=3 Degree=3 IsPeriodic=0
    g14: GeomPoint X=98 Y=6.3 Z=0
    g15: GeomPoint X=96.3938 Y=4.71946 Z=0
    g16: GeomPoint X=94.7 Y=3 Z=0
    g17-g23: Circle x7 (B-spline internal-alignment scaffolding for g24; pole/knot coordinates omitted)
    g24: BSplineCurve PolesCount=7 KnotsCount=5 Degree=3 IsPeriodic=0
    g25-g29: GeomPoint x5 (B-spline internal-alignment scaffolding for g24; pole/knot coordinates omitted)
    g30: ArcOfCircle CenterX=98 CenterY=19 CenterZ=0 NormalX=0 NormalY=0 NormalZ=1 AngleXU=0 Radius=15.7 StartAngle=5.81226 EndAngle=6.28319
    g31: LineSegment StartX=110.7 StartY=19 StartZ=0 EndX=113.7 EndY=19 EndZ=0
  constraints (41):
    c: Horizontal(g0)
    c: Coincident(g1,g0)
    c: Block(g1)
    c: Horizontal(g2)
    c: Distance(g2) = 3
    c: Coincident(g3,g2)
    c: Vertical(g3)
    c: Coincident(g3,g0)
    c: Block(g4)
    c: Block(g2)
    c: Coincident(g5,g2)
    c: Coincident(g5,g4)
    c: Vertical(g5)
    c: Coincident(g6,g1)
    c: Block(g6)
    c: Coincident(g7,g4)
    c: Horizontal(g7)
    c: Block(g0)
    c: Block(g7)
    c: Block(g3)
    c: Coincident(g13,g6)
    c: Weight(g8) = 1
    c: Equal(g8, g9-g12) x4
    c: Coincident(g13,g7)
    c: InternalAlignment(g8-g12 -> g13) x5
    c: InternalAlignment(g14,g13)
    c: InternalAlignment(g15,g13)
    c: InternalAlignment(g16,g13)
    c: Block(g13)
    c: Weight(g17) = 1
    c: Equal(g17, g18-g23) x6
    c: Coincident(g24,g1)
    c: InternalAlignment(g17-g23 -> g24) x7
    c: InternalAlignment(g25-g29 -> g24) x5
    c: Block(g24)
    c: Coincident(g30,g24)
    c: Coincident(g31,g6)
    c: Coincident(g31,g30)
    c: Horizontal(g31)
    c: Block(g31)
    c: Block(g30)
FEATURE [Part::Extrusion] Extrude062  label="bottom014"
  Base = -> Sketch071
  Dir = (0,0,1)
  DirMode = 2
  FaceMakerClass = Part::FaceMakerBullseye
  LengthFwd = 71.4
  LengthRev = 0
  Placement = pos=(0,0,0.3) rot=(0,0,1;0rad)
  Solid = true
  Symmetric = false
FEATURE [Part::Fillet] Fillet054
  Base = -> Extrude062
  Edges = 1 edges r=2.4: [Edge17]
FEATURE [Part::Fillet] Fillet055  label="bottom015"
  Base = -> Fillet054
  Edges = 1 edges r=2.4: [Edge36]
FEATURE [Part::Cylinder] Cylinder055
  Angle = 360
  AttacherType = Attacher::AttachEngine3D
  Height = 10
  Placement = pos=(0,0,36.15) rot=(0,0,1;0rad)
  Radius = 4
FEATURE [Part::MultiFuse] Fusion131  label="removeToCreateHoleForPlugHousing002"
  Placement = pos=(70,19,36.15) rot=(0,1,0;1.5708rad)
  Shapes = -> [Cylinder054,Cylinder055]
FEATURE [Part::Cut] Cut056  label="Bottom001"
  Base = -> Fillet055
  Placement = pos=(9,0,0) rot=(0,0,1;0rad)
  Tool = -> Fusion131
FEATURE [Part::Cut] Cut057
  Base = -> Cut055
  Tool = -> Cut056
FEATURE [Sketcher::SketchObject] Sketch072  label="topSketch021"
  FullyConstrained = true
  sketch-geometry (4):
    g0: ArcOfCircle CenterX=105 CenterY=19 CenterZ=0 NormalX=0 NormalY=0 NormalZ=1 AngleXU=0 Radius=20.6155 StartAngle=5.54125 EndAngle=6.28319
    g1: ArcOfCircle CenterX=105 CenterY=19 CenterZ=0 NormalX=0 NormalY=0 NormalZ=1 AngleXU=0 Radius=13 StartAngle=5.54125 EndAngle=6.28319
    g2: LineSegment StartX=118 StartY=19 StartZ=0 EndX=125.616 EndY=19 EndZ=0
    g3: LineSegment StartX=114.583 StartY=10.2157 StartZ=0 EndX=120.197 EndY=5.06982 EndZ=0
  constraints (7):
    c: Block(g0)
    c: Block(g1)
    c: Coincident(g2,g1)
    c: Coincident(g2,g0)
    c: Horizontal(g2)
    c: Coincident(g3,g1)
    c: Coincident(g3,g0)
FEATURE [Part::Extrusion] Extrude063  label="bottomPlugHousingBit003"
  Base = -> Sketch072
  Dir = (0,0,1)
  DirMode = 2
  FaceMakerClass = Part::FaceMakerBullseye
  LengthFwd = 72
  LengthRev = 0
  Solid = true
  Symmetric = false
FEATURE [Part::Cylinder] Cylinder056
  Angle = 360
  AttacherType = Attacher::AttachEngine3D
  Height = 20
  Placement = pos=(0,0,36.15) rot=(0,0,1;0rad)
  Radius = 14.3
FEATURE [Part::Cylinder] Cylinder057
  Angle = 360
  AttacherType = Attacher::AttachEngine3D
  Height = 10
  Placement = pos=(0,0,36.15) rot=(0,0,1;0rad)
  Radius = 4
FEATURE [Part::Box] Box034  label="removeToCreteHoleForPlugHousing047"
  AttacherType = Attacher::AttachEngine3D
  Height = 28.6
  Length = 20
  Placement = pos=(106.15,0,21.7) rot=(0,0,1;0rad)
  Width = 19
FEATURE [Part::Cylinder] Cylinder058
  Angle = 360
  AttacherType = Attacher::AttachEngine3D
  Height = 20
  Placement = pos=(0,0,36.15) rot=(0,0,1;0rad)
  Radius = 14.3
FEATURE [Part::Cylinder] Cylinder059
  Angle = 360
  AttacherType = Attacher::AttachEngine3D
  Height = 10
  Placement = pos=(0,0,36.15) rot=(0,0,1;0rad)
  Radius = 4
FEATURE [Part::MultiFuse] Fusion134  label="removeToCreteHoleForPlugHousing046"
  Placement = pos=(70,19,36) rot=(0,1,0;1.5708rad)
  Shapes = -> [Cylinder058,Cylinder059]
FEATURE [Part::Cylinder] Cylinder060
  Angle = 360
  AttacherType = Attacher::AttachEngine3D
  Height = 20
  Placement = pos=(0,0,36.15) rot=(0,0,1;0rad)
  Radius = 14
FEATURE [Part::Cylinder] Cylinder061
  Angle = 360
  AttacherType = Attacher::AttachEngine3D
  Height = 10
  Placement = pos=(0,0,36.15) rot=(0,0,1;0rad)
  Radius = 4
FEATURE [Part::MultiFuse] Fusion135  label="removeToCreteHoleForPlugHousing048"
  Placement = pos=(70,19,36) rot=(0,1,0;1.5708rad)
  Shapes = -> [Cylinder060,Cylinder061]
FEATURE [Part::Box] Box035  label="removeToCreteHoleForPlugHousing049"
  AttacherType = Attacher::AttachEngine3D
  Height = 28.6
  Length = 20
  Placement = pos=(106.15,0,21.7) rot=(0,0,1;0rad)
  Width = 19
FEATURE [Part::MultiFuse] Fusion133  label="removeToCreteHoleForPlugHousing045"
  Placement = pos=(0,0,-28.3) rot=(0,0,1;0rad)
  Shapes = -> [Box035,Fusion134]
FEATURE [Part::MultiFuse] Fusion138  label="removeToCreteHoleForPlugHousing051"
  Placement = pos=(70,19,36) rot=(0,1,0;1.5708rad)
  Shapes = -> [Cylinder056,Cylinder057]
FEATURE [Part::MultiFuse] Fusion137  label="removeToCreteHoleForPlugHousing050"
  Placement = pos=(0,0,28.3) rot=(0,0,1;0rad)
  Shapes = -> [Box034,Fusion138]
FEATURE [Part::MultiFuse] Fusion132  label="removeToCreatePlugHousingBottomBit002"
  Shapes = -> [Fusion133,Fusion137]
FEATURE [Part::MultiFuse] Fusion136  label="removeToCreatePlugHousingBottomBit003"
  Shapes = -> [Fusion135,Fusion132]
FEATURE [Part::Cut] Cut058  label="bottomPlugHousingBit002"
  Base = -> Extrude063
  Placement = pos=(-0.09,0,0) rot=(0,0,1;0rad)
  Tool = -> Fusion136
FEATURE [Sketcher::SketchObject] Sketch073  label="bottomSketch003"
  FullyConstrained = true
  sketch-geometry (45):
    g0: LineSegment StartX=6.29999 StartY=8 StartZ=0 EndX=3.29999 EndY=8 EndZ=0
    g1: LineSegment StartX=3.29999 StartY=8 StartZ=0 EndX=3.29999 EndY=-6.03275e-07 EndZ=0
    g2: ArcOfCircle CenterX=8.29999 CenterY=5 CenterZ=0 NormalX=0 NormalY=0 NormalZ=1 AngleXU=0 Radius=2 StartAngle=3.14159 EndAngle=4.71239
    g3: LineSegment StartX=6.29999 StartY=8 StartZ=0 EndX=6.29999 EndY=5 EndZ=0
    g4: ArcOfCircle CenterX=105 CenterY=19 CenterZ=0 NormalX=0 NormalY=0 NormalZ=1 AngleXU=0 Radius=12.7 StartAngle=4.71239 EndAngle=5.94289
    g5-g11: Circle x7 (B-spline internal-alignment scaffolding for g12; pole/knot coordinates omitted)
    g12: BSplineCurve PolesCount=7 KnotsCount=5 Degree=3 IsPeriodic=0
    g13-g17: GeomPoint x5 (B-spline internal-alignment scaffolding for g12; pole/knot coordinates omitted)
    g18: ArcOfCircle CenterX=105 CenterY=19 CenterZ=0 NormalX=0 NormalY=0 NormalZ=1 AngleXU=0 Radius=15.7 StartAngle=5.81226 EndAngle=6.28319
    g19: BSplineCurve PolesCount=5 KnotsCount=3 Degree=3 IsPeriodic=0
    g20: LineSegment StartX=8.29999 StartY=3 StartZ=0 EndX=101.7 EndY=3 EndZ=0
    g21: LineSegment StartX=3.29999 StartY=-6.03275e-07 StartZ=0 EndX=105 EndY=-6.03275e-07 EndZ=0
    g22: LineSegment StartX=120.974 StartY=8.71251 StartZ=0 EndX=122.332 EndY=7.83778 EndZ=0
    g23: LineSegment StartX=105 StartY=-6.03274e-07 StartZ=0 EndX=113 EndY=-6.03274e-07 EndZ=0
    g24: ArcOfCircle CenterX=105 CenterY=19 CenterZ=0 NormalX=0 NormalY=0 NormalZ=1 AngleXU=0 Radius=20.6155 StartAngle=5.11091 EndAngle=5.71103
    g25: ArcOfCircle CenterX=117.7 CenterY=19 CenterZ=0 NormalX=0 NormalY=0 NormalZ=1 AngleXU=0 Radius=3 StartAngle=1.2e-15 EndAngle=2.10468
    g26: Circle CenterX=116.345 CenterY=16.3232 CenterZ=0 NormalX=0 NormalY=0 NormalZ=1 AngleXU=0 Radius=1
    g27: Circle CenterX=117.24 CenterY=15.7584 CenterZ=0 NormalX=0 NormalY=0 NormalZ=1 AngleXU=0 Radius=1
    g28: Circle CenterX=116.972 CenterY=14.7612 CenterZ=0 NormalX=0 NormalY=0 NormalZ=1 AngleXU=0 Radius=1
    g29: BSplineCurve PolesCount=3 KnotsCount=2 Degree=2 IsPeriodic=0
    g30: GeomPoint X=116.345 Y=16.3232 Z=0
    g31: GeomPoint X=116.972 Y=14.7612 Z=0
    g32: Circle CenterX=115.828 CenterY=17.157 CenterZ=0 NormalX=0 NormalY=0 NormalZ=1 AngleXU=0 Radius=1
    g33: Circle CenterX=115.841 CenterY=16.639 CenterZ=0 NormalX=0 NormalY=0 NormalZ=1 AngleXU=0 Radius=1
    g34: Circle CenterX=116.345 CenterY=16.3232 CenterZ=0 NormalX=0 NormalY=0 NormalZ=1 AngleXU=0 Radius=1
    g35: BSplineCurve PolesCount=3 KnotsCount=2 Degree=2 IsPeriodic=0
    g36: GeomPoint X=115.828 Y=17.157 Z=0
    g37: GeomPoint X=116.345 Y=16.3232 Z=0
    g38: LineSegment StartX=115.828 StartY=17.157 StartZ=0 EndX=115.828 EndY=20.8307 EndZ=0
    g39: Circle CenterX=115.828 CenterY=20.8307 CenterZ=0 NormalX=0 NormalY=0 NormalZ=1 AngleXU=0 Radius=1
    g40: Circle CenterX=115.831 CenterY=21.3396 CenterZ=0 NormalX=0 NormalY=0 NormalZ=1 AngleXU=0 Radius=1
    g41: Circle CenterX=116.173 CenterY=21.5825 CenterZ=0 NormalX=0 NormalY=0 NormalZ=1 AngleXU=0 Radius=1
    g42: BSplineCurve PolesCount=3 KnotsCount=2 Degree=2 IsPeriodic=0
    g43: GeomPoint X=115.828 Y=20.8307 Z=0
    g44: GeomPoint X=116.173 Y=21.5825 Z=0
  constraints (70):
    c: Horizontal(g0)
    c: Distance(g0) = 3
    c: Coincident(g1,g0)
    c: Vertical(g1)
    c: Block(g2)
    c: Block(g0)
    c: Coincident(g3,g0)
    c: Coincident(g3,g2)
    c: Vertical(g3)
    c: Block(g1)
    c: Block(g4)
    c: Coincident(g19,g4)
    c: Block(g19)
    c: Equal(g5, g6-g11) x6
    c: InternalAlignment(g5-g11 -> g12) x7
    c: InternalAlignment(g13-g17 -> g12) x5
    c: Block(g12)
    c: Coincident(g18,g12)
    c: Block(g18)
    c: Coincident(g20,g2)
    c: Coincident(g20,g19)
    c: Horizontal(g20)
    c: Distance(g20) = 93.4
    c: Coincident(g21,g1)
    c: Horizontal(g21)
    c: Distance(g21) = 101.7
    c: Horizontal(g23)
    c: Distance(g23) = 8
    c: Coincident(g24,g23)
    c: Block(g23)
    c: Coincident(g22,g24)
    c: Block(g24)
    c: Block(g22)
    c: Distance(g22) = 1.61553
    c: Coincident(g25,g18)
    c: Block(g25)
    c: Weight(g26) = 1
    c: Equal(g26,g27)
    c: Equal(g26,g28)
    c: Coincident(g29,g4)
    c: InternalAlignment(g26,g29)
    c: InternalAlignment(g27,g29)
    c: InternalAlignment(g28,g29)
    c: InternalAlignment(g30,g29)
    c: InternalAlignment(g31,g29)
    c: Block(g29)
    c: Weight(g32) = 1
    c: Equal(g32,g33)
    c: Equal(g32,g34)
    c: Coincident(g35,g29)
    c: InternalAlignment(g32,g35)
    c: InternalAlignment(g33,g35)
    c: InternalAlignment(g34,g35)
    c: InternalAlignment(g36,g35)
    c: InternalAlignment(g37,g35)
    c: Block(g35)
    c: Coincident(g38,g35)
    c: Vertical(g38)
    c: Block(g38)
    c: Coincident(g42,g38)
    c: Weight(g39) = 1
    c: Equal(g39,g40)
    c: Equal(g39,g41)
    c: Coincident(g42,g25)
    c: InternalAlignment(g39,g42)
    c: InternalAlignment(g40,g42)
    c: InternalAlignment(g41,g42)
    c: InternalAlignment(g43,g42)
    c: InternalAlignment(g44,g42)
    c: Block(g42)
FEATURE [Part::Extrusion] Extrude064  label="bottom016"
  Base = -> Sketch073
  Dir = (0,0,1)
  DirMode = 2
  FaceMakerClass = Part::FaceMakerBullseye
  LengthFwd = 71.4
  LengthRev = 0
  Placement = pos=(0,0,0.3) rot=(0,0,1;0rad)
  Solid = true
  Symmetric = false
FEATURE [Part::Revolution] Revolve157  label="removeToCreateScrewAndThreadedInsertHole063"
  Angle = 360
  Axis = (0,1,0)
  Base = (0,0,0)
  FaceMakerClass = Part::FaceMakerBullseye
  Placement = pos=(12.5,0,10) rot=(0,0,1;0rad)
  Solid = false
  Source = -> Face141
  Symmetric = false
FEATURE [Sketcher::SketchObject] Sketch074
  FullyConstrained = true
  Placement = pos=(117,19,0) rot=(0.57735,0.57735,0.57735;2.0944rad)
  sketch-geometry (48):
    g0: LineSegment StartX=-49.19 StartY=69.25 StartZ=0 EndX=-49.19 EndY=66.25 EndZ=0
    g1: LineSegment StartX=-49.19 StartY=63.5 StartZ=0 EndX=-49.19 EndY=60.5 EndZ=0
    g2: LineSegment StartX=-49.19 StartY=57.75 StartZ=0 EndX=-49.19 EndY=54.75 EndZ=0
    g3: LineSegment StartX=-49.19 StartY=52 StartZ=0 EndX=-49.19 EndY=49 EndZ=0
    g4: LineSegment StartX=-49.19 StartY=46.25 StartZ=0 EndX=-49.19 EndY=43.25 EndZ=0
    g5: LineSegment StartX=-49.19 StartY=40.5 StartZ=0 EndX=-49.19 EndY=37.5 EndZ=0
    g6: LineSegment StartX=-49.19 StartY=34.5 StartZ=0 EndX=-49.19 EndY=31.5 EndZ=0
    g7: LineSegment StartX=-49.19 StartY=28.75 StartZ=0 EndX=-49.19 EndY=25.75 EndZ=0
    g8: LineSegment StartX=-49.19 StartY=23 StartZ=0 EndX=-49.19 EndY=20 EndZ=0
    g9: LineSegment StartX=-49.19 StartY=17.25 StartZ=0 EndX=-49.19 EndY=14.25 EndZ=0
    g10: LineSegment StartX=-49.19 StartY=11.5 StartZ=0 EndX=-49.19 EndY=8.5 EndZ=0
    g11: LineSegment StartX=-49.19 StartY=5.75 StartZ=0 EndX=-49.19 EndY=2.75 EndZ=0
    g12: ArcOfCircle CenterX=-1.5 CenterY=67.75 CenterZ=0 NormalX=0 NormalY=0 NormalZ=1 AngleXU=0 Radius=1.5 StartAngle=4.71239 EndAngle=7.85398
    g13: ArcOfCircle CenterX=-1.5 CenterY=62 CenterZ=0 NormalX=0 NormalY=0 NormalZ=1 AngleXU=0 Radius=1.5 StartAngle=4.71239 EndAngle=7.85398
    g14: ArcOfCircle CenterX=-1.5 CenterY=56.25 CenterZ=0 NormalX=0 NormalY=0 NormalZ=1 AngleXU=0 Radius=1.5 StartAngle=4.71239 EndAngle=7.85398
    g15: ArcOfCircle CenterX=-11.49 CenterY=50.5 CenterZ=0 NormalX=0 NormalY=0 NormalZ=1 AngleXU=0 Radius=1.5 StartAngle=4.71239 EndAngle=7.85398
    g16: ArcOfCircle CenterX=-16.28 CenterY=44.75 CenterZ=0 NormalX=0 NormalY=0 NormalZ=1 AngleXU=0 Radius=1.5 StartAngle=4.71239 EndAngle=7.85398
    g17: ArcOfCircle CenterX=-18.2337 CenterY=39 CenterZ=0 NormalX=0 NormalY=0 NormalZ=1 AngleXU=0 Radius=1.5 StartAngle=4.71485 EndAngle=7.85398
    g18: ArcOfCircle CenterX=-16.2837 CenterY=27.25 CenterZ=0 NormalX=0 NormalY=0 NormalZ=1 AngleXU=0 Radius=1.5 StartAngle=4.71485 EndAngle=7.85398
    g19: ArcOfCircle CenterX=-18.2337 CenterY=33 CenterZ=0 NormalX=0 NormalY=0 NormalZ=1 AngleXU=0 Radius=1.5 StartAngle=4.71485 EndAngle=7.85398
    g20: ArcOfCircle CenterX=-11.49 CenterY=21.5 CenterZ=0 NormalX=0 NormalY=0 NormalZ=1 AngleXU=0 Radius=1.5 StartAngle=4.71239 EndAngle=7.85398
    g21: ArcOfCircle CenterX=-1.5 CenterY=4.25 CenterZ=0 NormalX=0 NormalY=0 NormalZ=1 AngleXU=0 Radius=1.5 StartAngle=4.71239 EndAngle=7.85398
    g22: ArcOfCircle CenterX=-1.5 CenterY=10 CenterZ=0 NormalX=0 NormalY=0 NormalZ=1 AngleXU=0 Radius=1.5 StartAngle=4.71239 EndAngle=7.85398
    g23: ArcOfCircle CenterX=-1.5 CenterY=15.75 CenterZ=0 NormalX=0 NormalY=0 NormalZ=1 AngleXU=0 Radius=1.5 StartAngle=4.71239 EndAngle=7.85398
    g24: LineSegment StartX=-49.19 StartY=69.25 StartZ=0 EndX=-1.5 EndY=69.25 EndZ=0
    g25: LineSegment StartX=-49.19 StartY=66.25 StartZ=0 EndX=-1.5 EndY=66.25 EndZ=0
    g26: LineSegment StartX=-49.19 StartY=63.5 StartZ=0 EndX=-1.5 EndY=63.5 EndZ=0
    g27: LineSegment StartX=-49.19 StartY=60.5 StartZ=0 EndX=-1.5 EndY=60.5 EndZ=0
    g28: LineSegment StartX=-49.19 StartY=57.75 StartZ=0 EndX=-1.5 EndY=57.75 EndZ=0
    g29: LineSegment StartX=-49.19 StartY=54.75 StartZ=0 EndX=-1.5 EndY=54.75 EndZ=0
    g30: LineSegment StartX=-49.19 StartY=52 StartZ=0 EndX=-11.49 EndY=52 EndZ=0
    g31: LineSegment StartX=-49.19 StartY=49 StartZ=0 EndX=-11.49 EndY=49 EndZ=0
    g32: LineSegment StartX=-49.19 StartY=46.25 StartZ=0 EndX=-16.28 EndY=46.25 EndZ=0
    g33: LineSegment StartX=-49.19 StartY=43.25 StartZ=0 EndX=-16.28 EndY=43.25 EndZ=0
    g34: LineSegment StartX=-49.19 StartY=40.5 StartZ=0 EndX=-18.2337 EndY=40.5 EndZ=0
    g35: LineSegment StartX=-49.19 StartY=37.5 StartZ=0 EndX=-18.23 EndY=37.5 EndZ=0
    g36: LineSegment StartX=-49.19 StartY=34.5 StartZ=0 EndX=-18.2337 EndY=34.5 EndZ=0
    g37: LineSegment StartX=-49.19 StartY=31.5 StartZ=0 EndX=-18.23 EndY=31.5 EndZ=0
    g38: LineSegment StartX=-49.19 StartY=28.75 StartZ=0 EndX=-16.2837 EndY=28.75 EndZ=0
    g39: LineSegment StartX=-49.19 StartY=25.75 StartZ=0 EndX=-16.28 EndY=25.75 EndZ=0
    g40: LineSegment StartX=-49.19 StartY=23 StartZ=0 EndX=-11.49 EndY=23 EndZ=0
    g41: LineSegment StartX=-49.19 StartY=20 StartZ=0 EndX=-11.49 EndY=20 EndZ=0
    g42: LineSegment StartX=-49.19 StartY=17.25 StartZ=0 EndX=-1.5 EndY=17.25 EndZ=0
    g43: LineSegment StartX=-49.19 StartY=14.25 StartZ=0 EndX=-1.5 EndY=14.25 EndZ=0
    g44: LineSegment StartX=-49.19 StartY=11.5 StartZ=0 EndX=-1.5 EndY=11.5 EndZ=0
    g45: LineSegment StartX=-49.19 StartY=8.5 StartZ=0 EndX=-1.5 EndY=8.5 EndZ=0
    g46: LineSegment StartX=-49.19 StartY=5.75 StartZ=0 EndX=-1.5 EndY=5.75 EndZ=0
    g47: LineSegment StartX=-49.19 StartY=2.75 StartZ=0 EndX=-1.5 EndY=2.75 EndZ=0
  constraints (120):
    c: Vertical(g0)
    c: Distance(g0) = 3
    c: Block(g0)
    c: Vertical(g1)
    c: Distance(g1) = 3
    c: Vertical(g2)
    c: Equal(g0,g2) = 3
    c: Block(g2)
    c: Vertical(g3)
    c: Equal(g1,g3) = 3
    c: Vertical(g4)
    c: Equal(g0,g4) = 3
    c: Block(g4)
    c: Vertical(g5)
    c: Equal(g1,g5) = 3
    c: Vertical(g6)
    c: Equal(g0,g6) = 3
    c: Block(g6)
    c: Vertical(g7)
    c: Equal(g1,g7) = 3
    c: Vertical(g8)
    c: Equal(g0,g8) = 3
    c: Block(g8)
    c: Vertical(g9)
    c: Equal(g1,g9) = 3
    c: Vertical(g10)
    c: Equal(g0,g10) = 3
    c: Block(g10)
    c: Vertical(g11)
    c: Equal(g1,g11) = 3
    c: Block(g12)
    c: Block(g13)
    c: Block(g14)
    c: Block(g15)
    c: Block(g16)
    c: Block(g17)
    c: Block(g18)
    c: Block(g19)
    c: Block(g20)
    c: Block(g21)
    c: Block(g22)
    c: Block(g23)
    c: Block(g11)
    c: Block(g9)
    c: Block(g7)
    c: Block(g5)
    c: Block(g3)
    c: Block(g1)
    c: Coincident(g24,g0)
    c: Coincident(g24,g12)
    c: Horizontal(g24)
    c: Coincident(g25,g0)
    c: Coincident(g25,g12)
    c: Horizontal(g25)
    c: Coincident(g26,g1)
    c: Coincident(g26,g13)
    c: Horizontal(g26)
    c: Coincident(g27,g1)
    c: Coincident(g27,g13)
    c: Horizontal(g27)
    c: Coincident(g28,g2)
    c: Coincident(g28,g14)
    c: Horizontal(g28)
    c: Coincident(g29,g2)
    c: Coincident(g29,g14)
    c: Horizontal(g29)
    c: Coincident(g30,g3)
    c: Coincident(g30,g15)
    c: Horizontal(g30)
    c: Coincident(g31,g3)
    c: Coincident(g31,g15)
    c: Horizontal(g31)
    c: Coincident(g32,g4)
    c: Coincident(g32,g16)
    c: Horizontal(g32)
    c: Coincident(g33,g4)
    c: Coincident(g33,g16)
    c: Horizontal(g33)
    c: Coincident(g34,g5)
    c: Coincident(g34,g17)
    c: Horizontal(g34)
    c: Coincident(g35,g5)
    c: Coincident(g35,g17)
    c: Horizontal(g35)
    c: Coincident(g36,g6)
    c: Coincident(g36,g19)
    c: Horizontal(g36)
    c: Coincident(g37,g6)
    c: Coincident(g37,g19)
    c: Horizontal(g37)
    c: Coincident(g38,g7)
    c: Coincident(g38,g18)
    c: Horizontal(g38)
    c: Coincident(g39,g7)
    c: Coincident(g39,g18)
    c: Horizontal(g39)
    c: Coincident(g40,g8)
    c: Coincident(g40,g20)
    c: Horizontal(g40)
    c: Coincident(g41,g8)
    c: Coincident(g41,g20)
    c: Horizontal(g41)
    c: Coincident(g42,g9)
    c: Coincident(g42,g23)
    c: Horizontal(g42)
    c: Coincident(g43,g9)
    c: Coincident(g43,g23)
    c: Horizontal(g43)
    c: Coincident(g44,g10)
    c: Coincident(g44,g22)
    c: Horizontal(g44)
    c: Coincident(g45,g10)
    c: Coincident(g45,g22)
    c: Horizontal(g45)
    c: Coincident(g46,g11)
    c: Coincident(g46,g21)
    c: Horizontal(g46)
    c: Coincident(g47,g11)
    c: Coincident(g47,g21)
    c: Horizontal(g47)
FEATURE [Part::Extrusion] Extrude065
  Base = -> Sketch074
  Dir = (1,0,0)
  DirMode = 2
  FaceMakerClass = Part::FaceMakerBullseye
  LengthFwd = 23
  LengthRev = 0
  Placement = pos=(-19,0,0) rot=(0,0,1;0rad)
  Solid = true
  Symmetric = false
FEATURE [Part::Fillet] Fillet056  label="removeToCreateVentalationHoles003"
  Base = -> Extrude065
  Edges = <same value as first occurrence — deduplicated (x6 in doc)>
  Placement = pos=(7,0.02,0) rot=(0,0,1;0rad)
FEATURE [Part::Revolution] Revolve158  label="removeToCreateScrewAndThreadedInsertHole065"
  Angle = 360
  Axis = (0,1,0)
  Base = (0,0,0)
  FaceMakerClass = Part::FaceMakerBullseye
  Placement = pos=(12.5,0,62) rot=(0,0,1;0rad)
  Solid = false
  Source = -> Face146
  Symmetric = false
FEATURE [Part::Revolution] Revolve159  label="removeToCreateScrewAndThreadedInsertHole066"
  Angle = 360
  Axis = (0,1,0)
  Base = (0,0,0)
  FaceMakerClass = Part::FaceMakerBullseye
  Placement = pos=(89.5,0,68.5) rot=(0,0,1;0rad)
  Solid = false
  Source = -> Face143
  Symmetric = false
FEATURE [Part::Revolution] Revolve160  label="removeToCreateScrewAndThreadedInsertHole067"
  Angle = 360
  Axis = (0,1,0)
  Base = (0,0,0)
  FaceMakerClass = Part::FaceMakerBullseye
  Placement = pos=(89.5,0,3.5) rot=(0,0,1;0rad)
  Solid = false
  Source = -> Face142
  Symmetric = false
FEATURE [Part::Revolution] Revolve161  label="removeToCreateScrewAndThreadedInsertHole068"
  Angle = 360
  Axis = (0,1,0)
  Base = (0,0,0)
  FaceMakerClass = Part::FaceMakerBullseye
  Placement = pos=(109.5,4.7,3.5) rot=(0,0,1;0rad)
  Solid = false
  Source = -> Face145
  Symmetric = false
FEATURE [Part::Revolution] Revolve162  label="removeToCreateScrewAndThreadedInsertHole069"
  Angle = 360
  Axis = (0,1,0)
  Base = (0,0,0)
  FaceMakerClass = Part::FaceMakerBullseye
  Placement = pos=(109.5,4.7,68.5) rot=(0,0,1;0rad)
  Solid = false
  Source = -> Face144
  Symmetric = false
FEATURE [Part::MultiFuse] Fusion141  label="removeToCreateScrewAndThreadedInsertHole064"
  Shapes = -> [Revolve162,Revolve161,Revolve160,Revolve159,Revolve158,Revolve157]
FEATURE [Part::Cylinder] Cylinder062
  Angle = 360
  AttacherType = Attacher::AttachEngine3D
  Height = 20
  Placement = pos=(0,0,36.15) rot=(0,0,1;0rad)
  Radius = 14
FEATURE [Part::Cylinder] Cylinder063
  Angle = 360
  AttacherType = Attacher::AttachEngine3D
  Height = 10
  Placement = pos=(0,0,36.15) rot=(0,0,1;0rad)
  Radius = 4
FEATURE [Part::MultiFuse] Fusion139  label="removeToCreteHoleForPlugHousing052"
  Placement = pos=(70,19,36) rot=(0,1,0;1.5708rad)
  Shapes = -> [Cylinder062,Cylinder063]
FEATURE [Part::Cut] Cut060  label="bottom017"
  Base = -> Extrude064
  Tool = -> Fusion139
FEATURE [Part::Cut] Cut061  label="bottom019"
  Base = -> Cut060
  Tool = -> Fusion141
FEATURE [Part::MultiFuse] Fusion140  label="bottom018"
  Shapes = -> [Cut061,Cut058]
FEATURE [Part::Cut] Cut059  label="bottom020"
  Base = -> Fusion140
  Tool = -> Fillet056
FEATURE [Part::Box] Box036  label="Cube021"
  AttacherType = Attacher::AttachEngine3D
  Height = 80
  Length = 26
  Placement = pos=(0,-1,-5) rot=(0,0,1;0rad)
  Width = 11
FEATURE [Part::Cut] Cut062  label="removeFromBottom002"
  Base = -> Cut057
  Tool = -> Box036
FEATURE [Part::Cut] Cut063
  Base = -> Cut059
  Tool = -> Cut062
FEATURE [Part::Cut] Cut064  label="pcbStands"
  Base = -> Fusion095
  Tool = -> Fusion127
FEATURE [Sketcher::SketchObject] Sketch075  label="topSketch022"
  FullyConstrained = true
  sketch-geometry (6):
    g0: LineSegment StartX=19 StartY=38 StartZ=0 EndX=117 EndY=38 EndZ=0
    g1: ArcOfCircle CenterX=19 CenterY=19 CenterZ=0 NormalX=0 NormalY=0 NormalZ=1 AngleXU=0 Radius=19 StartAngle=1.5708 EndAngle=3.14159
    g2: LineSegment StartX=117 StartY=38 StartZ=0 EndX=117 EndY=19 EndZ=0
    g3: LineSegment StartX=98 StartY=1.0161e-12 StartZ=0 EndX=5.22862e-06 EndY=1.0161e-12 EndZ=0
    g4: LineSegment StartX=5.22862e-06 StartY=19 StartZ=0 EndX=5.22862e-06 EndY=1.0161e-12 EndZ=0
    g5: ArcOfCircle CenterX=98 CenterY=19 CenterZ=0 NormalX=0 NormalY=0 NormalZ=1 AngleXU=0 Radius=19 StartAngle=4.71239 EndAngle=6.28319
  constraints (16):
    c: Horizontal(g0)
    c: Distance(g0) = 98
    c: Coincident(g1,g0)
    c: Block(g1)
    c: Coincident(g2,g0)
    c: Vertical(g2)
    c: Distance(g2) = 19
    c: Horizontal(g3)
    c: Coincident(g4,g1)
    c: Vertical(g4)
    c: Coincident(g3,g4)
    c: Block(g3)
    c: Coincident(g5,g2)
    c: Coincident(g5,g3)
    c: Block(g0)
    c: Block(g5)
FEATURE [Part::Extrusion] Extrude067  label="sideB003"
  Base = -> Sketch075
  Dir = (0,0,1)
  DirMode = 2
  FaceMakerClass = Part::FaceMakerBullseye
  LengthFwd = 3
  LengthRev = 0
  Placement = pos=(0,0,71.7) rot=(0,0,1;0rad)
  Solid = true
  Symmetric = false
FEATURE [Sketcher::SketchObject] Sketch076  label="topSketch023"
  FullyConstrained = true
  sketch-geometry (6):
    g0: LineSegment StartX=19 StartY=38 StartZ=0 EndX=117 EndY=38 EndZ=0
    g1: ArcOfCircle CenterX=19 CenterY=19 CenterZ=0 NormalX=0 NormalY=0 NormalZ=1 AngleXU=0 Radius=19 StartAngle=1.5708 EndAngle=3.14159
    g2: LineSegment StartX=117 StartY=38 StartZ=0 EndX=117 EndY=19 EndZ=0
    g3: LineSegment StartX=98 StartY=1.0161e-12 StartZ=0 EndX=5.22862e-06 EndY=1.0161e-12 EndZ=0
    g4: LineSegment StartX=5.22862e-06 StartY=19 StartZ=0 EndX=5.22862e-06 EndY=1.0161e-12 EndZ=0
    g5: ArcOfCircle CenterX=98 CenterY=19 CenterZ=0 NormalX=0 NormalY=0 NormalZ=1 AngleXU=0 Radius=19 StartAngle=4.71239 EndAngle=6.28319
  constraints (16):
    c: Horizontal(g0)
    c: Distance(g0) = 98
    c: Coincident(g1,g0)
    c: Block(g1)
    c: Coincident(g2,g0)
    c: Vertical(g2)
    c: Distance(g2) = 19
    c: Horizontal(g3)
    c: Coincident(g4,g1)
    c: Vertical(g4)
    c: Coincident(g3,g4)
    c: Block(g3)
    c: Coincident(g5,g2)
    c: Coincident(g5,g3)
    c: Block(g0)
    c: Block(g5)
FEATURE [Part::Extrusion] Extrude066  label="sideA003"
  Base = -> Sketch076
  Dir = (0,0,1)
  DirMode = 2
  FaceMakerClass = Part::FaceMakerBullseye
  LengthFwd = 3
  LengthRev = 0
  Placement = pos=(0,0,-2.7) rot=(0,0,1;0rad)
  Solid = true
  Symmetric = false
FEATURE [Part::MultiFuse] Fusion142  label="removeFromBottom003"
  Placement = pos=(2,0,0) rot=(0,0,1;0rad)
  Shapes = -> [Extrude066,Extrude067]
FEATURE [Part::Cut] Cut065  label="screwRetainers002"
  Base = -> Fusion096
  Tool = -> Fusion142
FEATURE [Sketcher::SketchObject] Sketch077
  FullyConstrained = true
  Placement = pos=(117,19,0) rot=(0.57735,0.57735,0.57735;2.0944rad)
  sketch-geometry (8):
    g0: LineSegment StartX=-49.19 StartY=63.5 StartZ=0 EndX=-49.19 EndY=60.5 EndZ=0
    g1: LineSegment StartX=-49.19 StartY=11.5 StartZ=0 EndX=-49.19 EndY=8.5 EndZ=0
    g2: ArcOfCircle CenterX=-1.5 CenterY=62 CenterZ=0 NormalX=0 NormalY=0 NormalZ=1 AngleXU=0 Radius=1.5 StartAngle=4.71239 EndAngle=7.85398
    g3: ArcOfCircle CenterX=-1.5 CenterY=10 CenterZ=0 NormalX=0 NormalY=0 NormalZ=1 AngleXU=0 Radius=1.5 StartAngle=4.71239 EndAngle=7.85398
    g4: LineSegment StartX=-49.19 StartY=63.5 StartZ=0 EndX=-1.5 EndY=63.5 EndZ=0
    g5: LineSegment StartX=-49.19 StartY=60.5 StartZ=0 EndX=-1.5 EndY=60.5 EndZ=0
    g6: LineSegment StartX=-49.19 StartY=11.5 StartZ=0 EndX=-1.5 EndY=11.5 EndZ=0
    g7: LineSegment StartX=-49.19 StartY=8.5 StartZ=0 EndX=-1.5 EndY=8.5 EndZ=0
  constraints (19):
    c: Vertical(g0)
    c: Distance(g0) = 3
    c: Vertical(g1)
    c: Block(g1)
    c: Block(g2)
    c: Block(g3)
    c: Block(g0)
    c: Coincident(g4,g0)
    c: Coincident(g4,g2)
    c: Horizontal(g4)
    c: Coincident(g5,g0)
    c: Coincident(g5,g2)
    c: Horizontal(g5)
    c: Coincident(g6,g1)
    c: Coincident(g6,g3)
    c: Horizontal(g6)
    c: Coincident(g7,g1)
    c: Coincident(g7,g3)
    c: Horizontal(g7)
FEATURE [Part::Extrusion] Extrude068
  Base = -> Sketch077
  Dir = (1,0,0)
  DirMode = 2
  FaceMakerClass = Part::FaceMakerBullseye
  LengthFwd = 10
  LengthRev = 0
  Solid = true
  Symmetric = false
FEATURE [Part::Fillet] Fillet057  label="removeFromtMoreFrontCaseScrewRetainers002"
  Base = -> Extrude068
  Edges = 4 edges r=1.49: [Edge6,Edge11,Edge18,Edge23]
  Placement = pos=(-12,0,0) rot=(0,0,1;0rad)
FEATURE [Sketcher::SketchObject] Sketch078
  FullyConstrained = true
  Placement = pos=(117,19,0) rot=(0.57735,0.57735,0.57735;2.0944rad)
  sketch-geometry (8):
    g0: LineSegment StartX=-49.19 StartY=69.25 StartZ=0 EndX=-49.19 EndY=66.25 EndZ=0
    g1: LineSegment StartX=-49.19 StartY=5.75 StartZ=0 EndX=-49.19 EndY=2.75 EndZ=0
    g2: ArcOfCircle CenterX=-1.5 CenterY=67.75 CenterZ=0 NormalX=0 NormalY=0 NormalZ=1 AngleXU=0 Radius=1.5 StartAngle=4.71239 EndAngle=7.85398
    g3: ArcOfCircle CenterX=-1.5 CenterY=4.25 CenterZ=0 NormalX=0 NormalY=0 NormalZ=1 AngleXU=0 Radius=1.5 StartAngle=4.71239 EndAngle=7.85398
    g4: LineSegment StartX=-49.19 StartY=69.25 StartZ=0 EndX=-1.5 EndY=69.25 EndZ=0
    g5: LineSegment StartX=-49.19 StartY=66.25 StartZ=0 EndX=-1.5 EndY=66.25 EndZ=0
    g6: LineSegment StartX=-49.19 StartY=5.75 StartZ=0 EndX=-1.5 EndY=5.75 EndZ=0
    g7: LineSegment StartX=-49.19 StartY=2.75 StartZ=0 EndX=-1.5 EndY=2.75 EndZ=0
  constraints (19):
    c: Vertical(g0)
    c: Distance(g0) = 3
    c: Block(g0)
    c: Vertical(g1)
    c: Block(g2)
    c: Block(g3)
    c: Block(g1)
    c: Coincident(g4,g0)
    c: Coincident(g4,g2)
    c: Horizontal(g4)
    c: Coincident(g5,g0)
    c: Coincident(g5,g2)
    c: Horizontal(g5)
    c: Coincident(g6,g1)
    c: Coincident(g6,g3)
    c: Horizontal(g6)
    c: Coincident(g7,g1)
    c: Coincident(g7,g3)
    c: Horizontal(g7)
FEATURE [Part::Extrusion] Extrude069
  Base = -> Sketch078
  Dir = (1,0,0)
  DirMode = 2
  FaceMakerClass = Part::FaceMakerBullseye
  LengthFwd = 10
  LengthRev = 0
  Solid = true
  Symmetric = false
FEATURE [Part::Fillet] Fillet058  label="removeFromtMoreFrontCaseScrewRetainers003"
  Base = -> Extrude069
  Edges = 4 edges r=1.49: [Edge6,Edge11,Edge18,Edge23]
  Placement = pos=(-4,0,0) rot=(0,0,1;0rad)
FEATURE [Part::Cut] Cut066
  Base = -> Cut065
  Tool = -> Fillet058
FEATURE [Part::Cut] Cut067  label="screwPillars"
  Base = -> Cut066
  Tool = -> Fillet057
FEATURE [Part::MultiFuse] Fusion143  label="bottom021"
  Shapes = -> [Cut031,Cut063]
FEATURE [Part::Cylinder] Cylinder
  Angle = 360
  AttacherType = Attacher::AttachEngine3D
  Height = 10
  Placement = pos=(20.65,12,4.68) rot=(1,0,0;1.5708rad)
  Radius = 2
FEATURE [Part::Cylinder] Cylinder064
  Angle = 360
  AttacherType = Attacher::AttachEngine3D
  Height = 10
  Placement = pos=(20.65,12,67.38) rot=(1,0,0;1.5708rad)
  Radius = 2
FEATURE [Part::Cylinder] Cylinder065
  Angle = 360
  AttacherType = Attacher::AttachEngine3D
  Height = 10
  Placement = pos=(77.15,12,67.38) rot=(1,0,0;1.5708rad)
  Radius = 2
FEATURE [Part::Cylinder] Cylinder066
  Angle = 360
  AttacherType = Attacher::AttachEngine3D
  Height = 10
  Placement = pos=(77.15,12,4.68) rot=(1,0,0;1.5708rad)
  Radius = 2
FEATURE [Part::MultiFuse] Fusion144  label="removeFromThreadedInsertHousing"
  Shapes = -> [Cylinder065,Cylinder064,Cylinder,Cylinder066]
FEATURE [Part::Cut] Cut068  label="pcbStands001"
  Base = -> Cut064
  Tool = -> Fusion144
FEATURE [Part::MultiFuse] Fusion145
  Shapes = -> [Cut068,Fusion143]
FEATURE [Part::MultiFuse] Fusion146
  Shapes = -> [Fusion145]
FEATURE [Part::MultiFuse] Fusion147  label="bottom022"
  Shapes = -> [Cut067,Fusion146]
FEATURE [Part::MultiFuse] Fusion148  label="casePillars005"
  Shapes = -> [Cut047,Fusion092]
FEATURE [Part::MultiFuse] Fusion149  label="bottom023"
  Shapes = -> [Fusion124,Fusion113,Fusion147]
FEATURE [Part::MultiFuse] Fusion150  label="topBits"
  Shapes = -> [Cut025,Fusion148,Cut030,Fillet034]
FEATURE [Part::Feature] Face149 .. Face152  x4 (patterned run collapsed; names and placements below)
  shape: bbox 3.2 x 1.5 x 2e-07 mm, 1 faces, 0 solids (baked)
FEATURE [Part::Feature] Face153
  shape: bbox 3.6 x 3.2 x 2e-07 mm, 1 faces, 0 solids (baked)
FEATURE [Part::Feature] Face154
  shape: bbox 3.6 x 3.2 x 2e-07 mm, 1 faces, 0 solids (baked)
FEATURE [Sketcher::SketchObject] Sketch079  label="topSketch024"
  FullyConstrained = true
  sketch-geometry (6):
    g0: LineSegment StartX=19 StartY=38 StartZ=0 EndX=117 EndY=38 EndZ=0
    g1: ArcOfCircle CenterX=19 CenterY=19 CenterZ=0 NormalX=0 NormalY=0 NormalZ=1 AngleXU=0 Radius=19 StartAngle=1.5708 EndAngle=3.14159
    g2: LineSegment StartX=117 StartY=38 StartZ=0 EndX=117 EndY=19 EndZ=0
    g3: LineSegment StartX=98 StartY=1.0161e-12 StartZ=0 EndX=5.22862e-06 EndY=1.0161e-12 EndZ=0
    g4: LineSegment StartX=5.22862e-06 StartY=19 StartZ=0 EndX=5.22862e-06 EndY=1.0161e-12 EndZ=0
    g5: ArcOfCircle CenterX=98 CenterY=19 CenterZ=0 NormalX=0 NormalY=0 NormalZ=1 AngleXU=0 Radius=19 StartAngle=4.71239 EndAngle=6.28319
  constraints (16):
    c: Horizontal(g0)
    c: Distance(g0) = 98
    c: Coincident(g1,g0)
    c: Block(g1)
    c: Coincident(g2,g0)
    c: Vertical(g2)
    c: Distance(g2) = 19
    c: Horizontal(g3)
    c: Coincident(g4,g1)
    c: Vertical(g4)
    c: Coincident(g3,g4)
    c: Block(g3)
    c: Coincident(g5,g2)
    c: Coincident(g5,g3)
    c: Block(g0)
    c: Block(g5)
FEATURE [Sketcher::SketchObject] Sketch080  label="topSketch025"
  FullyConstrained = true
  sketch-geometry (6):
    g0: LineSegment StartX=19 StartY=38 StartZ=0 EndX=117 EndY=38 EndZ=0
    g1: ArcOfCircle CenterX=19 CenterY=19 CenterZ=0 NormalX=0 NormalY=0 NormalZ=1 AngleXU=0 Radius=19 StartAngle=1.5708 EndAngle=3.14159
    g2: LineSegment StartX=117 StartY=38 StartZ=0 EndX=117 EndY=19 EndZ=0
    g3: LineSegment StartX=98 StartY=1.0161e-12 StartZ=0 EndX=5.22862e-06 EndY=1.0161e-12 EndZ=0
    g4: LineSegment StartX=5.22862e-06 StartY=19 StartZ=0 EndX=5.22862e-06 EndY=1.0161e-12 EndZ=0
    g5: ArcOfCircle CenterX=98 CenterY=19 CenterZ=0 NormalX=0 NormalY=0 NormalZ=1 AngleXU=0 Radius=19 StartAngle=4.71239 EndAngle=6.28319
  constraints (16):
    c: Horizontal(g0)
    c: Distance(g0) = 98
    c: Coincident(g1,g0)
    c: Block(g1)
    c: Coincident(g2,g0)
    c: Vertical(g2)
    c: Distance(g2) = 19
    c: Horizontal(g3)
    c: Coincident(g4,g1)
    c: Vertical(g4)
    c: Coincident(g3,g4)
    c: Block(g3)
    c: Coincident(g5,g2)
    c: Coincident(g5,g3)
    c: Block(g0)
    c: Block(g5)
FEATURE [Part::Extrusion] Extrude070  label="sideA004"
  Base = -> Sketch080
  Dir = (0,0,1)
  DirMode = 2
  FaceMakerClass = Part::FaceMakerBullseye
  LengthFwd = 3
  LengthRev = 0
  Placement = pos=(0,0,-2.7) rot=(0,0,1;0rad)
  Solid = true
  Symmetric = false
FEATURE [Sketcher::SketchObject] Sketch081
  FullyConstrained = true
  Placement = pos=(117,19,0) rot=(0.57735,0.57735,0.57735;2.0944rad)
  sketch-geometry (8):
    g0: LineSegment StartX=-49.19 StartY=63.5 StartZ=0 EndX=-49.19 EndY=60.5 EndZ=0
    g1: LineSegment StartX=-49.19 StartY=11.5 StartZ=0 EndX=-49.19 EndY=8.5 EndZ=0
    g2: ArcOfCircle CenterX=-1.5 CenterY=62 CenterZ=0 NormalX=0 NormalY=0 NormalZ=1 AngleXU=0 Radius=1.5 StartAngle=4.71239 EndAngle=7.85398
    g3: ArcOfCircle CenterX=-1.5 CenterY=10 CenterZ=0 NormalX=0 NormalY=0 NormalZ=1 AngleXU=0 Radius=1.5 StartAngle=4.71239 EndAngle=7.85398
    g4: LineSegment StartX=-49.19 StartY=63.5 StartZ=0 EndX=-1.5 EndY=63.5 EndZ=0
    g5: LineSegment StartX=-49.19 StartY=60.5 StartZ=0 EndX=-1.5 EndY=60.5 EndZ=0
    g6: LineSegment StartX=-49.19 StartY=11.5 StartZ=0 EndX=-1.5 EndY=11.5 EndZ=0
    g7: LineSegment StartX=-49.19 StartY=8.5 StartZ=0 EndX=-1.5 EndY=8.5 EndZ=0
  constraints (19):
    c: Vertical(g0)
    c: Distance(g0) = 3
    c: Vertical(g1)
    c: Block(g1)
    c: Block(g2)
    c: Block(g3)
    c: Block(g0)
    c: Coincident(g4,g0)
    c: Coincident(g4,g2)
    c: Horizontal(g4)
    c: Coincident(g5,g0)
    c: Coincident(g5,g2)
    c: Horizontal(g5)
    c: Coincident(g6,g1)
    c: Coincident(g6,g3)
    c: Horizontal(g6)
    c: Coincident(g7,g1)
    c: Coincident(g7,g3)
    c: Horizontal(g7)
FEATURE [Part::Extrusion] Extrude071  label="sideB004"
  Base = -> Sketch079
  Dir = (0,0,1)
  DirMode = 2
  FaceMakerClass = Part::FaceMakerBullseye
  LengthFwd = 3
  LengthRev = 0
  Placement = pos=(0,0,71.7) rot=(0,0,1;0rad)
  Solid = true
  Symmetric = false
FEATURE [Part::MultiFuse] Fusion152  label="removeFromBottom004"
  Placement = pos=(2,0,0) rot=(0,0,1;0rad)
  Shapes = -> [Extrude070,Extrude071]
FEATURE [Part::Extrusion] Extrude072
  Base = -> Sketch081
  Dir = (1,0,0)
  DirMode = 2
  FaceMakerClass = Part::FaceMakerBullseye
  LengthFwd = 10
  LengthRev = 0
  Solid = true
  Symmetric = false
FEATURE [Part::Fillet] Fillet059  label="removeFromtMoreFrontCaseScrewRetainers004"
  Base = -> Extrude072
  Edges = 4 edges r=1.49: [Edge6,Edge11,Edge18,Edge23]
  Placement = pos=(-12,0,0) rot=(0,0,1;0rad)
FEATURE [Sketcher::SketchObject] Sketch082
  FullyConstrained = true
  Placement = pos=(117,19,0) rot=(0.57735,0.57735,0.57735;2.0944rad)
  sketch-geometry (8):
    g0: LineSegment StartX=-49.19 StartY=69.25 StartZ=0 EndX=-49.19 EndY=66.25 EndZ=0
    g1: LineSegment StartX=-49.19 StartY=5.75 StartZ=0 EndX=-49.19 EndY=2.75 EndZ=0
    g2: ArcOfCircle CenterX=-1.5 CenterY=67.75 CenterZ=0 NormalX=0 NormalY=0 NormalZ=1 AngleXU=0 Radius=1.5 StartAngle=4.71239 EndAngle=7.85398
    g3: ArcOfCircle CenterX=-1.5 CenterY=4.25 CenterZ=0 NormalX=0 NormalY=0 NormalZ=1 AngleXU=0 Radius=1.5 StartAngle=4.71239 EndAngle=7.85398
    g4: LineSegment StartX=-49.19 StartY=69.25 StartZ=0 EndX=-1.5 EndY=69.25 EndZ=0
    g5: LineSegment StartX=-49.19 StartY=66.25 StartZ=0 EndX=-1.5 EndY=66.25 EndZ=0
    g6: LineSegment StartX=-49.19 StartY=5.75 StartZ=0 EndX=-1.5 EndY=5.75 EndZ=0
    g7: LineSegment StartX=-49.19 StartY=2.75 StartZ=0 EndX=-1.5 EndY=2.75 EndZ=0
  constraints (19):
    c: Vertical(g0)
    c: Distance(g0) = 3
    c: Block(g0)
    c: Vertical(g1)
    c: Block(g2)
    c: Block(g3)
    c: Block(g1)
    c: Coincident(g4,g0)
    c: Coincident(g4,g2)
    c: Horizontal(g4)
    c: Coincident(g5,g0)
    c: Coincident(g5,g2)
    c: Horizontal(g5)
    c: Coincident(g6,g1)
    c: Coincident(g6,g3)
    c: Horizontal(g6)
    c: Coincident(g7,g1)
    c: Coincident(g7,g3)
    c: Horizontal(g7)
FEATURE [Part::Extrusion] Extrude073
  Base = -> Sketch082
  Dir = (1,0,0)
  DirMode = 2
  FaceMakerClass = Part::FaceMakerBullseye
  LengthFwd = 10
  LengthRev = 0
  Solid = true
  Symmetric = false
FEATURE [Part::Fillet] Fillet060  label="removeFromtMoreFrontCaseScrewRetainers005"
  Base = -> Extrude073
  Edges = 4 edges r=1.49: [Edge6,Edge11,Edge18,Edge23]
  Placement = pos=(-4,0,0) rot=(0,0,1;0rad)
FEATURE [Part::Revolution] Revolve163  label="backCaseScrewRetainer004"
  Angle = 360
  Axis = (0,1,0)
  Base = (0,0,0)
  FaceMakerClass = Part::FaceMakerBullseye
  Placement = pos=(12.5,3,62) rot=(0,0,1;0rad)
  Solid = false
  Source = -> Face149
  Symmetric = false
FEATURE [Part::Revolution] Revolve164  label="frontCaseScrewRetainer006"
  Angle = 360
  Axis = (0,1,0)
  Base = (0,0,0)
  FaceMakerClass = Part::FaceMakerBullseye
  Placement = pos=(89.5,3,68.5) rot=(0,0,1;0rad)
  Solid = false
  Source = -> Face151
  Symmetric = false
FEATURE [Part::Revolution] Revolve165  label="frontCaseScrewRetainer007"
  Angle = 360
  Axis = (0,1,0)
  Base = (0,0,0)
  FaceMakerClass = Part::FaceMakerBullseye
  Placement = pos=(89.5,3,3.5) rot=(0,0,1;0rad)
  Solid = false
  Source = -> Face152
  Symmetric = false
FEATURE [Part::Revolution] Revolve166  label="backCaseScrewRetainer005"
  Angle = 360
  Axis = (0,1,0)
  Base = (0,0,0)
  FaceMakerClass = Part::FaceMakerBullseye
  Placement = pos=(12.5,3,10) rot=(0,0,1;0rad)
  Solid = false
  Source = -> Face150
  Symmetric = false
FEATURE [Part::Revolution] Revolve167  label="moreFrontCaseScrewRetainer006"
  Angle = 360
  Axis = (0,1,0)
  Base = (0,0,0)
  FaceMakerClass = Part::FaceMakerBullseye
  Placement = pos=(109.5,4.5,68.5) rot=(0,0,1;0rad)
  Solid = false
  Source = -> Face153
  Symmetric = false
FEATURE [Part::Revolution] Revolve168  label="moreFrontCaseScrewRetainer007"
  Angle = 360
  Axis = (0,1,0)
  Base = (0,0,0)
  FaceMakerClass = Part::FaceMakerBullseye
  Placement = pos=(109.5,4.5,3.5) rot=(0,0,1;0rad)
  Solid = false
  Source = -> Face154
  Symmetric = false
FEATURE [Part::MultiFuse] Fusion151  label="screwRetainers003"
  Shapes = -> [Revolve168,Revolve167,Revolve166,Revolve165,Revolve164,Revolve163]
FEATURE [Part::Cut] Cut069  label="screwRetainers004"
  Base = -> Fusion151
  Tool = -> Fusion152
FEATURE [Part::Cut] Cut070
  Base = -> Cut069
  Tool = -> Fillet060
FEATURE [Part::Cut] Cut071  label="screwPillars001"
  Base = -> Cut070
  Tool = -> Fillet059
FEATURE [Part::MultiFuse] Fusion153  label="bottom024"
  Shapes = -> [Fusion149,Cut071]
FEATURE [Part::Cylinder] Cylinder067
  Angle = 360
  AttacherType = Attacher::AttachEngine3D
  Height = 10
  Placement = pos=(20.65,12,4.68) rot=(1,0,0;1.5708rad)
  Radius = 2
FEATURE [Part::Cylinder] Cylinder068
  Angle = 360
  AttacherType = Attacher::AttachEngine3D
  Height = 10
  Placement = pos=(20.65,12,67.38) rot=(1,0,0;1.5708rad)
  Radius = 2
FEATURE [Part::Cylinder] Cylinder069
  Angle = 360
  AttacherType = Attacher::AttachEngine3D
  Height = 10
  Placement = pos=(77.15,12,67.38) rot=(1,0,0;1.5708rad)
  Radius = 2
FEATURE [Part::Cylinder] Cylinder070
  Angle = 360
  AttacherType = Attacher::AttachEngine3D
  Height = 10
  Placement = pos=(77.15,12,4.68) rot=(1,0,0;1.5708rad)
  Radius = 2
FEATURE [Part::MultiFuse] Fusion154  label="removeFromThreadedInsertHousing001"
  Shapes = -> [Cylinder069,Cylinder068,Cylinder067,Cylinder070]
FEATURE [Part::Cut] Cut072  label="bottom025"
  Base = -> Fusion153
  Tool = -> Fusion154
FEATURE [Image::ImagePlane] ImagePlane
  XSize = 339
  YSize = 72
FEATURE [Sketcher::SketchObject] Sketch083
  FullyConstrained = true
  MapMode = 5
  Support = -> [XY_Plane]
  sketch-geometry (242):
    g0: LineSegment StartX=-151.619 StartY=28.8932 StartZ=0 EndX=-140.819 EndY=28.8932 EndZ=0
    g1: LineSegment StartX=-151.619 StartY=24.0313 StartZ=0 EndX=-151.619 EndY=28.8932 EndZ=0
    g2: LineSegment StartX=-140.819 StartY=17.7713 StartZ=0 EndX=-151.619 EndY=17.7713 EndZ=0
    g3: LineSegment StartX=-151.619 StartY=17.7713 StartZ=0 EndX=-151.619 EndY=22.6313 EndZ=0
    g4: LineSegment StartX=-151.619 StartY=22.6313 StartZ=0 EndX=-145.128 EndY=22.6313 EndZ=0
    g5: LineSegment StartX=-145.128 StartY=24.0313 StartZ=0 EndX=-140.819 EndY=28.8932 EndZ=0
    g6: LineSegment StartX=-145.128 StartY=22.6313 StartZ=0 EndX=-140.819 EndY=17.7713 EndZ=0
    g7: ArcOfCircle CenterX=-155.157 CenterY=23.3323 CenterZ=0 NormalX=0 NormalY=0 NormalZ=1 AngleXU=0 Radius=6.92354 StartAngle=1.03434 EndAngle=5.24885
    g8: ArcOfCircle CenterX=-155.157 CenterY=23.3323 CenterZ=0 NormalX=0 NormalY=0 NormalZ=1 AngleXU=0 Radius=12.6269 StartAngle=1.28675 EndAngle=4.99643
    g9: LineSegment StartX=-151.619 StartY=35.4532 StartZ=0 EndX=-151.619 EndY=29.2832 EndZ=0
    g10: LineSegment StartX=-151.619 StartY=17.3813 StartZ=0 EndX=-151.619 EndY=11.2113 EndZ=0
    g11-g21: Circle x11 (B-spline internal-alignment scaffolding for g22; pole/knot coordinates omitted)
    g22: BSplineCurve PolesCount=11 KnotsCount=9 Degree=3 IsPeriodic=0
    g23-g31: GeomPoint x9 (B-spline internal-alignment scaffolding for g22; pole/knot coordinates omitted)
    g32-g49: Circle x18 (B-spline internal-alignment scaffolding for g50; pole/knot coordinates omitted)
    g50: BSplineCurve PolesCount=18 KnotsCount=16 Degree=3 IsPeriodic=0
    g51-g66: GeomPoint x16 (B-spline internal-alignment scaffolding for g50; pole/knot coordinates omitted)
    g67: LineSegment StartX=-117.124 StartY=30.093 StartZ=0 EndX=-117.603 EndY=26.5272 EndZ=0
    g68: LineSegment StartX=-117.603 StartY=17.8472 StartZ=0 EndX=-117.124 EndY=14.2659 EndZ=0
    g69: Ellipse CenterX=-109.671 CenterY=20.025 CenterZ=0 NormalX=0 NormalY=0 NormalZ=1 MajorRadius=3.34798 MinorRadius=2.71052 AngleXU=-1.56793
    g70: GeomPoint X=-109.666 Y=18.0598 Z=0
    g71: GeomPoint X=-109.677 Y=21.9902 Z=0
    g72: Ellipse CenterX=-109.671 CenterY=20.0123 CenterZ=0 NormalX=0 NormalY=0 NormalZ=1 MajorRadius=6.93002 MinorRadius=6.36273 AngleXU=-3.13976
    g73: GeomPoint X=-112.417 Y=20.0073 Z=0
    g74: GeomPoint X=-106.925 Y=20.0173 Z=0
    g75: Ellipse CenterX=-51.7682 CenterY=20.1463 CenterZ=0 NormalX=0 NormalY=0 NormalZ=1 MajorRadius=3.19279 MinorRadius=2.71052 AngleXU=-1.52774
    g76: GeomPoint X=-51.6955 Y=18.4606 Z=0
    g77: GeomPoint X=-51.8408 Y=21.832 Z=0
    g78: GeomPoint X=-54.5142 Y=20.1413 Z=0
    g79: GeomPoint X=-49.0221 Y=20.1513 Z=0
    g80: Ellipse CenterX=-51.7682 CenterY=20.1463 CenterZ=0 NormalX=0 NormalY=0 NormalZ=1 MajorRadius=6.93002 MinorRadius=6.36273 AngleXU=-3.13976
    g81: Ellipse CenterX=-22.8436 CenterY=20.1783 CenterZ=0 NormalX=0 NormalY=0 NormalZ=1 MajorRadius=3.31512 MinorRadius=2.71052 AngleXU=-1.60214
    g82: GeomPoint X=-22.9034 Y=18.2706 Z=0
    g83: GeomPoint X=-22.7838 Y=22.0861 Z=0
    g84: GeomPoint X=-25.5897 Y=20.1733 Z=0
    g85: GeomPoint X=-20.0976 Y=20.1833 Z=0
    g86: Ellipse CenterX=-22.8436 CenterY=20.1783 CenterZ=0 NormalX=0 NormalY=0 NormalZ=1 MajorRadius=6.93002 MinorRadius=6.36273 AngleXU=-3.13976
    g87: LineSegment StartX=-101.889 StartY=14.1107 StartZ=0 EndX=-97.7455 EndY=14.1107 EndZ=0
    g88: LineSegment StartX=-93.8155 StartY=14.1107 StartZ=0 EndX=-89.6755 EndY=14.1107 EndZ=0
    g89: LineSegment StartX=-85.7455 StartY=14.1107 StartZ=0 EndX=-81.6055 EndY=14.1107 EndZ=0
    g90: LineSegment StartX=-101.889 StartY=14.1107 StartZ=0 EndX=-101.889 EndY=25.9907 EndZ=0
    g91: LineSegment StartX=-101.889 StartY=25.9907 StartZ=0 EndX=-97.8594 EndY=25.9907 EndZ=0
    g92: LineSegment StartX=-97.8594 StartY=25.9907 StartZ=0 EndX=-97.8594 EndY=24.0907 EndZ=0
    g93: LineSegment StartX=-97.7455 StartY=14.1107 StartZ=0 EndX=-97.7455 EndY=19.9107 EndZ=0
    g94: LineSegment StartX=-89.6755 StartY=14.1107 StartZ=0 EndX=-89.6755 EndY=19.9107 EndZ=0
    g95: LineSegment StartX=-93.8155 StartY=14.1107 StartZ=0 EndX=-93.8155 EndY=21.0107 EndZ=0
    g96-g106: Circle x11 (B-spline internal-alignment scaffolding for g107; pole/knot coordinates omitted)
    g107: BSplineCurve PolesCount=11 KnotsCount=9 Degree=3 IsPeriodic=0
    g108-g116: GeomPoint x9 (B-spline internal-alignment scaffolding for g107; pole/knot coordinates omitted)
    g117: BSplineCurve PolesCount=11 KnotsCount=9 Degree=3 IsPeriodic=0
    g118-g125: Circle x8 (B-spline internal-alignment scaffolding for g126; pole/knot coordinates omitted)
    g126: BSplineCurve PolesCount=8 KnotsCount=6 Degree=3 IsPeriodic=0
    g127-g132: GeomPoint x6 (B-spline internal-alignment scaffolding for g126; pole/knot coordinates omitted)
    g133: BSplineCurve PolesCount=8 KnotsCount=6 Degree=3 IsPeriodic=0
    g134: LineSegment StartX=-85.7455 StartY=21.0107 StartZ=0 EndX=-85.7455 EndY=14.1107 EndZ=0
    g135: LineSegment StartX=-80.0879 StartY=14.1107 StartZ=0 EndX=-75.944 EndY=14.1107 EndZ=0
    g136: LineSegment StartX=-72.014 StartY=14.1107 StartZ=0 EndX=-67.874 EndY=14.1107 EndZ=0
    g137: LineSegment StartX=-63.944 StartY=14.1107 StartZ=0 EndX=-59.804 EndY=14.1107 EndZ=0
    g138: LineSegment StartX=-80.0879 StartY=14.1107 StartZ=0 EndX=-80.0879 EndY=25.9907 EndZ=0
    g139: LineSegment StartX=-80.0879 StartY=25.9907 StartZ=0 EndX=-76.0579 EndY=25.9907 EndZ=0
    g140: LineSegment StartX=-76.0579 StartY=25.9907 StartZ=0 EndX=-76.0579 EndY=24.0907 EndZ=0
    g141: LineSegment StartX=-75.944 StartY=14.1107 StartZ=0 EndX=-75.944 EndY=19.9107 EndZ=0
    g142: LineSegment StartX=-67.874 StartY=14.1107 StartZ=0 EndX=-67.874 EndY=19.9107 EndZ=0
    g143: LineSegment StartX=-72.014 StartY=14.1107 StartZ=0 EndX=-72.014 EndY=21.0107 EndZ=0
    g144-g148: Circle x5 (B-spline internal-alignment scaffolding for g149; pole/knot coordinates omitted)
    g149: BSplineCurve PolesCount=11 KnotsCount=9 Degree=3 IsPeriodic=0
    g150-g158: GeomPoint x9 (B-spline internal-alignment scaffolding for g149; pole/knot coordinates omitted)
    g159: BSplineCurve PolesCount=11 KnotsCount=9 Degree=3 IsPeriodic=0
    g160-g167: Circle x8 (B-spline internal-alignment scaffolding for g168; pole/knot coordinates omitted)
    g168: BSplineCurve PolesCount=8 KnotsCount=6 Degree=3 IsPeriodic=0
    g169-g174: GeomPoint x6 (B-spline internal-alignment scaffolding for g168; pole/knot coordinates omitted)
    g175: BSplineCurve PolesCount=8 KnotsCount=6 Degree=3 IsPeriodic=0
    g176: LineSegment StartX=-63.944 StartY=21.0107 StartZ=0 EndX=-63.944 EndY=14.1107 EndZ=0
    g177: LineSegment StartX=-59.804 StartY=14.1107 StartZ=0 EndX=-59.804 EndY=21.5868 EndZ=0
    g178: BSplineCurve PolesCount=4 KnotsCount=2 Degree=3 IsPeriodic=0
    g179: GeomPoint X=-59.804 Y=21.5868 Z=0
    g180: GeomPoint X=-60.2379 Y=24.0907 Z=0
    g181: LineSegment StartX=-81.6055 StartY=14.1107 StartZ=0 EndX=-81.6055 EndY=21.5868 EndZ=0
    g182: LineSegment StartX=-151.619 StartY=24.0313 StartZ=0 EndX=-145.128 EndY=24.0313 EndZ=0
    g183: Circle CenterX=-82.0394 CenterY=24.0907 CenterZ=0 NormalX=0 NormalY=0 NormalZ=1 AngleXU=0 Radius=1
    g184: Circle CenterX=-81.7131 CenterY=23.2736 CenterZ=0 NormalX=0 NormalY=0 NormalZ=1 AngleXU=0 Radius=1
    g185: Circle CenterX=-81.6055 CenterY=21.5868 CenterZ=0 NormalX=0 NormalY=0 NormalZ=1 AngleXU=0 Radius=1
    g186: BSplineCurve PolesCount=3 KnotsCount=2 Degree=2 IsPeriodic=0
    g187: GeomPoint X=-82.0394 Y=24.0907 Z=0
    g188: GeomPoint X=-81.6055 Y=21.5868 Z=0
    g189: Ellipse CenterX=-37.3522 CenterY=19.9515 CenterZ=0 NormalX=0 NormalY=0 NormalZ=1 MajorRadius=2.99755 MinorRadius=2.49 AngleXU=1.5708
    g190: GeomPoint X=-37.3522 Y=21.6203 Z=0
    g191: GeomPoint X=-37.3522 Y=18.2826 Z=0
    g192: ArcOfEllipse CenterX=-38.7647 CenterY=20.06 CenterZ=0 NormalX=0 NormalY=0 NormalZ=1 MajorRadius=6.30025 MinorRadius=5.3849 AngleXU=1.57276 StartAngle=5.50632 EndAngle=10.3035
    g193: GeomPoint X=-38.7711 Y=23.3304 Z=0
    g194: GeomPoint X=-38.7583 Y=16.7895 Z=0
    g195: LineSegment StartX=-34.6109 StartY=14.1107 StartZ=0 EndX=-30.8984 EndY=14.1107 EndZ=0
    g196: LineSegment StartX=-30.8984 StartY=14.1107 StartZ=0 EndX=-30.8984 EndY=31.1784 EndZ=0
    g197: LineSegment StartX=-30.8984 StartY=31.1784 StartZ=0 EndX=-34.9984 EndY=31.1784 EndZ=0
    g198: LineSegment StartX=-34.9984 StartY=24.5602 StartZ=0 EndX=-34.9984 EndY=31.1784 EndZ=0
    g199: LineSegment StartX=-34.6109 StartY=16.0476 StartZ=0 EndX=-34.6109 EndY=14.1107 EndZ=0
    g200: LineSegment StartX=-14.8781 StartY=14.1107 StartZ=0 EndX=-10.5106 EndY=14.1107 EndZ=0
    g201: LineSegment StartX=-14.8781 StartY=14.1107 StartZ=0 EndX=-14.8781 EndY=25.8504 EndZ=0
    g202: LineSegment StartX=-14.8781 StartY=25.8504 StartZ=0 EndX=-10.8534 EndY=25.8504 EndZ=0
    g203: LineSegment StartX=-10.8534 StartY=25.8504 StartZ=0 EndX=-10.8534 EndY=24.0923 EndZ=0
    g204: LineSegment StartX=-10.5106 StartY=14.1107 StartZ=0 EndX=-10.5106 EndY=19.7752 EndZ=0
    g205: LineSegment StartX=-5.98735 StartY=25.9939 StartZ=0 EndX=-6.26019 EndY=22.6375 EndZ=0
    g206-g214: Circle x9 (B-spline internal-alignment scaffolding for g215; pole/knot coordinates omitted)
    g215: BSplineCurve PolesCount=9 KnotsCount=7 Degree=3 IsPeriodic=0
    g216-g222: GeomPoint x7 (B-spline internal-alignment scaffolding for g215; pole/knot coordinates omitted)
    g223-g232: Circle x10 (B-spline internal-alignment scaffolding for g233; pole/knot coordinates omitted)
    g233: BSplineCurve PolesCount=10 KnotsCount=8 Degree=3 IsPeriodic=0
    g234-g241: GeomPoint x8 (B-spline internal-alignment scaffolding for g233; pole/knot coordinates omitted)
  constraints (224):
    c: Coincident(g1,g0)
    c: Horizontal(g0)
    c: Vertical(g1)
    c: Coincident(g2,g3)
    c: Coincident(g3,g4)
    c: Horizontal(g4)
    c: Horizontal(g2)
    c: Vertical(g3)
    c: Block(g1)
    c: Distance(g3) = 4.86
    c: Block(g4)
    c: Distance(g0) = 10.8
    c: Distance(g2) = 10.8
    c: Coincident(g5,g0)
    c: Coincident(g6,g4)
    c: Coincident(g6,g2)
    c: Block(g8)
    c: Block(g7)
    c: Coincident(g9,g8)
    c: Coincident(g9,g7)
    c: Vertical(g9)
    c: Coincident(g10,g7)
    c: Coincident(g10,g8)
    c: Vertical(g10)
    c: Weight(g11) = 1
    c: Equal(g11, g12-g21) x10
    c: InternalAlignment(g11-g21 -> g22) x11
    c: InternalAlignment(g23-g31 -> g22) x9
    c: Block(g22)
    c: Weight(g32) = 1
    c: Equal(g32, g33-g49) x17
    c: InternalAlignment(g32-g49 -> g50) x18
    c: InternalAlignment(g51-g66 -> g50) x16
    c: Block(g50)
    c: Coincident(g67,g50)
    c: Coincident(g67,g22)
    c: Coincident(g68,g22)
    c: Coincident(g68,g50)
    c: InternalAlignment(g70,g69)
    c: InternalAlignment(g71,g69)
    c: Block(g69)
    c: InternalAlignment(g73,g72)
    c: InternalAlignment(g74,g72)
    c: Block(g72)
    c: InternalAlignment(g76,g75)
    c: InternalAlignment(g77,g75)
    c: InternalAlignment(g78,g80)
    c: InternalAlignment(g79,g80)
    c: Block(g80)
    c: Coincident(g75,g80)
    c: Block(g75)
    c: InternalAlignment(g82,g81)
    c: InternalAlignment(g83,g81)
    c: InternalAlignment(g84,g86)
    c: InternalAlignment(g85,g86)
    c: Block(g86)
    c: Coincident(g81,g86)
    c: Block(g81)
    c: Horizontal(g87)
    c: Block(g87)
    c: Horizontal(g88)
    c: Distance(g88) = 4.14
    c: Horizontal(g89)
    c: Equal(g88,g89) = 4.14
    c: Block(g89)
    c: Block(g88)
    c: Coincident(g90,g87)
    c: Vertical(g90)
    c: Distance(g90) = 11.88
    c: Coincident(g91,g90)
    c: Horizontal(g91)
    c: Coincident(g92,g91)
    c: Vertical(g92)
    c: Distance(g91) = 4.03
    c: Distance(g92) = 1.9
    c: Coincident(g93,g87)
    c: Vertical(g93)
    c: Vertical(g94)
    c: Coincident(g94,g88)
    c: Distance(g93) = 5.8
    c: Distance(g94) = 5.8
    c: Vertical(g95)
    c: Coincident(g95,g88)
    c: Distance(g95) = 6.9
    c: Coincident(g107,g92)
    c: Weight(g96) = 1
    c: Equal(g96, g97-g106) x10
    c: InternalAlignment(g96-g106 -> g107) x11
    c: InternalAlignment(g108-g116 -> g107) x9
    c: Block(g107)
    c: Block(g117)
    c: Coincident(g126,g93)
    c: Weight(g118) = 1
    c: Equal(g118, g119-g125) x7
    c: Coincident(g126,g95)
    c: InternalAlignment(g118-g125 -> g126) x8
    c: InternalAlignment(g127-g132 -> g126) x6
    c: Coincident(g133,g94)
    c: Block(g126)
    c: Block(g133)
    c: Coincident(g134,g133)
    c: Coincident(g134,g89)
    c: Vertical(g134)
    c: Horizontal(g135)
    c: Block(g135)
    c: Horizontal(g136)
    c: Equal(g88,g136) = 4.14
    c: Horizontal(g137)
    c: Equal(g136,g137) = 4.14
    c: Block(g137)
    c: Block(g136)
    c: Coincident(g138,g135)
    c: Vertical(g138)
    c: Equal(g90,g138) = 11.88
    c: Coincident(g139,g138)
    c: Horizontal(g139)
    c: Coincident(g140,g139)
    c: Vertical(g140)
    c: Equal(g91,g139) = 4.03
    c: Equal(g92,g140) = 1.9
    c: Coincident(g141,g135)
    c: Vertical(g141)
    c: Vertical(g142)
    c: Coincident(g142,g136)
    c: Equal(g93,g141) = 5.8
    c: Equal(g94,g142) = 5.8
    c: Vertical(g143)
    c: Coincident(g143,g136)
    c: Equal(g95,g143) = 6.9
    c: Coincident(g149,g140)
    c: Equal(g96,g144) = 1
    c: Equal(g144, g145-g148) x4
    c: InternalAlignment(g144-g148 -> g149) x5
    c: InternalAlignment(g150-g158 -> g149) x9
    c: Block(g149)
    c: Block(g159)
    c: Coincident(g168,g141)
    c: Equal(g118,g160) = 1
    c: Equal(g160, g161-g167) x7
    c: Coincident(g168,g143)
    c: InternalAlignment(g160-g167 -> g168) x8
    c: InternalAlignment(g169-g174 -> g168) x6
    c: Coincident(g175,g142)
    c: Block(g168)
    c: Block(g175)
    c: Coincident(g176,g175)
    c: Coincident(g176,g137)
    c: Vertical(g176)
    c: Coincident(g177,g137)
    c: Vertical(g177)
    c: Coincident(g178,g177)
    c: Coincident(g178,g159)
    c: InternalAlignment(g179,g178)
    c: InternalAlignment(g180,g178)
    c: Block(g178)
    c: Vertical(g181)
    c: Coincident(g181,g89)
    c: Block(g5)
    c: Coincident(g182,g1)
    c: Coincident(g182,g5)
    c: Horizontal(g182)
    c: Coincident(g186,g117)
    c: Weight(g183) = 1
    c: Equal(g183,g184)
    c: Equal(g183,g185)
    c: Coincident(g186,g181)
    c: InternalAlignment(g183,g186)
    c: InternalAlignment(g184,g186)
    c: InternalAlignment(g185,g186)
    c: InternalAlignment(g187,g186)
    c: InternalAlignment(g188,g186)
    c: Block(g186)
    c: InternalAlignment(g190,g189)
    c: InternalAlignment(g191,g189)
    c: Block(g189)
    c: InternalAlignment(g193,g192)
    c: InternalAlignment(g194,g192)
    c: Block(g192)
    c: Horizontal(g195)
    c: Block(g195)
    c: Coincident(g196,g195)
    c: Vertical(g196)
    c: Block(g196)
    c: Distance(g195) = 3.71244
    c: Coincident(g197,g196)
    c: Horizontal(g197)
    c: Distance(g197) = 4.1
    c: Coincident(g198,g192)
    c: Coincident(g198,g197)
    c: Vertical(g198)
    c: Block(g198)
    c: Coincident(g199,g192)
    c: Coincident(g199,g195)
    c: Vertical(g199)
    c: Block(g199)
    c: Horizontal(g200)
    c: Block(g200)
    c: Coincident(g201,g200)
    c: Vertical(g201)
    c: Block(g201)
    c: Coincident(g202,g201)
    c: Horizontal(g202)
    c: Block(g202)
    c: Coincident(g203,g202)
    c: Vertical(g203)
    c: Block(g203)
    c: Coincident(g204,g200)
    c: Vertical(g204)
    c: Block(g204)
    c: Block(g205)
    c: Coincident(g215,g203)
    c: Weight(g206) = 1
    c: Equal(g206, g207-g214) x8
    c: Coincident(g215,g205)
    c: InternalAlignment(g206-g214 -> g215) x9
    c: InternalAlignment(g216-g222 -> g215) x7
    c: Block(g215)
    c: Coincident(g233,g204)
    c: Weight(g223) = 1
    c: Equal(g223, g224-g232) x9
    c: Coincident(g233,g205)
    c: InternalAlignment(g223-g232 -> g233) x10
    c: InternalAlignment(g234-g241 -> g233) x8
    c: Block(g233)
FEATURE [PartDesign::Body] Body
  Group = -> [Sketch083]
  Origin = -> Origin
FEATURE [Sketcher::SketchObject] Sketch084
  FullyConstrained = true
  MapMode = 5
  Support = -> [XY_Plane001]
FEATURE [PartDesign::Body] Body001
  Group = -> [Sketch084]
  Origin = -> Origin001
